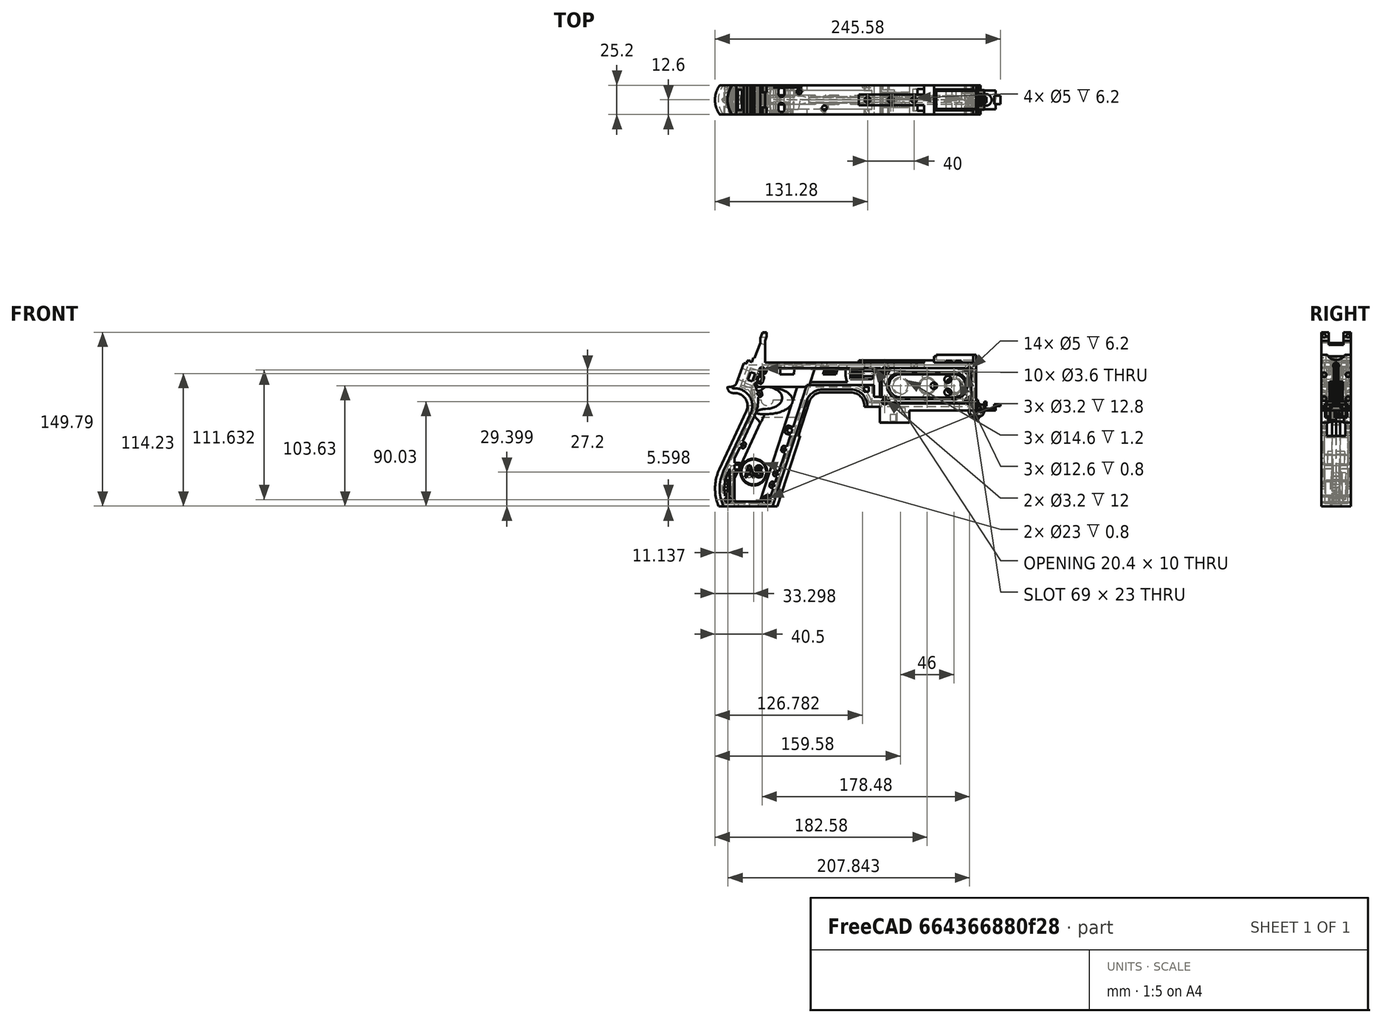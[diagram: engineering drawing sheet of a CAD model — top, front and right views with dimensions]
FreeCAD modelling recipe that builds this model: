
FCSTD DOCUMENT  (FreeCAD 1.0R39319 (Git))
Label: PICON-OF_ver_63
License: All rights reserved
LicenseURL: https://en.wikipedia.org/wiki/All_rights_reserved
objects: Sketcher::SketchObject×132, Part::Extrusion×66, Part::Cut×51, PartDesign::Pad×34, PartDesign::Pocket×21, PartDesign::Chamfer×15, PartDesign::Body×11, PartDesign::Fillet×6, Part::MultiFuse×5, Part::Part2DObjectPython×4, PartDesign::SubtractivePipe×4, PartDesign::SubtractiveLoft×4, PartDesign::Plane×3, PartDesign::SubShapeBinder×2, Part::Sweep×1, PartDesign::ShapeBinder×1, Mesh::Feature×1, PartDesign::Point×1, PartDesign::Groove×1
note: 664 computed .brp shape members not serialized (recipe doc carries the construction recipe); baked Part::Feature solids carry a one-line shape summary decoded from their .brp

FEATURE [Sketcher::SketchObject] Sketch  label="corpo principale"
  ArcFitTolerance = 1e-06
  AttacherType = Attacher::AttachEngine3D
  AttachmentSupport = -> [XZ_Plane]
  FullyConstrained = true
  MakeInternals = false
  MapMode = 5
  Placement = pos=(0,0,0) rot=(1,0,0;1.5708rad)
  sketch-geometry (65):
    g0: LineSegment StartX=0 StartY=0 StartZ=0 EndX=-57.2 EndY=0 EndZ=0
    g1: LineSegment StartX=-57.2 StartY=0 StartZ=0 EndX=-57.2 EndY=-10.4 EndZ=0
    g2: LineSegment StartX=-57.2 StartY=-10.4 StartZ=0 EndX=-82.8 EndY=-10.4 EndZ=0
    g3: LineSegment StartX=-82.8 StartY=-10.4 StartZ=0 EndX=-82.8 EndY=3.2 EndZ=0
    g4: LineSegment StartX=-82.8 StartY=3.2 StartZ=0 EndX=-93.6 EndY=3.2 EndZ=0
    g5: LineSegment StartX=-93.6 StartY=3.2 StartZ=0 EndX=-93.6 EndY=4 EndZ=0
    g6: LineSegment StartX=-107.6 StartY=18 StartZ=0 EndX=-132.428 EndY=18 EndZ=0
    g7: LineSegment StartX=-145.743 StartY=8.32624 StartZ=0 EndX=-175.232 EndY=-82.4316 EndZ=0
    g8: LineSegment StartX=-175.232 StartY=-82.4316 StartZ=0 EndX=-217.232 EndY=-82.4316 EndZ=0
    g9: LineSegment StartX=-217.232 StartY=-52.1862 StartZ=0 EndX=-193.988 EndY=-2.33927 EndZ=0
    g10: LineSegment StartX=-206.196 StartY=23.0857 StartZ=0 EndX=-199.861 EndY=40.4914 EndZ=0
    g11: LineSegment StartX=-199.861 StartY=40.4914 StartZ=0 EndX=-197.061 EndY=40.4914 EndZ=0
    g12: LineSegment StartX=-197.061 StartY=40.4914 StartZ=0 EndX=-197.061 EndY=42.8914 EndZ=0
    g13: LineSegment StartX=-197.061 StartY=42.8914 StartZ=0 EndX=-194.261 EndY=42.8914 EndZ=0
    g14: LineSegment StartX=-194.261 StartY=42.8914 StartZ=0 EndX=-194.535 EndY=42.1397 EndZ=0
    g15: LineSegment StartX=-194.535 StartY=42.1397 StartZ=0 EndX=-193.031 EndY=41.5924 EndZ=0
    g16: LineSegment StartX=-193.031 StartY=41.5924 StartZ=0 EndX=-191.663 EndY=45.3512 EndZ=0
    g17: LineSegment StartX=-191.663 StartY=45.3512 StartZ=0 EndX=-190.536 EndY=44.9408 EndZ=0
    g18: LineSegment StartX=-190.536 StartY=44.9408 StartZ=0 EndX=-185.747 EndY=58.0965 EndZ=0
    g19: LineSegment StartX=-185.747 StartY=58.0965 StartZ=0 EndX=-185.747 EndY=62.0965 EndZ=0
    g20: LineSegment StartX=-185.747 StartY=62.0965 StartZ=0 EndX=-183.832 EndY=67.3588 EndZ=0
    g21: LineSegment StartX=-183.832 StartY=67.3588 StartZ=0 EndX=-180.232 EndY=67.3588 EndZ=0
    g22: LineSegment StartX=-180.232 StartY=67.3588 StartZ=0 EndX=-180.232 EndY=63.7588 EndZ=0
    g23: LineSegment StartX=-180.232 StartY=63.7588 StartZ=0 EndX=-181.6 EndY=60 EndZ=0
    g24: LineSegment StartX=-181.6 StartY=60 StartZ=0 EndX=-181.6 EndY=41.2 EndZ=0
    g25: LineSegment StartX=-181.6 StartY=41.2 StartZ=0 EndX=-100.8 EndY=41.2 EndZ=0
    g26: LineSegment StartX=-36 StartY=43.2 StartZ=0 EndX=-36 EndY=41.2 EndZ=0
    g27: LineSegment StartX=0 StartY=48 StartZ=0 EndX=0 EndY=0 EndZ=0
    g28: LineSegment StartX=-209.901 StartY=19.85 StartZ=0 EndX=-209.901 EndY=20.1 EndZ=0
    g29: LineSegment StartX=-208.001 StartY=22 StartZ=0 EndX=-207.747 EndY=22 EndZ=0
    g30: LineSegment StartX=-207.583 StartY=19 StartZ=0 EndX=-209.051 EndY=19 EndZ=0
    g31: ArcOfCircle CenterX=-208.001 CenterY=20.1 CenterZ=0 NormalX=0 NormalY=0 NormalZ=1 AngleXU=0 Radius=1.9 StartAngle=1.5708 EndAngle=3.14159
    g32: GeomPoint [constr] X=-209.901 Y=22 Z=0
    g33: ArcOfCircle CenterX=-209.051 CenterY=19.85 CenterZ=0 NormalX=0 NormalY=0 NormalZ=1 AngleXU=0 Radius=0.85 StartAngle=3.14159 EndAngle=4.71239
    g34: GeomPoint [constr] X=-209.901 Y=19 Z=0
    g35: ArcOfCircle CenterX=-207.747 CenterY=23.65 CenterZ=0 NormalX=0 NormalY=0 NormalZ=1 AngleXU=0 Radius=1.65 StartAngle=4.71239 EndAngle=5.93412
    g36: GeomPoint [constr] X=-206.591 Y=22 Z=0
    g37: LineSegment StartX=-4 StartY=6 StartZ=0 EndX=-4 EndY=36.4 EndZ=0
    g38: LineSegment StartX=-4 StartY=36.4 StartZ=0 EndX=-185.2 EndY=36.4 EndZ=0
    g39: LineSegment StartX=-185.2 StartY=36.4 StartZ=0 EndX=-190.441 EndY=22 EndZ=0
    g40: LineSegment StartX=-214.575 StartY=-78.4316 StartZ=0 EndX=-178.142 EndY=-78.4316 EndZ=0
    g41: LineSegment StartX=-178.142 StartY=-78.4316 StartZ=0 EndX=-145.51 EndY=22 EndZ=0
    g42: LineSegment StartX=-145.51 StartY=22 StartZ=0 EndX=-87.91 EndY=22 EndZ=0
    g43: LineSegment StartX=-87.91 StartY=22 StartZ=0 EndX=-87.91 EndY=11.6 EndZ=0
    g44: LineSegment StartX=-87.91 StartY=11.6 StartZ=0 EndX=-80.11 EndY=11.6 EndZ=0
    g45: LineSegment StartX=-80.11 StartY=11.6 StartZ=0 EndX=-80.11 EndY=6 EndZ=0
    g46: LineSegment StartX=-80.11 StartY=6 StartZ=0 EndX=-4 EndY=6 EndZ=0
    g47: LineSegment StartX=-190.363 StartY=-4.02975 StartZ=0 EndX=-213.607 EndY=-53.8767 EndZ=0
    g48: ArcOfCircle CenterX=-132.428 CenterY=4 CenterZ=0 NormalX=0 NormalY=0 NormalZ=1 AngleXU=0 Radius=14 StartAngle=1.5708 EndAngle=2.82743
    g49: GeomPoint [constr] X=-142.6 Y=18 Z=0
    g50: ArcOfCircle CenterX=-107.6 CenterY=4 CenterZ=0 NormalX=0 NormalY=0 NormalZ=1 AngleXU=0 Radius=14 StartAngle=0 EndAngle=1.5708
    g51: GeomPoint [constr] X=-93.6 Y=18 Z=0
    g52: ArcOfCircle CenterX=-184.801 CenterY=-67.3089 CenterZ=0 NormalX=0 NormalY=0 NormalZ=1 AngleXU=0 Radius=35.7833 StartAngle=2.70526 EndAngle=3.57792
    g53: ArcOfCircle CenterX=-207.583 CenterY=4 CenterZ=0 NormalX=0 NormalY=0 NormalZ=1 AngleXU=0 Radius=15 StartAngle=5.84685 EndAngle=7.85398
    g54: LineSegment [constr] StartX=-213.607 StartY=-53.8767 StartZ=0 EndX=-217.232 EndY=-52.1862 EndZ=0
    g55: ArcOfCircle CenterX=-184.801 CenterY=-67.3089 CenterZ=0 NormalX=0 NormalY=0 NormalZ=1 AngleXU=0 Radius=31.7833 StartAngle=2.70526 EndAngle=3.49911
    g56: ArcOfCircle CenterX=-218.095 CenterY=8.90192 CenterZ=0 NormalX=0 NormalY=0 NormalZ=1 AngleXU=0 Radius=30.5989 StartAngle=5.84685 EndAngle=6.72553
    g57: LineSegment StartX=-44.6 StartY=43.2 StartZ=0 EndX=-36 EndY=43.2 EndZ=0
    g58: LineSegment StartX=-100.8 StartY=41.2 StartZ=0 EndX=-44.6 EndY=41.2 EndZ=0
    g59: LineSegment StartX=-44.6 StartY=41.2 StartZ=0 EndX=-44.6 EndY=43.2 EndZ=0
    g60: LineSegment StartX=-2.4 StartY=48 StartZ=0 EndX=0 EndY=48 EndZ=0
    g61: LineSegment StartX=-36 StartY=41.2 StartZ=0 EndX=-2.4 EndY=41.2 EndZ=0
    g62: LineSegment StartX=-2.4 StartY=41.2 StartZ=0 EndX=-2.4 EndY=48 EndZ=0
    g63: LineSegment [constr] StartX=-181.6 StartY=36.4 StartZ=0 EndX=-152.209 EndY=36.4 EndZ=0
    g64: LineSegment [constr] StartX=-181.6 StartY=36.4 StartZ=0 EndX=-130.41 EndY=36.4 EndZ=0
  constraints (183):
    c: Coincident(g-1,g0)
    c: PointOnObject(g0,g-1)
    c: Coincident(g0,g1)
    c: Vertical(g1)
    c: Coincident(g1,g2)
    c: Horizontal(g2)
    c: Coincident(g2,g3)
    c: Vertical(g3)
    c: Coincident(g3,g4)
    c: Coincident(g4,g5)
    c: Vertical(g5)
    c: Horizontal(g6)
    c: Coincident(g7,g8)
    c: Horizontal(g8)
    c: Coincident(g10,g11)
    c: Horizontal(g11)
    c: Coincident(g11,g12)
    c: Vertical(g12)
    c: Coincident(g12,g13)
    c: Horizontal(g13)
    c: Coincident(g13,g14)
    c: Coincident(g14,g15)
    c: Coincident(g15,g16)
    c: Coincident(g16,g17)
    c: Coincident(g17,g18)
    c: Coincident(g18,g19)
    c: Vertical(g19)
    c: Coincident(g19,g20)
    c: Coincident(g20,g21)
    c: Horizontal(g21)
    c: Coincident(g21,g22)
    c: Vertical(g22)
    c: Coincident(g22,g23)
    c: Coincident(g23,g24)
    c: Vertical(g24)
    c: Coincident(g24,g25)
    c: Horizontal(g25)
    c: Coincident(g57,g26)
    c: Vertical(g26)
    c: Coincident(g26,g61)
    c: PointOnObject(g60,g-2)
    c: Coincident(g60,g27)
    c: Coincident(g27,g0)
    c: DistanceY(g27,g27) = 48
    c: DistanceY(g1,g1) = 10.4
    c: DistanceX(g0,g0) = 57.2
    c: DistanceX(g2,g2) = 25.6
    c: Horizontal(g4)
    c: DistanceY(g3,g3) = 13.6
    c: DistanceX(g4,g4) = 10.8
    c: DistanceY(g5,g51) = 14.8
    c: DistanceX(g49,g51) = 49
    c: Distance(g7,g49) = 105.6
    c: DistanceX(g61,g60) = 36
    c: DistanceX(g25,g25) = 80.8
    c: DistanceY(g24,g24) = 18.8
    c: DistanceY(g22,g22) = 3.6
    c: Distance(g23) = 4
    c: Angle(g-1,g23) = 1.22173
    c: DistanceX(g21,g21) = 3.6
    c: Distance(g20) = 5.6
    c: Angle(g-1,g20) = 1.22173
    c: DistanceY(g19,g19) = 4
    c: Distance(g18) = 14
    c: Angle(g-1,g18) = 1.22173
    c: Distance(g17) = 1.2
    c: Distance(g16) = 4
    c: Angle(g16) = 1.22173
    c: Perpendicular(g18,g17)
    c: Distance(g15) = 1.6
    c: Perpendicular(g16,g15)
    c: Distance(g14) = 0.8
    c: DistanceX(g13,g13) = 2.8
    c: Perpendicular(g15,g14)
    c: DistanceY(g12,g12) = 2.4
    c: DistanceX(g11,g11) = 2.8
    c: Distance(g9) = 55
    c: Angle(g9,g-1) = 2.00713
    c: Horizontal(g29)
    c: Vertical(g28)
    c: Horizontal(g30)
    c: PointOnObject(g32,g29)
    c: PointOnObject(g32,g28)
    c: Tangent(g29,g31) = 1.5708
    c: Tangent(g28,g31) = 1.5708
    c: PointOnObject(g34,g28)
    c: PointOnObject(g34,g30)
    c: Tangent(g28,g33) = 1.5708
    c: Tangent(g30,g33) = 1.5708
    c: PointOnObject(g36,g29)
    c: PointOnObject(g36,g10)
    c: Tangent(g29,g35) = -1.5708
    c: Tangent(g10,g35) = -1.5708
    c: Angle(g-1,g10) = 1.22173
    c: Radius(g35) = 1.65
    c: Vertical(g37)
    c: Coincident(g37,g38)
    c: Horizontal(g38)
    c: Coincident(g38,g39)
    c: Horizontal(g40)
    c: Coincident(g40,g41)
    c: Coincident(g41,g42)
    c: Horizontal(g42)
    c: Coincident(g42,g43)
    c: Vertical(g43)
    c: Coincident(g43,g44)
    c: Horizontal(g44)
    c: Coincident(g44,g45)
    c: Vertical(g45)
    c: Coincident(g45,g46)
    c: Coincident(g46,g37)
    c: Horizontal(g46)
    c: DistanceY(g0,g37) = 6
    c: DistanceX(g37,g0) = 4
    c: DistanceY(g37,g25) = 4.8
    c: DistanceX(g38,g38) = 181.2
    c: DistanceX(g42,g42) = 57.6
    c: DistanceY(g49,g41) = 4
    c: DistanceX(g41,g49) = 2.91
    c: DistanceY(g43,g43) = 10.4
    c: DistanceX(g44,g44) = 7.8
    c: DistanceY(g7,g40) = 4
    c: Distance(g47) = 55
    c: Angle(g-1,g39) = 1.22173
    c: PointOnObject(g49,g7)
    c: PointOnObject(g49,g6)
    c: Tangent(g7,g48) = -1.5708
    c: Tangent(g6,g48) = -1.5708
    c: PointOnObject(g51,g5)
    c: PointOnObject(g51,g6)
    c: Tangent(g5,g50) = -1.5708
    c: Tangent(g6,g50) = -1.5708
    c: Radius(g50) = 14
    c: Radius(g48) = 14
    c: DistanceX(g8,g8) = 42
    c: Angle(g7,g-1) = 1.88496
    c: Parallel(g41,g7)
    c: Parallel(g47,g9)
    c: Coincident(g52,g8)
    c: Tangent(g52,g9) = 1.5708
    c: DistanceX(g9,g8) = 0
    c: Tangent(g53,g9) = -1.5708
    c: Tangent(g53,g30) = -1.5708
    c: Diameter(g53) = 30
    c: DistanceY(g53,g0) = -4
    c: Coincident(g54,g47)
    c: Distance(g54) = 4
    c: Coincident(g54,g9)
    c: Coincident(g55,g40)
    c: Tangent(g55,g47) = -1.5708
    c: Coincident(g52,g55)
    c: Coincident(g56,g39)
    c: Tangent(g56,g47) = 1.5708
    c: Horizontal(g57)
    c: DistanceX(g57,g57) = 8.6
    c: Coincident(g58,g25)
    c: Horizontal(g58)
    c: Coincident(g59,g58)
    c: Vertical(g59)
    c: DistanceY(g58,g57) = 2
    c: DistanceX(g58,g58) = 56.2
    c: Coincident(g59,g57)
    c: DistanceY(g41,g36) = 0
    c: DistanceY(g36,g39) = 0
    c: DistanceY(g28,g28) = 0.25
    c: DistanceX(g30,g36) = 2.46
    c: DistanceX(g28,g29) = 1.9
    c: Coincident(g62,g60)
    c: Horizontal(g60)
    c: DistanceX(g62,g27) = 2.4
    c: Coincident(g61,g62)
    c: DistanceY(g26,g26) = 2
    c: Vertical(g62)
    c: DistanceY(g61,g60) = 6.8
    c: Horizontal(g61)
    c: Distance(g63) = 29.391
    c: PointOnObject(g63,g38)
    c: PointOnObject(g63,g38)
    c: Distance(g64) = 51.19
    c: PointOnObject(g64,g38)
    c: PointOnObject(g64,g38)
    c: DistanceX(g24,g63) = 0
    c: DistanceX(g24,g64) = 0
FEATURE [Part::Extrusion] Extrude  label="Extrude corpo principale"
  Base = -> Sketch
  Dir = (0,-1,2e-16)
  DirMode = 2
  FaceMakerClass = Part::FaceMakerBullseye
  FaceMakerMode = 3
  LengthFwd = 25.2
  LengthRev = 12.6
  Solid = true
  Symmetric = true
FEATURE [Sketcher::SketchObject] Sketch002  label="scavo grilletto"
  ArcFitTolerance = 1e-06
  AttachmentSupport = -> [XZ_Plane]
  ExternalGeometry = -> [Sketch]
  FullyConstrained = true
  MakeInternals = false
  MapMode = 5
  Placement = pos=(0,0,0) rot=(1,0,0;1.5708rad)
  sketch-geometry (4):
    g0: LineSegment StartX=-89.51 StartY=22 StartZ=0 EndX=-152.71 EndY=22 EndZ=0
    g1: LineSegment StartX=-152.71 StartY=22 StartZ=0 EndX=-167.006 EndY=-22 EndZ=0
    g2: LineSegment StartX=-167.006 StartY=-22 StartZ=0 EndX=-89.51 EndY=-22 EndZ=0
    g3: LineSegment StartX=-89.51 StartY=-22 StartZ=0 EndX=-89.51 EndY=22 EndZ=0
  constraints (12):
    c: Horizontal(g0)
    c: Coincident(g0,g1)
    c: Coincident(g1,g2)
    c: Horizontal(g2)
    c: Coincident(g2,g3)
    c: Coincident(g3,g0)
    c: Vertical(g3)
    c: Angle(g1,g0) = 1.88496
    c: DistanceY(g3,g3) = 44
    c: DistanceX(g0,g0) = 63.2
    c: DistanceX(g0,g-3) = 1.6
    c: DistanceY(g-3,g0) = 0
FEATURE [Sketcher::SketchObject] Sketch004  label="traiettoria arrotondamento impugnatura anteriore"
  ArcFitTolerance = 1e-06
  AttachmentSupport = -> [XZ_Plane]
  ExternalGeometry = -> [Sketch]
  FullyConstrained = true
  MakeInternals = false
  MapMode = 5
  Placement = pos=(0,0,0) rot=(1,0,0;1.5708rad)
  sketch-geometry (13):
    g0: LineSegment StartX=-175.232 StartY=-82.4316 StartZ=0 EndX=-145.743 EndY=8.32624 EndZ=0
    g1: LineSegment StartX=-93.6 StartY=3.2 StartZ=0 EndX=-93.6 EndY=4 EndZ=0
    g2: LineSegment StartX=-132.428 StartY=18 StartZ=0 EndX=-107.6 EndY=18 EndZ=0
    g3: ArcOfCircle CenterX=-132.428 CenterY=4 CenterZ=0 NormalX=0 NormalY=0 NormalZ=1 AngleXU=0 Radius=14 StartAngle=1.5708 EndAngle=2.82743
    g4: ArcOfCircle CenterX=-107.6 CenterY=4 CenterZ=0 NormalX=0 NormalY=0 NormalZ=1 AngleXU=0 Radius=14 StartAngle=0 EndAngle=1.5708
    g5: LineSegment StartX=-175.232 StartY=-82.4316 StartZ=0 EndX=-217.232 EndY=-82.4316 EndZ=0
    g6: LineSegment StartX=-217.232 StartY=-52.1862 StartZ=0 EndX=-193.988 EndY=-2.33927 EndZ=0
    g7: LineSegment StartX=-209.051 StartY=19 StartZ=0 EndX=-207.583 EndY=19 EndZ=0
    g8: LineSegment StartX=-209.901 StartY=20.1 StartZ=0 EndX=-209.901 EndY=19.85 EndZ=0
    g9: ArcOfCircle CenterX=-184.801 CenterY=-67.3089 CenterZ=0 NormalX=0 NormalY=0 NormalZ=1 AngleXU=0 Radius=35.7833 StartAngle=2.70526 EndAngle=3.57792
    g10: ArcOfCircle CenterX=-207.583 CenterY=4 CenterZ=0 NormalX=0 NormalY=0 NormalZ=1 AngleXU=0 Radius=15 StartAngle=5.84685 EndAngle=7.85398
    g11: ArcOfCircle CenterX=-209.051 CenterY=19.85 CenterZ=0 NormalX=0 NormalY=0 NormalZ=1 AngleXU=0 Radius=0.85 StartAngle=3.14159 EndAngle=4.71239
    g12: ArcOfCircle CenterX=-208.001 CenterY=20.1 CenterZ=0 NormalX=0 NormalY=0 NormalZ=1 AngleXU=0 Radius=1.9 StartAngle=1.5708 EndAngle=3.14159
  constraints (26):
    c: Coincident(g0,g-3)
    c: Coincident(g0,g-6)
    c: Coincident(g1,g-8)
    c: Coincident(g1,g-7)
    c: Coincident(g2,g-5)
    c: Coincident(g2,g-4)
    c: Coincident(g3,g2)
    c: Tangent(g3,g0) = 1.5708
    c: Coincident(g4,g1)
    c: Tangent(g4,g2) = 1.5708
    c: Coincident(g5,g0)
    c: Coincident(g5,g-9)
    c: Coincident(g6,g-12)
    c: Coincident(g6,g-11)
    c: Coincident(g7,g-15)
    c: Coincident(g7,g-14)
    c: Coincident(g8,g-16)
    c: Coincident(g8,g-17)
    c: Tangent(g9,g6) = 1.5708
    c: Coincident(g9,g5)
    c: Coincident(g10,g7)
    c: Tangent(g10,g6) = -1.5708
    c: Tangent(g11,g7) = -1.5708
    c: Coincident(g11,g8)
    c: Tangent(g12,g8) = -1.5708
    c: Coincident(g12,g-17)
FEATURE [PartDesign::Plane] DatumPlane  label="Piano per disegno arrotondamento impugnatura"
  AttachmentSupport = -> [Sketch]
  Length = 73.6581
  MapMode = 7
  Placement = pos=(-145.743,1.8e-15,8.32624) rot=(0.154555,0.154555,0.97582;1.59527rad)
  ResizeMode = 0
  Width = 303.511
FEATURE [Sketcher::SketchObject] Sketch005  label="forma arrotondamento impugnatura anteriore"
  ArcFitTolerance = 1e-06
  AttachmentSupport = -> [DatumPlane]
  FullyConstrained = true
  MakeInternals = false
  MapMode = 5
  Placement = pos=(-145.743,1.8e-15,8.32624) rot=(0.154555,0.154555,0.97582;1.59527rad)
  sketch-geometry (5):
    g0: GeomPoint [constr] X=0 Y=-4 Z=0
    g1: GeomPoint [constr] X=-12.6 Y=7.1e-15 Z=0
    g2: GeomPoint [constr] X=12.6 Y=4.97e-14 Z=0
    g3: LineSegment StartX=-12.6 StartY=7.1e-15 StartZ=0 EndX=12.6 EndY=4.97e-14 EndZ=0
    g4: ArcOfCircle CenterX=-3.88e-14 CenterY=17.845 CenterZ=0 NormalX=0 NormalY=0 NormalZ=1 AngleXU=0 Radius=21.845 StartAngle=4.09759 EndAngle=5.32718
  constraints (11):
    c: DistanceY(g0,g-1) = 4
    c: DistanceX(g-1,g0) = 0
    c: DistanceX(g1,g-1) = 12.6
    c: DistanceX(g-1,g2) = 12.6
    c: DistanceY(g-1,g2) = 0
    c: DistanceY(g-1,g1) = 0
    c: Coincident(g3,g1)
    c: Coincident(g3,g2)
    c: Coincident(g4,g1)
    c: Coincident(g4,g2)
    c: PointOnObject(g0,g4)
FEATURE [Part::Sweep] Sweep  label="Sweep impugnatura"
  Frenet = true
  Sections = -> [Sketch005]
  Solid = true
  Spine = -> Sketch [Edge32,Edge33,Edge34,Edge35,Edge36,Edge37,Edge38,Edge39,Edge40,Edge41,Edge42,Edge43,Edge44]
  Transition = 1
FEATURE [Sketcher::SketchObject] Sketch008  label="buchi e pulizie varie"
  ArcFitTolerance = 1e-06
  AttachmentSupport = -> [XZ_Plane]
  ExternalGeometry = -> [Sketch]
  FullyConstrained = true
  MakeInternals = false
  MapMode = 5
  Placement = pos=(0,0,0) rot=(1,0,0;1.5708rad)
  sketch-geometry (26):
    g0: LineSegment StartX=-96.278 StartY=20.155 StartZ=0 EndX=-92.278 EndY=20.155 EndZ=0
    g1: LineSegment StartX=-92.278 StartY=20.155 StartZ=0 EndX=-92.278 EndY=16.155 EndZ=0
    g2: LineSegment StartX=-92.278 StartY=16.155 StartZ=0 EndX=-96.278 EndY=16.155 EndZ=0
    g3: LineSegment StartX=-96.278 StartY=16.155 StartZ=0 EndX=-96.278 EndY=20.155 EndZ=0
    g4: LineSegment StartX=-222.232 StartY=-82.4316 StartZ=0 EndX=-170.232 EndY=-82.4316 EndZ=0
    g5: LineSegment StartX=-170.232 StartY=-82.4316 StartZ=0 EndX=-170.232 EndY=-86.4316 EndZ=0
    g6: LineSegment StartX=-170.232 StartY=-86.4316 StartZ=0 EndX=-222.232 EndY=-86.4316 EndZ=0
    g7: LineSegment StartX=-222.232 StartY=-86.4316 StartZ=0 EndX=-222.232 EndY=-82.4316 EndZ=0
    g8: LineSegment StartX=-213.901 StartY=20.1 StartZ=0 EndX=-213.901 EndY=26 EndZ=0
    g9: LineSegment StartX=-213.901 StartY=26 StartZ=0 EndX=-206.196 EndY=26 EndZ=0
    g10: LineSegment StartX=-17.4 StartY=42.8 StartZ=0 EndX=-12.4 EndY=42.8 EndZ=0
    g11: LineSegment StartX=-12.4 StartY=42.8 StartZ=0 EndX=-12.4 EndY=41.2 EndZ=0
    g12: LineSegment StartX=-12.4 StartY=41.2 StartZ=0 EndX=-17.4 EndY=41.2 EndZ=0
    g13: LineSegment StartX=-17.4 StartY=41.2 StartZ=0 EndX=-17.4 EndY=42.8 EndZ=0
    g14: LineSegment StartX=-25.9 StartY=42.8 StartZ=0 EndX=-20.9 EndY=42.8 EndZ=0
    g15: LineSegment StartX=-20.9 StartY=42.8 StartZ=0 EndX=-20.9 EndY=41.2 EndZ=0
    g16: LineSegment StartX=-20.9 StartY=41.2 StartZ=0 EndX=-25.9 EndY=41.2 EndZ=0
    g17: LineSegment StartX=-25.9 StartY=41.2 StartZ=0 EndX=-25.9 EndY=42.8 EndZ=0
    g18: GeomPoint [constr] X=-206.196 Y=23.0857 Z=0
    g19: GeomPoint [constr] X=-213.901 Y=20.1 Z=0
    g20: BSplineCurve PolesCount=4 KnotsCount=2 Degree=3 IsPeriodic=0
    g21-g24: Circle [constr] x4 (B-spline internal-alignment scaffolding for g20; pole/knot coordinates omitted)
    g25: LineSegment StartX=-206.196 StartY=26 StartZ=0 EndX=-206.196 EndY=23.0857 EndZ=0
  constraints (73):
    c: Horizontal(g0)
    c: Coincident(g1,g0)
    c: Vertical(g1)
    c: Coincident(g2,g1)
    c: Horizontal(g2)
    c: Coincident(g3,g2)
    c: Coincident(g3,g0)
    c: Vertical(g3)
    c: DistanceX(g0,g-4) = 4.368
    c: DistanceY(g0,g-4) = 1.845
    c: DistanceY(g1,g1) = 4
    c: DistanceX(g2,g2) = 4
    c: Horizontal(g4)
    c: Coincident(g5,g4)
    c: Vertical(g5)
    c: Coincident(g6,g5)
    c: Horizontal(g6)
    c: Coincident(g7,g6)
    c: Coincident(g7,g4)
    c: Vertical(g7)
    c: DistanceY(g7,g7) = 4
    c: DistanceX(g4,g-5) = 5
    c: DistanceX(g-5,g4) = 5
    c: DistanceY(g4,g-5) = 0
    c: Coincident(g9,g8)
    c: Parallel(g9,g-6)
    c: DistanceX(g8,g-8) = 4
    c: Horizontal(g10)
    c: Coincident(g11,g10)
    c: Vertical(g11)
    c: Coincident(g12,g11)
    c: Horizontal(g12)
    c: Coincident(g13,g12)
    c: Coincident(g13,g10)
    c: Vertical(g13)
    c: Horizontal(g14)
    c: Coincident(g15,g14)
    c: Vertical(g15)
    c: Coincident(g16,g15)
    c: Horizontal(g16)
    c: Coincident(g17,g16)
    c: Coincident(g17,g14)
    c: Vertical(g17)
    c: DistanceY(g11,g10) = 1.6
    c: DistanceX(g10,g10) = 5
    c: DistanceY(g15,g14) = 1.6
    c: DistanceX(g14,g14) = 5
    c: DistanceX(g15,g12) = 3.5
    c: DistanceX(g11,g-9) = 10
    c: DistanceY(g-9,g11) = 0
    c: DistanceY(g-9,g15) = 0
    c: Perpendicular(g8,g9)
    c: DistanceY(g-7,g9) = 4
    c: DistanceY(g8,g-8) = 0
    c: InternalAlignment(g18,g20)
    c: InternalAlignment(g19,g20)
    c: InternalAlignment(g21,g20)
    c: Weight(g21) = 1
    c: InternalAlignment(g22,g20)
    c: Equal(g22,g21)
    c: InternalAlignment(g23,g20)
    c: Equal(g23,g21)
    c: InternalAlignment(g24,g20)
    c: Equal(g24,g21)
    c: Coincident(g18,g-12)
    c: Coincident(g19,g8)
    c: Coincident(g25,g9)
    c: Coincident(g25,g20)
    c: Vertical(g25)
    c: DistanceY(g20,g23) = 0
    c: DistanceY(g22,g18) = 2.26
    c: DistanceX(g22,g18) = 0.93
    c: DistanceX(g20,g23) = 2.9
FEATURE [Part::Extrusion] Extrude004  label="Extrude Buchi e pulizie varie"
  Base = -> Sketch008
  Dir = (0,-1,2e-16)
  DirMode = 2
  FaceMakerClass = Part::FaceMakerBullseye
  FaceMakerMode = 3
  LengthFwd = 25.2
  LengthRev = 0
  Solid = true
  Symmetric = true
FEATURE [Sketcher::SketchObject] Sketch009  label="rinforzi"
  ArcFitTolerance = 1e-06
  AttachmentSupport = -> [XZ_Plane]
  ExternalGeometry = -> [Sketch]
  FullyConstrained = true
  MakeInternals = false
  MapMode = 5
  Placement = pos=(0,0,0) rot=(1,0,0;1.5708rad)
  sketch-geometry (9):
    g0: LineSegment StartX=-87.91 StartY=22 StartZ=0 EndX=-87.91 EndY=36.4 EndZ=0
    g1: LineSegment StartX=-87.91 StartY=36.4 StartZ=0 EndX=-97.91 EndY=36.4 EndZ=0
    g2: LineSegment StartX=-97.91 StartY=36.4 StartZ=0 EndX=-97.91 EndY=22 EndZ=0
    g3: LineSegment StartX=-97.91 StartY=22 StartZ=0 EndX=-87.91 EndY=22 EndZ=0
    g4: LineSegment StartX=-149.713 StartY=9.06563 StartZ=0 EndX=-154.586 EndY=-5.93437 EndZ=0
    g5: LineSegment StartX=-154.586 StartY=-5.93437 StartZ=0 EndX=-191.863 EndY=-5.93437 EndZ=0
    g6: LineSegment StartX=-191.863 StartY=-5.93437 StartZ=0 EndX=-191.863 EndY=9.06563 EndZ=0
    g7: LineSegment StartX=-191.863 StartY=9.06563 StartZ=0 EndX=-149.713 EndY=9.06563 EndZ=0
    g8: LineSegment [constr] StartX=-145.51 StartY=22 StartZ=0 EndX=-149.713 EndY=9.06563 EndZ=0
  constraints (25):
    c: Vertical(g0)
    c: Coincident(g1,g0)
    c: Horizontal(g1)
    c: Coincident(g2,g1)
    c: Vertical(g2)
    c: Coincident(g3,g2)
    c: Coincident(g3,g0)
    c: Horizontal(g3)
    c: Coincident(g0,g-4)
    c: DistanceX(g3,g3) = 10
    c: DistanceY(g0,g-3) = 0
    c: Coincident(g5,g4)
    c: Horizontal(g5)
    c: Coincident(g6,g5)
    c: Vertical(g6)
    c: Coincident(g7,g6)
    c: Coincident(g7,g4)
    c: Horizontal(g7)
    c: Distance(g8) = 13.6
    c: Parallel(g-6,g8)
    c: Coincident(g-6,g8)
    c: Parallel(g4,g-6)
    c: DistanceY(g4,g4) = 15
    c: Coincident(g4,g8)
    c: DistanceX(g-5,g5) = -1.5
FEATURE [Part::Extrusion] Extrude001  label="Extrude scavo grilletto"
  Base = -> Sketch002
  Dir = (0,-1,2e-16)
  DirMode = 2
  FaceMakerClass = Part::FaceMakerBullseye
  FaceMakerMode = 3
  LengthFwd = 16
  LengthRev = 0
  Solid = true
  Symmetric = true
FEATURE [Part::Extrusion] Extrude005  label="Extrude Rinforzi"
  Base = -> Sketch009
  Dir = (0,-1,2e-16)
  DirMode = 2
  FaceMakerClass = Part::FaceMakerBullseye
  FaceMakerMode = 3
  LengthFwd = 2
  LengthRev = 0
  Placement = pos=(0,12.6,0) rot=(0,0,1;0rad)
  Solid = true
  Symmetric = false
FEATURE [PartDesign::ShapeBinder] CopyCut
  TraceSupport = false
FEATURE [PartDesign::Plane] DatumPlane001
  AttachmentSupport = -> [CopyCut]
  Length = 283.944
  MapMode = 5
  Placement = pos=(0,12.6,0) rot=(0,0.707107,0.707107;3.14159rad)
  ResizeMode = 0
  Width = 188.15
FEATURE [Sketcher::SketchObject] Sketch010  label="buco neopixel"
  ArcFitTolerance = 1e-06
  AttachmentSupport = -> [XZ_Plane]
  ExternalGeometry = -> [Sketch]
  FullyConstrained = true
  MakeInternals = false
  MapMode = 5
  Placement = pos=(0,0,0) rot=(1,0,0;1.5708rad)
  sketch-geometry (5):
    g0: LineSegment [constr] StartX=-199.861 StartY=40.4914 StartZ=0 EndX=-201.368 EndY=36.3521 EndZ=0
    g1: LineSegment StartX=-201.368 StartY=36.3521 StartZ=0 EndX=-204.932 EndY=26.5605 EndZ=0
    g2: LineSegment StartX=-201.368 StartY=36.3521 StartZ=0 EndX=-180.2 EndY=28.6477 EndZ=0
    g3: LineSegment StartX=-180.2 StartY=28.6477 StartZ=0 EndX=-183.764 EndY=18.8561 EndZ=0
    g4: LineSegment StartX=-183.764 StartY=18.8561 StartZ=0 EndX=-204.932 EndY=26.5605 EndZ=0
  constraints (14):
    c: Parallel(g0,g-3)
    c: Distance(g0) = 4.405
    c: Coincident(g0,g-3)
    c: Coincident(g2,g1)
    c: Coincident(g3,g2)
    c: Coincident(g4,g3)
    c: Coincident(g4,g1)
    c: Parallel(g1,g-3)
    c: Distance(g1) = 10.42
    c: Coincident(g1,g0)
    c: Parallel(g2,g4)
    c: Perpendicular(g1,g2)
    c: DistanceX(g-4,g2) = 5
    c: Parallel(g3,g1)
FEATURE [Part::Extrusion] Extrude006  label="Extrude buco neopixel"
  Base = -> Sketch010
  Dir = (0,-1,2e-16)
  DirMode = 2
  FaceMakerClass = Part::FaceMakerBullseye
  FaceMakerMode = 3
  LengthFwd = 17.2
  LengthRev = 0
  Solid = true
  Symmetric = true
FEATURE [Sketcher::SketchObject] Sketch011  label="fermo grilletto"
  ArcFitTolerance = 1e-06
  AttachmentSupport = -> [XZ_Plane]
  ExternalGeometry = -> [Sketch]
  FullyConstrained = true
  MakeInternals = false
  MapMode = 5
  Placement = pos=(0,0,0) rot=(1,0,0;1.5708rad)
  sketch-geometry (18):
    g0: LineSegment [constr] StartX=-145.51 StartY=22 StartZ=0 EndX=-157.347 EndY=-14.4293 EndZ=0
    g1: LineSegment [constr] StartX=-157.347 StartY=-14.4293 StartZ=0 EndX=-157.841 EndY=-15.951 EndZ=0
    g2: LineSegment StartX=-161.151 StartY=-13.1932 StartZ=0 EndX=-155.825 EndY=-14.9237 EndZ=0
    g3: LineSegment StartX=-163.167 StartY=-14.2205 StartZ=0 EndX=-164.403 EndY=-18.0247 EndZ=0
    g4: LineSegment StartX=-163.376 StartY=-20.0408 StartZ=0 EndX=-158.05 EndY=-21.7713 EndZ=0
    g5: LineSegment StartX=-158.05 StartY=-21.7713 StartZ=0 EndX=-155.825 EndY=-14.9237 EndZ=0
    g6: LineSegment StartX=-161.645 StartY=-14.7149 StartZ=0 EndX=-157.841 EndY=-15.951 EndZ=0
    g7: LineSegment StartX=-157.841 StartY=-15.951 StartZ=0 EndX=-159.077 EndY=-19.7552 EndZ=0
    g8: LineSegment StartX=-159.077 StartY=-19.7552 StartZ=0 EndX=-162.881 EndY=-18.5191 EndZ=0
    g9: LineSegment StartX=-162.881 StartY=-18.5191 StartZ=0 EndX=-161.645 EndY=-14.7149 EndZ=0
    g10: LineSegment [constr] StartX=-161.645 StartY=-14.7149 StartZ=0 EndX=-161.151 EndY=-13.1932 EndZ=0
    g11: LineSegment [constr] StartX=-159.077 StartY=-19.7552 StartZ=0 EndX=-157.555 EndY=-20.2496 EndZ=0
    g12: LineSegment [constr] StartX=-159.077 StartY=-19.7552 StartZ=0 EndX=-159.572 EndY=-21.2769 EndZ=0
    g13: LineSegment [constr] StartX=-161.645 StartY=-14.7149 StartZ=0 EndX=-163.167 EndY=-14.2205 EndZ=0
    g14: ArcOfCircle CenterX=-161.645 CenterY=-14.7149 CenterZ=0 NormalX=0 NormalY=0 NormalZ=1 AngleXU=0 Radius=1.6 StartAngle=1.25664 EndAngle=2.82743
    g15: GeomPoint [constr] X=-162.673 Y=-12.6988 Z=0
    g16: ArcOfCircle CenterX=-162.881 CenterY=-18.5191 CenterZ=0 NormalX=0 NormalY=0 NormalZ=1 AngleXU=0 Radius=1.6 StartAngle=2.82743 EndAngle=4.39823
    g17: GeomPoint [constr] X=-164.897 Y=-19.5464 Z=0
  constraints (48):
    c: Parallel(g0,g-3)
    c: Distance(g0) = 38.304
    c: Coincident(g0,g-3)
    c: Parallel(g1,g-3)
    c: Distance(g1) = 1.6
    c: Coincident(g1,g0)
    c: Coincident(g5,g4)
    c: Coincident(g5,g2)
    c: Coincident(g7,g6)
    c: Coincident(g8,g7)
    c: Coincident(g9,g8)
    c: Coincident(g9,g6)
    c: Parallel(g7,g-3)
    c: Parallel(g9,g7)
    c: Perpendicular(g6,g7)
    c: Parallel(g6,g8)
    c: Distance(g6) = 4
    c: Distance(g9) = 4
    c: Parallel(g5,g7)
    c: Parallel(g9,g3)
    c: Parallel(g2,g6)
    c: Parallel(g4,g8)
    c: Parallel(g13,g6)
    c: Parallel(g10,g9)
    c: Parallel(g11,g8)
    c: Parallel(g12,g7)
    c: Distance(g10) = 1.6
    c: Distance(g13) = 1.6
    c: Distance(g12) = 1.6
    c: Distance(g11) = 1.6
    c: Coincident(g10,g6)
    c: Coincident(g13,g6)
    c: Coincident(g12,g7)
    c: Coincident(g11,g7)
    c: Distance(g10,g15) = 1.6
    c: Distance(g15,g13) = 1.6
    c: Distance(g4,g12) = 1.6
    c: Distance(g4,g11) = 1.6
    c: PointOnObject(g15,g2)
    c: Tangent(g3,g14) = -1.5708
    c: Tangent(g2,g14) = 1.5708
    c: PointOnObject(g17,g4)
    c: PointOnObject(g17,g3)
    c: Tangent(g4,g16) = -1.5708
    c: Tangent(g3,g16) = -1.5708
    c: Equal(g16,g14)
    c: Coincident(g16,g8)
    c: Coincident(g6,g1)
FEATURE [Part::Extrusion] Extrude007  label="Extrude fermo grilletto"
  Base = -> Sketch011
  Dir = (0,-1,2e-16)
  DirMode = 2
  FaceMakerClass = Part::FaceMakerBullseye
  FaceMakerMode = 3
  LengthFwd = 25.2
  LengthRev = 0
  Solid = true
  Symmetric = true
FEATURE [Sketcher::SketchObject] Sketch012  label="buco oled"
  ArcFitTolerance = 1e-06
  AttachmentSupport = -> [XZ_Plane]
  ExternalGeometry = -> [Sketch]
  FullyConstrained = true
  MakeInternals = false
  MapMode = 5
  Placement = pos=(0,0,0) rot=(1,0,0;1.5708rad)
  sketch-geometry (4):
    g0: LineSegment StartX=-185.747 StartY=58.0965 StartZ=0 EndX=-180.232 EndY=56.0891 EndZ=0
    g1: LineSegment StartX=-185.747 StartY=58.0965 StartZ=0 EndX=-185.747 EndY=67.3588 EndZ=0
    g2: LineSegment StartX=-185.747 StartY=67.3588 StartZ=0 EndX=-180.232 EndY=67.3588 EndZ=0
    g3: LineSegment StartX=-180.232 StartY=67.3588 StartZ=0 EndX=-180.232 EndY=56.0891 EndZ=0
  constraints (10):
    c: Coincident(g1,g0)
    c: Coincident(g2,g1)
    c: Coincident(g3,g2)
    c: Coincident(g3,g0)
    c: Parallel(g1,g-5)
    c: Perpendicular(g-3,g0)
    c: Parallel(g2,g-6)
    c: Parallel(g3,g-4)
    c: Coincident(g0,g-5)
    c: Coincident(g2,g-6)
FEATURE [Part::Extrusion] Extrude008  label="Extrude buco oled"
  Base = -> Sketch012
  Dir = (0,-1,2e-16)
  DirMode = 2
  FaceMakerClass = Part::FaceMakerBullseye
  FaceMakerMode = 3
  LengthFwd = 12.8
  LengthRev = 0
  Solid = true
  Symmetric = true
FEATURE [Sketcher::SketchObject] Sketch013  label="buco pompa"
  ArcFitTolerance = 1e-06
  AttachmentSupport = -> [XZ_Plane]
  ExternalGeometry = -> [Sketch]
  FullyConstrained = true
  MakeInternals = false
  MapMode = 5
  Placement = pos=(0,0,0) rot=(1,0,0;1.5708rad)
  sketch-geometry (8):
    g0: LineSegment StartX=-82.8 StartY=-10.4 StartZ=0 EndX=-82.8 EndY=-9.6 EndZ=0
    g1: LineSegment StartX=-82.8 StartY=-9.6 StartZ=0 EndX=-67.9 EndY=-9.6 EndZ=0
    g2: LineSegment StartX=-67.9 StartY=-9.6 StartZ=0 EndX=-67.9 EndY=6 EndZ=0
    g3: LineSegment StartX=-67.9 StartY=6 StartZ=0 EndX=-65.9 EndY=6 EndZ=0
    g4: LineSegment StartX=-65.9 StartY=6 StartZ=0 EndX=-65.9 EndY=-1.7 EndZ=0
    g5: LineSegment StartX=-65.9 StartY=-1.7 StartZ=0 EndX=-57.2 EndY=-1.7 EndZ=0
    g6: LineSegment StartX=-57.2 StartY=-1.7 StartZ=0 EndX=-57.2 EndY=-10.4 EndZ=0
    g7: LineSegment StartX=-57.2 StartY=-10.4 StartZ=0 EndX=-82.8 EndY=-10.4 EndZ=0
  constraints (22):
    c: Vertical(g0)
    c: Coincident(g1,g0)
    c: Horizontal(g1)
    c: Coincident(g2,g1)
    c: Vertical(g2)
    c: Coincident(g3,g2)
    c: Horizontal(g3)
    c: Coincident(g4,g3)
    c: Vertical(g4)
    c: Coincident(g5,g4)
    c: Horizontal(g5)
    c: Coincident(g6,g5)
    c: Vertical(g6)
    c: Coincident(g7,g6)
    c: Coincident(g7,g0)
    c: DistanceY(g0,g0) = 0.8
    c: DistanceY(g6,g6) = 8.7
    c: DistanceX(g1,g1) = 14.9
    c: DistanceX(g3,g3) = 2
    c: Coincident(g0,g-4)
    c: DistanceY(g2,g-6) = 0
    c: Coincident(g6,g-5)
FEATURE [Part::Extrusion] Extrude009  label="Extrude buco pompa"
  Base = -> Sketch013
  Dir = (0,-1,2e-16)
  DirMode = 2
  FaceMakerClass = Part::FaceMakerBullseye
  FaceMakerMode = 3
  LengthFwd = 13.2
  LengthRev = 0
  Solid = true
  Symmetric = true
FEATURE [Sketcher::SketchObject] Sketch014  label="buco frontale"
  ArcFitTolerance = 1e-06
  AttachmentSupport = -> [XZ_Plane]
  ExternalGeometry = -> [Sketch]
  FullyConstrained = true
  MakeInternals = false
  MapMode = 5
  Placement = pos=(0,0,0) rot=(1,0,0;1.5708rad)
  sketch-geometry (10):
    g0: LineSegment StartX=0 StartY=0 StartZ=0 EndX=0 EndY=24.671 EndZ=0
    g1: LineSegment StartX=0 StartY=24.671 StartZ=0 EndX=-4 EndY=24.671 EndZ=0
    g2: LineSegment StartX=-4 StartY=24.671 StartZ=0 EndX=-4 EndY=16 EndZ=0
    g3: LineSegment StartX=-4 StartY=16 StartZ=0 EndX=-2.4 EndY=16 EndZ=0
    g4: LineSegment StartX=-2.4 StartY=16 StartZ=0 EndX=-2.4 EndY=10 EndZ=0
    g5: LineSegment StartX=-2.4 StartY=10 StartZ=0 EndX=-12 EndY=10 EndZ=0
    g6: LineSegment StartX=-12 StartY=10 StartZ=0 EndX=-12 EndY=6 EndZ=0
    g7: LineSegment StartX=-12 StartY=6 StartZ=0 EndX=-2.4 EndY=6 EndZ=0
    g8: LineSegment StartX=-2.4 StartY=6 StartZ=0 EndX=-2.4 EndY=0 EndZ=0
    g9: LineSegment StartX=-2.4 StartY=0 StartZ=0 EndX=0 EndY=0 EndZ=0
  constraints (29):
    c: Vertical(g0)
    c: Coincident(g1,g0)
    c: Horizontal(g1)
    c: Coincident(g2,g1)
    c: Vertical(g2)
    c: Coincident(g3,g2)
    c: Horizontal(g3)
    c: Coincident(g4,g3)
    c: Vertical(g4)
    c: Coincident(g5,g4)
    c: Horizontal(g5)
    c: Coincident(g6,g5)
    c: Vertical(g6)
    c: Coincident(g7,g6)
    c: Coincident(g8,g7)
    c: Vertical(g8)
    c: Coincident(g9,g8)
    c: Coincident(g9,g0)
    c: Horizontal(g9)
    c: DistanceY(g0,g0) = 24.671
    c: Horizontal(g7)
    c: DistanceY(g6,g6) = 4
    c: DistanceY(g4,g4) = 6
    c: DistanceX(g9,g9) = 2.4
    c: Coincident(g0,g-1)
    c: DistanceY(g-3,g7) = 0
    c: DistanceX(g8,g4) = 0
    c: DistanceX(g-3,g1) = 0
    c: DistanceX(g6,g-3) = 8
FEATURE [Part::Extrusion] Extrude010  label="Extrude buco frontale"
  Base = -> Sketch014
  Dir = (0,-1,2e-16)
  DirMode = 2
  FaceMakerClass = Part::FaceMakerBullseye
  FaceMakerMode = 3
  LengthFwd = 11.2
  LengthRev = 0
  Solid = true
  Symmetric = true
FEATURE [Sketcher::SketchObject] Sketch015  label="guida rail"
  ArcFitTolerance = 1e-06
  AttachmentSupport = -> [XZ_Plane]
  ExternalGeometry = -> [Sketch]
  FullyConstrained = true
  MakeInternals = false
  MapMode = 5
  Placement = pos=(0,0,0) rot=(1,0,0;1.5708rad)
  sketch-geometry (4):
    g0: LineSegment StartX=-100.8 StartY=43.2 StartZ=0 EndX=-44.6 EndY=43.2 EndZ=0
    g1: LineSegment StartX=-44.6 StartY=43.2 StartZ=0 EndX=-44.6 EndY=41.2 EndZ=0
    g2: LineSegment StartX=-44.6 StartY=41.2 StartZ=0 EndX=-100.8 EndY=41.2 EndZ=0
    g3: LineSegment StartX=-100.8 StartY=41.2 StartZ=0 EndX=-100.8 EndY=43.2 EndZ=0
  constraints (9):
    c: Horizontal(g0)
    c: Coincident(g1,g0)
    c: Coincident(g2,g1)
    c: Coincident(g3,g2)
    c: Coincident(g3,g0)
    c: Vertical(g3)
    c: Coincident(g2,g-3)
    c: Coincident(g1,g-3)
    c: Coincident(g0,g-4)
FEATURE [Part::Extrusion] Extrude011  label="Extrude guida rail"
  Base = -> Sketch015
  Dir = (0,-1,2e-16)
  DirMode = 2
  FaceMakerClass = Part::FaceMakerBullseye
  FaceMakerMode = 3
  LengthFwd = 9
  LengthRev = 0
  Solid = true
  Symmetric = true
FEATURE [Sketcher::SketchObject] Sketch016  label="guide per coperture laterali"
  ArcFitTolerance = 1e-06
  AttachmentSupport = -> [XZ_Plane]
  ExternalGeometry = -> [Sketch]
  FullyConstrained = true
  MakeInternals = false
  MapMode = 5
  Placement = pos=(0,0,0) rot=(1,0,0;1.5708rad)
  sketch-geometry (14):
    g0: Circle CenterX=-5.6 CenterY=7.6 CenterZ=0 NormalX=0 NormalY=0 NormalZ=1 AngleXU=0 Radius=1.6
    g1: Circle CenterX=-5.6 CenterY=7.6 CenterZ=0 NormalX=0 NormalY=0 NormalZ=1 AngleXU=0 Radius=4
    g2: Circle CenterX=-5.6 CenterY=34.8 CenterZ=0 NormalX=0 NormalY=0 NormalZ=1 AngleXU=0 Radius=1.6
    g3: Circle CenterX=-5.6 CenterY=34.8 CenterZ=0 NormalX=0 NormalY=0 NormalZ=1 AngleXU=0 Radius=4
    g4: Circle CenterX=-184.08 CenterY=34.8 CenterZ=0 NormalX=0 NormalY=0 NormalZ=1 AngleXU=0 Radius=1.6
    g5: Circle CenterX=-184.08 CenterY=34.8 CenterZ=0 NormalX=0 NormalY=0 NormalZ=1 AngleXU=0 Radius=4
    g6: Circle CenterX=-179.305 CenterY=-76.8316 CenterZ=0 NormalX=0 NormalY=0 NormalZ=1 AngleXU=0 Radius=1.6
    g7: Circle CenterX=-179.305 CenterY=-76.8316 CenterZ=0 NormalX=0 NormalY=0 NormalZ=1 AngleXU=0 Radius=4
    g8: Circle CenterX=-213.443 CenterY=-76.8316 CenterZ=0 NormalX=0 NormalY=0 NormalZ=1 AngleXU=0 Radius=1.6
    g9: Circle CenterX=-213.443 CenterY=-76.8316 CenterZ=0 NormalX=0 NormalY=0 NormalZ=1 AngleXU=0 Radius=4
    g10: Circle CenterX=-78.51 CenterY=7.6 CenterZ=0 NormalX=0 NormalY=0 NormalZ=1 AngleXU=0 Radius=1.6
    g11: Circle CenterX=-78.51 CenterY=7.6 CenterZ=0 NormalX=0 NormalY=0 NormalZ=1 AngleXU=0 Radius=4
    g12: Circle CenterX=-78.51 CenterY=34.8 CenterZ=0 NormalX=0 NormalY=0 NormalZ=1 AngleXU=0 Radius=1.6
    g13: Circle CenterX=-78.51 CenterY=34.8 CenterZ=0 NormalX=0 NormalY=0 NormalZ=1 AngleXU=0 Radius=4
  constraints (35):
    c: Diameter(g0) = 3.2
    c: Diameter(g1) = 8
    c: Coincident(g0,g1)
    c: Diameter(g2) = 3.2
    c: Diameter(g3) = 8
    c: Coincident(g3,g2)
    c: Tangent(g2,g-7)
    c: Diameter(g4) = 3.2
    c: Diameter(g5) = 8
    c: Coincident(g5,g4)
    c: Tangent(g4,g-7)
    c: Tangent(g4,g-8)
    c: Diameter(g6) = 3.2
    c: Diameter(g7) = 8
    c: Coincident(g7,g6)
    c: Tangent(g6,g-9)
    c: Tangent(g6,g-10)
    c: Diameter(g8) = 3.2
    c: Diameter(g9) = 8
    c: Coincident(g9,g8)
    c: Tangent(g8,g-10)
    c: Tangent(g8,g-11)
    c: Diameter(g10) = 3.2
    c: Diameter(g11) = 8
    c: Diameter(g12) = 3.2
    c: Diameter(g13) = 8
    c: Coincident(g12,g13)
    c: Coincident(g10,g11)
    c: Tangent(g12,g-7)
    c: DistanceX(g12,g10) = 0
    c: Tangent(g2,g-6)
    c: Tangent(g0,g-6)
    c: Tangent(g0,g-3)
    c: Tangent(g10,g-3)
    c: Tangent(g10,g-4)
FEATURE [Part::Extrusion] Extrude012  label="extrude guide per coperture laterali"
  Base = -> Sketch016
  Dir = (0,-1,2e-16)
  DirMode = 2
  FaceMakerClass = Part::FaceMakerBullseye
  FaceMakerMode = 3
  LengthFwd = 25.2
  LengthRev = 0
  Solid = true
  Symmetric = true
FEATURE [Sketcher::SketchObject] Sketch017  label="supporto CAM"
  ArcFitTolerance = 1e-06
  AttachmentSupport = -> [XZ_Plane]
  ExternalGeometry = -> [Sketch]
  FullyConstrained = true
  MakeInternals = false
  MapMode = 5
  Placement = pos=(0,0,0) rot=(1,0,0;1.5708rad)
  sketch-geometry (6):
    g0: LineSegment StartX=-2.4 StartY=48 StartZ=0 EndX=-2.4 EndY=41.2 EndZ=0
    g1: LineSegment StartX=-2.4 StartY=48 StartZ=0 EndX=-34 EndY=48 EndZ=0
    g2: LineSegment StartX=-34 StartY=48 StartZ=0 EndX=-34 EndY=46.72 EndZ=0
    g3: LineSegment StartX=-34 StartY=46.72 StartZ=0 EndX=-36 EndY=46.72 EndZ=0
    g4: LineSegment StartX=-36 StartY=46.72 StartZ=0 EndX=-36 EndY=41.2 EndZ=0
    g5: LineSegment StartX=-36 StartY=41.2 StartZ=0 EndX=-2.4 EndY=41.2 EndZ=0
  constraints (15):
    c: Coincident(g1,g0)
    c: Horizontal(g1)
    c: Coincident(g2,g1)
    c: Vertical(g2)
    c: Coincident(g3,g2)
    c: Horizontal(g3)
    c: Coincident(g4,g3)
    c: Coincident(g5,g4)
    c: DistanceX(g1,g0) = 31.6
    c: Coincident(g5,g0)
    c: Vertical(g4)
    c: DistanceY(g2,g1) = 1.28
    c: Coincident(g0,g-3)
    c: Coincident(g0,g-3)
    c: Coincident(g4,g-4)
FEATURE [Part::Extrusion] Extrude013  label="Extrude supporto CAM"
  Base = -> Sketch017
  Dir = (0,-1,2e-16)
  DirMode = 2
  FaceMakerClass = Part::FaceMakerBullseye
  FaceMakerMode = 3
  LengthFwd = 17.8
  LengthRev = 0
  Solid = true
  Symmetric = true
FEATURE [Sketcher::SketchObject] Sketch018  label="Scavo CAM"
  ArcFitTolerance = 1e-06
  AttachmentSupport = -> [YZ_Plane]
  ExternalGeometry = -> [Sketch]
  FullyConstrained = true
  MakeInternals = false
  MapMode = 5
  Placement = pos=(0,0,0) rot=(0.57735,0.57735,0.57735;2.0944rad)
  sketch-geometry (4):
    g0: LineSegment StartX=-7.73 StartY=48 StartZ=0 EndX=7.73 EndY=48 EndZ=0
    g1: LineSegment [constr] StartX=1.07e-14 StartY=48 StartZ=0 EndX=0 EndY=43.5155 EndZ=0
    g2: ArcOfCircle CenterX=9e-15 CenterY=52.42 CenterZ=0 NormalX=0 NormalY=0 NormalZ=1 AngleXU=0 Radius=8.90445 StartAngle=3.66102 EndAngle=5.76376
    g3: Circle [constr] CenterX=9e-15 CenterY=52.42 CenterZ=0 NormalX=0 NormalY=0 NormalZ=1 AngleXU=0 Radius=8.9
  constraints (13):
    c: Horizontal(g0)
    c: DistanceY(g-3,g0) = 0
    c: DistanceX(g0,g0) = 15.46
    c: DistanceX(g0,g-3) = 7.73
    c: DistanceX(g-3) = 0
    c: Coincident(g1,g-3)
    c: PointOnObject(g1,g-2)
    c: Coincident(g2,g0)
    c: Coincident(g2,g0)
    c: PointOnObject(g1,g2)
    c: Diameter(g3) = 17.8
    c: DistanceY(g1,g3) = 4.42
    c: Coincident(g2,g3)
FEATURE [Part::Extrusion] Extrude014  label="Extrude Scavo CAM"
  Base = -> Sketch018
  Dir = (1,0,0)
  DirMode = 2
  FaceMakerClass = Part::FaceMakerBullseye
  FaceMakerMode = 3
  LengthFwd = -34
  LengthRev = 0
  Solid = true
  Symmetric = false
FEATURE [Sketcher::SketchObject] Sketch019  label="scavo rumble"
  ArcFitTolerance = 1e-06
  AttachmentSupport = -> [XZ_Plane]
  ExternalGeometry = -> [Sketch]
  FullyConstrained = true
  MakeInternals = false
  MapMode = 5
  Placement = pos=(0,0,0) rot=(1,0,0;1.5708rad)
  sketch-geometry (6):
    g0: LineSegment StartX=-168.716 StartY=-37.1227 StartZ=0 EndX=-163.58 EndY=-38.7914 EndZ=0
    g1: LineSegment StartX=-163.58 StartY=-38.7914 StartZ=0 EndX=-170.687 EndY=-60.6657 EndZ=0
    g2: LineSegment StartX=-170.687 StartY=-60.6657 StartZ=0 EndX=-175.823 EndY=-58.997 EndZ=0
    g3: LineSegment StartX=-175.823 StartY=-58.997 StartZ=0 EndX=-168.716 EndY=-37.1227 EndZ=0
    g4: LineSegment [constr] StartX=-145.51 StartY=22 StartZ=0 EndX=-165.102 EndY=-38.297 EndZ=0
    g5: LineSegment [constr] StartX=-163.58 StartY=-38.7914 StartZ=0 EndX=-165.102 EndY=-38.297 EndZ=0
  constraints (17):
    c: Coincident(g1,g0)
    c: Coincident(g2,g1)
    c: Coincident(g3,g2)
    c: Coincident(g3,g0)
    c: Parallel(g3,g-3)
    c: Parallel(g3,g1)
    c: Perpendicular(g3,g0)
    c: Perpendicular(g2,g3)
    c: Distance(g2,g0) = 23
    c: Parallel(g4,g-3)
    c: Distance(g4) = 63.4
    c: Coincident(g4,g-3)
    c: Parallel(g5,g0)
    c: Coincident(g5,g0)
    c: Coincident(g5,g4)
    c: Distance(g4,g0) = 3.8
    c: Distance(g4,g0) = 1.6
FEATURE [Part::Extrusion] Extrude015  label="scavo rumble001"
  Base = -> Sketch019
  Dir = (0,-1,2e-16)
  DirMode = 2
  FaceMakerClass = Part::FaceMakerBullseye
  FaceMakerMode = 3
  LengthFwd = 21
  LengthRev = 0
  Solid = true
  Symmetric = true
FEATURE [Sketcher::SketchObject] Sketch020  label="fermo rumble"
  ArcFitTolerance = 1e-06
  AttachmentSupport = -> [XZ_Plane]
  ExternalGeometry = -> [Sketch019,Sketch]
  FullyConstrained = true
  MakeInternals = false
  MapMode = 5
  Placement = pos=(0,0,0) rot=(1,0,0;1.5708rad)
  sketch-geometry (16):
    g0: LineSegment [constr] StartX=-170.849 StartY=-55.9866 StartZ=0 EndX=-172.209 EndY=-60.1713 EndZ=0
    g1: LineSegment [constr] StartX=-172.209 StartY=-60.1713 StartZ=0 EndX=-170.687 EndY=-60.6657 EndZ=0
    g2: LineSegment StartX=-172.262 StartY=-53.2145 StartZ=0 EndX=-170.17 EndY=-53.8943 EndZ=0
    g3: LineSegment StartX=-170.17 StartY=-53.8943 StartZ=0 EndX=-170.849 EndY=-55.9866 EndZ=0
    g4: LineSegment StartX=-170.849 StartY=-55.9866 StartZ=0 EndX=-172.942 EndY=-55.3068 EndZ=0
    g5: LineSegment StartX=-172.942 StartY=-55.3068 StartZ=0 EndX=-172.262 EndY=-53.2145 EndZ=0
    g6: LineSegment StartX=-171.767 StartY=-51.6928 StartZ=0 EndX=-168.344 EndY=-52.8052 EndZ=0
    g7: LineSegment StartX=-168.344 StartY=-52.8052 StartZ=0 EndX=-169.951 EndY=-57.7507 EndZ=0
    g8: LineSegment StartX=-169.951 StartY=-57.7507 StartZ=0 EndX=-173.374 EndY=-56.6383 EndZ=0
    g9: LineSegment StartX=-174.402 StartY=-54.6222 StartZ=0 EndX=-173.784 EndY=-52.72 EndZ=0
    g10: LineSegment [constr] StartX=-173.784 StartY=-52.72 StartZ=0 EndX=-173.289 EndY=-51.1984 EndZ=0
    g11: LineSegment [constr] StartX=-173.289 StartY=-51.1984 StartZ=0 EndX=-171.767 EndY=-51.6928 EndZ=0
    g12: ArcOfCircle CenterX=-172.88 CenterY=-55.1166 CenterZ=0 NormalX=0 NormalY=0 NormalZ=1 AngleXU=0 Radius=1.6 StartAngle=2.82743 EndAngle=4.39823
    g13: GeomPoint [constr] X=-174.896 Y=-56.1438 Z=0
    g14: ArcOfCircle CenterX=-172.262 CenterY=-53.2145 CenterZ=0 NormalX=0 NormalY=0 NormalZ=1 AngleXU=0 Radius=1.6 StartAngle=1.25664 EndAngle=2.82743
    g15: GeomPoint [constr] X=-173.289 Y=-51.1984 Z=0
  constraints (42):
    c: Parallel(g0,g-4)
    c: Distance(g0) = 4.4
    c: Coincident(g1,g0)
    c: Perpendicular(g0,g1)
    c: Distance(g1) = 1.6
    c: Coincident(g1,g-5)
    c: Coincident(g3,g2)
    c: Coincident(g4,g3)
    c: Coincident(g5,g4)
    c: Coincident(g5,g2)
    c: Parallel(g3,g-4)
    c: Parallel(g3,g5)
    c: Perpendicular(g2,g3)
    c: Parallel(g4,g2)
    c: Distance(g2) = 2.2
    c: Distance(g3) = 2.2
    c: Coincident(g7,g6)
    c: Coincident(g8,g7)
    c: Parallel(g7,g-4)
    c: Parallel(g7,g9)
    c: Perpendicular(g6,g7)
    c: Parallel(g6,g8)
    c: Distance(g6,g15) = 5.2
    c: Distance(g7) = 5.2
    c: Coincident(g11,g10)
    c: Parallel(g10,g9)
    c: Parallel(g11,g6)
    c: Distance(g10) = 1.6
    c: Distance(g11) = 1.6
    c: Coincident(g10,g15)
    c: Distance(g11,g2) = 1.6
    c: Distance(g2,g10) = 1.6
    c: PointOnObject(g13,g8)
    c: PointOnObject(g13,g9)
    c: Tangent(g8,g12) = 1.5708
    c: Tangent(g9,g12) = 1.5708
    c: PointOnObject(g15,g9)
    c: Tangent(g6,g14) = 1.5708
    c: Tangent(g9,g14) = 1.5708
    c: Equal(g12,g14)
    c: Coincident(g6,g11)
    c: Coincident(g3,g0)
FEATURE [Part::Extrusion] Extrude016  label="Extrude fermo rumble"
  Base = -> Sketch020
  Dir = (0,-1,2e-16)
  DirMode = 2
  FaceMakerClass = Part::FaceMakerBullseye
  FaceMakerMode = 3
  LengthFwd = 25.2
  LengthRev = 0
  Solid = true
  Symmetric = true
FEATURE [Sketcher::SketchObject] Sketch021  label="perno fermo rumble001"
  ArcFitTolerance = 1e-06
  AttachmentSupport = -> [XZ_Plane001]
  FullyConstrained = true
  MakeInternals = false
  MapMode = 5
  Placement = pos=(0,0,0) rot=(1,0,0;1.5708rad)
  sketch-geometry (16):
    g0: LineSegment StartX=0 StartY=0.45 StartZ=0 EndX=0 EndY=1.55 EndZ=0
    g1: LineSegment StartX=0.45 StartY=2 StartZ=0 EndX=1.55 EndY=2 EndZ=0
    g2: LineSegment StartX=2 StartY=1.55 StartZ=0 EndX=2 EndY=0.45 EndZ=0
    g3: LineSegment StartX=1.55 StartY=0 StartZ=0 EndX=0.45 EndY=0 EndZ=0
    g4: ArcOfCircle [constr] CenterX=0.45 CenterY=1.55 CenterZ=0 NormalX=0 NormalY=0 NormalZ=1 AngleXU=0 Radius=0.45 StartAngle=1.5708 EndAngle=3.14159
    g5: GeomPoint [constr] X=0 Y=2 Z=0
    g6: LineSegment StartX=0.45 StartY=2 StartZ=0 EndX=0 EndY=1.55 EndZ=0
    g7: ArcOfCircle [constr] CenterX=1.55 CenterY=1.55 CenterZ=0 NormalX=0 NormalY=0 NormalZ=1 AngleXU=0 Radius=0.45 StartAngle=0 EndAngle=1.5708
    g8: GeomPoint [constr] X=2 Y=2 Z=0
    g9: LineSegment StartX=2 StartY=1.55 StartZ=0 EndX=1.55 EndY=2 EndZ=0
    g10: ArcOfCircle [constr] CenterX=1.55 CenterY=0.45 CenterZ=0 NormalX=0 NormalY=0 NormalZ=1 AngleXU=0 Radius=0.45 StartAngle=4.71239 EndAngle=6.28319
    g11: GeomPoint [constr] X=2 Y=0 Z=0
    g12: LineSegment StartX=1.55 StartY=0 StartZ=0 EndX=2 EndY=0.45 EndZ=0
    g13: ArcOfCircle [constr] CenterX=0.45 CenterY=0.45 CenterZ=0 NormalX=0 NormalY=0 NormalZ=1 AngleXU=0 Radius=0.45 StartAngle=3.14159 EndAngle=4.71239
    g14: GeomPoint [constr] X=0 Y=0 Z=0
    g15: LineSegment StartX=0 StartY=0.45 StartZ=0 EndX=0.45 EndY=0 EndZ=0
  constraints (35):
    c: Coincident(g14,g-1)
    c: PointOnObject(g5,g-2)
    c: Horizontal(g1)
    c: Vertical(g2)
    c: Horizontal(g3)
    c: DistanceX(g5,g8) = 2
    c: DistanceY(g11,g8) = 2
    c: PointOnObject(g5,g0)
    c: PointOnObject(g5,g1)
    c: Tangent(g0,g4) = 1.5708
    c: Tangent(g1,g4) = 1.5708
    c: Coincident(g6,g0)
    c: Coincident(g6,g1)
    c: PointOnObject(g8,g2)
    c: PointOnObject(g8,g1)
    c: Tangent(g2,g7) = 1.5708
    c: Tangent(g1,g7) = 1.5708
    c: Coincident(g9,g2)
    c: Coincident(g9,g1)
    c: PointOnObject(g11,g2)
    c: PointOnObject(g11,g3)
    c: Tangent(g2,g10) = 1.5708
    c: Tangent(g3,g10) = 1.5708
    c: Coincident(g12,g2)
    c: Coincident(g12,g3)
    c: PointOnObject(g14,g0)
    c: PointOnObject(g14,g3)
    c: Tangent(g0,g13) = 1.5708
    c: Tangent(g3,g13) = 1.5708
    c: Coincident(g15,g0)
    c: Coincident(g15,g3)
    c: Equal(g6,g9)
    c: Equal(g9,g12)
    c: Equal(g12,g15)
    c: DistanceX(g14,g3) = 0.45
FEATURE [Sketcher::SketchObject] Sketch022  label="fori per M3x5(OD)x6(L)"
  ArcFitTolerance = 1e-06
  AttachmentSupport = -> [XZ_Plane]
  ExternalGeometry = -> [Sketch016]
  FullyConstrained = true
  MakeInternals = false
  MapMode = 5
  Placement = pos=(0,0,0) rot=(1,0,0;1.5708rad)
  sketch-geometry (7):
    g0: Circle CenterX=-5.6 CenterY=34.8 CenterZ=0 NormalX=0 NormalY=0 NormalZ=1 AngleXU=0 Radius=2.5
    g1: Circle CenterX=-5.6 CenterY=7.6 CenterZ=0 NormalX=0 NormalY=0 NormalZ=1 AngleXU=0 Radius=2.5
    g2: Circle CenterX=-78.51 CenterY=34.8 CenterZ=0 NormalX=0 NormalY=0 NormalZ=1 AngleXU=0 Radius=2.5
    g3: Circle CenterX=-78.51 CenterY=7.6 CenterZ=0 NormalX=0 NormalY=0 NormalZ=1 AngleXU=0 Radius=2.5
    g4: Circle CenterX=-184.08 CenterY=34.8 CenterZ=0 NormalX=0 NormalY=0 NormalZ=1 AngleXU=0 Radius=2.5
    g5: Circle CenterX=-179.305 CenterY=-76.8316 CenterZ=0 NormalX=0 NormalY=0 NormalZ=1 AngleXU=0 Radius=2.5
    g6: Circle CenterX=-213.443 CenterY=-76.8316 CenterZ=0 NormalX=0 NormalY=0 NormalZ=1 AngleXU=0 Radius=2.5
  constraints (14):
    c: Diameter(g0) = 5
    c: Diameter(g1) = 5
    c: Diameter(g2) = 5
    c: Diameter(g3) = 5
    c: Diameter(g4) = 5
    c: Diameter(g5) = 5
    c: Diameter(g6) = 5
    c: Coincident(g0,g-8)
    c: Coincident(g1,g-9)
    c: Coincident(g2,g-6)
    c: Coincident(g3,g-7)
    c: Coincident(g4,g-5)
    c: Coincident(g5,g-4)
    c: Coincident(g6,g-3)
FEATURE [Part::Extrusion] Extrude018  label="Extrude fori M3x5x6 - dx"
  Base = -> Sketch022
  Dir = (0,-1,2e-16)
  DirMode = 2
  FaceMakerClass = Part::FaceMakerBullseye
  FaceMakerMode = 3
  LengthFwd = 6.2
  LengthRev = 0
  Placement = pos=(0,-9.5,0) rot=(0,0,1;0rad)
  Solid = true
  Symmetric = true
FEATURE [Part::Extrusion] Extrude019  label="Extrude fori M3x5x6 - sx"
  Base = -> Sketch022
  Dir = (0,-1,2e-16)
  DirMode = 2
  FaceMakerClass = Part::FaceMakerBullseye
  FaceMakerMode = 3
  LengthFwd = 6.2
  LengthRev = 0
  Placement = pos=(0,9.5,0) rot=(0,0,1;0rad)
  Solid = true
  Symmetric = true
FEATURE [Sketcher::SketchObject] Sketch023  label="foro anteriore M3x5x6"
  ArcFitTolerance = 1e-06
  AttachmentSupport = -> [YZ_Plane]
  FullyConstrained = true
  MakeInternals = false
  MapMode = 5
  Placement = pos=(0,0,0) rot=(0.57735,0.57735,0.57735;2.0944rad)
  sketch-geometry (2):
    g0: LineSegment [constr] StartX=0 StartY=0 StartZ=0 EndX=0 EndY=38.6 EndZ=0
    g1: Circle CenterX=0 CenterY=38.6 CenterZ=0 NormalX=0 NormalY=0 NormalZ=1 AngleXU=0 Radius=2.5
  constraints (5):
    c: Coincident(g0,g-1)
    c: PointOnObject(g0,g-2)
    c: DistanceY(g0,g0) = 38.6
    c: Diameter(g1) = 5
    c: Coincident(g1,g0)
FEATURE [Part::Extrusion] Extrude020  label="Extrude foro anteriore M3x5x6"
  Base = -> Sketch023
  Dir = (1,0,0)
  DirMode = 2
  FaceMakerClass = Part::FaceMakerBullseye
  FaceMakerMode = 3
  LengthFwd = -6.2
  LengthRev = 0
  Solid = true
  Symmetric = false
FEATURE [Sketcher::SketchObject] Sketch024  label="fori per viti frontale"
  ArcFitTolerance = 1e-06
  AttachmentSupport = -> [YZ_Plane]
  FullyConstrained = true
  MakeInternals = false
  MapMode = 5
  Placement = pos=(0,0,0) rot=(0.57735,0.57735,0.57735;2.0944rad)
  sketch-geometry (9):
    g0: LineSegment [constr] StartX=-10.3 StartY=30.721 StartZ=0 EndX=10.3 EndY=30.721 EndZ=0
    g1: LineSegment [constr] StartX=10.3 StartY=30.721 StartZ=0 EndX=10.3 EndY=10.121 EndZ=0
    g2: LineSegment [constr] StartX=10.3 StartY=10.121 StartZ=0 EndX=-10.3 EndY=10.121 EndZ=0
    g3: LineSegment [constr] StartX=-10.3 StartY=10.121 StartZ=0 EndX=-10.3 EndY=30.721 EndZ=0
    g4: LineSegment [constr] StartX=0 StartY=0 StartZ=0 EndX=0 EndY=10.121 EndZ=0
    g5: Circle CenterX=-10.3 CenterY=30.721 CenterZ=0 NormalX=0 NormalY=0 NormalZ=1 AngleXU=0 Radius=2
    g6: Circle CenterX=10.3 CenterY=30.721 CenterZ=0 NormalX=0 NormalY=0 NormalZ=1 AngleXU=0 Radius=2
    g7: Circle CenterX=-10.3 CenterY=10.121 CenterZ=0 NormalX=0 NormalY=0 NormalZ=1 AngleXU=0 Radius=2
    g8: Circle CenterX=10.3 CenterY=10.121 CenterZ=0 NormalX=0 NormalY=0 NormalZ=1 AngleXU=0 Radius=2
  constraints (22):
    c: Horizontal(g0)
    c: Coincident(g1,g0)
    c: Vertical(g1)
    c: Coincident(g2,g1)
    c: Horizontal(g2)
    c: Coincident(g3,g2)
    c: Coincident(g3,g0)
    c: Vertical(g3)
    c: DistanceX(g0,g0) = 20.6
    c: DistanceY(g3,g3) = 20.6
    c: Coincident(g4,g-1)
    c: PointOnObject(g4,g-2)
    c: DistanceY(g4,g4) = 10.121
    c: Symmetric(g2,g2,g4)
    c: Diameter(g5) = 4
    c: Diameter(g6) = 4
    c: Diameter(g7) = 4
    c: Diameter(g8) = 4
    c: Coincident(g5,g0)
    c: Coincident(g6,g0)
    c: Coincident(g7,g2)
    c: Coincident(g8,g1)
FEATURE [Part::Extrusion] Extrude021  label="Extrude fori per viti frontale"
  Base = -> Sketch024
  Dir = (1,0,0)
  DirMode = 2
  FaceMakerClass = Part::FaceMakerBullseye
  FaceMakerMode = 3
  LengthFwd = -2.4
  LengthRev = 0
  Solid = true
  Symmetric = false
FEATURE [Sketcher::SketchObject] Sketch025  label="foro per filo CAM"
  ArcFitTolerance = 1e-06
  AttachmentSupport = -> [XZ_Plane]
  ExternalGeometry = -> [Sketch]
  FullyConstrained = true
  MakeInternals = false
  MapMode = 5
  Placement = pos=(0,0,0) rot=(1,0,0;1.5708rad)
  sketch-geometry (4):
    g0: LineSegment StartX=-44.6 StartY=41.2 StartZ=0 EndX=-44.6 EndY=36.4 EndZ=0
    g1: LineSegment StartX=-44.6 StartY=36.4 StartZ=0 EndX=-54.6 EndY=36.4 EndZ=0
    g2: LineSegment StartX=-54.6 StartY=36.4 StartZ=0 EndX=-50.4 EndY=41.2 EndZ=0
    g3: LineSegment StartX=-50.4 StartY=41.2 StartZ=0 EndX=-44.6 EndY=41.2 EndZ=0
  constraints (11):
    c: Vertical(g0)
    c: Coincident(g1,g0)
    c: Horizontal(g1)
    c: Coincident(g2,g1)
    c: Coincident(g3,g2)
    c: Coincident(g3,g0)
    c: Horizontal(g3)
    c: Coincident(g0,g-3)
    c: DistanceY(g0,g-4) = 0
    c: DistanceX(g3,g3) = 5.8
    c: DistanceX(g1,g1) = 10
FEATURE [Part::Extrusion] Extrude022  label="Extrude foro per filo CAM dx"
  Base = -> Sketch025
  Dir = (0,-1,2e-16)
  DirMode = 2
  FaceMakerClass = Part::FaceMakerBullseye
  FaceMakerMode = 3
  LengthFwd = 4.9
  LengthRev = 0
  Placement = pos=(0,6.95,0) rot=(0,0,1;0rad)
  Solid = true
  Symmetric = true
FEATURE [Part::Extrusion] Extrude023  label="Extrude foro per filo CAM sx"
  Base = -> Sketch025
  Dir = (0,-1,2e-16)
  DirMode = 2
  FaceMakerClass = Part::FaceMakerBullseye
  FaceMakerMode = 3
  LengthFwd = 4.9
  LengthRev = 0
  Placement = pos=(0,-6.95,0) rot=(0,0,1;0rad)
  Solid = true
  Symmetric = true
FEATURE [Sketcher::SketchObject] Sketch026  label="foro sotto anteriore M3x5x6"
  ArcFitTolerance = 1e-06
  AttachmentSupport = -> [XY_Plane]
  FullyConstrained = true
  MakeInternals = false
  MapMode = 5
  sketch-geometry (2):
    g0: LineSegment [constr] StartX=0 StartY=0 StartZ=0 EndX=-16.5 EndY=0 EndZ=0
    g1: Circle CenterX=-16.5 CenterY=0 CenterZ=0 NormalX=0 NormalY=0 NormalZ=1 AngleXU=0 Radius=2.5
  constraints (5):
    c: Distance(g0) = 16.5
    c: Coincident(g0,g-1)
    c: PointOnObject(g0,g-1)
    c: Diameter(g1) = 5
    c: Coincident(g0,g1)
FEATURE [Sketcher::SketchObject] Sketch027  label="foro sotto posteriore M3x5x6"
  ArcFitTolerance = 1e-06
  AttachmentSupport = -> [XY_Plane]
  ExternalGeometry = -> [Sketch]
  FullyConstrained = true
  MakeInternals = false
  MapMode = 5
  sketch-geometry (2):
    g0: LineSegment [constr] StartX=-82.8 StartY=2e-16 StartZ=0 EndX=-71.3 EndY=2e-16 EndZ=0
    g1: Circle CenterX=-71.3 CenterY=2e-16 CenterZ=0 NormalX=0 NormalY=0 NormalZ=1 AngleXU=0 Radius=2.5
  constraints (5):
    c: Distance(g0) = 11.5
    c: Coincident(g0,g-3)
    c: PointOnObject(g0,g-3)
    c: Diameter(g1) = 5
    c: Coincident(g1,g0)
FEATURE [Sketcher::SketchObject] Sketch029  label="fori sotto impugnatura"
  ArcFitTolerance = 1e-06
  AttachmentSupport = -> [XY_Plane]
  ExternalGeometry = -> [Sketch]
  FullyConstrained = true
  MakeInternals = false
  MapMode = 5
  sketch-geometry (15):
    g0: LineSegment [constr] StartX=-175.232 StartY=-1.83e-14 StartZ=0 EndX=-191.232 EndY=0 EndZ=0
    g1: Circle CenterX=-191.232 CenterY=0 CenterZ=0 NormalX=0 NormalY=0 NormalZ=1 AngleXU=0 Radius=3.95
    g2: LineSegment [constr] StartX=-175.232 StartY=-1.83e-14 StartZ=0 EndX=-204.275 EndY=0 EndZ=0
    g3: LineSegment StartX=-204.275 StartY=3.525 StartZ=0 EndX=-204.275 EndY=-3.525 EndZ=0
    g4: LineSegment StartX=-205.4 StartY=-4.65 StartZ=0 EndX=-206.65 EndY=-4.65 EndZ=0
    g5: LineSegment StartX=-207.775 StartY=-3.525 StartZ=0 EndX=-207.775 EndY=3.525 EndZ=0
    g6: LineSegment StartX=-206.65 StartY=4.65 StartZ=0 EndX=-205.4 EndY=4.65 EndZ=0
    g7: ArcOfCircle CenterX=-206.65 CenterY=3.525 CenterZ=0 NormalX=0 NormalY=0 NormalZ=1 AngleXU=0 Radius=1.125 StartAngle=1.5708 EndAngle=3.14159
    g8: GeomPoint [constr] X=-207.775 Y=4.65 Z=0
    g9: ArcOfCircle CenterX=-205.4 CenterY=3.525 CenterZ=0 NormalX=0 NormalY=0 NormalZ=1 AngleXU=0 Radius=1.125 StartAngle=0 EndAngle=1.5708
    g10: GeomPoint [constr] X=-204.275 Y=4.65 Z=0
    g11: ArcOfCircle CenterX=-205.4 CenterY=-3.525 CenterZ=0 NormalX=0 NormalY=0 NormalZ=1 AngleXU=0 Radius=1.125 StartAngle=4.71239 EndAngle=6.28319
    g12: GeomPoint [constr] X=-204.275 Y=-4.65 Z=0
    g13: ArcOfCircle CenterX=-206.65 CenterY=-3.525 CenterZ=0 NormalX=0 NormalY=0 NormalZ=1 AngleXU=0 Radius=1.125 StartAngle=3.14159 EndAngle=4.71239
    g14: GeomPoint [constr] X=-207.775 Y=-4.65 Z=0
  constraints (35):
    c: Distance(g0) = 16
    c: Coincident(g0,g-3)
    c: PointOnObject(g0,g-1)
    c: Diameter(g1) = 7.9
    c: Coincident(g1,g0)
    c: Coincident(g2,g0)
    c: PointOnObject(g2,g-1)
    c: Vertical(g3)
    c: Horizontal(g4)
    c: Vertical(g5)
    c: Horizontal(g6)
    c: DistanceY(g12,g10) = 9.3
    c: DistanceX(g8,g10) = 3.5
    c: Symmetric(g10,g12,g2)
    c: PointOnObject(g8,g5)
    c: PointOnObject(g8,g6)
    c: Tangent(g5,g7) = 1.5708
    c: Tangent(g6,g7) = 1.5708
    c: PointOnObject(g10,g3)
    c: PointOnObject(g10,g6)
    c: Tangent(g3,g9) = 1.5708
    c: Tangent(g6,g9) = 1.5708
    c: PointOnObject(g12,g3)
    c: PointOnObject(g12,g4)
    c: Tangent(g3,g11) = 1.5708
    c: Tangent(g4,g11) = 1.5708
    c: PointOnObject(g14,g4)
    c: PointOnObject(g14,g5)
    c: Tangent(g4,g13) = 1.5708
    c: Tangent(g5,g13) = 1.5708
    c: Equal(g7,g9)
    c: Equal(g9,g11)
    c: Equal(g11,g13)
    c: DistanceX(g6,g6) = 1.25
    c: DistanceX(g-5,g5) = 6.8
FEATURE [Sketcher::SketchObject] Sketch030  label="fori superiori per solenoide e oled"
  ArcFitTolerance = 1e-06
  AttachmentSupport = -> [XY_Plane]
  ExternalGeometry = -> [Sketch]
  FullyConstrained = true
  MakeInternals = false
  MapMode = 5
  sketch-geometry (33):
    g0: LineSegment [constr] StartX=-181.6 StartY=1.12e-14 StartZ=0 EndX=-169.91 EndY=0 EndZ=0
    g1: LineSegment [constr] StartX=-169.91 StartY=0 StartZ=0 EndX=-169.91 EndY=-2.6 EndZ=0
    g2: LineSegment [constr] StartX=-169.91 StartY=0 StartZ=0 EndX=-169.91 EndY=2.6 EndZ=0
    g3: LineSegment StartX=-169.91 StartY=4.975 StartZ=0 EndX=-169.91 EndY=8.225 EndZ=0
    g4: LineSegment StartX=-167.535 StartY=10.6 StartZ=0 EndX=-167.285 EndY=10.6 EndZ=0
    g5: LineSegment StartX=-164.91 StartY=8.225 StartZ=0 EndX=-164.91 EndY=4.975 EndZ=0
    g6: LineSegment StartX=-167.285 StartY=2.6 StartZ=0 EndX=-167.535 EndY=2.6 EndZ=0
    g7: LineSegment StartX=-169.91 StartY=-4.975 StartZ=0 EndX=-169.91 EndY=-8.225 EndZ=0
    g8: LineSegment StartX=-167.535 StartY=-10.6 StartZ=0 EndX=-167.285 EndY=-10.6 EndZ=0
    g9: LineSegment StartX=-164.91 StartY=-8.225 StartZ=0 EndX=-164.91 EndY=-4.975 EndZ=0
    g10: LineSegment StartX=-167.285 StartY=-2.6 StartZ=0 EndX=-167.535 EndY=-2.6 EndZ=0
    g11: ArcOfCircle CenterX=-167.535 CenterY=8.225 CenterZ=0 NormalX=0 NormalY=0 NormalZ=1 AngleXU=0 Radius=2.375 StartAngle=1.5708 EndAngle=3.14159
    g12: GeomPoint [constr] X=-169.91 Y=10.6 Z=0
    g13: ArcOfCircle CenterX=-167.285 CenterY=8.225 CenterZ=0 NormalX=0 NormalY=0 NormalZ=1 AngleXU=0 Radius=2.375 StartAngle=0 EndAngle=1.5708
    g14: GeomPoint [constr] X=-164.91 Y=10.6 Z=0
    g15: ArcOfCircle CenterX=-167.285 CenterY=4.975 CenterZ=0 NormalX=0 NormalY=0 NormalZ=1 AngleXU=0 Radius=2.375 StartAngle=4.71239 EndAngle=6.28319
    g16: GeomPoint [constr] X=-164.91 Y=2.6 Z=0
    g17: ArcOfCircle CenterX=-167.535 CenterY=4.975 CenterZ=0 NormalX=0 NormalY=0 NormalZ=1 AngleXU=0 Radius=2.375 StartAngle=3.14159 EndAngle=4.71239
    g18: GeomPoint [constr] X=-169.91 Y=2.6 Z=0
    g19: ArcOfCircle CenterX=-167.535 CenterY=-4.975 CenterZ=0 NormalX=0 NormalY=0 NormalZ=1 AngleXU=0 Radius=2.375 StartAngle=1.5708 EndAngle=3.14159
    g20: GeomPoint [constr] X=-169.91 Y=-2.6 Z=0
    g21: ArcOfCircle CenterX=-167.285 CenterY=-4.975 CenterZ=0 NormalX=0 NormalY=0 NormalZ=1 AngleXU=0 Radius=2.375 StartAngle=0 EndAngle=1.5708
    g22: GeomPoint [constr] X=-164.91 Y=-2.6 Z=0
    g23: ArcOfCircle CenterX=-167.285 CenterY=-8.225 CenterZ=0 NormalX=0 NormalY=0 NormalZ=1 AngleXU=0 Radius=2.375 StartAngle=4.71239 EndAngle=6.28319
    g24: GeomPoint [constr] X=-164.91 Y=-10.6 Z=0
    g25: ArcOfCircle CenterX=-167.535 CenterY=-8.225 CenterZ=0 NormalX=0 NormalY=0 NormalZ=1 AngleXU=0 Radius=2.375 StartAngle=3.14159 EndAngle=4.71239
    g26: GeomPoint [constr] X=-169.91 Y=-10.6 Z=0
    g27: LineSegment [constr] StartX=-181.6 StartY=1.12e-14 StartZ=0 EndX=-152.209 EndY=0 EndZ=0
    g28: LineSegment [constr] StartX=-181.6 StartY=1.12e-14 StartZ=0 EndX=-130.41 EndY=0 EndZ=0
    g29: LineSegment [constr] StartX=-152.209 StartY=0 StartZ=0 EndX=-152.209 EndY=6.95 EndZ=0
    g30: LineSegment [constr] StartX=-130.41 StartY=0 StartZ=0 EndX=-130.41 EndY=-6.95 EndZ=0
    g31: Circle CenterX=-152.209 CenterY=6.95 CenterZ=0 NormalX=0 NormalY=0 NormalZ=1 AngleXU=0 Radius=2.1
    g32: Circle CenterX=-130.41 CenterY=-6.95 CenterZ=0 NormalX=0 NormalY=0 NormalZ=1 AngleXU=0 Radius=2.1
  constraints (79):
    c: Distance(g0) = 11.69
    c: PointOnObject(g0,g-1)
    c: Coincident(g-4,g0)
    c: Distance(g1) = 2.6
    c: Coincident(g1,g0)
    c: Vertical(g1)
    c: Distance(g2) = 2.6
    c: Coincident(g2,g0)
    c: Vertical(g2)
    c: Distance(g18,g12) = 8
    c: Coincident(g18,g2)
    c: Vertical(g3)
    c: Distance(g14,g12) = 5
    c: Horizontal(g4)
    c: Distance(g16,g14) = 8
    c: Vertical(g5)
    c: Distance(g26,g20) = 8
    c: Coincident(g20,g1)
    c: Vertical(g7)
    c: Distance(g26,g24) = 5
    c: Horizontal(g8)
    c: Distance(g24,g22) = 8
    c: Vertical(g9)
    c: PointOnObject(g12,g3)
    c: PointOnObject(g12,g4)
    c: Tangent(g3,g11) = 1.5708
    c: Tangent(g4,g11) = 1.5708
    c: PointOnObject(g14,g5)
    c: PointOnObject(g14,g4)
    c: Tangent(g5,g13) = 1.5708
    c: Tangent(g4,g13) = 1.5708
    c: PointOnObject(g16,g5)
    c: PointOnObject(g16,g6)
    c: Tangent(g5,g15) = 1.5708
    c: Tangent(g6,g15) = 1.5708
    c: PointOnObject(g18,g3)
    c: PointOnObject(g18,g6)
    c: Tangent(g3,g17) = 1.5708
    c: Tangent(g6,g17) = 1.5708
    c: Equal(g11,g13)
    c: Equal(g13,g15)
    c: Equal(g15,g17)
    c: DistanceX(g4,g4) = 0.25
    c: PointOnObject(g20,g7)
    c: PointOnObject(g20,g10)
    c: Tangent(g7,g19) = -1.5708
    c: Tangent(g10,g19) = -1.5708
    c: PointOnObject(g22,g9)
    c: PointOnObject(g22,g10)
    c: Tangent(g9,g21) = -1.5708
    c: Tangent(g10,g21) = -1.5708
    c: PointOnObject(g24,g9)
    c: PointOnObject(g24,g8)
    c: Tangent(g9,g23) = -1.5708
    c: Tangent(g8,g23) = -1.5708
    c: PointOnObject(g26,g8)
    c: PointOnObject(g26,g7)
    c: Tangent(g8,g25) = -1.5708
    c: Tangent(g7,g25) = -1.5708
    c: Equal(g19,g21)
    c: Equal(g21,g23)
    c: Equal(g23,g25)
    c: DistanceX(g10,g10) = 0.25
    c: Distance(g27) = 29.391
    c: Coincident(g27,g0)
    c: PointOnObject(g27,g-1)
    c: Distance(g28) = 51.19
    c: Coincident(g28,g0)
    c: PointOnObject(g28,g-1)
    c: Distance(g29) = 6.95
    c: Coincident(g29,g27)
    c: Vertical(g29)
    c: Distance(g30) = 6.95
    c: Coincident(g30,g28)
    c: Vertical(g30)
    c: Diameter(g31) = 4.2
    c: Diameter(g32) = 4.2
    c: Coincident(g32,g30)
    c: Coincident(g31,g29)
FEATURE [Sketcher::SketchObject] Sketch031  label="fori inferiori switch pompa"
  ArcFitTolerance = 1e-06
  AttachmentSupport = -> [XY_Plane]
  ExternalGeometry = -> [Sketch]
  FullyConstrained = true
  MakeInternals = false
  MapMode = 5
  sketch-geometry (4):
    g0: LineSegment [constr] StartX=-57.2 StartY=1.9e-15 StartZ=0 EndX=-62.45 EndY=1.9e-15 EndZ=0
    g1: LineSegment [constr] StartX=-62.45 StartY=3.25 StartZ=0 EndX=-62.45 EndY=-3.25 EndZ=0
    g2: Circle CenterX=-62.45 CenterY=3.25 CenterZ=0 NormalX=0 NormalY=0 NormalZ=1 AngleXU=0 Radius=1.6
    g3: Circle CenterX=-62.45 CenterY=-3.25 CenterZ=0 NormalX=0 NormalY=0 NormalZ=1 AngleXU=0 Radius=1.6
  constraints (10):
    c: Distance(g0) = 5.25
    c: Coincident(g0,g-3)
    c: PointOnObject(g0,g-3)
    c: Vertical(g1)
    c: DistanceY(g1,g1) = 6.5
    c: Symmetric(g1,g1,g0)
    c: Diameter(g2) = 3.2
    c: Diameter(g3) = 3.2
    c: Coincident(g2,g1)
    c: Coincident(g3,g1)
FEATURE [Sketcher::SketchObject] Sketch032  label="spazio per PILA 18650"
  ArcFitTolerance = 1e-06
  AttachmentSupport = -> [XY_Plane]
  ExternalGeometry = -> [Sketch]
  FullyConstrained = true
  MakeInternals = false
  MapMode = 5
  sketch-geometry (2):
    g0: LineSegment [constr] StartX=-178.142 StartY=-1.74e-14 StartZ=0 EndX=-191.142 EndY=-1.83e-14 EndZ=0
    g1: Circle CenterX=-191.142 CenterY=-1.83e-14 CenterZ=0 NormalX=0 NormalY=0 NormalZ=1 AngleXU=0 Radius=10.5
  constraints (5):
    c: Distance(g0) = 13
    c: Coincident(g0,g-3)
    c: PointOnObject(g0,g-4)
    c: Diameter(g1) = 21
    c: Coincident(g1,g0)
FEATURE [Part::Extrusion] Extrude030  label="Extrude spazio per PILA 18650"
  Base = -> Sketch032
  Dir = (0,0,1)
  DirLink = -> Sketch [Edge45]
  DirMode = 2
  FaceMakerClass = Part::FaceMakerBullseye
  FaceMakerMode = 3
  LengthFwd = 76
  LengthRev = 0
  Placement = pos=(6,0,-72) rot=(0,0,1;0rad)
  Solid = true
  Symmetric = false
FEATURE [Sketcher::SketchObject] Sketch033  label="fermo per scheda micro"
  ArcFitTolerance = 1e-06
  AttachmentSupport = -> [XZ_Plane]
  ExternalGeometry = -> [Sketch]
  FullyConstrained = true
  MakeInternals = false
  MapMode = 5
  Placement = pos=(0,0,0) rot=(1,0,0;1.5708rad)
  sketch-geometry (12):
    g0: LineSegment StartX=-11.6 StartY=6 StartZ=0 EndX=-4 EndY=6 EndZ=0
    g1: LineSegment StartX=-4 StartY=6 StartZ=0 EndX=-4 EndY=36.4 EndZ=0
    g2: LineSegment StartX=-4 StartY=36.4 StartZ=0 EndX=-11.6 EndY=36.4 EndZ=0
    g3: LineSegment StartX=-11.6 StartY=36.4 StartZ=0 EndX=-11.6 EndY=6 EndZ=0
    g4: LineSegment StartX=-80.11 StartY=11.6 StartZ=0 EndX=-70.51 EndY=11.6 EndZ=0
    g5: LineSegment StartX=-70.51 StartY=11.6 StartZ=0 EndX=-70.51 EndY=6 EndZ=0
    g6: LineSegment StartX=-70.51 StartY=6 StartZ=0 EndX=-80.11 EndY=6 EndZ=0
    g7: LineSegment StartX=-80.11 StartY=6 StartZ=0 EndX=-80.11 EndY=11.6 EndZ=0
    g8: LineSegment StartX=-78.51 StartY=36.4 StartZ=0 EndX=-70.51 EndY=36.4 EndZ=0
    g9: LineSegment StartX=-70.51 StartY=36.4 StartZ=0 EndX=-70.51 EndY=30.8 EndZ=0
    g10: LineSegment StartX=-70.51 StartY=30.8 StartZ=0 EndX=-78.51 EndY=30.8 EndZ=0
    g11: LineSegment StartX=-78.51 StartY=30.8 StartZ=0 EndX=-78.51 EndY=36.4 EndZ=0
  constraints (33):
    c: Horizontal(g0)
    c: Coincident(g1,g0)
    c: Coincident(g2,g1)
    c: Horizontal(g2)
    c: Coincident(g3,g2)
    c: Coincident(g3,g0)
    c: Vertical(g3)
    c: DistanceX(g2,g2) = 7.6
    c: Coincident(g1,g-3)
    c: Coincident(g0,g-3)
    c: Horizontal(g4)
    c: Coincident(g5,g4)
    c: Vertical(g5)
    c: Coincident(g6,g5)
    c: Horizontal(g6)
    c: Coincident(g7,g6)
    c: Coincident(g7,g4)
    c: Vertical(g7)
    c: DistanceY(g5,g5) = 5.6
    c: DistanceX(g4,g4) = 9.6
    c: Coincident(g9,g8)
    c: Vertical(g9)
    c: Coincident(g10,g9)
    c: Horizontal(g10)
    c: Coincident(g11,g10)
    c: Coincident(g11,g8)
    c: Vertical(g11)
    c: DistanceY(g9,g9) = 5.6
    c: DistanceX(g10,g10) = 8
    c: Coincident(g4,g-4)
    c: DistanceX(g4,g10) = 1.6
    c: Horizontal(g8)
    c: DistanceY(g8,g1) = 0
FEATURE [Sketcher::SketchObject] Sketch034  label="buchi guida rail"
  ArcFitTolerance = 1e-06
  AttachmentSupport = -> [XY_Plane]
  ExternalGeometry = -> [Sketch]
  FullyConstrained = true
  MakeInternals = false
  MapMode = 5
  sketch-geometry (6):
    g0: LineSegment [constr] StartX=-100.8 StartY=9.1e-15 StartZ=0 EndX=-93.3 EndY=0 EndZ=0
    g1: LineSegment [constr] StartX=-93.3 StartY=0 StartZ=0 EndX=-73.3 EndY=0 EndZ=0
    g2: LineSegment [constr] StartX=-73.3 StartY=0 StartZ=0 EndX=-53.3 EndY=0 EndZ=0
    g3: Circle CenterX=-93.3 CenterY=0 CenterZ=0 NormalX=0 NormalY=0 NormalZ=1 AngleXU=0 Radius=2.5
    g4: Circle CenterX=-73.3 CenterY=0 CenterZ=0 NormalX=0 NormalY=0 NormalZ=1 AngleXU=0 Radius=2.5
    g5: Circle CenterX=-53.3 CenterY=0 CenterZ=0 NormalX=0 NormalY=0 NormalZ=1 AngleXU=0 Radius=2.5
  constraints (15):
    c: Distance(g0) = 7.5
    c: Coincident(g0,g-3)
    c: PointOnObject(g0,g-1)
    c: Distance(g1) = 20
    c: Coincident(g1,g0)
    c: PointOnObject(g1,g-1)
    c: Distance(g2) = 20
    c: Coincident(g2,g1)
    c: PointOnObject(g2,g-1)
    c: Diameter(g3) = 5
    c: Diameter(g4) = 5
    c: Diameter(g5) = 5
    c: Coincident(g3,g0)
    c: Coincident(g4,g1)
    c: Coincident(g5,g2)
FEATURE [Part::Extrusion] Extrude032  label="Extrude buchi guida rail"
  Base = -> Sketch034
  Dir = (0,0,1)
  DirMode = 2
  FaceMakerClass = Part::FaceMakerBullseye
  FaceMakerMode = 3
  LengthFwd = -6.2
  LengthRev = 0
  Placement = pos=(0,0,43.2) rot=(0,0,1;0rad)
  Solid = true
  Symmetric = false
FEATURE [Part::Extrusion] Extrude033  label="Extrude fori superiori per solenoide e oled001"
  Base = -> Sketch030
  Dir = (0,0,1)
  DirMode = 2
  FaceMakerClass = Part::FaceMakerBullseye
  FaceMakerMode = 3
  LengthFwd = -4.8
  LengthRev = 0
  Placement = pos=(0,0,41.2) rot=(0,0,1;0rad)
  Solid = true
  Symmetric = false
FEATURE [Part::Extrusion] Extrude034  label="Extrude fori sotto impugnatura001"
  Base = -> Sketch029
  Dir = (0,0,1)
  DirMode = 2
  FaceMakerClass = Part::FaceMakerBullseye
  FaceMakerMode = 3
  LengthFwd = 5
  LengthRev = 0
  Placement = pos=(0,0,-83) rot=(0,0,1;0rad)
  Solid = true
  Symmetric = false
FEATURE [Part::Extrusion] Extrude035  label="Extrude fori inferiori switch pompa001"
  Base = -> Sketch031
  Dir = (0,0,1)
  DirMode = 2
  FaceMakerClass = Part::FaceMakerBullseye
  FaceMakerMode = 3
  LengthFwd = 4
  LengthRev = 0
  Placement = pos=(0,0,-1.7) rot=(0,0,1;0rad)
  Solid = true
  Symmetric = false
FEATURE [Part::Extrusion] Extrude036  label="Extrude foro sotto posteriore M3x5x007"
  Base = -> Sketch027
  Dir = (0,0,1)
  DirMode = 2
  FaceMakerClass = Part::FaceMakerBullseye
  FaceMakerMode = 3
  LengthFwd = 6.2
  LengthRev = 0
  Placement = pos=(0,0,-9.6) rot=(0,0,1;0rad)
  Solid = true
  Symmetric = false
FEATURE [Part::Extrusion] Extrude037  label="Extrude foro sotto anteriore M3x5x007"
  Base = -> Sketch026
  Dir = (0,0,1)
  DirMode = 2
  FaceMakerClass = Part::FaceMakerBullseye
  FaceMakerMode = 3
  LengthFwd = 6.2
  LengthRev = 0
  Solid = true
  Symmetric = false
FEATURE [Sketcher::SketchObject] Sketch035  label="foro per fissaggio micro"
  ArcFitTolerance = 1e-06
  AttachmentSupport = -> [XZ_Plane]
  ExternalGeometry = -> [Sketch,Sketch033]
  FullyConstrained = true
  MakeInternals = false
  MapMode = 5
  Placement = pos=(0,0,0) rot=(1,0,0;1.5708rad)
  sketch-geometry (3):
    g0: Circle CenterX=-7.8 CenterY=21.2 CenterZ=0 NormalX=0 NormalY=0 NormalZ=1 AngleXU=0 Radius=1.6
    g1: GeomPoint [constr] X=-4 Y=21.2 Z=0
    g2: LineSegment [constr] StartX=-4 StartY=21.2 StartZ=0 EndX=-11.6 EndY=21.2 EndZ=0
  constraints (6):
    c: Diameter(g0) = 3.2
    c: Symmetric(g-3,g-3,g1)
    c: Coincident(g2,g1)
    c: Horizontal(g2)
    c: DistanceX(g-4,g2) = 0
    c: Symmetric(g2,g1,g0)
FEATURE [Part::Extrusion] Extrude038  label="Extrude foro per fissaggio micro"
  Base = -> Sketch035
  Dir = (0,-1,2e-16)
  DirMode = 2
  FaceMakerClass = Part::FaceMakerBullseye
  FaceMakerMode = 3
  LengthFwd = 3
  LengthRev = 0
  Placement = pos=(0,8.6,0) rot=(0,0,1;0rad)
  Solid = true
  Symmetric = false
FEATURE [Sketcher::SketchObject] Sketch036  label="supporto per alimentatore"
  ArcFitTolerance = 1e-06
  AttachmentSupport = -> [XZ_Plane]
  ExternalGeometry = -> [Sketch,Sketch016,Sketch022]
  FullyConstrained = true
  MakeInternals = false
  MapMode = 5
  Placement = pos=(0,0,0) rot=(1,0,0;1.5708rad)
  sketch-geometry (5):
    g0: LineSegment StartX=-211.843 StartY=-50.0944 StartZ=0 EndX=-211.843 EndY=-80.4316 EndZ=0
    g1: LineSegment StartX=-211.843 StartY=-50.0944 StartZ=0 EndX=-207.775 EndY=-41.3701 EndZ=0
    g2: LineSegment [constr] StartX=-209.443 StartY=-50.0944 StartZ=0 EndX=-209.443 EndY=-80.4316 EndZ=0
    g3: LineSegment StartX=-207.775 StartY=-41.3701 StartZ=0 EndX=-207.775 EndY=-80.4316 EndZ=0
    g4: LineSegment StartX=-211.843 StartY=-80.4316 StartZ=0 EndX=-207.775 EndY=-80.4316 EndZ=0
  constraints (15):
    c: Vertical(g0)
    c: Coincident(g1,g0)
    c: Vertical(g2)
    c: Tangent(g2,g-5)
    c: Coincident(g3,g1)
    c: Vertical(g3)
    c: DistanceY(g-3,g3) = -2
    c: Tangent(g1,g-8)
    c: DistanceY(g-3,g0) = -2
    c: Coincident(g4,g0)
    c: Coincident(g4,g3)
    c: Tangent(g0,g-6)
    c: DistanceY(g-3,g2) = -2
    c: DistanceY(g2,g0) = 0
    c: DistanceX(g-3,g3) = 6.8
FEATURE [Part::Extrusion] Extrude039  label="Extrude039 supporto alimentatore"
  Base = -> Sketch036
  Dir = (0,-1,2e-16)
  DirMode = 2
  FaceMakerClass = Part::FaceMakerBullseye
  FaceMakerMode = 3
  LengthFwd = 25.2
  LengthRev = 0
  Solid = true
  Symmetric = true
FEATURE [Sketcher::SketchObject] Sketch037  label="scavo per alimentatore"
  ArcFitTolerance = 1e-06
  AttachmentSupport = -> [XZ_Plane]
  ExternalGeometry = -> [Sketch036]
  FullyConstrained = true
  MakeInternals = false
  MapMode = 5
  Placement = pos=(0,0,0) rot=(1,0,0;1.5708rad)
  sketch-geometry (4):
    g0: LineSegment StartX=-209.575 StartY=-50.4316 StartZ=0 EndX=-209.575 EndY=-80.4316 EndZ=0
    g1: LineSegment StartX=-209.575 StartY=-50.4316 StartZ=0 EndX=-207.775 EndY=-50.4316 EndZ=0
    g2: LineSegment StartX=-207.775 StartY=-50.4316 StartZ=0 EndX=-207.775 EndY=-80.4316 EndZ=0
    g3: LineSegment StartX=-207.775 StartY=-80.4316 StartZ=0 EndX=-209.575 EndY=-80.4316 EndZ=0
  constraints (11):
    c: Vertical(g0)
    c: Coincident(g1,g0)
    c: Horizontal(g1)
    c: Coincident(g2,g1)
    c: Vertical(g2)
    c: Coincident(g3,g2)
    c: Coincident(g3,g0)
    c: Horizontal(g3)
    c: DistanceX(g1,g1) = 1.8
    c: Coincident(g2,g-3)
    c: DistanceY(g2,g2) = 30
FEATURE [Part::Extrusion] Extrude040  label="Extrude040 scavo alimentatore"
  Base = -> Sketch037
  Dir = (0,-1,2e-16)
  DirMode = 2
  FaceMakerClass = Part::FaceMakerBullseye
  FaceMakerMode = 3
  LengthFwd = 19.5
  LengthRev = 0
  Solid = true
  Symmetric = true
FEATURE [Part::Extrusion] Extrude031  label="Extrude fermo per scheda micro"
  Base = -> Sketch033
  Dir = (0,-1,2e-16)
  DirMode = 2
  FaceMakerClass = Part::FaceMakerBullseye
  FaceMakerMode = 3
  LengthFwd = 3
  LengthRev = 0
  Placement = pos=(0,8.6,0) rot=(0,0,1;0rad)
  Solid = true
  Symmetric = false
FEATURE [Sketcher::SketchObject] Sketch038  label="scavo driver solenoide"
  ArcFitTolerance = 1e-06
  AttachmentSupport = -> [XZ_Plane]
  ExternalGeometry = -> [Sketch,Sketch036]
  FullyConstrained = true
  MakeInternals = false
  MapMode = 5
  Placement = pos=(0,0,0) rot=(1,0,0;1.5708rad)
  sketch-geometry (8):
    g0: LineSegment StartX=-192.596 StartY=-10.712 StartZ=0 EndX=-196.04 EndY=-9.10605 EndZ=0
    g1: LineSegment StartX=-196.04 StartY=-9.10605 StartZ=0 EndX=-213.368 EndY=-46.2647 EndZ=0
    g2: LineSegment StartX=-192.596 StartY=-10.712 StartZ=0 EndX=-189.152 EndY=-12.3179 EndZ=0
    g3: LineSegment StartX=-189.152 StartY=-12.3179 StartZ=0 EndX=-205.497 EndY=-47.3701 EndZ=0
    g4: LineSegment [constr] StartX=-213.368 StartY=-46.2647 StartZ=0 EndX=-210.649 EndY=-47.5325 EndZ=0
    g5: LineSegment StartX=-213.368 StartY=-46.2647 StartZ=0 EndX=-210.649 EndY=-47.5325 EndZ=0
    g6: LineSegment StartX=-205.497 StartY=-47.3701 StartZ=0 EndX=-207.775 EndY=-47.3701 EndZ=0
    g7: LineSegment StartX=-207.775 StartY=-47.3701 StartZ=0 EndX=-210.649 EndY=-47.5325 EndZ=0
  constraints (23):
    c: Coincident(g1,g0)
    c: Coincident(g3,g2)
    c: Distance(g2) = 3.8
    c: Distance(g1) = 41
    c: Coincident(g4,g1)
    c: Distance(g4) = 3
    c: Perpendicular(g4,g-3)
    c: Parallel(g1,g-3)
    c: Perpendicular(g1,g0)
    c: Distance(g0) = 3.8
    c: Coincident(g5,g1)
    c: Parallel(g3,g-3)
    c: Perpendicular(g2,g3)
    c: Coincident(g2,g0)
    c: PointOnObject(g4,g-3)
    c: Distance(g-3,g4) = 7
    c: Coincident(g6,g3)
    c: Horizontal(g6)
    c: PointOnObject(g6,g-4)
    c: Coincident(g7,g6)
    c: Coincident(g7,g5)
    c: DistanceY(g6,g-4) = 6
    c: Coincident(g5,g4)
FEATURE [Part::Extrusion] Extrude041  label="Extrude scavo driver solenoide"
  Base = -> Sketch038
  Dir = (0,-1,2e-16)
  DirMode = 2
  FaceMakerClass = Part::FaceMakerBullseye
  FaceMakerMode = 3
  LengthFwd = 20.6
  LengthRev = 0
  Solid = true
  Symmetric = true
FEATURE [Sketcher::SketchObject] Sketch039  label="scavo per cavo usb per micro"
  ArcFitTolerance = 1e-06
  AttachmentSupport = -> [XZ_Plane]
  ExternalGeometry = -> [Sketch,Sketch016]
  FullyConstrained = true
  MakeInternals = false
  MapMode = 5
  Placement = pos=(0,0,0) rot=(1,0,0;1.5708rad)
  sketch-geometry (4):
    g0: LineSegment StartX=-82.51 StartY=36.4 StartZ=0 EndX=-74.51 EndY=36.4 EndZ=0
    g1: LineSegment StartX=-74.51 StartY=36.4 StartZ=0 EndX=-74.51 EndY=30.8 EndZ=0
    g2: LineSegment StartX=-74.51 StartY=30.8 StartZ=0 EndX=-82.51 EndY=30.8 EndZ=0
    g3: LineSegment StartX=-82.51 StartY=30.8 StartZ=0 EndX=-82.51 EndY=36.4 EndZ=0
  constraints (11):
    c: Coincident(g1,g0)
    c: Vertical(g1)
    c: Coincident(g2,g1)
    c: Horizontal(g2)
    c: Coincident(g3,g2)
    c: Coincident(g3,g0)
    c: Vertical(g3)
    c: Tangent(g0,g-3)
    c: Tangent(g2,g-4)
    c: Tangent(g3,g-4)
    c: Tangent(g1,g-4)
FEATURE [Part::Extrusion] Extrude042  label="Extrude scavo per cavo usb per micro"
  Base = -> Sketch039
  Dir = (0,-1,2e-16)
  DirMode = 2
  FaceMakerClass = Part::FaceMakerBullseye
  FaceMakerMode = 3
  LengthFwd = 11.2
  LengthRev = 0
  Solid = true
  Symmetric = true
FEATURE [Sketcher::SketchObject] Sketch040  label="scavo saldature alimentatore connettore 5v"
  ArcFitTolerance = 1e-06
  AttachmentSupport = -> [XZ_Plane]
  ExternalGeometry = -> [Sketch037]
  FullyConstrained = true
  MakeInternals = false
  MapMode = 5
  Placement = pos=(0,0,0) rot=(1,0,0;1.5708rad)
  sketch-geometry (4):
    g0: LineSegment StartX=-211.175 StartY=-52.4316 StartZ=0 EndX=-211.175 EndY=-56.4316 EndZ=0
    g1: LineSegment StartX=-211.175 StartY=-52.4316 StartZ=0 EndX=-209.575 EndY=-52.4316 EndZ=0
    g2: LineSegment StartX=-209.575 StartY=-52.4316 StartZ=0 EndX=-209.575 EndY=-56.4316 EndZ=0
    g3: LineSegment StartX=-209.575 StartY=-56.4316 StartZ=0 EndX=-211.175 EndY=-56.4316 EndZ=0
  constraints (11):
    c: Vertical(g0)
    c: Coincident(g1,g0)
    c: Horizontal(g1)
    c: Coincident(g2,g1)
    c: Coincident(g3,g2)
    c: Coincident(g3,g0)
    c: Horizontal(g3)
    c: DistanceX(g1,g1) = 1.6
    c: DistanceY(g2,g2) = 4
    c: Tangent(g2,g-3)
    c: DistanceY(g1,g-3) = 2
FEATURE [Part::Extrusion] Extrude043  label="Extrude scavo saldature alimentatore connettore 5v"
  Base = -> Sketch040
  Dir = (0,-1,2e-16)
  DirMode = 2
  FaceMakerClass = Part::FaceMakerBullseye
  FaceMakerMode = 3
  LengthFwd = 8
  LengthRev = 0
  Solid = true
  Symmetric = true
FEATURE [Sketcher::SketchObject] Sketch041  label="scavo saldature alimentatore connettore 5v verticali"
  ArcFitTolerance = 1e-06
  AttachmentSupport = -> [XZ_Plane]
  ExternalGeometry = -> [Sketch037]
  FullyConstrained = true
  MakeInternals = false
  MapMode = 5
  Placement = pos=(0,0,0) rot=(1,0,0;1.5708rad)
  sketch-geometry (4):
    g0: LineSegment StartX=-211.175 StartY=-53.6316 StartZ=0 EndX=-209.575 EndY=-53.6316 EndZ=0
    g1: LineSegment StartX=-209.575 StartY=-53.6316 StartZ=0 EndX=-209.575 EndY=-76.6316 EndZ=0
    g2: LineSegment StartX=-209.575 StartY=-76.6316 StartZ=0 EndX=-211.175 EndY=-76.6316 EndZ=0
    g3: LineSegment StartX=-211.175 StartY=-76.6316 StartZ=0 EndX=-211.175 EndY=-53.6316 EndZ=0
  constraints (11):
    c: Horizontal(g0)
    c: Coincident(g1,g0)
    c: Coincident(g2,g1)
    c: Horizontal(g2)
    c: Coincident(g3,g2)
    c: Coincident(g3,g0)
    c: Vertical(g3)
    c: DistanceY(g3,g3) = 23
    c: DistanceX(g0,g0) = 1.6
    c: Tangent(g1,g-3)
    c: DistanceY(g0,g-3) = 3.2
FEATURE [Part::Extrusion] Extrude044  label="Extrude scavo saldature alimentatore connettore 5v verticali"
  Base = -> Sketch041
  Dir = (0,-1,2e-16)
  DirMode = 2
  FaceMakerClass = Part::FaceMakerBullseye
  FaceMakerMode = 3
  LengthFwd = 3.2
  LengthRev = 0
  Placement = pos=(0,8.3,0) rot=(0,0,1;0rad)
  Solid = true
  Symmetric = false
FEATURE [Sketcher::SketchObject] Sketch042  label="fermi per driver solenoide e alimentatore"
  ArcFitTolerance = 1e-06
  AttachmentSupport = -> [XZ_Plane]
  ExternalGeometry = -> [Sketch036,Sketch037,Sketch,Sketch038]
  FullyConstrained = true
  MakeInternals = false
  MapMode = 5
  Placement = pos=(0,0,0) rot=(1,0,0;1.5708rad)
  sketch-geometry (27):
    g0: LineSegment StartX=-201.605 StartY=-28.1375 StartZ=0 EndX=-202.534 EndY=-30.1314 EndZ=0
    g1: LineSegment StartX=-202.534 StartY=-30.1314 StartZ=0 EndX=-200.54 EndY=-31.0612 EndZ=0
    g2: LineSegment StartX=-200.54 StartY=-31.0612 StartZ=0 EndX=-199.611 EndY=-29.0673 EndZ=0
    g3: LineSegment StartX=-199.611 StartY=-29.0673 StartZ=0 EndX=-201.605 EndY=-28.1375 EndZ=0
    g4: LineSegment StartX=-202.379 StartY=-26.0113 StartZ=0 EndX=-204.661 EndY=-30.9053 EndZ=0
    g5: LineSegment StartX=-204.661 StartY=-30.9053 StartZ=0 EndX=-201.217 EndY=-32.5113 EndZ=0
    g6: LineSegment StartX=-199.09 StartY=-31.7374 StartZ=0 EndX=-198.161 EndY=-29.7435 EndZ=0
    g7: LineSegment StartX=-198.935 StartY=-27.6172 StartZ=0 EndX=-202.379 EndY=-26.0113 EndZ=0
    g8: LineSegment [constr] StartX=-199.767 StartY=-33.1875 StartZ=0 EndX=-199.09 EndY=-31.7374 EndZ=0
    g9: LineSegment [constr] StartX=-199.767 StartY=-33.1875 StartZ=0 EndX=-201.217 EndY=-32.5113 EndZ=0
    g10: ArcOfCircle CenterX=-199.611 CenterY=-29.0673 CenterZ=0 NormalX=0 NormalY=0 NormalZ=1 AngleXU=0 Radius=1.6 StartAngle=5.84685 EndAngle=7.41765
    g11: GeomPoint [constr] X=-197.484 Y=-28.2934 Z=0
    g12: ArcOfCircle CenterX=-200.54 CenterY=-31.0612 CenterZ=0 NormalX=0 NormalY=0 NormalZ=1 AngleXU=0 Radius=1.6 StartAngle=4.27606 EndAngle=5.84685
    g13: GeomPoint [constr] X=-199.767 Y=-33.1875 Z=0
    g14: LineSegment StartX=-207.775 StartY=-46.8316 StartZ=0 EndX=-207.775 EndY=-50.8316 EndZ=0
    g15: LineSegment StartX=-207.775 StartY=-46.8316 StartZ=0 EndX=-203.775 EndY=-46.8316 EndZ=0
    g16: LineSegment StartX=-203.775 StartY=-46.8316 StartZ=0 EndX=-203.775 EndY=-50.8316 EndZ=0
    g17: LineSegment StartX=-207.775 StartY=-50.8316 StartZ=0 EndX=-203.775 EndY=-50.8316 EndZ=0
    g18: LineSegment StartX=-209.375 StartY=-52.4316 StartZ=0 EndX=-203.775 EndY=-52.4316 EndZ=0
    g19: LineSegment StartX=-202.175 StartY=-50.8316 StartZ=0 EndX=-202.175 EndY=-46.8316 EndZ=0
    g20: LineSegment StartX=-203.775 StartY=-45.2316 StartZ=0 EndX=-209.375 EndY=-45.2316 EndZ=0
    g21: LineSegment StartX=-209.375 StartY=-45.2316 StartZ=0 EndX=-209.375 EndY=-52.4316 EndZ=0
    g22: ArcOfCircle CenterX=-203.775 CenterY=-46.8316 CenterZ=0 NormalX=0 NormalY=0 NormalZ=1 AngleXU=0 Radius=1.6 StartAngle=1.8e-15 EndAngle=1.5708
    g23: GeomPoint [constr] X=-202.175 Y=-45.2316 Z=0
    g24: ArcOfCircle CenterX=-203.775 CenterY=-50.8316 CenterZ=0 NormalX=0 NormalY=0 NormalZ=1 AngleXU=0 Radius=1.6 StartAngle=4.71239 EndAngle=6.28319
    g25: GeomPoint [constr] X=-202.175 Y=-52.4316 Z=0
    g26: LineSegment [constr] StartX=-207.775 StartY=-50.4316 StartZ=0 EndX=-207.775 EndY=-50.8316 EndZ=0
  constraints (69):
    c: Coincident(g1,g0)
    c: Coincident(g2,g1)
    c: Coincident(g3,g2)
    c: Coincident(g3,g0)
    c: Parallel(g0,g2)
    c: Perpendicular(g3,g0)
    c: Perpendicular(g1,g0)
    c: Coincident(g5,g4)
    c: Coincident(g7,g4)
    c: Distance(g3) = 2.2
    c: Distance(g2) = 2.2
    c: Parallel(g6,g2)
    c: Parallel(g6,g4)
    c: Perpendicular(g5,g6)
    c: Perpendicular(g7,g6)
    c: Distance(g13,g11) = 5.4
    c: Distance(g5,g13) = 5.4
    c: Coincident(g9,g8)
    c: Distance(g8) = 1.6
    c: Distance(g9) = 1.6
    c: Perpendicular(g9,g8)
    c: Parallel(g8,g6)
    c: Coincident(g8,g13)
    c: Distance(g8,g1) = 1.6
    c: Distance(g9,g1) = 1.6
    c: Tangent(g0,g-5)
    c: Distance(g0,g-6) = 19.2
    c: PointOnObject(g11,g7)
    c: PointOnObject(g11,g6)
    c: Tangent(g7,g10) = -1.5708
    c: Tangent(g6,g10) = -1.5708
    c: PointOnObject(g13,g5)
    c: Tangent(g5,g12) = -1.5708
    c: Tangent(g6,g12) = -1.5708
    c: Equal(g10,g12)
    c: Coincident(g10,g2)
    c: Vertical(g14)
    c: Coincident(g15,g14)
    c: Horizontal(g15)
    c: Coincident(g16,g15)
    c: Vertical(g16)
    c: Coincident(g17,g14)
    c: Coincident(g17,g16)
    c: Horizontal(g17)
    c: Distance(g16) = 4
    c: Distance(g15) = 4
    c: Horizontal(g18)
    c: Vertical(g19)
    c: Horizontal(g20)
    c: Coincident(g21,g20)
    c: Coincident(g21,g18)
    c: Vertical(g21)
    c: Distance(g20,g23) = 7.2
    c: Distance(g25,g23) = 7.2
    c: DistanceY(g18,g14) = 1.6
    c: DistanceX(g18,g14) = 1.6
    c: PointOnObject(g23,g20)
    c: PointOnObject(g23,g19)
    c: Tangent(g20,g22) = -1.5708
    c: Tangent(g19,g22) = -1.5708
    c: PointOnObject(g25,g19)
    c: Tangent(g18,g24) = -1.5708
    c: Tangent(g19,g24) = -1.5708
    c: Equal(g22,g24)
    c: Coincident(g22,g15)
    c: Vertical(g26)
    c: Distance(g26) = 0.4
    c: Coincident(g26,g-4)
    c: Coincident(g14,g26)
FEATURE [Part::Extrusion] Extrude045  label="Extrude fermi per driver solenoide e alimentatore"
  Base = -> Sketch042
  Dir = (0,-1,2e-16)
  DirMode = 2
  FaceMakerClass = Part::FaceMakerBullseye
  FaceMakerMode = 3
  LengthFwd = 25.2
  LengthRev = 0
  Solid = true
  Symmetric = true
FEATURE [Sketcher::SketchObject] Sketch043  label="scavo pulizia fermo alimentatore"
  ArcFitTolerance = 1e-06
  AttachmentSupport = -> [XZ_Plane]
  ExternalGeometry = -> [Sketch042,Sketch036,Sketch037]
  FullyConstrained = true
  MakeInternals = false
  MapMode = 5
  Placement = pos=(0,0,0) rot=(1,0,0;1.5708rad)
  sketch-geometry (6):
    g0: LineSegment StartX=-209.375 StartY=-52.4316 StartZ=0 EndX=-209.375 EndY=-50.4316 EndZ=0
    g1: LineSegment StartX=-209.375 StartY=-50.4316 StartZ=0 EndX=-207.775 EndY=-50.4316 EndZ=0
    g2: LineSegment StartX=-207.775 StartY=-50.4316 StartZ=0 EndX=-207.775 EndY=-45.2316 EndZ=0
    g3: LineSegment StartX=-207.775 StartY=-45.2316 StartZ=0 EndX=-202.175 EndY=-45.2316 EndZ=0
    g4: LineSegment StartX=-202.175 StartY=-45.2316 StartZ=0 EndX=-202.175 EndY=-52.4316 EndZ=0
    g5: LineSegment StartX=-202.175 StartY=-52.4316 StartZ=0 EndX=-209.375 EndY=-52.4316 EndZ=0
  constraints (13):
    c: Vertical(g0)
    c: Coincident(g1,g0)
    c: Coincident(g2,g1)
    c: Coincident(g3,g2)
    c: Coincident(g4,g3)
    c: Coincident(g5,g4)
    c: Coincident(g5,g0)
    c: Horizontal(g5)
    c: Coincident(g0,g-6)
    c: Tangent(g1,g-8)
    c: Tangent(g2,g-4)
    c: Tangent(g3,g-7)
    c: Tangent(g4,g-3)
FEATURE [Part::Extrusion] Extrude046  label="Extrude scavo pulizia fermo alimentatore"
  Base = -> Sketch043
  Dir = (0,-1,2e-16)
  DirMode = 2
  FaceMakerClass = Part::FaceMakerBullseye
  FaceMakerMode = 3
  LengthFwd = 19.5
  LengthRev = 0
  Solid = true
  Symmetric = true
FEATURE [Sketcher::SketchObject] Sketch044  label="buchini per fissaggio oled"
  ArcFitTolerance = 1e-06
  AttachmentSupport = -> [YZ_Plane]
  ExternalGeometry = -> [Sketch]
  FullyConstrained = true
  MakeInternals = false
  MapMode = 5
  Placement = pos=(0,0,0) rot=(0.57735,0.57735,0.57735;2.0944rad)
  sketch-geometry (5):
    g0: LineSegment [constr] StartX=1.5e-14 StartY=67.3588 StartZ=0 EndX=0 EndY=64.3588 EndZ=0
    g1: LineSegment [constr] StartX=0 StartY=64.3588 StartZ=0 EndX=10.4 EndY=64.3588 EndZ=0
    g2: LineSegment [constr] StartX=0 StartY=64.3588 StartZ=0 EndX=-10.4 EndY=64.3588 EndZ=0
    g3: Circle CenterX=10.4 CenterY=64.3588 CenterZ=0 NormalX=0 NormalY=0 NormalZ=1 AngleXU=0 Radius=1.5
    g4: Circle CenterX=-10.4 CenterY=64.3588 CenterZ=0 NormalX=0 NormalY=0 NormalZ=1 AngleXU=0 Radius=1.5
  constraints (13):
    c: Distance(g0) = 3
    c: PointOnObject(g0,g-2)
    c: Coincident(g1,g0)
    c: Horizontal(g1)
    c: Coincident(g2,g0)
    c: Horizontal(g2)
    c: DistanceX(g1,g1) = 10.4
    c: Coincident(g3,g1)
    c: Diameter(g4) = 3
    c: Coincident(g4,g2)
    c: Coincident(g0,g-7)
    c: Equal(g1,g2)
    c: Equal(g4,g3)
FEATURE [Part::Extrusion] Extrude047  label="Extrude buchini per fissaggio oled"
  Base = -> Sketch044
  Dir = (1,0,0)
  DirMode = 2
  FaceMakerClass = Part::FaceMakerBullseye
  FaceMakerMode = 3
  LengthFwd = 10
  LengthRev = 0
  Placement = pos=(-186,0,0) rot=(0,0,1;0rad)
  Solid = true
  Symmetric = false
FEATURE [Sketcher::SketchObject] Sketch046  label="scavo 5x5 neopixel"
  ArcFitTolerance = 1e-06
  AttachmentSupport = -> [YZ_Plane002]
  FullyConstrained = true
  MakeInternals = false
  MapMode = 5
  Placement = pos=(0,0,0) rot=(0.57735,0.57735,0.57735;2.0944rad)
  sketch-geometry (4):
    g0: LineSegment StartX=-2.7 StartY=2.7 StartZ=0 EndX=2.7 EndY=2.7 EndZ=0
    g1: LineSegment StartX=2.7 StartY=2.7 StartZ=0 EndX=2.7 EndY=-2.7 EndZ=0
    g2: LineSegment StartX=2.7 StartY=-2.7 StartZ=0 EndX=-2.7 EndY=-2.7 EndZ=0
    g3: LineSegment StartX=-2.7 StartY=-2.7 StartZ=0 EndX=-2.7 EndY=2.7 EndZ=0
  constraints (11):
    c: Horizontal(g0)
    c: Coincident(g1,g0)
    c: Vertical(g1)
    c: Coincident(g2,g1)
    c: Horizontal(g2)
    c: Coincident(g3,g2)
    c: Coincident(g3,g0)
    c: Vertical(g3)
    c: DistanceX(g0,g0) = 5.4
    c: DistanceY(g1,g1) = 5.4
    c: Symmetric(g0,g1,g-1)
FEATURE [Sketcher::SketchObject] Sketch047  label="scavo 10x10 neopixel corpo"
  ArcFitTolerance = 1e-06
  AttachmentOffset = pos=(0,0,1) rot=(0,0,1;0rad)
  AttachmentSupport = -> [YZ_Plane002]
  FullyConstrained = true
  MakeInternals = false
  MapMode = 5
  Placement = pos=(1,0,0) rot=(0.57735,0.57735,0.57735;2.0944rad)
  sketch-geometry (4):
    g0: LineSegment StartX=-5 StartY=5.1 StartZ=0 EndX=5 EndY=5.1 EndZ=0
    g1: LineSegment StartX=5 StartY=5.1 StartZ=0 EndX=5 EndY=-5.1 EndZ=0
    g2: LineSegment StartX=5 StartY=-5.1 StartZ=0 EndX=-5 EndY=-5.1 EndZ=0
    g3: LineSegment StartX=-5 StartY=-5.1 StartZ=0 EndX=-5 EndY=5.1 EndZ=0
  constraints (11):
    c: Horizontal(g0)
    c: Coincident(g1,g0)
    c: Vertical(g1)
    c: Coincident(g2,g1)
    c: Horizontal(g2)
    c: Coincident(g3,g2)
    c: Coincident(g3,g0)
    c: Vertical(g3)
    c: DistanceX(g0,g0) = 10
    c: DistanceY(g1,g1) = 10.2
    c: Symmetric(g0,g2,g-1)
FEATURE [Sketcher::SketchObject] Sketch048  label="buco per perno blocco neopixel"
  ArcFitTolerance = 1e-06
  AttachmentSupport = -> [XZ_Plane002]
  FullyConstrained = true
  MakeInternals = false
  MapMode = 5
  Placement = pos=(0,0,0) rot=(1,0,0;1.5708rad)
  sketch-geometry (4):
    g0: LineSegment StartX=3 StartY=1.2 StartZ=0 EndX=3 EndY=-1.2 EndZ=0
    g1: LineSegment StartX=3 StartY=-1.2 StartZ=0 EndX=5.4 EndY=-1.2 EndZ=0
    g2: LineSegment StartX=5.4 StartY=-1.2 StartZ=0 EndX=5.4 EndY=1.2 EndZ=0
    g3: LineSegment StartX=5.4 StartY=1.2 StartZ=0 EndX=3 EndY=1.2 EndZ=0
  constraints (11):
    c: Coincident(g1,g0)
    c: Horizontal(g1)
    c: Coincident(g2,g1)
    c: Vertical(g2)
    c: Coincident(g3,g2)
    c: Coincident(g3,g0)
    c: Horizontal(g3)
    c: DistanceX(g1,g1) = 2.4
    c: DistanceY(g2,g2) = 2.4
    c: Symmetric(g0,g0,g-1)
    c: DistanceX(g-1,g0) = 3
FEATURE [Sketcher::SketchObject] Sketch045  label="blocco principale per neopixel"
  ArcFitTolerance = 1e-06
  AttachmentSupport = -> [XZ_Plane002]
  ExternalGeometry = -> [Sketch048]
  FullyConstrained = true
  MakeInternals = false
  MapMode = 5
  Placement = pos=(0,0,0) rot=(1,0,0;1.5708rad)
  sketch-geometry (6):
    g0: LineSegment StartX=0 StartY=5.1 StartZ=0 EndX=0 EndY=-5.1 EndZ=0
    g1: LineSegment StartX=0 StartY=-5.1 StartZ=0 EndX=3 EndY=-5.1 EndZ=0
    g2: LineSegment StartX=7 StartY=-1.1 StartZ=0 EndX=7 EndY=5.1 EndZ=0
    g3: LineSegment StartX=7 StartY=5.1 StartZ=0 EndX=0 EndY=5.1 EndZ=0
    g4: ArcOfCircle CenterX=3 CenterY=-1.1 CenterZ=0 NormalX=0 NormalY=0 NormalZ=1 AngleXU=0 Radius=4 StartAngle=4.71239 EndAngle=6.28319
    g5: GeomPoint [constr] X=7 Y=-5.1 Z=0
  constraints (15):
    c: Vertical(g0)
    c: Coincident(g1,g0)
    c: Horizontal(g1)
    c: Vertical(g2)
    c: Coincident(g3,g2)
    c: Coincident(g3,g0)
    c: Horizontal(g3)
    c: DistanceY(g0,g0) = 10.2
    c: Symmetric(g0,g0,g-1)
    c: DistanceX(g3,g3) = 7
    c: PointOnObject(g5,g2)
    c: PointOnObject(g5,g1)
    c: Tangent(g2,g4) = -1.5708
    c: Tangent(g1,g4) = -1.5708
    c: DistanceX(g-3,g1) = 0
FEATURE [Sketcher::SketchObject] Sketch049  label="rinforzi esterni per corpo neopoixel"
  ArcFitTolerance = 1e-06
  AttachmentSupport = -> [XZ_Plane002]
  ExternalGeometry = -> [Sketch045]
  FullyConstrained = true
  MakeInternals = false
  MapMode = 5
  Placement = pos=(0,0,0) rot=(1,0,0;1.5708rad)
  sketch-geometry (8):
    g0: LineSegment StartX=1 StartY=-4.1 StartZ=0 EndX=2 EndY=-4.1 EndZ=0
    g1: LineSegment StartX=2 StartY=-4.1 StartZ=0 EndX=2 EndY=-5.1 EndZ=0
    g2: LineSegment StartX=2 StartY=-5.1 StartZ=0 EndX=1 EndY=-5.1 EndZ=0
    g3: LineSegment StartX=1 StartY=-5.1 StartZ=0 EndX=1 EndY=-4.1 EndZ=0
    g4: LineSegment StartX=1 StartY=5.1 StartZ=0 EndX=2 EndY=5.1 EndZ=0
    g5: LineSegment StartX=2 StartY=5.1 StartZ=0 EndX=2 EndY=4.1 EndZ=0
    g6: LineSegment StartX=2 StartY=4.1 StartZ=0 EndX=1 EndY=4.1 EndZ=0
    g7: LineSegment StartX=1 StartY=4.1 StartZ=0 EndX=1 EndY=5.1 EndZ=0
  constraints (24):
    c: Horizontal(g0)
    c: Coincident(g1,g0)
    c: Vertical(g1)
    c: Coincident(g2,g1)
    c: Horizontal(g2)
    c: Coincident(g3,g2)
    c: Coincident(g3,g0)
    c: Vertical(g3)
    c: Horizontal(g4)
    c: Coincident(g5,g4)
    c: Vertical(g5)
    c: Coincident(g6,g5)
    c: Horizontal(g6)
    c: Coincident(g7,g6)
    c: Coincident(g7,g4)
    c: Vertical(g7)
    c: DistanceX(g4,g4) = 1
    c: DistanceY(g5,g5) = 1
    c: DistanceX(g0,g0) = 1
    c: DistanceY(g1,g1) = 1
    c: DistanceX(g-3,g4) = 1
    c: DistanceY(g-3,g4) = 0
    c: DistanceX(g-4,g2) = 1
    c: DistanceY(g2,g-4) = 0
FEATURE [Sketcher::SketchObject] Sketch052  label="scavo saldature driver solenoide"
  ArcFitTolerance = 1e-06
  AttachmentSupport = -> [XZ_Plane]
  ExternalGeometry = -> [Sketch038]
  FullyConstrained = true
  MakeInternals = false
  MapMode = 5
  Placement = pos=(0,0,0) rot=(1,0,0;1.5708rad)
  sketch-geometry (4):
    g0: LineSegment StartX=-196.403 StartY=-8.937 StartZ=0 EndX=-198.093 EndY=-12.5622 EndZ=0
    g1: LineSegment StartX=-198.093 StartY=-12.5622 StartZ=0 EndX=-197.731 EndY=-12.7313 EndZ=0
    g2: LineSegment StartX=-197.731 StartY=-12.7313 StartZ=0 EndX=-196.04 EndY=-9.10605 EndZ=0
    g3: LineSegment StartX=-196.04 StartY=-9.10605 StartZ=0 EndX=-196.403 EndY=-8.937 EndZ=0
  constraints (11):
    c: Coincident(g1,g0)
    c: Coincident(g2,g1)
    c: Coincident(g3,g2)
    c: Coincident(g3,g0)
    c: Parallel(g2,g0)
    c: Perpendicular(g2,g3)
    c: Perpendicular(g1,g2,g1) = 1.5708
    c: Parallel(g2,g-3)
    c: Distance(g2) = 4
    c: Distance(g3) = 0.4
    c: Coincident(g2,g-3)
FEATURE [Part::Extrusion] Extrude055  label="Extrude scavo saldature driver solenoide"
  Base = -> Sketch052
  Dir = (0,-1,2e-16)
  DirMode = 2
  FaceMakerClass = Part::FaceMakerBullseye
  FaceMakerMode = 3
  LengthFwd = 6
  LengthRev = 0
  Solid = true
  Symmetric = true
FEATURE [Sketcher::SketchObject] Sketch053  label="scavo saldature rumble"
  ArcFitTolerance = 1e-06
  AttachmentSupport = -> [XZ_Plane]
  ExternalGeometry = -> [Sketch019]
  FullyConstrained = true
  MakeInternals = false
  MapMode = 5
  Placement = pos=(0,0,0) rot=(1,0,0;1.5708rad)
  sketch-geometry (4):
    g0: LineSegment StartX=-169.451 StartY=-56.8615 StartZ=0 EndX=-170.687 EndY=-60.6657 EndZ=0
    g1: LineSegment StartX=-170.687 StartY=-60.6657 StartZ=0 EndX=-169.546 EndY=-61.0365 EndZ=0
    g2: LineSegment StartX=-169.546 StartY=-61.0365 StartZ=0 EndX=-168.31 EndY=-57.2323 EndZ=0
    g3: LineSegment StartX=-168.31 StartY=-57.2323 StartZ=0 EndX=-169.451 EndY=-56.8615 EndZ=0
  constraints (11):
    c: Coincident(g1,g0)
    c: Coincident(g2,g1)
    c: Coincident(g3,g2)
    c: Coincident(g3,g0)
    c: Parallel(g0,g2)
    c: Perpendicular(g3,g0)
    c: Perpendicular(g1,g0)
    c: Parallel(g0,g-3)
    c: Distance(g0) = 4
    c: Coincident(g0,g-3)
    c: Distance(g1) = 1.2
FEATURE [Part::Extrusion] Extrude056  label="Extrude scavo saldature rumble"
  Base = -> Sketch053
  Dir = (0,-1,2e-16)
  DirMode = 2
  FaceMakerClass = Part::FaceMakerBullseye
  FaceMakerMode = 3
  LengthFwd = 8.4
  LengthRev = 0
  Solid = true
  Symmetric = true
FEATURE [Sketcher::SketchObject] Sketch054  label="scavo saldature alimentatore connettore USB"
  ArcFitTolerance = 1e-06
  AttachmentSupport = -> [XZ_Plane]
  ExternalGeometry = -> [Sketch037]
  FullyConstrained = true
  MakeInternals = false
  MapMode = 5
  Placement = pos=(0,0,0) rot=(1,0,0;1.5708rad)
  sketch-geometry (4):
    g0: LineSegment StartX=-209.575 StartY=-80.4316 StartZ=0 EndX=-210.375 EndY=-80.4316 EndZ=0
    g1: LineSegment StartX=-210.375 StartY=-80.4316 StartZ=0 EndX=-210.375 EndY=-72.4316 EndZ=0
    g2: LineSegment StartX=-210.375 StartY=-72.4316 StartZ=0 EndX=-209.575 EndY=-72.4316 EndZ=0
    g3: LineSegment StartX=-209.575 StartY=-72.4316 StartZ=0 EndX=-209.575 EndY=-80.4316 EndZ=0
  constraints (11):
    c: Horizontal(g0)
    c: Coincident(g1,g0)
    c: Vertical(g1)
    c: Coincident(g2,g1)
    c: Horizontal(g2)
    c: Coincident(g3,g2)
    c: Coincident(g3,g0)
    c: Vertical(g3)
    c: DistanceX(g0,g0) = 0.8
    c: DistanceY(g3,g3) = 8
    c: Coincident(g0,g-4)
FEATURE [Part::Extrusion] Extrude057  label="Extrude scavo saldature alimentatore connettore USB"
  Base = -> Sketch054
  Dir = (0,-1,2e-16)
  DirMode = 2
  FaceMakerClass = Part::FaceMakerBullseye
  FaceMakerMode = 3
  LengthFwd = 11
  LengthRev = 0
  Solid = true
  Symmetric = true
FEATURE [Sketcher::SketchObject] Sketch055  label="buco interno per micro switch"
  ArcFitTolerance = 1e-06
  AttachmentSupport = -> [XZ_Plane]
  ExternalGeometry = -> [Sketch]
  FullyConstrained = true
  MakeInternals = false
  MapMode = 5
  Placement = pos=(0,0,0) rot=(1,0,0;1.5708rad)
  sketch-geometry (11):
    g0: LineSegment [constr] StartX=-194.483 StartY=34.2854 StartZ=0 EndX=-196.022 EndY=30.0568 EndZ=0
    g1: LineSegment [constr] StartX=-196.022 StartY=30.0568 StartZ=0 EndX=-197.561 EndY=25.8282 EndZ=0
    g2: LineSegment [constr] StartX=-196.022 StartY=30.0568 StartZ=0 EndX=-194.143 EndY=29.3727 EndZ=0
    g3: LineSegment [constr] StartX=-196.022 StartY=30.0568 StartZ=0 EndX=-197.902 EndY=30.7408 EndZ=0
    g4: LineSegment StartX=-196.362 StartY=34.9694 StartZ=0 EndX=-192.604 EndY=33.6014 EndZ=0
    g5: LineSegment StartX=-199.441 StartY=26.5122 StartZ=0 EndX=-195.682 EndY=25.1441 EndZ=0
    g6: LineSegment StartX=-192.604 StartY=33.6014 StartZ=0 EndX=-195.682 EndY=25.1441 EndZ=0
    g7: LineSegment StartX=-196.362 StartY=34.9694 StartZ=0 EndX=-199.441 EndY=26.5122 EndZ=0
    g8: GeomPoint [constr] X=-187.821 Y=29.2 Z=0
    g9: LineSegment [constr] StartX=-188.505 StartY=27.3206 StartZ=0 EndX=-196.022 EndY=30.0568 EndZ=0
    g10: LineSegment [constr] StartX=-187.821 StartY=29.2 StartZ=0 EndX=-188.505 EndY=27.3206 EndZ=0
  constraints (27):
    c: Coincident(g2,g0)
    c: Parallel(g0,g-3)
    c: Tangent(g1,g0) = -1.5708
    c: Perpendicular(g0,g2)
    c: Tangent(g2,g3)
    c: Distance(g0,g1) = 9
    c: Equal(g0,g1)
    c: Distance(g3,g2) = 4
    c: Equal(g2,g3)
    c: Parallel(g3,g4)
    c: Symmetric(g4,g4,g0)
    c: Parallel(g6,g1)
    c: Parallel(g7,g1)
    c: Symmetric(g6,g6,g2)
    c: Symmetric(g5,g5,g1)
    c: Symmetric(g7,g7,g3)
    c: Coincident(g7,g4)
    c: Coincident(g6,g4)
    c: Coincident(g5,g6)
    c: Symmetric(g-3,g-3,g8)
    c: Perpendicular(g-3,g9)
    c: Distance(g9) = 8
    c: Coincident(g3,g9)
    c: Coincident(g10,g8)
    c: Parallel(g10,g-3)
    c: Distance(g10) = 2
    c: Coincident(g10,g9)
FEATURE [Sketcher::SketchObject] Sketch056  label="buco esterno per micro switch"
  ArcFitTolerance = 1e-06
  AttachmentSupport = -> [XZ_Plane]
  ExternalGeometry = -> [Sketch055]
  FullyConstrained = true
  MakeInternals = false
  MapMode = 5
  Placement = pos=(0,0,0) rot=(1,0,0;1.5708rad)
  sketch-geometry (17):
    g0: GeomPoint [constr] X=-194.143 Y=29.3727 Z=0
    g1: GeomPoint [constr] X=-194.483 Y=34.2854 Z=0
    g2: GeomPoint [constr] X=-197.902 Y=30.7408 Z=0
    g3: GeomPoint [constr] X=-197.561 Y=25.8282 Z=0
    g4: GeomPoint [constr] X=-196.022 Y=30.0568 Z=0
    g5: LineSegment [constr] StartX=-194.483 StartY=34.2854 StartZ=0 EndX=-196.022 EndY=30.0568 EndZ=0
    g6: LineSegment [constr] StartX=-196.022 StartY=30.0568 StartZ=0 EndX=-197.561 EndY=25.8282 EndZ=0
    g7: LineSegment [constr] StartX=-197.902 StartY=30.7408 StartZ=0 EndX=-196.022 EndY=30.0568 EndZ=0
    g8: LineSegment [constr] StartX=-196.022 StartY=30.0568 StartZ=0 EndX=-194.143 EndY=29.3727 EndZ=0
    g9: LineSegment [constr] StartX=-195.338 StartY=31.9362 StartZ=0 EndX=-196.022 EndY=30.0568 EndZ=0
    g10: LineSegment [constr] StartX=-196.022 StartY=30.0568 StartZ=0 EndX=-196.706 EndY=28.1774 EndZ=0
    g11: LineSegment [constr] StartX=-196.022 StartY=30.0568 StartZ=0 EndX=-196.821 EndY=30.3475 EndZ=0
    g12: LineSegment [constr] StartX=-196.022 StartY=30.0568 StartZ=0 EndX=-195.223 EndY=29.7661 EndZ=0
    g13: LineSegment StartX=-194.539 StartY=31.6454 StartZ=0 EndX=-195.907 EndY=27.8867 EndZ=0
    g14: LineSegment StartX=-196.137 StartY=32.2269 StartZ=0 EndX=-197.505 EndY=28.4681 EndZ=0
    g15: LineSegment StartX=-196.137 StartY=32.2269 StartZ=0 EndX=-194.539 EndY=31.6454 EndZ=0
    g16: LineSegment StartX=-197.505 StartY=28.4681 StartZ=0 EndX=-195.907 EndY=27.8867 EndZ=0
  constraints (34):
    c: Symmetric(g-5,g-5,g1)
    c: Symmetric(g-5,g-6,g0)
    c: Symmetric(g-6,g-6,g3)
    c: Symmetric(g-5,g-6,g2)
    c: Coincident(g5,g1)
    c: Coincident(g5,g4)
    c: Coincident(g6,g4)
    c: Coincident(g6,g3)
    c: Equal(g5,g6)
    c: Coincident(g7,g2)
    c: Coincident(g7,g4)
    c: Coincident(g8,g4)
    c: Coincident(g8,g0)
    c: Equal(g7,g8)
    c: Coincident(g11,g9)
    c: Coincident(g12,g9)
    c: Tangent(g10,g9) = -1.5708
    c: Perpendicular(g11,g9)
    c: Parallel(g9,g-4)
    c: Equal(g9,g10)
    c: Parallel(g12,g11)
    c: Equal(g11,g12)
    c: Distance(g11,g12) = 1.7
    c: Distance(g9,g10) = 4
    c: Symmetric(g13,g13,g12)
    c: Parallel(g13,g9)
    c: Symmetric(g14,g14,g11)
    c: Symmetric(g15,g15,g9)
    c: Parallel(g15,g11)
    c: Symmetric(g16,g16,g10)
    c: Coincident(g16,g14)
    c: Coincident(g15,g14)
    c: Coincident(g13,g15)
    c: Coincident(g9,g4)
FEATURE [Sketcher::SketchObject] Sketch057  label="buco interno per SWITCH"
  ArcFitTolerance = 1e-06
  AttachmentSupport = -> [XZ_Plane]
  ExternalGeometry = -> [Sketch]
  FullyConstrained = true
  MakeInternals = false
  MapMode = 5
  Placement = pos=(0,0,0) rot=(1,0,0;1.5708rad)
  sketch-geometry (10):
    g0: GeomPoint [constr] X=-187.821 Y=29.2 Z=0
    g1: LineSegment [constr] StartX=-188.505 StartY=27.3206 StartZ=0 EndX=-193.203 EndY=29.0307 EndZ=0
    g2: LineSegment [constr] StartX=-190.809 StartY=35.6086 StartZ=0 EndX=-195.597 EndY=22.4529 EndZ=0
    g3: GeomPoint [constr] X=-193.203 Y=29.0307 Z=0
    g4: LineSegment [constr] StartX=-196.492 StartY=30.2278 StartZ=0 EndX=-189.914 EndY=27.8336 EndZ=0
    g5: LineSegment StartX=-194.098 StartY=36.8056 StartZ=0 EndX=-187.52 EndY=34.4115 EndZ=0
    g6: LineSegment StartX=-194.098 StartY=36.8056 StartZ=0 EndX=-198.886 EndY=23.6499 EndZ=0
    g7: LineSegment StartX=-187.52 StartY=34.4115 StartZ=0 EndX=-192.308 EndY=21.2558 EndZ=0
    g8: LineSegment StartX=-198.886 StartY=23.6499 StartZ=0 EndX=-192.308 EndY=21.2558 EndZ=0
    g9: LineSegment [constr] StartX=-187.821 StartY=29.2 StartZ=0 EndX=-188.505 EndY=27.3206 EndZ=0
  constraints (23):
    c: Symmetric(g-3,g-3,g0)
    c: Perpendicular(g1,g-3)
    c: Parallel(g2,g-3)
    c: Symmetric(g2,g2,g3)
    c: Perpendicular(g2,g4)
    c: Symmetric(g4,g4,g3)
    c: Distance(g2) = 14
    c: Distance(g4) = 7
    c: Distance(g1) = 5
    c: Parallel(g5,g4)
    c: Parallel(g7,g2)
    c: Symmetric(g5,g5,g2)
    c: Symmetric(g6,g6,g4)
    c: Symmetric(g7,g7,g4)
    c: Symmetric(g8,g8,g2)
    c: Coincident(g6,g5)
    c: Coincident(g7,g5)
    c: Coincident(g8,g7)
    c: Coincident(g3,g1)
    c: Coincident(g9,g0)
    c: Parallel(g9,g-3)
    c: Distance(g9) = 2
    c: Coincident(g1,g9)
FEATURE [Sketcher::SketchObject] Sketch058  label="buco esterno per SWITCH"
  ArcFitTolerance = 1e-06
  AttachmentSupport = -> [XZ_Plane]
  ExternalGeometry = -> [Sketch057]
  FullyConstrained = true
  MakeInternals = false
  MapMode = 5
  Placement = pos=(0,0,0) rot=(1,0,0;1.5708rad)
  sketch-geometry (12):
    g0: GeomPoint [constr] X=-190.809 Y=35.6086 Z=0
    g1: GeomPoint [constr] X=-196.492 Y=30.2278 Z=0
    g2: GeomPoint [constr] X=-189.914 Y=27.8336 Z=0
    g3: GeomPoint [constr] X=-195.597 Y=22.4529 Z=0
    g4: GeomPoint [constr] X=-193.203 Y=29.0307 Z=0
    g5: LineSegment [constr] StartX=-192.006 StartY=32.3196 StartZ=0 EndX=-194.4 EndY=25.7418 EndZ=0
    g6: GeomPoint [constr] X=-193.203 Y=29.0307 Z=0
    g7: LineSegment [constr] StartX=-195.082 StartY=29.7148 StartZ=0 EndX=-191.324 EndY=28.3467 EndZ=0
    g8: LineSegment StartX=-193.885 StartY=33.0037 StartZ=0 EndX=-190.127 EndY=31.6356 EndZ=0
    g9: LineSegment StartX=-190.127 StartY=31.6356 StartZ=0 EndX=-192.521 EndY=25.0578 EndZ=0
    g10: LineSegment StartX=-196.28 StartY=26.4258 StartZ=0 EndX=-192.521 EndY=25.0578 EndZ=0
    g11: LineSegment StartX=-193.885 StartY=33.0037 StartZ=0 EndX=-196.28 EndY=26.4258 EndZ=0
  constraints (21):
    c: Symmetric(g-6,g-6,g3)
    c: Symmetric(g-4,g-6,g2)
    c: Symmetric(g-5,g-4,g0)
    c: Symmetric(g-5,g-6,g1)
    c: Symmetric(g1,g2,g4)
    c: Parallel(g5,g-4)
    c: Symmetric(g5,g5,g6)
    c: Perpendicular(g7,g5)
    c: Symmetric(g7,g7,g6)
    c: Distance(g5) = 7
    c: Distance(g7) = 4
    c: Parallel(g8,g7)
    c: Parallel(g11,g5)
    c: Symmetric(g8,g8,g5)
    c: Symmetric(g9,g9,g7)
    c: Symmetric(g10,g10,g5)
    c: Symmetric(g11,g11,g7)
    c: Coincident(g11,g8)
    c: Coincident(g9,g8)
    c: Coincident(g9,g10)
    c: Coincident(g6,g4)
FEATURE [Part::Extrusion] Extrude060  label="Extrude buco interno per SWITCH destro"
  Base = -> Sketch057
  Dir = (0,-1,2e-16)
  DirMode = 2
  FaceMakerClass = Part::FaceMakerBullseye
  FaceMakerMode = 3
  LengthFwd = 13.2
  LengthRev = 0
  Placement = pos=(0,2.6,0) rot=(0,0,1;0rad)
  Solid = true
  Symmetric = false
FEATURE [Part::Extrusion] Extrude061  label="Extrude buco esterno per SWITCH destro"
  Base = -> Sketch058
  Dir = (0,-1,2e-16)
  DirMode = 2
  FaceMakerClass = Part::FaceMakerBullseye
  FaceMakerMode = 3
  LengthFwd = 2
  LengthRev = 0
  Placement = pos=(0,-10.6,0) rot=(0,0,1;0rad)
  Solid = true
  Symmetric = false
FEATURE [Sketcher::SketchObject] Sketch059  label="buco per spazio introduzione SWITCH"
  ArcFitTolerance = 1e-06
  AttachmentSupport = -> [XZ_Plane]
  ExternalGeometry = -> [Sketch057,Sketch010]
  FullyConstrained = true
  MakeInternals = false
  MapMode = 5
  Placement = pos=(0,0,0) rot=(1,0,0;1.5708rad)
  sketch-geometry (8):
    g0: LineSegment [constr] StartX=-201.368 StartY=36.3521 StartZ=0 EndX=-195.094 EndY=34.0687 EndZ=0
    g1: LineSegment [constr] StartX=-194.098 StartY=36.8056 StartZ=0 EndX=-195.094 EndY=34.0687 EndZ=0
    g2: LineSegment StartX=-198.658 StartY=24.2771 StartZ=0 EndX=-199.654 EndY=21.5401 EndZ=0
    g3: LineSegment StartX=-199.654 StartY=21.5401 StartZ=0 EndX=-181.196 EndY=14.822 EndZ=0
    g4: LineSegment StartX=-181.196 StartY=14.822 StartZ=0 EndX=-180.2 EndY=17.559 EndZ=0
    g5: LineSegment StartX=-180.2 StartY=17.559 StartZ=0 EndX=-198.658 EndY=24.2771 EndZ=0
    g6: LineSegment [constr] StartX=-204.932 StartY=26.5605 StartZ=0 EndX=-198.658 EndY=24.2771 EndZ=0
    g7: LineSegment [constr] StartX=-198.658 StartY=24.2771 StartZ=0 EndX=-199.654 EndY=21.5401 EndZ=0
  constraints (20):
    c: Parallel(g1,g-3)
    c: Parallel(g0,g-4)
    c: Coincident(g0,g-4)
    c: Coincident(g1,g-3)
    c: Coincident(g0,g1)
    c: Coincident(g3,g2)
    c: Coincident(g4,g3)
    c: Coincident(g5,g4)
    c: Coincident(g5,g2)
    c: Parallel(g5,g-5)
    c: Parallel(g3,g-5)
    c: Parallel(g4,g-6)
    c: DistanceX(g-6,g4) = 0
    c: Coincident(g6,g-5)
    c: Equal(g6,g0)
    c: Coincident(g7,g6)
    c: Equal(g7,g1)
    c: Tangent(g7,g-3)
    c: Coincident(g2,g6)
    c: Coincident(g2,g7)
FEATURE [Part::Extrusion] Extrude062  label="Extrude buco per spazio introduzione SWITCH"
  Base = -> Sketch059
  Dir = (0,-1,2e-16)
  DirMode = 2
  FaceMakerClass = Part::FaceMakerBullseye
  FaceMakerMode = 3
  LengthFwd = 13.2
  LengthRev = 0
  Solid = true
  Symmetric = true
FEATURE [Part::Extrusion] Extrude063  label="Extrude buco interno per SWITCH sinistro"
  Base = -> Sketch057
  Dir = (0,-1,2e-16)
  DirMode = 2
  FaceMakerClass = Part::FaceMakerBullseye
  FaceMakerMode = 3
  LengthFwd = 13.2
  LengthRev = 0
  Placement = pos=(0,10.6,0) rot=(0,0,1;0rad)
  Solid = true
  Symmetric = false
FEATURE [Part::Extrusion] Extrude064  label="Extrude buco esterno per SWITCH sinistro"
  Base = -> Sketch058
  Dir = (0,-1,2e-16)
  DirMode = 2
  FaceMakerClass = Part::FaceMakerBullseye
  FaceMakerMode = 3
  LengthFwd = 2
  LengthRev = 0
  Placement = pos=(0,12.6,0) rot=(0,0,1;0rad)
  Solid = true
  Symmetric = false
FEATURE [Sketcher::SketchObject] Sketch061  label="struttura esterna blocco switch"
  ArcFitTolerance = 1e-06
  AttachmentSupport = -> [XZ_Plane003]
  FullyConstrained = true
  MakeInternals = false
  MapMode = 5
  Placement = pos=(0,0,0) rot=(1,0,0;1.5708rad)
  sketch-geometry (5):
    g0: LineSegment StartX=-1 StartY=-5.1 StartZ=0 EndX=1 EndY=-5.1 EndZ=0
    g1: LineSegment StartX=1 StartY=-5.1 StartZ=0 EndX=1 EndY=5.1 EndZ=0
    g2: LineSegment StartX=1 StartY=5.1 StartZ=0 EndX=-1 EndY=5.1 EndZ=0
    g3: LineSegment StartX=-1 StartY=5.1 StartZ=0 EndX=-1 EndY=-5.1 EndZ=0
    g4: GeomPoint [constr] X=0 Y=0 Z=0
  constraints (12):
    c: Coincident(g0,g1)
    c: Coincident(g1,g2)
    c: Coincident(g2,g3)
    c: Coincident(g3,g0)
    c: Horizontal(g0)
    c: Horizontal(g2)
    c: Vertical(g1)
    c: Vertical(g3)
    c: Symmetric(g2,g0,g4)
    c: Distance(g1,g3) = 2
    c: Distance(g0,g2) = 10.2
    c: Coincident(g4,g-1)
FEATURE [Sketcher::SketchObject] Sketch062  label="struttura interna blocco switch"
  ArcFitTolerance = 1e-06
  AttachmentSupport = -> [XZ_Plane003]
  ExternalGeometry = -> [Sketch061]
  FullyConstrained = true
  MakeInternals = false
  MapMode = 5
  Placement = pos=(0,0,0) rot=(1,0,0;1.5708rad)
  sketch-geometry (5):
    g0: LineSegment StartX=-1 StartY=3.1 StartZ=0 EndX=-1 EndY=-3.1 EndZ=0
    g1: LineSegment StartX=-1 StartY=-3.1 StartZ=0 EndX=1 EndY=-3.1 EndZ=0
    g2: LineSegment StartX=1 StartY=-3.1 StartZ=0 EndX=1 EndY=3.1 EndZ=0
    g3: LineSegment StartX=1 StartY=3.1 StartZ=0 EndX=-1 EndY=3.1 EndZ=0
    g4: GeomPoint [constr] X=0 Y=0 Z=0
  constraints (12):
    c: Coincident(g0,g1)
    c: Coincident(g1,g2)
    c: Coincident(g2,g3)
    c: Coincident(g3,g0)
    c: Vertical(g0)
    c: Vertical(g2)
    c: Horizontal(g1)
    c: Horizontal(g3)
    c: Symmetric(g2,g0,g4)
    c: Coincident(g4,g-1)
    c: Distance(g0) = 6.2
    c: Equal(g3,g-3)
FEATURE [Sketcher::SketchObject] Sketch063  label="blocchi tra switch"
  ArcFitTolerance = 1e-06
  AttachmentSupport = -> [XZ_Plane003]
  ExternalGeometry = -> [Sketch061,Sketch062]
  FullyConstrained = true
  MakeInternals = false
  MapMode = 5
  Placement = pos=(0,0,0) rot=(1,0,0;1.5708rad)
  sketch-geometry (8):
    g0: LineSegment StartX=-3 StartY=5.1 StartZ=0 EndX=-1 EndY=5.1 EndZ=0
    g1: LineSegment StartX=-1 StartY=5.1 StartZ=0 EndX=-1 EndY=3.1 EndZ=0
    g2: LineSegment StartX=-1 StartY=3.1 StartZ=0 EndX=-3 EndY=3.1 EndZ=0
    g3: LineSegment StartX=-3 StartY=3.1 StartZ=0 EndX=-3 EndY=5.1 EndZ=0
    g4: LineSegment StartX=-3 StartY=-3.1 StartZ=0 EndX=-1 EndY=-3.1 EndZ=0
    g5: LineSegment StartX=-1 StartY=-3.1 StartZ=0 EndX=-1 EndY=-5.1 EndZ=0
    g6: LineSegment StartX=-1 StartY=-5.1 StartZ=0 EndX=-3 EndY=-5.1 EndZ=0
    g7: LineSegment StartX=-3 StartY=-5.1 StartZ=0 EndX=-3 EndY=-3.1 EndZ=0
  constraints (20):
    c: Horizontal(g0)
    c: Coincident(g1,g0)
    c: Coincident(g2,g1)
    c: Horizontal(g2)
    c: Coincident(g3,g2)
    c: Coincident(g3,g0)
    c: Vertical(g3)
    c: Horizontal(g4)
    c: Coincident(g5,g4)
    c: Coincident(g6,g5)
    c: Horizontal(g6)
    c: Coincident(g7,g6)
    c: Coincident(g7,g4)
    c: Vertical(g7)
    c: Coincident(g0,g-4)
    c: Coincident(g1,g-5)
    c: Coincident(g4,g-6)
    c: Coincident(g5,g-7)
    c: Distance(g0) = 2
    c: Distance(g4) = 2
FEATURE [Sketcher::SketchObject] Sketch066  label="piano per rampino"
  ArcFitTolerance = 1e-06
  AttachmentSupport = -> [XZ_Plane002]
  ExternalGeometry = -> [Sketch045]
  FullyConstrained = true
  MakeInternals = false
  MapMode = 5
  Placement = pos=(0,0,0) rot=(1,0,0;1.5708rad)
  sketch-geometry (4):
    g0: LineSegment StartX=5.4 StartY=5.1 StartZ=0 EndX=5.4 EndY=3.9 EndZ=0
    g1: LineSegment StartX=5.4 StartY=3.9 StartZ=0 EndX=7 EndY=3.9 EndZ=0
    g2: LineSegment StartX=7 StartY=3.9 StartZ=0 EndX=7 EndY=5.1 EndZ=0
    g3: LineSegment StartX=7 StartY=5.1 StartZ=0 EndX=5.4 EndY=5.1 EndZ=0
  constraints (11):
    c: Coincident(g0,g1)
    c: Coincident(g1,g2)
    c: Coincident(g2,g3)
    c: Coincident(g3,g0)
    c: Vertical(g0)
    c: Vertical(g2)
    c: Horizontal(g1)
    c: Horizontal(g3)
    c: Distance(g0,g2) = 1.6
    c: Distance(g1,g3) = 1.2
    c: Coincident(g2,g-3)
FEATURE [Sketcher::SketchObject] Sketch064  label="rampini_per_serraggio_struttura"
  ArcFitTolerance = 1e-06
  AttachmentSupport = -> [XZ_Plane002]
  ExternalGeometry = -> [Sketch066,Sketch045]
  FullyConstrained = true
  MakeInternals = false
  MapMode = 5
  Placement = pos=(0,0,0) rot=(1,0,0;1.5708rad)
  sketch-geometry (7):
    g0: LineSegment StartX=7 StartY=5.1 StartZ=0 EndX=7 EndY=3.9 EndZ=0
    g1: LineSegment StartX=7 StartY=3.9 StartZ=0 EndX=9 EndY=3.9 EndZ=0
    g2: LineSegment StartX=7 StartY=5.1 StartZ=0 EndX=7 EndY=5.1 EndZ=0
    g3: LineSegment StartX=7 StartY=5.1 StartZ=0 EndX=7 EndY=7.5 EndZ=0
    g4: LineSegment StartX=9 StartY=5.1 StartZ=0 EndX=9 EndY=3.9 EndZ=0
    g5: LineSegment StartX=7 StartY=7.5 StartZ=0 EndX=9 EndY=7.5 EndZ=0
    g6: LineSegment StartX=9 StartY=7.5 StartZ=0 EndX=9 EndY=5.1 EndZ=0
  constraints (20):
    c: Vertical(g0)
    c: Coincident(g1,g0)
    c: Horizontal(g1)
    c: Coincident(g2,g0)
    c: Horizontal(g2)
    c: Coincident(g3,g2)
    c: Vertical(g3)
    c: Coincident(g5,g3)
    c: Coincident(g4,g6)
    c: Coincident(g4,g1)
    c: Vertical(g4)
    c: Coincident(g0,g-3)
    c: DistanceY(g-4,g3) = 2.4
    c: DistanceX(g1,g1) = 2
    c: DistanceY(g2,g6) = 0
    c: DistanceX(g2,g2) = 0
    c: DistanceY(g0,g0) = 1.2
    c: Coincident(g5,g6)
    c: Horizontal(g5)
    c: Vertical(g6)
FEATURE [Sketcher::SketchObject] Sketch067  label="perno per blocco switch"
  ArcFitTolerance = 1e-06
  AttachmentSupport = -> [XZ_Plane]
  ExternalGeometry = -> [Sketch,Sketch010]
  FullyConstrained = true
  MakeInternals = false
  MapMode = 5
  Placement = pos=(0,0,0) rot=(1,0,0;1.5708rad)
  sketch-geometry (14):
    g0: LineSegment StartX=-191.073 StartY=24.9429 StartZ=0 EndX=-185.81 EndY=23.0276 EndZ=0
    g1: LineSegment StartX=-183.76 StartY=23.9839 StartZ=0 EndX=-182.392 EndY=27.7427 EndZ=0
    g2: LineSegment StartX=-183.348 StartY=29.7934 StartZ=0 EndX=-188.61 EndY=31.7087 EndZ=0
    g3: LineSegment StartX=-188.61 StartY=31.7087 StartZ=0 EndX=-191.073 EndY=24.9429 EndZ=0
    g4: GeomPoint [constr] X=-186.459 Y=27.0946 Z=0
    g5: LineSegment StartX=-189.022 StartY=25.8992 StartZ=0 EndX=-185.263 EndY=24.5311 EndZ=0
    g6: LineSegment StartX=-185.263 StartY=24.5311 StartZ=0 EndX=-183.895 EndY=28.2899 EndZ=0
    g7: LineSegment StartX=-183.895 StartY=28.2899 StartZ=0 EndX=-187.654 EndY=29.658 EndZ=0
    g8: LineSegment StartX=-187.654 StartY=29.658 StartZ=0 EndX=-189.022 EndY=25.8992 EndZ=0
    g9: GeomPoint [constr] X=-186.459 Y=27.0946 Z=0
    g10: ArcOfCircle CenterX=-185.263 CenterY=24.5311 CenterZ=0 NormalX=0 NormalY=0 NormalZ=1 AngleXU=0 Radius=1.6 StartAngle=4.36332 EndAngle=5.93412
    g11: GeomPoint [constr] X=-184.307 Y=22.4804 Z=0
    g12: ArcOfCircle CenterX=-183.895 CenterY=28.2899 CenterZ=0 NormalX=0 NormalY=0 NormalZ=1 AngleXU=0 Radius=1.6 StartAngle=5.93412 EndAngle=7.50492
    g13: GeomPoint [constr] X=-181.844 Y=29.2462 Z=0
  constraints (30):
    c: Coincident(g2,g3)
    c: Coincident(g3,g0)
    c: Symmetric(g13,g0,g4)
    c: Distance(g11,g3) = 7.2
    c: Distance(g0,g2) = 7.2
    c: Parallel(g3,g1)
    c: Parallel(g2,g0)
    c: Perpendicular(g2,g3)
    c: Coincident(g5,g6)
    c: Coincident(g6,g7)
    c: Coincident(g7,g8)
    c: Coincident(g8,g5)
    c: Symmetric(g7,g5,g9)
    c: Distance(g6,g8) = 4
    c: Distance(g5,g7) = 4
    c: Coincident(g9,g4)
    c: Parallel(g8,g6)
    c: Parallel(g7,g5)
    c: Perpendicular(g7,g8)
    c: Tangent(g8,g-3)
    c: Tangent(g2,g-4)
    c: PointOnObject(g11,g1)
    c: PointOnObject(g11,g0)
    c: Tangent(g1,g10) = -1.5708
    c: Tangent(g0,g10) = -1.5708
    c: PointOnObject(g13,g1)
    c: Tangent(g1,g12) = -1.5708
    c: Tangent(g2,g12) = -1.5708
    c: Equal(g10,g12)
    c: Coincident(g10,g5)
FEATURE [Part::Extrusion] Extrude072  label="Extrude perno per blocco switch"
  Base = -> Sketch067
  Dir = (0,-1,2e-16)
  DirMode = 2
  FaceMakerClass = Part::FaceMakerBullseye
  FaceMakerMode = 3
  LengthFwd = 25.2
  LengthRev = 0
  Solid = true
  Symmetric = true
FEATURE [Part::MultiFuse] Fusion
  Refine = true
  Shapes = -> [Extrude,Sweep,Extrude007,Extrude011,Extrude005,Extrude012,Extrude013,Extrude016,Extrude031,Extrude039,Extrude045,Extrude072]
FEATURE [Part::Cut] Cut
  Base = -> Fusion
  Refine = true
  Tool = -> Extrude001
FEATURE [Part::Cut] Cut001
  Base = -> Cut
  Refine = true
  Tool = -> Extrude004
FEATURE [Part::Cut] Cut002
  Base = -> Cut001
  Refine = true
  Tool = -> Extrude006
FEATURE [Part::Cut] Cut003
  Base = -> Cut002
  Refine = true
  Tool = -> Extrude008
FEATURE [Part::Cut] Cut004
  Base = -> Cut003
  Refine = true
  Tool = -> Extrude009
FEATURE [Part::Cut] Cut005
  Base = -> Cut004
  Refine = true
  Tool = -> Extrude010
FEATURE [Part::Cut] Cut006
  Base = -> Cut005
  Refine = true
  Tool = -> Extrude014
FEATURE [Part::Cut] Cut007
  Base = -> Cut006
  Refine = true
  Tool = -> Extrude015
FEATURE [Part::Cut] Cut008
  Base = -> Cut007
  Refine = true
  Tool = -> Extrude018
FEATURE [Part::Cut] Cut009
  Base = -> Cut008
  Refine = true
  Tool = -> Extrude019
FEATURE [Part::Cut] Cut010
  Base = -> Cut009
  Refine = true
  Tool = -> Extrude020
FEATURE [Part::Cut] Cut011
  Base = -> Cut010
  Refine = true
  Tool = -> Extrude021
FEATURE [Part::Cut] Cut012
  Base = -> Cut011
  Refine = true
  Tool = -> Extrude022
FEATURE [Part::Cut] Cut013
  Base = -> Cut012
  Refine = true
  Tool = -> Extrude023
FEATURE [Part::Cut] Cut014
  Base = -> Cut013
  Refine = true
  Tool = -> Extrude032
FEATURE [Part::Cut] Cut015
  Base = -> Cut014
  Refine = true
  Tool = -> Extrude033
FEATURE [Part::Cut] Cut016
  Base = -> Cut015
  Refine = true
  Tool = -> Extrude034
FEATURE [Part::Cut] Cut017
  Base = -> Cut016
  Refine = true
  Tool = -> Extrude035
FEATURE [Part::Cut] Cut018
  Base = -> Cut017
  Refine = true
  Tool = -> Extrude036
FEATURE [Part::Cut] Cut019
  Base = -> Cut018
  Refine = true
  Tool = -> Extrude037
FEATURE [Part::Cut] Cut020
  Base = -> Cut019
  Refine = true
  Tool = -> Extrude030
FEATURE [Part::Cut] Cut022
  Base = -> Cut020
  Refine = true
  Tool = -> Extrude038
FEATURE [Part::Cut] Cut023
  Base = -> Cut022
  Refine = true
  Tool = -> Extrude041
FEATURE [Part::Cut] Cut024
  Base = -> Cut023
  Refine = true
  Tool = -> Extrude040
FEATURE [Part::Cut] Cut025
  Base = -> Cut024
  Refine = true
  Tool = -> Extrude042
FEATURE [Part::Cut] Cut026
  Base = -> Cut025
  Refine = true
  Tool = -> Extrude043
FEATURE [Part::Cut] Cut027
  Base = -> Cut026
  Refine = true
  Tool = -> Extrude044
FEATURE [Part::Cut] Cut028
  Base = -> Cut027
  Refine = true
  Tool = -> Extrude046
FEATURE [Part::Cut] Cut029
  Base = -> Cut028
  Refine = true
  Tool = -> Extrude047
FEATURE [Part::Cut] Cut033
  Base = -> Cut029
  Refine = true
  Tool = -> Extrude055
FEATURE [Part::Cut] Cut034
  Base = -> Cut033
  Refine = true
  Tool = -> Extrude056
FEATURE [Part::Cut] Cut035
  Base = -> Cut034
  Refine = true
  Tool = -> Extrude057
FEATURE [Part::Cut] Cut037
  Base = -> Cut035
  Refine = true
  Tool = -> Extrude060
FEATURE [Part::Cut] Cut038
  Base = -> Cut037
  Refine = true
  Tool = -> Extrude061
FEATURE [Part::Cut] Cut039
  Base = -> Cut038
  Refine = true
  Tool = -> Extrude063
FEATURE [Part::Cut] Cut040
  Base = -> Cut039
  Refine = true
  Tool = -> Extrude064
FEATURE [Part::Cut] Cut041
  Base = -> Cut040
  Refine = true
  Tool = -> Extrude062
FEATURE [Sketcher::SketchObject] Sketch068  label="base con smusso sopra neopixel"
  ArcFitTolerance = 1e-06
  AttachmentSupport = -> [YZ_Plane002]
  FullyConstrained = true
  MakeInternals = false
  MapMode = 5
  Placement = pos=(0,0,0) rot=(0.57735,0.57735,0.57735;2.0944rad)
  sketch-geometry (5):
    g0: LineSegment StartX=-9.5 StartY=-6.1 StartZ=0 EndX=9.5 EndY=-6.1 EndZ=0
    g1: LineSegment StartX=9.5 StartY=-6.1 StartZ=0 EndX=9.5 EndY=6.1 EndZ=0
    g2: LineSegment StartX=9.5 StartY=6.1 StartZ=0 EndX=-9.5 EndY=6.1 EndZ=0
    g3: LineSegment StartX=-9.5 StartY=6.1 StartZ=0 EndX=-9.5 EndY=-6.1 EndZ=0
    g4: GeomPoint [constr] X=0 Y=0 Z=0
  constraints (12):
    c: Coincident(g0,g1)
    c: Coincident(g1,g2)
    c: Coincident(g2,g3)
    c: Coincident(g3,g0)
    c: Horizontal(g0)
    c: Horizontal(g2)
    c: Vertical(g1)
    c: Vertical(g3)
    c: Symmetric(g2,g0,g4)
    c: Distance(g1,g3) = 19
    c: Distance(g0,g2) = 12.2
    c: Coincident(g4,g-1)
FEATURE [Sketcher::SketchObject] Sketch069  label="cilindro minore"
  ArcFitTolerance = 1e-06
  AttachmentSupport = -> [XZ_Plane004]
  FullyConstrained = true
  MakeInternals = false
  MapMode = 5
  Placement = pos=(0,0,0) rot=(1,0,0;1.5708rad)
  sketch-geometry (1):
    g0: Circle CenterX=0 CenterY=0 CenterZ=0 NormalX=0 NormalY=0 NormalZ=1 AngleXU=0 Radius=5.8
  constraints (2):
    c: Diameter(g0) = 11.6
    c: Coincident(g0,g-1)
FEATURE [Sketcher::SketchObject] Sketch070  label="cilindro maggiore"
  ArcFitTolerance = 1e-06
  AttachmentSupport = -> [XZ_Plane004]
  ExternalGeometry = -> [Sketch069]
  FullyConstrained = true
  MakeInternals = false
  MapMode = 5
  Placement = pos=(0,0,0) rot=(1,0,0;1.5708rad)
  sketch-geometry (1):
    g0: Circle CenterX=0 CenterY=0 CenterZ=0 NormalX=0 NormalY=0 NormalZ=1 AngleXU=0 Radius=6.5
  constraints (2):
    c: Coincident(g0,g-1)
    c: Diameter(g0) = 13
FEATURE [Sketcher::SketchObject] Sketch071  label="buco interno"
  ArcFitTolerance = 1e-06
  AttachmentSupport = -> [XZ_Plane004]
  ExternalGeometry = -> [Sketch069]
  FullyConstrained = true
  MakeInternals = false
  MapMode = 5
  Placement = pos=(0,0,0) rot=(1,0,0;1.5708rad)
  sketch-geometry (1):
    g0: Circle CenterX=0 CenterY=0 CenterZ=0 NormalX=0 NormalY=0 NormalZ=1 AngleXU=0 Radius=5
  constraints (2):
    c: Coincident(g0,g-1)
    c: Diameter(g0) = 10
FEATURE [PartDesign::Pad] Pad
  Direction = (0,-1,2e-16)
  Length = 1.2
  Length2 = 10
  Placement = pos=(0,0,0) rot=(1,0,0;1.5708rad)
  Profile = -> Sketch070
  ReferenceAxis = -> Sketch070 [N_Axis]
  Refine = true
  Suppressed = false
  Type = 0
FEATURE [PartDesign::Pad] Pad001
  BaseFeature = -> Pad
  Direction = (0,-1,2e-16)
  Length = 5.6
  Length2 = 10
  Placement = pos=(0,0,0) rot=(1,0,0;1.5708rad)
  Profile = -> Sketch069
  ReferenceAxis = -> Sketch069 [N_Axis]
  Refine = true
  Suppressed = false
  Type = 0
FEATURE [PartDesign::Pocket] Pocket
  BaseFeature = -> Pad001
  Direction = (0,1,-2e-16)
  Length = 7
  Length2 = 5
  Midplane = true
  Placement = pos=(0,0,0) rot=(1,0,0;1.5708rad)
  Profile = -> Sketch071
  ReferenceAxis = -> Sketch071 [N_Axis]
  Refine = true
  Suppressed = false
  Type = 0
FEATURE [PartDesign::Fillet] Fillet
  Base = -> Pocket [Face7]
  BaseFeature = -> Pocket
  Placement = pos=(0,0,0) rot=(1,0,0;1.5708rad)
  Radius = 1
  Refine = true
  SupportTransform = false
  Suppressed = false
  UseAllEdges = false
FEATURE [PartDesign::Body] Body004  label="pulsanti lato sinistro"
  AllowCompound = false
  Group = -> [Sketch069,Sketch070,Sketch071,Pad,Pad001,Pocket,Fillet]
  Origin = -> Origin004
  Tip = -> Fillet
FEATURE [Sketcher::SketchObject] Sketch072  label="buco per saldature e diodo driver solenoide"
  ArcFitTolerance = 1e-06
  AttachmentSupport = -> [XZ_Plane]
  ExternalGeometry = -> [Sketch038]
  FullyConstrained = true
  MakeInternals = false
  MapMode = 5
  Placement = pos=(0,0,0) rot=(1,0,0;1.5708rad)
  sketch-geometry (4):
    g0: LineSegment StartX=-213.368 StartY=-46.2647 StartZ=0 EndX=-208.296 EndY=-35.389 EndZ=0
    g1: LineSegment StartX=-208.296 StartY=-35.389 StartZ=0 EndX=-208.659 EndY=-35.2199 EndZ=0
    g2: LineSegment StartX=-208.659 StartY=-35.2199 StartZ=0 EndX=-213.73 EndY=-46.0956 EndZ=0
    g3: LineSegment StartX=-213.73 StartY=-46.0956 StartZ=0 EndX=-213.368 EndY=-46.2647 EndZ=0
  constraints (11):
    c: Coincident(g1,g0)
    c: Coincident(g2,g1)
    c: Coincident(g3,g2)
    c: Coincident(g3,g0)
    c: Parallel(g-3,g0)
    c: Parallel(g0,g2)
    c: Perpendicular(g0,g3)
    c: Perpendicular(g1,g0)
    c: Distance(g3) = 0.4
    c: Distance(g2) = 12
    c: Coincident(g0,g-3)
FEATURE [Part::Extrusion] Extrude074  label="Extrude buco per saldature e diodo driver solenoide"
  Base = -> Sketch072
  Dir = (0,-1,2e-16)
  DirMode = 2
  FaceMakerClass = Part::FaceMakerBullseye
  FaceMakerMode = 3
  LengthFwd = 14.6
  LengthRev = 0
  Solid = true
  Symmetric = true
FEATURE [Part::Cut] Cut042
  Base = -> Cut041
  Refine = true
  Tool = -> Extrude074
FEATURE [Sketcher::SketchObject] Sketch073  label="fori slargati blocco solenoide"
  ArcFitTolerance = 1e-06
  AttachmentSupport = -> [XY_Plane]
  ExternalGeometry = -> [Sketch030]
  FullyConstrained = true
  MakeInternals = false
  MapMode = 5
  sketch-geometry (2):
    g0: Circle CenterX=-152.209 CenterY=6.95 CenterZ=0 NormalX=0 NormalY=0 NormalZ=1 AngleXU=0 Radius=3.7
    g1: Circle CenterX=-130.41 CenterY=-6.95 CenterZ=0 NormalX=0 NormalY=0 NormalZ=1 AngleXU=0 Radius=3.7
  constraints (4):
    c: Diameter(g0) = 7.4
    c: Coincident(g0,g-3)
    c: Diameter(g1) = 7.4
    c: Coincident(g1,g-4)
FEATURE [Part::Extrusion] Extrude075  label="Extrude fori slargati blocco solenoide"
  Base = -> Sketch073
  Dir = (0,0,1)
  DirMode = 2
  FaceMakerClass = Part::FaceMakerBullseye
  FaceMakerMode = 3
  LengthFwd = 1.5
  LengthRev = 0
  Placement = pos=(0,0,36.4) rot=(0,0,1;0rad)
  Solid = true
  Symmetric = false
FEATURE [Part::Cut] Cut043
  Base = -> Cut042
  Refine = true
  Tool = -> Extrude075
FEATURE [Sketcher::SketchObject] Sketch074  label="lato sx pistola"
  ArcFitTolerance = 1e-06
  AttachmentSupport = -> [XZ_Plane]
  ExternalGeometry = -> [Sketch016,Sketch,Sketch058]
  FullyConstrained = true
  MakeInternals = false
  MapMode = 5
  Placement = pos=(0,0,0) rot=(1,0,0;1.5708rad)
  sketch-geometry (37):
    g0: LineSegment StartX=-82.8 StartY=3.2 StartZ=0 EndX=0 EndY=3.2 EndZ=0
    g1: LineSegment StartX=-82.8 StartY=3.2 StartZ=0 EndX=-82.8 EndY=6.2 EndZ=0
    g2: LineSegment [constr] StartX=-107.6 StartY=18 StartZ=0 EndX=-107.6 EndY=20 EndZ=0
    g3: LineSegment [constr] StartX=-132.428 StartY=18 StartZ=0 EndX=-132.428 EndY=20 EndZ=0
    g4: LineSegment StartX=-132.428 StartY=20 StartZ=0 EndX=-107.6 EndY=20 EndZ=0
    g5: ArcOfCircle CenterX=-107.6 CenterY=4 CenterZ=0 NormalX=0 NormalY=0 NormalZ=1 AngleXU=0 Radius=16 StartAngle=0.137937 EndAngle=1.5708
    g6: LineSegment StartX=-82.8 StartY=6.2 StartZ=0 EndX=-91.752 EndY=6.2 EndZ=0
    g7: LineSegment [constr] StartX=-145.743 StartY=8.32624 StartZ=0 EndX=-147.645 EndY=8.94427 EndZ=0
    g8: ArcOfCircle CenterX=-132.428 CenterY=4 CenterZ=0 NormalX=0 NormalY=0 NormalZ=1 AngleXU=0 Radius=16 StartAngle=1.5708 EndAngle=2.82743
    g9: LineSegment StartX=-215.932 StartY=-80.4316 StartZ=0 EndX=-176.685 EndY=-80.4316 EndZ=0
    g10: LineSegment StartX=-147.645 StartY=8.94427 StartZ=0 EndX=-176.685 EndY=-80.4316 EndZ=0
    g11: LineSegment [constr] StartX=-193.988 StartY=-2.33927 StartZ=0 EndX=-192.176 EndY=-3.18451 EndZ=0
    g12: LineSegment [constr] StartX=-217.232 StartY=-52.1862 StartZ=0 EndX=-215.42 EndY=-53.0314 EndZ=0
    g13: LineSegment StartX=-192.176 StartY=-3.18451 StartZ=0 EndX=-215.42 EndY=-53.0314 EndZ=0
    g14: ArcOfCircle CenterX=-184.801 CenterY=-67.3089 CenterZ=0 NormalX=0 NormalY=0 NormalZ=1 AngleXU=0 Radius=33.7833 StartAngle=2.70526 EndAngle=3.54053
    g15: ArcOfCircle CenterX=-207.583 CenterY=4 CenterZ=0 NormalX=0 NormalY=0 NormalZ=1 AngleXU=0 Radius=17 StartAngle=5.84685 EndAngle=7.56663
    g16: LineSegment StartX=-202.765 StartY=20.303 StartZ=0 EndX=-195.887 EndY=39.2 EndZ=0
    g17: LineSegment [constr] StartX=-193.885 StartY=33.0037 StartZ=0 EndX=-197.644 EndY=34.3718 EndZ=0
    g18: LineSegment StartX=-195.887 StartY=39.2 StartZ=0 EndX=0 EndY=39.2 EndZ=0
    g19: LineSegment StartX=0 StartY=3.2 StartZ=0 EndX=0 EndY=39.2 EndZ=0
    g20: LineSegment StartX=-189.939 StartY=31.5672 StartZ=0 EndX=-192.333 EndY=24.9893 EndZ=0
    g21: LineSegment StartX=-196.467 StartY=26.4942 StartZ=0 EndX=-194.073 EndY=33.0721 EndZ=0
    g22: Circle CenterX=-213.443 CenterY=-76.8316 CenterZ=0 NormalX=0 NormalY=0 NormalZ=1 AngleXU=0 Radius=1.8
    g23: Circle CenterX=-179.305 CenterY=-76.8316 CenterZ=0 NormalX=0 NormalY=0 NormalZ=1 AngleXU=0 Radius=1.8
    g24: Circle CenterX=-184.08 CenterY=34.8 CenterZ=0 NormalX=0 NormalY=0 NormalZ=1 AngleXU=0 Radius=1.8
    g25: Circle CenterX=-78.51 CenterY=34.8 CenterZ=0 NormalX=0 NormalY=0 NormalZ=1 AngleXU=0 Radius=1.8
    g26: Circle CenterX=-78.51 CenterY=7.6 CenterZ=0 NormalX=0 NormalY=0 NormalZ=1 AngleXU=0 Radius=1.8
    g27: Circle CenterX=-5.6 CenterY=34.8 CenterZ=0 NormalX=0 NormalY=0 NormalZ=1 AngleXU=0 Radius=1.8
    g28: Circle CenterX=-5.6 CenterY=7.6 CenterZ=0 NormalX=0 NormalY=0 NormalZ=1 AngleXU=0 Radius=1.8
    g29: LineSegment StartX=-190.127 StartY=31.6356 StartZ=0 EndX=-189.939 EndY=31.5672 EndZ=0
    g30: LineSegment StartX=-194.073 StartY=33.0721 StartZ=0 EndX=-193.885 EndY=33.0037 EndZ=0
    g31: LineSegment StartX=-193.885 StartY=33.0037 StartZ=0 EndX=-190.127 EndY=31.6356 EndZ=0
    g32: LineSegment StartX=-196.467 StartY=26.4942 StartZ=0 EndX=-192.333 EndY=24.9893 EndZ=0
    g33: Circle CenterX=-19 CenterY=21.2 CenterZ=0 NormalX=0 NormalY=0 NormalZ=1 AngleXU=0 Radius=6.3
    g34: Circle CenterX=-42 CenterY=21.2 CenterZ=0 NormalX=0 NormalY=0 NormalZ=1 AngleXU=0 Radius=6.3
    g35: Circle CenterX=-65 CenterY=21.2 CenterZ=0 NormalX=0 NormalY=0 NormalZ=1 AngleXU=0 Radius=6.3
    g36: LineSegment [constr] StartX=-4 StartY=21.2 StartZ=0 EndX=-65 EndY=21.2 EndZ=0
  constraints (96):
    c: Coincident(g0,g-41)
    c: Horizontal(g0)
    c: PointOnObject(g0,g-39)
    c: Coincident(g1,g0)
    c: Vertical(g1)
    c: DistanceY(g1,g1) = 3
    c: Coincident(g2,g-17)
    c: Vertical(g2)
    c: Coincident(g3,g-16)
    c: Vertical(g3)
    c: DistanceY(g2,g2) = 2
    c: DistanceY(g3,g3) = 2
    c: Coincident(g4,g3)
    c: Coincident(g4,g2)
    c: Coincident(g5,g-17)
    c: Coincident(g5,g2)
    c: Coincident(g6,g1)
    c: Horizontal(g6)
    c: Coincident(g6,g5)
    c: Coincident(g7,g-15)
    c: Coincident(g8,g7)
    c: Coincident(g8,g3)
    c: Coincident(g8,g-15)
    c: Horizontal(g9)
    c: DistanceY(g-13,g9) = 2
    c: Coincident(g10,g7)
    c: Parallel(g10,g-14)
    c: Coincident(g9,g10)
    c: Distance(g11) = 2
    c: Coincident(g11,g-11)
    c: Perpendicular(g-11,g11)
    c: Distance(g12) = 2
    c: Coincident(g12,g-12)
    c: Perpendicular(g-11,g12)
    c: Coincident(g13,g11)
    c: Coincident(g13,g12)
    c: Coincident(g14,g-32)
    c: Coincident(g14,g12)
    c: Coincident(g14,g9)
    c: Coincident(g15,g-10)
    c: Coincident(g15,g11)
    c: Parallel(g16,g-22)
    c: Distance(g17) = 4
    c: PointOnObject(g17,g16)
    c: Coincident(g15,g16)
    c: Horizontal(g18)
    c: Coincident(g18,g16)
    c: Coincident(g19,g0)
    c: PointOnObject(g19,g-39)
    c: DistanceY(g19,g-36) = 2
    c: Coincident(g18,g19)
    c: Diameter(g22) = 3.6
    c: Coincident(g22,g-9)
    c: Diameter(g23) = 3.6
    c: Coincident(g23,g-8)
    c: Diameter(g24) = 3.6
    c: Diameter(g25) = 3.6
    c: Diameter(g26) = 3.6
    c: Diameter(g27) = 3.6
    c: Diameter(g28) = 3.6
    c: Coincident(g27,g-4)
    c: Coincident(g28,g-3)
    c: Coincident(g25,g-6)
    c: Coincident(g26,g-5)
    c: Coincident(g24,g-7)
    c: Parallel(g20,g-21)
    c: Equal(g20,g-21)
    c: Parallel(g21,g-19)
    c: Equal(g21,g-19)
    c: Distance(g29) = 0.2
    c: Distance(g30) = 0.2
    c: Parallel(g29,g-20)
    c: Parallel(g31,g-20)
    c: Equal(g31,g-20)
    c: Coincident(g30,g31)
    c: Coincident(g31,g29)
    c: Coincident(g29,g-21)
    c: Parallel(g30,g31)
    c: Coincident(g17,g30)
    c: Coincident(g20,g29)
    c: Coincident(g21,g30)
    c: Perpendicular(g16,g17)
    c: Coincident(g32,g21)
    c: Coincident(g32,g20)
    c: Perpendicular(g10,g7)
    c: Diameter(g33) = 12.6
    c: Diameter(g34) = 12.6
    c: Diameter(g35) = 12.6
    c: Horizontal(g36)
    c: PointOnObject(g33,g36)
    c: PointOnObject(g34,g36)
    c: DistanceX(g34,g33) = 23
    c: DistanceX(g35,g34) = 23
    c: DistanceX(g33,g36) = 15
    c: Symmetric(g-24,g-24,g36)
    c: Coincident(g36,g35)
FEATURE [Sketcher::SketchObject] Sketch075  label="lato dx pistola"
  ArcFitTolerance = 1e-06
  AttachmentSupport = -> [XZ_Plane]
  ExternalGeometry = -> [Sketch016,Sketch,Sketch058,Sketch074]
  FullyConstrained = true
  MakeInternals = false
  MapMode = 5
  Placement = pos=(0,0,0) rot=(1,0,0;1.5708rad)
  sketch-geometry (61):
    g0: LineSegment StartX=-82.8 StartY=3.2 StartZ=0 EndX=0 EndY=3.2 EndZ=0
    g1: LineSegment StartX=-82.8 StartY=3.2 StartZ=0 EndX=-82.8 EndY=6.2 EndZ=0
    g2: LineSegment [constr] StartX=-107.6 StartY=18 StartZ=0 EndX=-107.6 EndY=20 EndZ=0
    g3: LineSegment [constr] StartX=-132.428 StartY=18 StartZ=0 EndX=-132.428 EndY=20 EndZ=0
    g4: LineSegment StartX=-132.428 StartY=20 StartZ=0 EndX=-107.6 EndY=20 EndZ=0
    g5: ArcOfCircle CenterX=-107.6 CenterY=4 CenterZ=0 NormalX=0 NormalY=0 NormalZ=1 AngleXU=0 Radius=16 StartAngle=0.137937 EndAngle=1.5708
    g6: LineSegment StartX=-82.8 StartY=6.2 StartZ=0 EndX=-91.752 EndY=6.2 EndZ=0
    g7: LineSegment [constr] StartX=-145.743 StartY=8.32624 StartZ=0 EndX=-147.645 EndY=8.94427 EndZ=0
    g8: ArcOfCircle CenterX=-132.428 CenterY=4 CenterZ=0 NormalX=0 NormalY=0 NormalZ=1 AngleXU=0 Radius=16 StartAngle=1.5708 EndAngle=2.82743
    g9: LineSegment StartX=-215.932 StartY=-80.4316 StartZ=0 EndX=-176.685 EndY=-80.4316 EndZ=0
    g10: LineSegment StartX=-147.645 StartY=8.94427 StartZ=0 EndX=-176.685 EndY=-80.4316 EndZ=0
    g11: LineSegment [constr] StartX=-193.988 StartY=-2.33927 StartZ=0 EndX=-192.176 EndY=-3.18451 EndZ=0
    g12: LineSegment [constr] StartX=-217.232 StartY=-52.1862 StartZ=0 EndX=-215.42 EndY=-53.0314 EndZ=0
    g13: LineSegment StartX=-192.176 StartY=-3.18451 StartZ=0 EndX=-215.42 EndY=-53.0314 EndZ=0
    g14: ArcOfCircle CenterX=-184.801 CenterY=-67.3089 CenterZ=0 NormalX=0 NormalY=0 NormalZ=1 AngleXU=0 Radius=33.7833 StartAngle=2.70526 EndAngle=3.54053
    g15: ArcOfCircle CenterX=-207.583 CenterY=4 CenterZ=0 NormalX=0 NormalY=0 NormalZ=1 AngleXU=0 Radius=17 StartAngle=5.84685 EndAngle=7.56663
    g16: LineSegment StartX=-202.765 StartY=20.303 StartZ=0 EndX=-195.887 EndY=39.2 EndZ=0
    g17: LineSegment [constr] StartX=-193.885 StartY=33.0037 StartZ=0 EndX=-197.644 EndY=34.3718 EndZ=0
    g18: LineSegment StartX=-195.887 StartY=39.2 StartZ=0 EndX=0 EndY=39.2 EndZ=0
    g19: LineSegment StartX=0 StartY=3.2 StartZ=0 EndX=0 EndY=39.2 EndZ=0
    g20: LineSegment StartX=-189.939 StartY=31.5672 StartZ=0 EndX=-192.333 EndY=24.9893 EndZ=0
    g21: LineSegment StartX=-196.467 StartY=26.4942 StartZ=0 EndX=-194.073 EndY=33.0721 EndZ=0
    g22: Circle CenterX=-213.443 CenterY=-76.8316 CenterZ=0 NormalX=0 NormalY=0 NormalZ=1 AngleXU=0 Radius=1.8
    g23: Circle CenterX=-179.305 CenterY=-76.8316 CenterZ=0 NormalX=0 NormalY=0 NormalZ=1 AngleXU=0 Radius=1.8
    g24: Circle CenterX=-184.08 CenterY=34.8 CenterZ=0 NormalX=0 NormalY=0 NormalZ=1 AngleXU=0 Radius=1.8
    g25: Circle CenterX=-78.51 CenterY=34.8 CenterZ=0 NormalX=0 NormalY=0 NormalZ=1 AngleXU=0 Radius=1.8
    g26: Circle CenterX=-78.51 CenterY=7.6 CenterZ=0 NormalX=0 NormalY=0 NormalZ=1 AngleXU=0 Radius=1.8
    g27: Circle CenterX=-5.6 CenterY=34.8 CenterZ=0 NormalX=0 NormalY=0 NormalZ=1 AngleXU=0 Radius=1.8
    g28: Circle CenterX=-5.6 CenterY=7.6 CenterZ=0 NormalX=0 NormalY=0 NormalZ=1 AngleXU=0 Radius=1.8
    g29: LineSegment StartX=-190.127 StartY=31.6356 StartZ=0 EndX=-189.939 EndY=31.5672 EndZ=0
    g30: LineSegment StartX=-194.073 StartY=33.0721 StartZ=0 EndX=-193.885 EndY=33.0037 EndZ=0
    g31: LineSegment StartX=-193.885 StartY=33.0037 StartZ=0 EndX=-190.127 EndY=31.6356 EndZ=0
    g32: LineSegment StartX=-196.467 StartY=26.4942 StartZ=0 EndX=-192.333 EndY=24.9893 EndZ=0
    g33: LineSegment [constr] StartX=-4 StartY=21.2 StartZ=0 EndX=-87.91 EndY=21.2 EndZ=0
    g34: GeomPoint [constr] X=-4 Y=21.2 Z=0
    g35: LineSegment [constr] StartX=-15.2 StartY=33.7 StartZ=0 EndX=-15.2 EndY=8.7 EndZ=0
    g36: LineSegment [constr] StartX=-15.2 StartY=33.7 StartZ=0 EndX=-56.2 EndY=33.7 EndZ=0
    g37: LineSegment [constr] StartX=-15.2 StartY=8.7 StartZ=0 EndX=-56.2 EndY=8.7 EndZ=0
    g38: LineSegment [constr] StartX=-56.2 StartY=33.7 StartZ=0 EndX=-56.2 EndY=8.7 EndZ=0
    g39: Circle CenterX=-18.6 CenterY=30.3 CenterZ=0 NormalX=0 NormalY=0 NormalZ=1 AngleXU=0 Radius=3.4
    g40: Circle CenterX=-18.6 CenterY=12.1 CenterZ=0 NormalX=0 NormalY=0 NormalZ=1 AngleXU=0 Radius=3.4
    g41: Circle CenterX=-43.2 CenterY=30.3 CenterZ=0 NormalX=0 NormalY=0 NormalZ=1 AngleXU=0 Radius=3.4
    g42: Circle CenterX=-43.2 CenterY=12.1 CenterZ=0 NormalX=0 NormalY=0 NormalZ=1 AngleXU=0 Radius=3.4
    g43: LineSegment [constr] StartX=-4 StartY=21.2 StartZ=0 EndX=-15.2 EndY=21.2 EndZ=0
    g44: LineSegment [constr] StartX=-15.2 StartY=21.2 StartZ=0 EndX=-36.2 EndY=21.2 EndZ=0
    g45: LineSegment [constr] StartX=-41.5 StartY=16.2 StartZ=0 EndX=-30.9 EndY=16.2 EndZ=0
    g46: LineSegment [constr] StartX=-30.9 StartY=16.2 StartZ=0 EndX=-30.9 EndY=26.2 EndZ=0
    g47: LineSegment [constr] StartX=-30.9 StartY=26.2 StartZ=0 EndX=-41.5 EndY=26.2 EndZ=0
    g48: LineSegment [constr] StartX=-41.5 StartY=26.2 StartZ=0 EndX=-41.5 EndY=16.2 EndZ=0
    g49: GeomPoint [constr] X=-36.2 Y=21.2 Z=0
    g50: Circle CenterX=-36.2 CenterY=21.2 CenterZ=0 NormalX=0 NormalY=0 NormalZ=1 AngleXU=0 Radius=2.8
    g51: LineSegment [constr] StartX=-24.2 StartY=26.7 StartZ=0 EndX=-24.2 EndY=15.7 EndZ=0
    g52: Circle CenterX=-24.2 CenterY=26.7 CenterZ=0 NormalX=0 NormalY=0 NormalZ=1 AngleXU=0 Radius=3
    g53: Circle CenterX=-24.2 CenterY=15.7 CenterZ=0 NormalX=0 NormalY=0 NormalZ=1 AngleXU=0 Radius=3
    g54: GeomPoint X=-18.6 Y=30.3 Z=0
    g55: GeomPoint X=-18.6 Y=12.1 Z=0
    g56: GeomPoint X=-43.2 Y=12.1 Z=0
    g57: GeomPoint X=-43.2 Y=30.3 Z=0
    g58: Circle CenterX=-65 CenterY=21.2 CenterZ=0 NormalX=0 NormalY=0 NormalZ=1 AngleXU=0 Radius=1.5
    g59: Circle CenterX=-42 CenterY=21.2 CenterZ=0 NormalX=0 NormalY=0 NormalZ=1 AngleXU=0 Radius=1.5
    g60: Circle CenterX=-19 CenterY=21.2 CenterZ=0 NormalX=0 NormalY=0 NormalZ=1 AngleXU=0 Radius=1.5
  constraints (149):
    c: Coincident(g0,g-41)
    c: Horizontal(g0)
    c: PointOnObject(g0,g-39)
    c: Coincident(g1,g0)
    c: Vertical(g1)
    c: DistanceY(g1,g1) = 3
    c: Coincident(g2,g-17)
    c: Vertical(g2)
    c: Coincident(g3,g-16)
    c: Vertical(g3)
    c: DistanceY(g2,g2) = 2
    c: DistanceY(g3,g3) = 2
    c: Coincident(g4,g3)
    c: Coincident(g4,g2)
    c: Coincident(g5,g-17)
    c: Coincident(g5,g2)
    c: Coincident(g6,g1)
    c: Horizontal(g6)
    c: Coincident(g6,g5)
    c: Coincident(g7,g-15)
    c: Coincident(g8,g7)
    c: Coincident(g8,g3)
    c: Coincident(g8,g-15)
    c: Horizontal(g9)
    c: DistanceY(g-13,g9) = 2
    c: Coincident(g10,g7)
    c: Parallel(g10,g-14)
    c: Coincident(g9,g10)
    c: Distance(g11) = 2
    c: Coincident(g11,g-11)
    c: Perpendicular(g-11,g11)
    c: Distance(g12) = 2
    c: Coincident(g12,g-12)
    c: Perpendicular(g-11,g12)
    c: Coincident(g13,g11)
    c: Coincident(g13,g12)
    c: Coincident(g14,g-32)
    c: Coincident(g14,g12)
    c: Coincident(g14,g9)
    c: Coincident(g15,g-10)
    c: Coincident(g15,g11)
    c: Parallel(g16,g-22)
    c: Distance(g17) = 4
    c: PointOnObject(g17,g16)
    c: Coincident(g15,g16)
    c: Horizontal(g18)
    c: Coincident(g18,g16)
    c: Coincident(g19,g0)
    c: PointOnObject(g19,g-39)
    c: DistanceY(g19,g-36) = 2
    c: Coincident(g18,g19)
    c: Diameter(g22) = 3.6
    c: Coincident(g22,g-9)
    c: Diameter(g23) = 3.6
    c: Coincident(g23,g-8)
    c: Diameter(g24) = 3.6
    c: Diameter(g25) = 3.6
    c: Diameter(g26) = 3.6
    c: Diameter(g27) = 3.6
    c: Diameter(g28) = 3.6
    c: Coincident(g27,g-4)
    c: Coincident(g28,g-3)
    c: Coincident(g25,g-6)
    c: Coincident(g26,g-5)
    c: Coincident(g24,g-7)
    c: Parallel(g20,g-21)
    c: Equal(g20,g-21)
    c: Parallel(g21,g-19)
    c: Equal(g21,g-19)
    c: Distance(g29) = 0.2
    c: Distance(g30) = 0.2
    c: Parallel(g29,g-20)
    c: Parallel(g31,g-20)
    c: Equal(g31,g-20)
    c: Coincident(g30,g31)
    c: Coincident(g31,g29)
    c: Coincident(g29,g-21)
    c: Parallel(g30,g31)
    c: Coincident(g17,g30)
    c: Coincident(g20,g29)
    c: Coincident(g21,g30)
    c: Perpendicular(g16,g17)
    c: Coincident(g32,g21)
    c: Coincident(g32,g20)
    c: Perpendicular(g10,g7)
    c: Horizontal(g33)
    c: Symmetric(g-24,g-24,g33)
    c: PointOnObject(g33,g-28)
    c: Symmetric(g-24,g-24,g34)
    c: DistanceY(g35,g35) = 25
    c: Symmetric(g35,g35,g33)
    c: Distance(g36) = 41
    c: Coincident(g36,g35)
    c: Horizontal(g36)
    c: Coincident(g37,g35)
    c: Horizontal(g37)
    c: Coincident(g38,g36)
    c: Vertical(g38)
    c: Coincident(g37,g38)
    c: Diameter(g39) = 6.8
    c: Diameter(g40) = 6.8
    c: Tangent(g39,g36)
    c: Tangent(g40,g37)
    c: Tangent(g39,g35)
    c: Tangent(g40,g35)
    c: Diameter(g41) = 6.8
    c: Diameter(g42) = 6.8
    c: Tangent(g41,g36)
    c: Tangent(g42,g37)
    c: DistanceX(g41,g39) = 24.6
    c: DistanceX(g42,g40) = 24.6
    c: Distance(g43) = 11.2
    c: Coincident(g43,g33)
    c: PointOnObject(g43,g33)
    c: PointOnObject(g43,g35)
    c: Distance(g44) = 21
    c: Coincident(g44,g43)
    c: PointOnObject(g44,g33)
    c: Coincident(g45,g46)
    c: Coincident(g46,g47)
    c: Coincident(g47,g48)
    c: Coincident(g48,g45)
    c: Horizontal(g45)
    c: Horizontal(g47)
    c: Vertical(g46)
    c: Vertical(g48)
    c: Symmetric(g47,g45,g49)
    c: Distance(g46,g48) = 10.6
    c: Distance(g45,g47) = 10
    c: Coincident(g49,g44)
    c: Diameter(g50) = 5.6
    c: Coincident(g50,g44)
    c: Distance(g51) = 11
    c: Symmetric(g51,g51,g33)
    c: DistanceX(g51,g43) = 9
    c: Diameter(g52) = 6
    c: Coincident(g52,g51)
    c: Diameter(g53) = 6
    c: Coincident(g53,g51)
    c: Coincident(g40,g55)
    c: Coincident(g39,g54)
    c: Coincident(g41,g57)
    c: Coincident(g42,g56)
    c: Diameter(g58) = 3
    c: Diameter(g59) = 3
    c: Diameter(g60) = 3
    c: Coincident(g58,g-44)
    c: Coincident(g59,g-46)
    c: Coincident(g60,g-45)
FEATURE [Sketcher::SketchObject] Sketch078
  ArcFitTolerance = 1e-06
  AttachmentSupport = -> [XZ_Plane005]
  FullyConstrained = true
  MakeInternals = false
  MapMode = 5
  Placement = pos=(0,0,0) rot=(1,0,0;1.5708rad)
  sketch-geometry (5):
    g0: LineSegment [constr] StartX=0 StartY=5.5 StartZ=0 EndX=0 EndY=-5.5 EndZ=0
    g1: ArcOfCircle CenterX=0 CenterY=5.5 CenterZ=0 NormalX=0 NormalY=0 NormalZ=1 AngleXU=0 Radius=2.7 StartAngle=0 EndAngle=3.14159
    g2: ArcOfCircle CenterX=0 CenterY=-5.5 CenterZ=0 NormalX=0 NormalY=0 NormalZ=1 AngleXU=0 Radius=2.7 StartAngle=3.1416 EndAngle=6.28318
    g3: LineSegment StartX=-2.7 StartY=5.5 StartZ=0 EndX=-2.7 EndY=-5.50001 EndZ=0
    g4: LineSegment StartX=2.7 StartY=5.5 StartZ=0 EndX=2.7 EndY=-5.50001 EndZ=0
  constraints (13):
    c: Distance(g0) = 11
    c: Vertical(g0)
    c: Symmetric(g0,g0,g-1)
    c: Radius(g1) = 2.7
    c: Coincident(g1,g0)
    c: Radius(g2) = 2.7
    c: Coincident(g2,g0)
    c: Vertical(g3)
    c: Vertical(g4)
    c: Coincident(g2,g4)
    c: Coincident(g2,g3)
    c: Tangent(g3,g1) = -1.5708
    c: Tangent(g4,g1) = 1.5708
FEATURE [PartDesign::Pad] Pad002
  Direction = (0,-1,2e-16)
  Length = 0.8
  Length2 = 10
  Placement = pos=(0,0,0) rot=(1,0,0;1.5708rad)
  Profile = -> Sketch078
  ReferenceAxis = -> Sketch078 [N_Axis]
  Refine = true
  Suppressed = false
  Type = 0
FEATURE [Sketcher::SketchObject] Sketch079
  ArcFitTolerance = 1e-06
  AttachmentSupport = -> [XZ_Plane005]
  ExternalGeometry = -> [Sketch078]
  FullyConstrained = true
  MakeInternals = false
  MapMode = 5
  Placement = pos=(0,0,0) rot=(1,0,0;1.5708rad)
  sketch-geometry (2):
    g0: Circle CenterX=-1e-16 CenterY=5.5 CenterZ=0 NormalX=0 NormalY=0 NormalZ=1 AngleXU=0 Radius=2.7
    g1: Circle CenterX=0 CenterY=-5.5 CenterZ=0 NormalX=0 NormalY=0 NormalZ=1 AngleXU=0 Radius=2.7
  constraints (4):
    c: Coincident(g0,g-3)
    c: PointOnObject(g-3,g0)
    c: Coincident(g1,g-4)
    c: Equal(g1,g-4)
FEATURE [PartDesign::Pad] Pad003
  BaseFeature = -> Pad002
  Direction = (0,-1,2e-16)
  Length = 5
  Length2 = 10
  Placement = pos=(0,0,0) rot=(1,0,0;1.5708rad)
  Profile = -> Sketch079
  ReferenceAxis = -> Sketch079 [N_Axis]
  Refine = true
  Suppressed = false
  Type = 0
FEATURE [PartDesign::Fillet] Fillet001
  Base = -> Pad003 [Edge16,Edge14]
  BaseFeature = -> Pad003
  Placement = pos=(0,0,0) rot=(1,0,0;1.5708rad)
  Radius = 0.4
  Refine = true
  SupportTransform = false
  Suppressed = false
  UseAllEdges = false
FEATURE [PartDesign::Body] Body005  label="pulsanti lato destro"
  AllowCompound = false
  Group = -> [Sketch078,Pad002,Sketch079,Pad003,Fillet001]
  Origin = -> Origin005
  Tip = -> Fillet001
FEATURE [PartDesign::SubShapeBinder] Binder
  BindCopyOnChange = 0
  BindMode = 0
  ClaimChildren = false
  Context = -> Body006 [Binder.]
  Fuse = false
  MakeFace = true
  OffsetFill = false
  OffsetIntersection = false
  OffsetJoinType = 0
  OffsetOpenResult = false
  PartialLoad = false
  Refine = true
  Relative = true
  Support = -> [Body[Sketch074.]]
  _Version = 2
FEATURE [PartDesign::SubShapeBinder] Binder001
  BindCopyOnChange = 0
  BindMode = 0
  ClaimChildren = false
  Context = -> Body007 [Binder001.]
  Fuse = false
  MakeFace = true
  OffsetFill = false
  OffsetIntersection = false
  OffsetJoinType = 0
  OffsetOpenResult = false
  PartialLoad = false
  Refine = true
  Relative = true
  Support = -> [Body[Sketch075.]]
  _Version = 2
FEATURE [Mesh::Feature] logo_per_PCB_definitivo_positivo
  Placement = pos=(-191,17,-66) rot=(0,1,1;0rad)
FEATURE [Sketcher::SketchObject] Sketch114  label="Sketch114 - base lato DX"
  ArcFitTolerance = 1e-06
  AttachmentSupport = -> [Binder001]
  ExternalGeometry = -> [Binder001]
  FullyConstrained = true
  MakeInternals = false
  MapMode = 5
  Placement = pos=(0,1e-15,0) rot=(0,0.707107,0.707107;3.14159rad)
  sketch-geometry (30):
    g0: Circle CenterX=5.6 CenterY=34.8 CenterZ=0 NormalX=0 NormalY=0 NormalZ=1 AngleXU=0 Radius=1.8
    g1: Circle CenterX=5.6 CenterY=7.6 CenterZ=0 NormalX=0 NormalY=0 NormalZ=1 AngleXU=0 Radius=1.8
    g2: Circle CenterX=24.2 CenterY=26.7 CenterZ=0 NormalX=0 NormalY=0 NormalZ=1 AngleXU=0 Radius=3
    g3: Circle CenterX=24.2 CenterY=15.7 CenterZ=0 NormalX=0 NormalY=0 NormalZ=1 AngleXU=0 Radius=3
    g4: Circle CenterX=36.2 CenterY=21.2 CenterZ=0 NormalX=0 NormalY=0 NormalZ=1 AngleXU=0 Radius=2.8
    g5: Circle CenterX=78.51 CenterY=34.8 CenterZ=0 NormalX=0 NormalY=0 NormalZ=1 AngleXU=0 Radius=1.8
    g6: Circle CenterX=78.51 CenterY=7.6 CenterZ=0 NormalX=0 NormalY=0 NormalZ=1 AngleXU=0 Radius=1.8
    g7: Circle CenterX=184.08 CenterY=34.8 CenterZ=0 NormalX=0 NormalY=0 NormalZ=1 AngleXU=0 Radius=1.8
    g8: Circle CenterX=213.443 CenterY=-76.8316 CenterZ=0 NormalX=0 NormalY=0 NormalZ=1 AngleXU=0 Radius=1.8
    g9: Circle CenterX=179.305 CenterY=-76.8316 CenterZ=0 NormalX=0 NormalY=0 NormalZ=1 AngleXU=0 Radius=1.8
    g10: ArcOfCircle [constr] CenterX=132.428 CenterY=4 CenterZ=0 NormalX=0 NormalY=0 NormalZ=1 AngleXU=0 Radius=16 StartAngle=0.314159 EndAngle=1.5708
    g11: ArcOfCircle CenterX=107.6 CenterY=4 CenterZ=0 NormalX=0 NormalY=0 NormalZ=1 AngleXU=0 Radius=16 StartAngle=1.5708 EndAngle=3.00366
    g12: ArcOfCircle CenterX=207.583 CenterY=4 CenterZ=0 NormalX=0 NormalY=0 NormalZ=1 AngleXU=0 Radius=17 StartAngle=1.85815 EndAngle=3.57792
    g13: ArcOfCircle CenterX=184.801 CenterY=-67.3089 CenterZ=0 NormalX=0 NormalY=0 NormalZ=1 AngleXU=0 Radius=33.7833 StartAngle=5.88425 EndAngle=6.71952
    g14: LineSegment StartX=0 StartY=39.2 StartZ=0 EndX=0 EndY=3.2 EndZ=0
    g15: LineSegment StartX=0 StartY=3.2 StartZ=0 EndX=82.8 EndY=3.2 EndZ=0
    g16: LineSegment StartX=82.8 StartY=3.2 StartZ=0 EndX=82.8 EndY=6.2 EndZ=0
    g17: LineSegment StartX=82.8 StartY=6.2 StartZ=0 EndX=91.752 EndY=6.2 EndZ=0
    g18: LineSegment StartX=107.6 StartY=20 StartZ=0 EndX=132.428 EndY=20 EndZ=0
    g19: LineSegment StartX=147.645 StartY=8.94427 StartZ=0 EndX=176.685 EndY=-80.4316 EndZ=0
    g20: LineSegment StartX=176.685 StartY=-80.4316 StartZ=0 EndX=215.932 EndY=-80.4316 EndZ=0
    g21: LineSegment StartX=215.42 StartY=-53.0314 StartZ=0 EndX=192.176 EndY=-3.18451 EndZ=0
    g22: LineSegment StartX=202.765 StartY=20.303 StartZ=0 EndX=195.887 EndY=39.2 EndZ=0
    g23: LineSegment StartX=195.887 StartY=39.2 StartZ=0 EndX=0 EndY=39.2 EndZ=0
    g24: LineSegment StartX=196.467 StartY=26.4942 StartZ=0 EndX=194.073 EndY=33.0721 EndZ=0
    g25: LineSegment StartX=194.073 StartY=33.0721 StartZ=0 EndX=189.939 EndY=31.5672 EndZ=0
    g26: LineSegment StartX=189.939 StartY=31.5672 StartZ=0 EndX=192.333 EndY=24.9893 EndZ=0
    g27: LineSegment StartX=192.333 StartY=24.9893 StartZ=0 EndX=196.467 EndY=26.4942 EndZ=0
    g28: LineSegment StartX=132.428 StartY=20 StartZ=0 EndX=144.053 EndY=20 EndZ=0
    g29: LineSegment StartX=144.053 StartY=20 StartZ=0 EndX=147.645 EndY=8.94427 EndZ=0
  constraints (65):
    c: Equal(g0,g-25)
    c: Equal(g2,g-29)
    c: Equal(g3,g-30)
    c: Equal(g4,g-28)
    c: Equal(g1,g-26)
    c: Coincident(g0,g-25)
    c: Coincident(g1,g-26)
    c: Coincident(g2,g-29)
    c: Coincident(g3,g-30)
    c: Coincident(g4,g-28)
    c: Equal(g5,g-23)
    c: Equal(g6,g-24)
    c: Coincident(g5,g-23)
    c: Coincident(g6,g-24)
    c: Equal(g7,g-20)
    c: Coincident(g7,g-20)
    c: Equal(g9,g-22)
    c: Coincident(g9,g-22)
    c: Equal(g8,g-21)
    c: Coincident(g8,g-21)
    c: Equal(g13,g-12)
    c: Equal(g12,g-14)
    c: Equal(g10,g-9)
    c: Equal(g11,g-7)
    c: Coincident(g14,g-27)
    c: Coincident(g14,g-27)
    c: Coincident(g15,g14)
    c: Coincident(g15,g-5)
    c: Coincident(g16,g15)
    c: Coincident(g16,g-6)
    c: Coincident(g17,g16)
    c: Coincident(g17,g-7)
    c: Coincident(g11,g17)
    c: Coincident(g11,g-8)
    c: Coincident(g18,g11)
    c: Coincident(g18,g-9)
    c: Coincident(g10,g18)
    c: Coincident(g10,g-10)
    c: Coincident(g19,g10)
    c: Coincident(g19,g-11)
    c: Coincident(g20,g19)
    c: Coincident(g20,g-12)
    c: Coincident(g13,g20)
    c: Coincident(g13,g-13)
    c: Coincident(g21,g13)
    c: Coincident(g21,g-14)
    c: Coincident(g12,g21)
    c: Coincident(g12,g-15)
    c: Coincident(g22,g12)
    c: Coincident(g22,g-15)
    c: Coincident(g23,g22)
    c: Coincident(g23,g14)
    c: Coincident(g24,g-18)
    c: Coincident(g24,g-16)
    c: Coincident(g25,g24)
    c: Coincident(g25,g-19)
    c: Coincident(g26,g25)
    c: Coincident(g26,g-19)
    c: Coincident(g27,g26)
    c: Coincident(g27,g24)
    c: Coincident(g29,g10)
    c: Coincident(g28,g10)
    c: Coincident(g29,g28)
    c: Parallel(g28,g18)
    c: Parallel(g29,g19)
FEATURE [PartDesign::Pad] Pad011
  Direction = (0,1,-2e-16)
  Length = 2
  Length2 = 10
  Profile = -> Sketch114
  ReferenceAxis = -> Sketch114 [N_Axis]
  Refine = true
  Reversed = true
  Suppressed = false
  Type = 0
FEATURE [Sketcher::SketchObject] Sketch115
  ArcFitTolerance = 1e-06
  AttachmentSupport = -> [Pad011]
  ExternalGeometry = -> [Binder001]
  FullyConstrained = true
  MakeInternals = false
  MapMode = 5
  Placement = pos=(0,1.7e-15,0) rot=(0,0.707107,0.707107;3.14159rad)
  sketch-geometry (4):
    g0: ArcOfCircle CenterX=24.2 CenterY=26.7 CenterZ=0 NormalX=0 NormalY=0 NormalZ=1 AngleXU=0 Radius=3 StartAngle=4.48384e-08 EndAngle=3.14159
    g1: ArcOfCircle CenterX=24.2 CenterY=15.7 CenterZ=0 NormalX=0 NormalY=0 NormalZ=1 AngleXU=0 Radius=3 StartAngle=3.14159 EndAngle=6.28318
    g2: LineSegment StartX=21.2 StartY=26.7 StartZ=0 EndX=21.2 EndY=15.7 EndZ=0
    g3: LineSegment StartX=27.2 StartY=26.7 StartZ=0 EndX=27.2 EndY=15.7 EndZ=0
  constraints (12):
    c: Equal(g1,g-4)
    c: Equal(g0,g-3)
    c: Coincident(g0,g-3)
    c: Coincident(g1,g-4)
    c: Vertical(g2)
    c: Vertical(g3)
    c: Tangent(g3,g-3)
    c: Tangent(g2,g-3)
    c: Coincident(g0,g2)
    c: Coincident(g0,g3)
    c: Coincident(g1,g2)
    c: Coincident(g3,g1)
FEATURE [Sketcher::SketchObject] Sketch117  label="Sketch117 - fori per inserto M3 x 3 x 4.5"
  ArcFitTolerance = 1e-06
  AttachmentSupport = -> [Pad011]
  ExternalGeometry = -> [Binder001]
  FullyConstrained = true
  MakeInternals = false
  MapMode = 5
  Placement = pos=(0,1.7e-15,0) rot=(0,0.707107,0.707107;3.14159rad)
  sketch-geometry (4):
    g0: Circle CenterX=43.2 CenterY=30.3 CenterZ=0 NormalX=0 NormalY=0 NormalZ=1 AngleXU=0 Radius=2.25
    g1: Circle CenterX=43.2 CenterY=12.1 CenterZ=0 NormalX=0 NormalY=0 NormalZ=1 AngleXU=0 Radius=2.25
    g2: Circle CenterX=18.6 CenterY=30.3 CenterZ=0 NormalX=0 NormalY=0 NormalZ=1 AngleXU=0 Radius=2.25
    g3: Circle CenterX=18.6 CenterY=12.1 CenterZ=0 NormalX=0 NormalY=0 NormalZ=1 AngleXU=0 Radius=2.25
  constraints (8):
    c: Diameter(g0) = 4.5
    c: Diameter(g1) = 4.5
    c: Diameter(g2) = 4.5
    c: Diameter(g3) = 4.5
    c: Coincident(g2,g-3)
    c: Coincident(g3,g-6)
    c: Coincident(g0,g-4)
    c: Coincident(g1,g-5)
FEATURE [Sketcher::SketchObject] Sketch118
  ArcFitTolerance = 1e-06
  AttachmentSupport = -> [Pad011]
  ExternalGeometry = -> [Binder001]
  FullyConstrained = true
  MakeInternals = false
  MapMode = 5
  Placement = pos=(0,-2,0) rot=(1,0,0;1.5708rad)
  sketch-geometry (12):
    g0: Circle CenterX=-78.51 CenterY=34.8 CenterZ=0 NormalX=0 NormalY=0 NormalZ=1 AngleXU=0 Radius=1.8
    g1: Circle CenterX=-78.51 CenterY=7.6 CenterZ=0 NormalX=0 NormalY=0 NormalZ=1 AngleXU=0 Radius=1.8
    g2: Circle CenterX=-5.6 CenterY=34.8 CenterZ=0 NormalX=0 NormalY=0 NormalZ=1 AngleXU=0 Radius=1.8
    g3: Circle CenterX=-5.6 CenterY=7.6 CenterZ=0 NormalX=0 NormalY=0 NormalZ=1 AngleXU=0 Radius=1.8
    g4: LineSegment StartX=0 StartY=39.2 StartZ=0 EndX=0 EndY=3.2 EndZ=0
    g5: LineSegment StartX=0 StartY=3.2 StartZ=0 EndX=-82.8 EndY=3.2 EndZ=0
    g6: LineSegment StartX=-82.8 StartY=3.2 StartZ=0 EndX=-82.8 EndY=39.2 EndZ=0
    g7: LineSegment StartX=-82.8 StartY=39.2 StartZ=0 EndX=0 EndY=39.2 EndZ=0
    g8: ArcOfCircle CenterX=-65 CenterY=21.2 CenterZ=0 NormalX=0 NormalY=0 NormalZ=1 AngleXU=0 Radius=10 StartAngle=1.5708 EndAngle=4.71239
    g9: ArcOfCircle CenterX=-19 CenterY=21.2 CenterZ=0 NormalX=0 NormalY=0 NormalZ=1 AngleXU=0 Radius=10 StartAngle=4.71239 EndAngle=7.85398
    g10: LineSegment StartX=-65 StartY=31.2 StartZ=0 EndX=-19 EndY=31.2 EndZ=0
    g11: LineSegment StartX=-65 StartY=11.2 StartZ=0 EndX=-19 EndY=11.2 EndZ=0
  constraints (25):
    c: Equal(g2,g-5)
    c: Equal(g3,g-7)
    c: Equal(g1,g-6)
    c: Equal(g0,g-4)
    c: Coincident(g0,g-4)
    c: Coincident(g1,g-6)
    c: Coincident(g3,g-7)
    c: Coincident(g2,g-5)
    c: Coincident(g4,g-8)
    c: Coincident(g4,g-9)
    c: Coincident(g5,g4)
    c: Coincident(g5,g-10)
    c: Coincident(g6,g5)
    c: PointOnObject(g6,g-3)
    c: Vertical(g6)
    c: Coincident(g7,g6)
    c: Coincident(g7,g4)
    c: Tangent(g8,g10) = 1.5708
    c: Tangent(g8,g11) = -1.5708
    c: Tangent(g9,g10) = 1.5708
    c: Tangent(g9,g11) = -1.5708
    c: Equal(g8,g9)
    c: Radius(g8) = 10
    c: Coincident(g8,g-11)
    c: Coincident(g9,g-12)
FEATURE [Sketcher::SketchObject] Sketch120
  ArcFitTolerance = 1e-06
  AttachmentSupport = -> [Pad011]
  ExternalGeometry = -> [Binder001]
  FullyConstrained = true
  MakeInternals = false
  MapMode = 5
  Placement = pos=(0,-2,0) rot=(1,0,0;1.5708rad)
  sketch-geometry (4):
    g0: LineSegment StartX=-137.815 StartY=39.2 StartZ=0 EndX=-142.655 EndY=24.303 EndZ=0
    g1: LineSegment StartX=-137.815 StartY=39.2 StartZ=0 EndX=-110.815 EndY=39.2 EndZ=0
    g2: LineSegment StartX=-142.655 StartY=24.303 StartZ=0 EndX=-110.815 EndY=24.303 EndZ=0
    g3: ArcOfCircle CenterX=-92.2534 CenterY=31.7515 CenterZ=0 NormalX=0 NormalY=0 NormalZ=1 AngleXU=0 Radius=20 StartAngle=2.75997 EndAngle=3.52321
  constraints (12):
    c: PointOnObject(g0,g-3)
    c: Coincident(g1,g0)
    c: PointOnObject(g1,g-3)
    c: Coincident(g2,g0)
    c: Horizontal(g2)
    c: Tangent(g0,g-4)
    c: Vertical(g2,g1)
    c: DistanceX(g1,g1) = 27
    c: DistanceY(g-6,g0) = 4
    c: Radius(g3) = 20
    c: Coincident(g3,g1)
    c: Coincident(g3,g2)
FEATURE [Sketcher::SketchObject] Sketch121
  ArcFitTolerance = 1e-06
  AttachmentSupport = -> [Pad011]
  ExternalGeometry = -> [Binder001]
  FullyConstrained = true
  MakeInternals = false
  MapMode = 5
  Placement = pos=(0,-2,0) rot=(1,0,0;1.5708rad)
  sketch-geometry (15):
    g0: LineSegment StartX=-137.815 StartY=39.2 StartZ=0 EndX=-143.955 EndY=20.303 EndZ=0
    g1: LineSegment StartX=-143.955 StartY=20.303 StartZ=0 EndX=-190.141 EndY=20.303 EndZ=0
    g2: LineSegment StartX=-190.141 StartY=20.303 StartZ=0 EndX=-186.139 EndY=31.3 EndZ=0
    g3: LineSegment StartX=-178.754 StartY=39.2 StartZ=0 EndX=-180.791 EndY=33.6029 EndZ=0
    g4: ArcOfCircle CenterX=-184.08 CenterY=34.8 CenterZ=0 NormalX=0 NormalY=0 NormalZ=1 AngleXU=0 Radius=3.5 StartAngle=4.71239 EndAngle=5.93412
    g5: LineSegment StartX=-184.08 StartY=31.3 StartZ=0 EndX=-186.139 EndY=31.3 EndZ=0
    g6: LineSegment StartX=-137.815 StartY=39.2 StartZ=0 EndX=-156.815 EndY=39.2 EndZ=0
    g7: LineSegment StartX=-168.815 StartY=39.2 StartZ=0 EndX=-178.754 EndY=39.2 EndZ=0
    g8: LineSegment StartX=-157.815 StartY=39.2 StartZ=0 EndX=-167.815 EndY=39.2 EndZ=0
    g9: LineSegment StartX=-168.815 StartY=31.2 StartZ=0 EndX=-156.815 EndY=31.2 EndZ=0
    g10: LineSegment StartX=-167.436 StartY=36.2 StartZ=0 EndX=-157.436 EndY=36.2 EndZ=0
    g11: ArcOfCircle CenterX=-176.411 CenterY=35.2 CenterZ=0 NormalX=0 NormalY=0 NormalZ=1 AngleXU=0 Radius=20 StartAngle=6.08183 EndAngle=6.48454
    g12: ArcOfCircle CenterX=-188.411 CenterY=35.2 CenterZ=0 NormalX=0 NormalY=0 NormalZ=1 AngleXU=0 Radius=20 StartAngle=6.08183 EndAngle=6.48454
    g13: ArcOfCircle CenterX=-177.411 CenterY=35.2 CenterZ=0 NormalX=0 NormalY=0 NormalZ=1 AngleXU=0 Radius=20 StartAngle=0.0500209 EndAngle=0.201358
    g14: ArcOfCircle CenterX=-187.411 CenterY=35.2 CenterZ=0 NormalX=0 NormalY=0 NormalZ=1 AngleXU=0 Radius=20 StartAngle=0.0500209 EndAngle=0.201358
  constraints (46):
    c: PointOnObject(g0,g-3)
    c: Tangent(g0,g-5)
    c: Coincident(g1,g0)
    c: Horizontal(g1)
    c: Coincident(g2,g1)
    c: PointOnObject(g3,g-3)
    c: Parallel(g3,g-6)
    c: Parallel(g2,g-6)
    c: Radius(g4) = 3.5
    c: Coincident(g4,g-7)
    c: Tangent(g3,g4) = 1.5708
    c: Horizontal(g5)
    c: Tangent(g5,g4) = 1.5708
    c: DistanceX(g-8,g5) = 3.8
    c: Coincident(g2,g5)
    c: Coincident(g6,g0)
    c: PointOnObject(g6,g-3)
    c: DistanceX(g6,g6) = 19
    c: PointOnObject(g7,g-3)
    c: DistanceX(g7,g6) = 12
    c: Coincident(g7,g3)
    c: PointOnObject(g8,g-3)
    c: PointOnObject(g8,g-3)
    c: DistanceX(g8,g8) = 10
    c: DistanceX(g8,g6) = 1
    c: Horizontal(g9)
    c: Vertical(g7,g9)
    c: Vertical(g6,g9)
    c: DistanceY(g9,g7) = 8
    c: Horizontal(g10)
    c: Equal(g8,g10)
    c: DistanceY(g10,g8) = 3
    c: Radius(g11) = 20
    c: Coincident(g11,g6)
    c: Coincident(g11,g9)
    c: Radius(g12) = 20
    c: Coincident(g12,g7)
    c: Coincident(g12,g9)
    c: Equal(g13,g11)
    c: Coincident(g13,g8)
    c: Coincident(g13,g10)
    c: Horizontal(g13,g11)
    c: Equal(g14,g12)
    c: Coincident(g14,g8)
    c: Coincident(g14,g10)
    c: Horizontal(g1,g-6)
FEATURE [Sketcher::SketchObject] Sketch122
  ArcFitTolerance = 1e-06
  AttachmentSupport = -> [Pad011]
  ExternalGeometry = -> [Binder001]
  FullyConstrained = true
  MakeInternals = false
  MapMode = 5
  Placement = pos=(0,-2,0) rot=(1,0,0;1.5708rad)
  sketch-geometry (8):
    g0: ArcOfCircle CenterX=-184.801 CenterY=-67.3089 CenterZ=0 NormalX=0 NormalY=0 NormalZ=1 AngleXU=0 Radius=33.7833 StartAngle=2.70526 EndAngle=3.54053
    g1: LineSegment StartX=-176.685 StartY=-80.4316 StartZ=0 EndX=-215.932 EndY=-80.4316 EndZ=0
    g2: LineSegment StartX=-215.42 StartY=-53.0314 StartZ=0 EndX=-192.176 EndY=-3.18454 EndZ=0
    g3: ArcOfCircle CenterX=-207.583 CenterY=4 CenterZ=0 NormalX=0 NormalY=0 NormalZ=1 AngleXU=0 Radius=17 StartAngle=5.84685 EndAngle=7.56663
    g4: Circle CenterX=-213.443 CenterY=-76.8316 CenterZ=0 NormalX=0 NormalY=0 NormalZ=1 AngleXU=0 Radius=3
    g5: Circle CenterX=-179.305 CenterY=-76.8316 CenterZ=0 NormalX=0 NormalY=0 NormalZ=1 AngleXU=0 Radius=3
    g6: LineSegment StartX=-143.955 StartY=20.303 StartZ=0 EndX=-176.685 EndY=-80.4316 EndZ=0
    g7: LineSegment StartX=-202.765 StartY=20.303 StartZ=0 EndX=-143.955 EndY=20.303 EndZ=0
  constraints (18):
    c: Coincident(g0,g-7)
    c: Coincident(g0,g-8)
    c: Coincident(g1,g0)
    c: Tangent(g2,g-5)
    c: Coincident(g3,g-6)
    c: Coincident(g2,g3)
    c: Coincident(g0,g2)
    c: Diameter(g4) = 6
    c: Diameter(g5) = 6
    c: Coincident(g4,g-9)
    c: Coincident(g5,g-10)
    c: Horizontal(g1)
    c: Coincident(g6,g1)
    c: Tangent(g6,g-4)
    c: Coincident(g3,g-6)
    c: Coincident(g7,g3)
    c: Horizontal(g7)
    c: Coincident(g7,g6)
FEATURE [Sketcher::SketchObject] Sketch123
  ArcFitTolerance = 1e-06
  AttachmentSupport = -> [Pad011]
  ExternalGeometry = -> [Binder001]
  FullyConstrained = true
  MakeInternals = false
  MapMode = 5
  Placement = pos=(0,-2,0) rot=(1,0,0;1.5708rad)
  sketch-geometry (4):
    g0: LineSegment StartX=-108 StartY=36.8 StartZ=0 EndX=-90 EndY=36.8 EndZ=0
    g1: LineSegment StartX=-108 StartY=36.8 StartZ=0 EndX=-108 EndY=26.8 EndZ=0
    g2: LineSegment StartX=-108 StartY=26.8 StartZ=0 EndX=-90 EndY=26.8 EndZ=0
    g3: ArcOfCircle CenterX=-94 CenterY=31.8 CenterZ=0 NormalX=0 NormalY=0 NormalZ=1 AngleXU=0 Radius=6.40312 StartAngle=5.38713 EndAngle=7.17924
  constraints (13):
    c: Horizontal(g0)
    c: Coincident(g1,g0)
    c: Vertical(g1)
    c: Coincident(g2,g1)
    c: Horizontal(g2)
    c: DistanceX(g0,g0) = 18
    c: DistanceY(g1,g1) = 10
    c: Equal(g0,g2)
    c: DistanceX(g0,g-3) = 90
    c: DistanceY(g0,g-3) = 2.4
    c: Coincident(g3,g0)
    c: Coincident(g3,g2)
    c: DistanceX(g3,g0) = 4
FEATURE [PartDesign::Chamfer] Chamfer014
  Angle = 45
  Base = -> Pad011 [Edge80,Edge4,Edge7]
  BaseFeature = -> Pad011
  ChamferType = 0
  FlipDirection = false
  Refine = true
  Size = 1.9
  Size2 = 1
  SupportTransform = false
  Suppressed = false
  UseAllEdges = false
FEATURE [PartDesign::Pocket] Pocket006
  BaseFeature = -> Chamfer014
  Direction = (0,-1,2e-16)
  Length = 1.2
  Length2 = 5
  Profile = -> Sketch115
  ReferenceAxis = -> Sketch115 [N_Axis]
  Refine = true
  Suppressed = false
  Type = 0
FEATURE [Sketcher::SketchObject] Sketch116  label="Sketch116 - pieno per inserto M3 x 3 x 4,5"
  ArcFitTolerance = 1e-06
  AttachmentSupport = -> [Pocket006]
  ExternalGeometry = -> [Binder001]
  FullyConstrained = true
  MakeInternals = false
  MapMode = 5
  Placement = pos=(0,1.7e-15,0) rot=(0,0.707107,0.707107;3.14159rad)
  sketch-geometry (4):
    g0: Circle CenterX=43.2 CenterY=30.3 CenterZ=0 NormalX=0 NormalY=0 NormalZ=1 AngleXU=0 Radius=3.4
    g1: Circle CenterX=43.2 CenterY=12.1 CenterZ=0 NormalX=0 NormalY=0 NormalZ=1 AngleXU=0 Radius=3.4
    g2: Circle CenterX=18.6 CenterY=30.3 CenterZ=0 NormalX=0 NormalY=0 NormalZ=1 AngleXU=0 Radius=3.4
    g3: Circle CenterX=18.6 CenterY=12.1 CenterZ=0 NormalX=0 NormalY=0 NormalZ=1 AngleXU=0 Radius=3.4
  constraints (8):
    c: Diameter(g0) = 6.8
    c: Diameter(g1) = 6.8
    c: Diameter(g2) = 6.8
    c: Diameter(g3) = 6.8
    c: Coincident(g2,g-3)
    c: Coincident(g0,g-4)
    c: Coincident(g3,g-6)
    c: Coincident(g1,g-5)
FEATURE [PartDesign::Pad] Pad012
  BaseFeature = -> Pocket006
  Direction = (0,1,-2e-16)
  Length = 2.4
  Length2 = 10
  Profile = -> Sketch116
  ReferenceAxis = -> Sketch116 [N_Axis]
  Refine = true
  Suppressed = false
  Type = 0
FEATURE [PartDesign::Pocket] Pocket007
  BaseFeature = -> Pad012
  Direction = (0,-1,2e-16)
  Length = 0.6
  Length2 = 2.4
  Profile = -> Sketch117
  ReferenceAxis = -> Sketch117 [N_Axis]
  Refine = true
  Suppressed = false
  Type = 4
FEATURE [PartDesign::Pad] Pad013
  BaseFeature = -> Pocket007
  Direction = (0,-1,2e-16)
  Length = 1.6
  Length2 = 10
  Profile = -> Sketch118
  ReferenceAxis = -> Sketch118 [N_Axis]
  Refine = true
  Suppressed = false
  Type = 0
FEATURE [Sketcher::SketchObject] Sketch119
  ArcFitTolerance = 1e-06
  AttachmentSupport = -> [Pad013]
  ExternalGeometry = -> [Binder001]
  FullyConstrained = true
  MakeInternals = false
  MapMode = 5
  Placement = pos=(0,-3.6,0) rot=(1,0,0;1.5708rad)
  sketch-geometry (21):
    g0: LineSegment [constr] StartX=-82.8 StartY=3.2 StartZ=0 EndX=-82.8 EndY=39.2 EndZ=0
    g1: ArcOfCircle CenterX=-78.51 CenterY=34.8 CenterZ=0 NormalX=0 NormalY=0 NormalZ=1 AngleXU=0 Radius=3.5 StartAngle=4.71239 EndAngle=6.28319
    g2: ArcOfCircle CenterX=-78.51 CenterY=7.6 CenterZ=0 NormalX=0 NormalY=0 NormalZ=1 AngleXU=0 Radius=3.5 StartAngle=0 EndAngle=1.5708
    g3: ArcOfCircle CenterX=-5.6 CenterY=34.8 CenterZ=0 NormalX=0 NormalY=0 NormalZ=1 AngleXU=0 Radius=3.5 StartAngle=3.14159 EndAngle=4.71239
    g4: ArcOfCircle CenterX=-5.6 CenterY=7.6 CenterZ=0 NormalX=0 NormalY=0 NormalZ=1 AngleXU=0 Radius=3.5 StartAngle=1.5708 EndAngle=3.14159
    g5: LineSegment StartX=0 StartY=39.2 StartZ=0 EndX=0 EndY=31.3 EndZ=0
    g6: LineSegment StartX=0 StartY=39.2 StartZ=0 EndX=-9.1 EndY=39.2 EndZ=0
    g7: LineSegment StartX=0 StartY=3.2 StartZ=0 EndX=0 EndY=11.1 EndZ=0
    g8: LineSegment StartX=0 StartY=3.2 StartZ=0 EndX=-9.1 EndY=3.2 EndZ=0
    g9: LineSegment StartX=-82.8 StartY=3.2 StartZ=0 EndX=-75.01 EndY=3.2 EndZ=0
    g10: LineSegment StartX=-82.8 StartY=3.2 StartZ=0 EndX=-82.8 EndY=11.1 EndZ=0
    g11: LineSegment StartX=-82.8 StartY=39.2 StartZ=0 EndX=-82.8 EndY=31.3 EndZ=0
    g12: LineSegment StartX=-82.8 StartY=39.2 StartZ=0 EndX=-75.01 EndY=39.2 EndZ=0
    g13: LineSegment StartX=-82.8 StartY=31.3 StartZ=0 EndX=-78.51 EndY=31.3 EndZ=0
    g14: LineSegment StartX=-75.01 StartY=39.2 StartZ=0 EndX=-75.01 EndY=34.8 EndZ=0
    g15: LineSegment StartX=-82.8 StartY=11.1 StartZ=0 EndX=-78.51 EndY=11.1 EndZ=0
    g16: LineSegment StartX=-75.01 StartY=3.2 StartZ=0 EndX=-75.01 EndY=7.6 EndZ=0
    g17: LineSegment StartX=-9.1 StartY=39.2 StartZ=0 EndX=-9.1 EndY=34.8 EndZ=0
    g18: LineSegment StartX=0 StartY=31.3 StartZ=0 EndX=-5.6 EndY=31.3 EndZ=0
    g19: LineSegment StartX=0 StartY=11.1 StartZ=0 EndX=-5.6 EndY=11.1 EndZ=0
    g20: LineSegment StartX=-9.1 StartY=3.2 StartZ=0 EndX=-9.1 EndY=7.6 EndZ=0
  constraints (51):
    c: Coincident(g0,g-10)
    c: PointOnObject(g0,g-8)
    c: Vertical(g0)
    c: Coincident(g1,g-3)
    c: Coincident(g2,g-4)
    c: Coincident(g3,g-5)
    c: Coincident(g4,g-6)
    c: Radius(g4) = 3.5
    c: Radius(g3) = 3.5
    c: Radius(g1) = 3.5
    c: Radius(g2) = 3.5
    c: Coincident(g5,g-9)
    c: PointOnObject(g5,g-9)
    c: Coincident(g6,g5)
    c: PointOnObject(g6,g-8)
    c: Coincident(g7,g-9)
    c: PointOnObject(g7,g-9)
    c: Coincident(g8,g7)
    c: PointOnObject(g8,g-7)
    c: Coincident(g9,g0)
    c: PointOnObject(g9,g-7)
    c: Coincident(g10,g0)
    c: PointOnObject(g10,g0)
    c: Coincident(g11,g0)
    c: PointOnObject(g11,g0)
    c: Coincident(g12,g0)
    c: PointOnObject(g12,g-8)
    c: Coincident(g13,g11)
    c: Horizontal(g13)
    c: Coincident(g14,g12)
    c: Vertical(g14)
    c: Coincident(g15,g10)
    c: Horizontal(g15)
    c: Coincident(g16,g9)
    c: Vertical(g16)
    c: Coincident(g17,g6)
    c: Vertical(g17)
    c: Coincident(g18,g5)
    c: Horizontal(g18)
    c: Coincident(g19,g7)
    c: Horizontal(g19)
    c: Coincident(g20,g8)
    c: Vertical(g20)
    c: Tangent(g20,g4) = 1.5708
    c: Tangent(g4,g19) = -1.5708
    c: Tangent(g18,g3) = 1.5708
    c: Tangent(g3,g17) = -1.5708
    c: Tangent(g13,g1) = -1.5708
    c: Tangent(g1,g14) = 1.5708
    c: Tangent(g16,g2) = -1.5708
    c: Tangent(g2,g15) = 1.5708
FEATURE [PartDesign::Pocket] Pocket008
  BaseFeature = -> Pad013
  Direction = (0,1,-2e-16)
  Length = 1.6
  Length2 = 5
  Profile = -> Sketch119
  ReferenceAxis = -> Sketch119 [N_Axis]
  Refine = true
  Suppressed = false
  Type = 0
FEATURE [PartDesign::Pad] Pad017
  BaseFeature = -> Pocket008
  Direction = (0,-1,2e-16)
  Length = 1.6
  Length2 = 10
  Profile = -> Sketch123
  ReferenceAxis = -> Sketch123 [N_Axis]
  Refine = true
  Suppressed = false
  Type = 0
FEATURE [Sketcher::SketchObject] Sketch125
  ArcFitTolerance = 1e-06
  AttachmentSupport = -> [Pad017]
  ExternalGeometry = -> [Pad017]
  FullyConstrained = true
  MakeInternals = false
  MapMode = 5
  Placement = pos=(0,-3.6,8e-16) rot=(1,0,0;1.5708rad)
  sketch-geometry (20):
    g0: LineSegment StartX=-108 StartY=35.8 StartZ=0 EndX=-108 EndY=35 EndZ=0
    g1: LineSegment StartX=-108 StartY=35 StartZ=0 EndX=-97 EndY=35 EndZ=0
    g2: LineSegment StartX=-97 StartY=35 StartZ=0 EndX=-97 EndY=35.8 EndZ=0
    g3: LineSegment StartX=-97 StartY=35.8 StartZ=0 EndX=-108 EndY=35.8 EndZ=0
    g4: LineSegment StartX=-108 StartY=28.6 StartZ=0 EndX=-108 EndY=27.8 EndZ=0
    g5: LineSegment StartX=-108 StartY=27.8 StartZ=0 EndX=-97 EndY=27.8 EndZ=0
    g6: LineSegment StartX=-97 StartY=27.8 StartZ=0 EndX=-97 EndY=28.6 EndZ=0
    g7: LineSegment StartX=-97 StartY=28.6 StartZ=0 EndX=-108 EndY=28.6 EndZ=0
    g8: LineSegment StartX=-108 StartY=30.4 StartZ=0 EndX=-108 EndY=29.6 EndZ=0
    g9: LineSegment StartX=-108 StartY=29.6 StartZ=0 EndX=-97 EndY=29.6 EndZ=0
    g10: LineSegment StartX=-97 StartY=29.6 StartZ=0 EndX=-97 EndY=30.4 EndZ=0
    g11: LineSegment StartX=-97 StartY=30.4 StartZ=0 EndX=-108 EndY=30.4 EndZ=0
    g12: LineSegment StartX=-108 StartY=32.2 StartZ=0 EndX=-108 EndY=31.4 EndZ=0
    g13: LineSegment StartX=-108 StartY=31.4 StartZ=0 EndX=-97 EndY=31.4 EndZ=0
    g14: LineSegment StartX=-97 StartY=31.4 StartZ=0 EndX=-97 EndY=32.2 EndZ=0
    g15: LineSegment StartX=-97 StartY=32.2 StartZ=0 EndX=-108 EndY=32.2 EndZ=0
    g16: LineSegment StartX=-108 StartY=34 StartZ=0 EndX=-108 EndY=33.2 EndZ=0
    g17: LineSegment StartX=-108 StartY=33.2 StartZ=0 EndX=-97 EndY=33.2 EndZ=0
    g18: LineSegment StartX=-97 StartY=33.2 StartZ=0 EndX=-97 EndY=34 EndZ=0
    g19: LineSegment StartX=-97 StartY=34 StartZ=0 EndX=-108 EndY=34 EndZ=0
  constraints (55):
    c: Coincident(g1,g0)
    c: Horizontal(g1)
    c: Coincident(g2,g1)
    c: Vertical(g2)
    c: Coincident(g3,g2)
    c: Horizontal(g3)
    c: Coincident(g3,g0)
    c: DistanceX(g1,g1) = 11
    c: DistanceY(g2,g2) = 0.8
    c: Coincident(g5,g4)
    c: Horizontal(g5)
    c: Coincident(g6,g5)
    c: Vertical(g6)
    c: Coincident(g7,g6)
    c: Horizontal(g7)
    c: Coincident(g7,g4)
    c: Coincident(g9,g8)
    c: Horizontal(g9)
    c: Coincident(g10,g9)
    c: Vertical(g10)
    c: Coincident(g11,g10)
    c: Horizontal(g11)
    c: Coincident(g11,g8)
    c: Coincident(g13,g12)
    c: Horizontal(g13)
    c: Coincident(g14,g13)
    c: Vertical(g14)
    c: Coincident(g15,g14)
    c: Horizontal(g15)
    c: Coincident(g15,g12)
    c: Coincident(g17,g16)
    c: Horizontal(g17)
    c: Coincident(g18,g17)
    c: Vertical(g18)
    c: Coincident(g19,g18)
    c: Horizontal(g19)
    c: Coincident(g19,g16)
    c: Equal(g3,g19)
    c: Equal(g3,g15)
    c: Equal(g3,g11)
    c: Equal(g3,g7)
    c: Equal(g2,g18)
    c: Equal(g2,g14)
    c: Equal(g2,g10)
    c: Equal(g2,g6)
    c: DistanceY(g-4,g4) = 1
    c: DistanceY(g4,g8) = 1
    c: DistanceY(g8,g12) = 1
    c: DistanceY(g12,g16) = 1
    c: DistanceY(g16,g0) = 1
    c: Tangent(g0,g-5)
    c: Tangent(g16,g-5)
    c: Tangent(g12,g-5)
    c: Tangent(g8,g-5)
    c: Tangent(g4,g-5)
FEATURE [PartDesign::Chamfer] Chamfer009
  Angle = 45
  Base = -> Pad017 [Edge151,Edge154]
  BaseFeature = -> Pad017
  ChamferType = 1
  FlipDirection = false
  Refine = true
  Size = 1.5
  Size2 = 2.8
  SupportTransform = false
  Suppressed = false
  UseAllEdges = false
FEATURE [PartDesign::Pocket] Pocket009
  BaseFeature = -> Chamfer009
  Direction = (0,1,-2e-16)
  Length = 1
  Length2 = 5
  Profile = -> Sketch125
  ReferenceAxis = -> Sketch125 [N_Axis]
  Refine = true
  Suppressed = false
  Type = 0
FEATURE [PartDesign::Pad] Pad014
  BaseFeature = -> Pocket009
  Direction = (0,-1,2e-16)
  Length = 0.8
  Length2 = 10
  Profile = -> Sketch120
  ReferenceAxis = -> Sketch120 [N_Axis]
  Refine = true
  Suppressed = false
  Type = 0
FEATURE [Sketcher::SketchObject] Sketch124
  ArcFitTolerance = 1e-06
  AttachmentSupport = -> [Pad014]
  ExternalGeometry = -> [Binder001]
  FullyConstrained = true
  MakeInternals = false
  MapMode = 5
  Placement = pos=(0,-2.8,6e-16) rot=(1,0,0;1.5708rad)
  sketch-geometry (4):
    g0: LineSegment StartX=-129 StartY=39.2 StartZ=0 EndX=-131.599 EndY=31.2 EndZ=0
    g1: LineSegment StartX=-118 StartY=39.2 StartZ=0 EndX=-120.599 EndY=31.2 EndZ=0
    g2: LineSegment StartX=-129 StartY=39.2 StartZ=0 EndX=-118 EndY=39.2 EndZ=0
    g3: LineSegment StartX=-120.599 StartY=31.2 StartZ=0 EndX=-131.599 EndY=31.2 EndZ=0
  constraints (12):
    c: PointOnObject(g0,g-3)
    c: PointOnObject(g1,g-3)
    c: Parallel(g-4,g0)
    c: Parallel(g-4,g1)
    c: Coincident(g2,g0)
    c: Coincident(g2,g1)
    c: DistanceX(g2,g2) = 11
    c: DistanceY(g1,g1) = 8
    c: Coincident(g3,g1)
    c: Horizontal(g3)
    c: Coincident(g3,g0)
    c: DistanceX(g1,g-3) = 118
FEATURE [PartDesign::Pad] Pad018
  BaseFeature = -> Pad014
  Direction = (0,-1,2e-16)
  Length = 1.2
  Length2 = 10
  Profile = -> Sketch124
  ReferenceAxis = -> Sketch124 [N_Axis]
  Refine = true
  Suppressed = false
  Type = 0
FEATURE [Sketcher::SketchObject] Sketch126
  ArcFitTolerance = 1e-06
  AttachmentSupport = -> [Pad018]
  ExternalGeometry = -> [Pad018]
  FullyConstrained = true
  MakeInternals = false
  MapMode = 5
  Placement = pos=(0,-4,0) rot=(1,0,0;1.5708rad)
  sketch-geometry (8):
    g0: LineSegment StartX=-129.877 StartY=36.5 StartZ=0 EndX=-130.137 EndY=35.7 EndZ=0
    g1: LineSegment StartX=-130.69 StartY=34 StartZ=0 EndX=-130.95 EndY=33.2 EndZ=0
    g2: LineSegment StartX=-129.877 StartY=36.5 StartZ=0 EndX=-118.877 EndY=36.5 EndZ=0
    g3: LineSegment StartX=-130.137 StartY=35.7 StartZ=0 EndX=-119.137 EndY=35.7 EndZ=0
    g4: LineSegment StartX=-130.69 StartY=34 StartZ=0 EndX=-119.69 EndY=34 EndZ=0
    g5: LineSegment StartX=-130.95 StartY=33.2 StartZ=0 EndX=-119.95 EndY=33.2 EndZ=0
    g6: LineSegment StartX=-118.877 StartY=36.5 StartZ=0 EndX=-119.137 EndY=35.7 EndZ=0
    g7: LineSegment StartX=-119.69 StartY=34 StartZ=0 EndX=-119.95 EndY=33.2 EndZ=0
  constraints (20):
    c: Coincident(g2,g0)
    c: Horizontal(g2)
    c: Coincident(g3,g0)
    c: Horizontal(g3)
    c: Coincident(g4,g1)
    c: Horizontal(g4)
    c: Coincident(g5,g1)
    c: Horizontal(g5)
    c: Coincident(g6,g2)
    c: Coincident(g6,g3)
    c: Coincident(g7,g4)
    c: Coincident(g7,g5)
    c: Tangent(g0,g-4)
    c: Tangent(g6,g-5)
    c: Tangent(g1,g-4)
    c: Tangent(g7,g-5)
    c: DistanceY(g3,g2) = 0.8
    c: DistanceY(g5,g4) = 0.8
    c: DistanceY(g-6,g1) = 2
    c: DistanceY(g-6,g0) = 4.5
FEATURE [PartDesign::Chamfer] Chamfer008
  Angle = 45
  Base = -> Pad018 [Edge257]
  BaseFeature = -> Pad018
  ChamferType = 1
  FlipDirection = false
  Refine = true
  Size = 1
  Size2 = 6
  SupportTransform = false
  Suppressed = false
  UseAllEdges = false
FEATURE [PartDesign::Pocket] Pocket010
  BaseFeature = -> Chamfer008
  Direction = (0,1,-2e-16)
  Length = 1
  Length2 = 5
  Profile = -> Sketch126
  ReferenceAxis = -> Sketch126 [N_Axis]
  Refine = true
  Suppressed = false
  Type = 0
FEATURE [PartDesign::Pad] Pad015
  BaseFeature = -> Pocket010
  Direction = (0,-1,2e-16)
  Length = 2
  Length2 = 10
  Profile = -> Sketch121
  ReferenceAxis = -> Sketch121 [N_Axis]
  Refine = true
  Suppressed = false
  Type = 0
FEATURE [PartDesign::Pad] Pad016
  BaseFeature = -> Pad015
  Direction = (0,-1,2e-16)
  Length = 1.6
  Length2 = 10
  Profile = -> Sketch122
  ReferenceAxis = -> Sketch122 [N_Axis]
  Refine = true
  Suppressed = false
  Type = 0
FEATURE [Sketcher::SketchObject] Sketch129
  ArcFitTolerance = 1e-06
  AttachmentSupport = -> [Pad016]
  ExternalGeometry = -> [Binder001]
  FullyConstrained = true
  MakeInternals = false
  MapMode = 5
  Placement = pos=(0,-3.6,0) rot=(1,0,0;1.5708rad)
  sketch-geometry (12):
    g0: LineSegment [constr] StartX=-192.176 StartY=-3.18451 StartZ=0 EndX=-181.223 EndY=20.303 EndZ=0
    g1: LineSegment [constr] StartX=-202.765 StartY=20.303 StartZ=0 EndX=-181.223 EndY=20.303 EndZ=0
    g2: LineSegment StartX=-202.765 StartY=20.303 StartZ=0 EndX=-181.223 EndY=20.303 EndZ=0
    g3: LineSegment StartX=-192.176 StartY=-3.18451 StartZ=0 EndX=-196.804 EndY=-13.1107 EndZ=0
    g4: ArcOfCircle CenterX=-207.583 CenterY=4 CenterZ=0 NormalX=0 NormalY=0 NormalZ=1 AngleXU=0 Radius=17 StartAngle=5.84685 EndAngle=7.56663
    g5: ArcOfEllipse CenterX=-181.223 CenterY=8.55923 CenterZ=0 NormalX=0 NormalY=0 NormalZ=1 MajorRadius=23.4779 MinorRadius=11.7437 AngleXU=2e-16 StartAngle=4.71239 EndAngle=7.85398
    g6: LineSegment [constr] StartX=-157.745 StartY=8.55923 StartZ=0 EndX=-204.701 EndY=8.55923 EndZ=0
    g7: LineSegment [constr] StartX=-181.223 StartY=20.303 StartZ=0 EndX=-181.223 EndY=-3.18451 EndZ=0
    g8: GeomPoint [constr] X=-160.894 Y=8.55923 Z=0
    g9: GeomPoint [constr] X=-201.553 Y=8.55923 Z=0
    g10: ArcOfCircle CenterX=-181.223 CenterY=-20.3763 CenterZ=0 NormalX=0 NormalY=0 NormalZ=1 AngleXU=0 Radius=17.1918 StartAngle=1.57079 EndAngle=2.70526
    g11: GeomPoint [constr] X=-181.223 Y=-3.18451 Z=0
  constraints (23):
    c: Coincident(g0,g-5)
    c: Coincident(g1,g-6)
    c: Horizontal(g1)
    c: Coincident(g1,g0)
    c: Parallel(g0,g-4)
    c: Coincident(g2,g1)
    c: Coincident(g2,g0)
    c: Coincident(g3,g0)
    c: Equal(g4,g-5)
    c: Coincident(g4,g1)
    c: Coincident(g4,g0)
    c: InternalAlignment(g6-g9 -> g5) x4
    c: Vertical(g5,g0)
    c: Horizontal(g6)
    c: Coincident(g5,g0)
    c: DistanceX(g6,g-3) = 10.1
    c: Tangent(g10,g3) = -1.5708
    c: PointOnObject(g11,g10)
    c: Tangent(g5,g10,g11) = 1.5708
    c: Coincident(g10,g5)
    c: Coincident(g11,g7)
    c: Parallel(g3,g-4)
    c: Horizontal(g5,g0)
FEATURE [Sketcher::SketchObject] Sketch130
  ArcFitTolerance = 1e-06
  AttachmentOffset = pos=(0,0,-1.6) rot=(0,0,1;0rad)
  AttachmentSupport = -> [Pad016]
  ExternalGeometry = -> [Binder001]
  FullyConstrained = true
  MakeInternals = false
  MapMode = 5
  Placement = pos=(0,-2,-4e-16) rot=(1,0,0;1.5708rad)
  sketch-geometry (12):
    g0: LineSegment [constr] StartX=-192.176 StartY=-3.18451 StartZ=0 EndX=-181.223 EndY=20.303 EndZ=0
    g1: LineSegment [constr] StartX=-202.765 StartY=20.303 StartZ=0 EndX=-181.223 EndY=20.303 EndZ=0
    g2: LineSegment StartX=-202.765 StartY=20.303 StartZ=0 EndX=-181.223 EndY=20.303 EndZ=0
    g3: LineSegment StartX=-192.176 StartY=-3.18451 StartZ=0 EndX=-193.827 EndY=-6.72678 EndZ=0
    g4: ArcOfCircle CenterX=-207.583 CenterY=4 CenterZ=0 NormalX=0 NormalY=0 NormalZ=1 AngleXU=0 Radius=17 StartAngle=5.84685 EndAngle=7.56663
    g5: ArcOfEllipse CenterX=-181.223 CenterY=10.803 CenterZ=0 NormalX=0 NormalY=0 NormalZ=1 MajorRadius=14.4779 MinorRadius=9.5 AngleXU=0 StartAngle=4.71239 EndAngle=7.85398
    g6: LineSegment [constr] StartX=-166.745 StartY=10.803 StartZ=0 EndX=-195.701 EndY=10.803 EndZ=0
    g7: LineSegment [constr] StartX=-181.223 StartY=20.303 StartZ=0 EndX=-181.223 EndY=1.30297 EndZ=0
    g8: GeomPoint [constr] X=-170.298 Y=10.803 Z=0
    g9: GeomPoint [constr] X=-192.148 Y=10.803 Z=0
    g10: ArcOfCircle CenterX=-181.223 CenterY=-12.6042 CenterZ=0 NormalX=0 NormalY=0 NormalZ=1 AngleXU=0 Radius=13.9072 StartAngle=1.5708 EndAngle=2.70526
    g11: GeomPoint [constr] X=-181.223 Y=1.30297 Z=0
  constraints (23):
    c: Coincident(g0,g-5)
    c: Coincident(g1,g-6)
    c: Horizontal(g1)
    c: Coincident(g1,g0)
    c: Parallel(g0,g-4)
    c: Coincident(g2,g1)
    c: Coincident(g2,g0)
    c: Coincident(g3,g0)
    c: Equal(g4,g-5)
    c: Coincident(g4,g1)
    c: Coincident(g4,g0)
    c: InternalAlignment(g6-g9 -> g5) x4
    c: Vertical(g5,g0)
    c: Horizontal(g6)
    c: Coincident(g5,g0)
    c: DistanceX(g6,g-3) = 19.1
    c: Tangent(g10,g3) = -1.5708
    c: PointOnObject(g11,g10)
    c: Tangent(g5,g10,g11) = 1.5708
    c: Coincident(g10,g5)
    c: Coincident(g11,g7)
    c: Parallel(g3,g-4)
    c: DistanceY(g5,g0) = 19
FEATURE [Part::Part2DObjectPython] Clone2D001  label="Sketch130 (2D)"  # Draft 2D object (typed FeaturePython)
  Fuse = false
  Objects = -> [Sketch130]
  Placement = pos=(0,-2,-4e-16) rot=(1,0,0;1.5708rad)
  Scale = (1,1,1)
FEATURE [Sketcher::SketchObject] Sketch131
  ArcFitTolerance = 1e-06
  AttachmentOffset = pos=(0,0,-3.5) rot=(0,0,1;0rad)
  AttachmentSupport = -> [Pad016]
  ExternalGeometry = -> [Binder001]
  FullyConstrained = true
  MakeInternals = false
  MapMode = 5
  Placement = pos=(0,-0.1,-8e-16) rot=(1,0,0;1.5708rad)
  sketch-geometry (1):
    g0: GeomPoint X=-197.47 Y=8.55923 Z=0
  constraints (1):
    c: Symmetric(g-6,g-4,g0)
FEATURE [Sketcher::SketchObject] Sketch132
  ArcFitTolerance = 1e-06
  AttachmentSupport = -> [Pad016]
  ExternalGeometry = -> [Binder001]
  FullyConstrained = true
  MakeInternals = false
  MapMode = 5
  Placement = pos=(0,-3.6,0) rot=(1,0,0;1.5708rad)
  sketch-geometry (3):
    g0: LineSegment [constr] StartX=-215.42 StartY=-53.0314 StartZ=0 EndX=-167.782 EndY=-53.0314 EndZ=0
    g1: Circle CenterX=-191.282 CenterY=-53.0314 CenterZ=0 NormalX=0 NormalY=0 NormalZ=1 AngleXU=0 Radius=11.5
    g2: Circle CenterX=-191.282 CenterY=-53.0314 CenterZ=0 NormalX=0 NormalY=0 NormalZ=1 AngleXU=0 Radius=10.7
  constraints (8):
    c: Coincident(g0,g-3)
    c: PointOnObject(g0,g-4)
    c: Horizontal(g0)
    c: Diameter(g1) = 23
    c: PointOnObject(g1,g0)
    c: DistanceX(g1,g0) = 23.5
    c: Diameter(g2) = 21.4
    c: Coincident(g2,g1)
FEATURE [Part::Part2DObjectPython] ShapeString  # Draft 2D object (typed FeaturePython)
  FontFile = <path>
  Fuse = false
  Justification = 6
  JustificationReference = 0
  KeepLeftMargin = false
  MakeFace = true
  ObliqueAngle = 0
  Placement = pos=(-199,-3.6,-57.5) rot=(1,0,0;1.5708rad)
  ScaleToSize = true
  Size = 10
  String = AS
  Tracking = 0
FEATURE [Sketcher::SketchObject] Sketch133
  ArcFitTolerance = 1e-06
  AttachmentSupport = -> [Binder]
  ExternalGeometry = -> [Binder]
  FullyConstrained = true
  MakeInternals = false
  MapMode = 5
  Placement = pos=(0,9e-16,0) rot=(0,0.707107,0.707107;3.14159rad)
  sketch-geometry (30):
    g0: LineSegment StartX=0 StartY=39.2 StartZ=0 EndX=0 EndY=3.2 EndZ=0
    g1: LineSegment StartX=0 StartY=3.2 StartZ=0 EndX=82.8 EndY=3.2 EndZ=0
    g2: LineSegment StartX=82.8 StartY=3.2 StartZ=0 EndX=82.8 EndY=6.2 EndZ=0
    g3: LineSegment StartX=82.8 StartY=6.2 StartZ=0 EndX=91.752 EndY=6.2 EndZ=0
    g4: LineSegment StartX=0 StartY=39.2 StartZ=0 EndX=195.887 EndY=39.2 EndZ=0
    g5: LineSegment StartX=195.887 StartY=39.2 StartZ=0 EndX=202.765 EndY=20.303 EndZ=0
    g6: LineSegment StartX=192.333 StartY=24.9893 StartZ=0 EndX=196.467 EndY=26.4942 EndZ=0
    g7: LineSegment StartX=196.467 StartY=26.4942 StartZ=0 EndX=194.073 EndY=33.0721 EndZ=0
    g8: LineSegment StartX=194.073 StartY=33.0721 StartZ=0 EndX=189.939 EndY=31.5672 EndZ=0
    g9: LineSegment StartX=189.939 StartY=31.5672 StartZ=0 EndX=192.333 EndY=24.9893 EndZ=0
    g10: ArcOfCircle CenterX=107.6 CenterY=4 CenterZ=0 NormalX=0 NormalY=0 NormalZ=1 AngleXU=0 Radius=16 StartAngle=1.5708 EndAngle=3.00366
    g11: LineSegment StartX=107.6 StartY=20 StartZ=0 EndX=132.428 EndY=20 EndZ=0
    g12: ArcOfCircle [constr] CenterX=132.428 CenterY=4 CenterZ=0 NormalX=0 NormalY=0 NormalZ=1 AngleXU=0 Radius=16 StartAngle=0.314159 EndAngle=1.5708
    g13: LineSegment StartX=147.645 StartY=8.94427 StartZ=0 EndX=176.685 EndY=-80.4316 EndZ=0
    g14: LineSegment StartX=176.685 StartY=-80.4316 StartZ=0 EndX=215.932 EndY=-80.4316 EndZ=0
    g15: ArcOfCircle CenterX=207.583 CenterY=4 CenterZ=0 NormalX=0 NormalY=0 NormalZ=1 AngleXU=0 Radius=17 StartAngle=1.85815 EndAngle=3.57792
    g16: ArcOfCircle CenterX=184.801 CenterY=-67.3089 CenterZ=0 NormalX=0 NormalY=0 NormalZ=1 AngleXU=0 Radius=33.7833 StartAngle=5.88425 EndAngle=6.71952
    g17: LineSegment StartX=192.176 StartY=-3.18451 StartZ=0 EndX=215.42 EndY=-53.0314 EndZ=0
    g18: Circle CenterX=5.6 CenterY=34.8 CenterZ=0 NormalX=0 NormalY=0 NormalZ=1 AngleXU=0 Radius=1.8
    g19: Circle CenterX=5.6 CenterY=7.6 CenterZ=0 NormalX=0 NormalY=0 NormalZ=1 AngleXU=0 Radius=1.8
    g20: Circle CenterX=78.51 CenterY=34.8 CenterZ=0 NormalX=0 NormalY=0 NormalZ=1 AngleXU=0 Radius=1.8
    g21: Circle CenterX=78.51 CenterY=7.6 CenterZ=0 NormalX=0 NormalY=0 NormalZ=1 AngleXU=0 Radius=1.8
    g22: Circle CenterX=184.08 CenterY=34.8 CenterZ=0 NormalX=0 NormalY=0 NormalZ=1 AngleXU=0 Radius=1.8
    g23: Circle CenterX=179.305 CenterY=-76.8316 CenterZ=0 NormalX=0 NormalY=0 NormalZ=1 AngleXU=0 Radius=1.8
    g24: Circle CenterX=213.443 CenterY=-76.8316 CenterZ=0 NormalX=0 NormalY=0 NormalZ=1 AngleXU=0 Radius=1.8
    g25: Circle CenterX=19 CenterY=21.2 CenterZ=0 NormalX=0 NormalY=0 NormalZ=1 AngleXU=0 Radius=6.3
    g26: Circle CenterX=42 CenterY=21.2 CenterZ=0 NormalX=0 NormalY=0 NormalZ=1 AngleXU=0 Radius=6.3
    g27: Circle CenterX=65 CenterY=21.2 CenterZ=0 NormalX=0 NormalY=0 NormalZ=1 AngleXU=0 Radius=6.3
    g28: LineSegment StartX=132.428 StartY=20 StartZ=0 EndX=144.053 EndY=20 EndZ=0
    g29: LineSegment StartX=147.645 StartY=8.94427 StartZ=0 EndX=144.053 EndY=20 EndZ=0
  constraints (65):
    c: Coincident(g0,g-4)
    c: Coincident(g0,g-5)
    c: Coincident(g1,g0)
    c: Coincident(g1,g-6)
    c: Coincident(g2,g1)
    c: Coincident(g2,g-7)
    c: Coincident(g3,g2)
    c: Coincident(g3,g-8)
    c: Coincident(g4,g0)
    c: Coincident(g4,g-16)
    c: Coincident(g5,g4)
    c: Coincident(g5,g-16)
    c: Coincident(g6,g-20)
    c: Coincident(g6,g-21)
    c: Coincident(g7,g6)
    c: Coincident(g7,g-23)
    c: Coincident(g8,g7)
    c: Coincident(g8,g-22)
    c: Coincident(g9,g8)
    c: Coincident(g9,g6)
    c: Equal(g10,g-8)
    c: Coincident(g10,g3)
    c: Coincident(g10,g-9)
    c: Coincident(g11,g10)
    c: Coincident(g11,g-10)
    c: Equal(g12,g-10)
    c: Coincident(g12,g11)
    c: Coincident(g12,g-11)
    c: Coincident(g13,g12)
    c: Coincident(g13,g-12)
    c: Coincident(g14,g13)
    c: Coincident(g14,g-13)
    c: Equal(g15,g-15)
    c: Coincident(g15,g5)
    c: Coincident(g15,g-15)
    c: Equal(g16,g-13)
    c: Coincident(g16,g14)
    c: Coincident(g16,g-14)
    c: Coincident(g17,g15)
    c: Coincident(g17,g16)
    c: Equal(g18,g-28)
    c: Equal(g19,g-29)
    c: Equal(g20,g-26)
    c: Equal(g21,g-27)
    c: Equal(g22,g-17)
    c: Equal(g24,g-25)
    c: Equal(g23,g-24)
    c: Coincident(g23,g-24)
    c: Coincident(g24,g-25)
    c: Coincident(g22,g-17)
    c: Coincident(g20,g-26)
    c: Coincident(g21,g-27)
    c: Coincident(g18,g-28)
    c: Coincident(g19,g-29)
    c: Equal(g25,g-30)
    c: Equal(g26,g-31)
    c: Equal(g27,g-32)
    c: Coincident(g25,g-30)
    c: Coincident(g26,g-31)
    c: Coincident(g27,g-32)
    c: Parallel(g28,g11)
    c: Parallel(g29,g13)
    c: Coincident(g28,g11)
    c: Coincident(g29,g12)
    c: Coincident(g29,g28)
FEATURE [PartDesign::Pad] Pad019
  Direction = (0,1,-2e-16)
  Length = 2
  Length2 = 10
  Profile = -> Sketch133
  ReferenceAxis = -> Sketch133 [N_Axis]
  Refine = true
  Suppressed = false
  Type = 0
FEATURE [Sketcher::SketchObject] Sketch091  label="Sketch091 - forma anteriore"
  ArcFitTolerance = 1e-06
  AttachmentSupport = -> [Pad019]
  ExternalGeometry = -> [Binder]
  FullyConstrained = true
  MakeInternals = false
  MapMode = 5
  Placement = pos=(0,2,0) rot=(0,0.707107,0.707107;3.14159rad)
  sketch-geometry (12):
    g0: Circle CenterX=5.6 CenterY=34.8 CenterZ=0 NormalX=0 NormalY=0 NormalZ=1 AngleXU=0 Radius=1.8
    g1: Circle CenterX=5.6 CenterY=7.6 CenterZ=0 NormalX=0 NormalY=0 NormalZ=1 AngleXU=0 Radius=1.8
    g2: Circle CenterX=78.51 CenterY=34.8 CenterZ=0 NormalX=0 NormalY=0 NormalZ=1 AngleXU=0 Radius=1.8
    g3: Circle CenterX=78.51 CenterY=7.6 CenterZ=0 NormalX=0 NormalY=0 NormalZ=1 AngleXU=0 Radius=1.8
    g4: LineSegment StartX=0 StartY=39.2 StartZ=0 EndX=0 EndY=3.2 EndZ=0
    g5: LineSegment StartX=0 StartY=3.2 StartZ=0 EndX=82.8 EndY=3.2 EndZ=0
    g6: LineSegment StartX=82.8 StartY=3.2 StartZ=0 EndX=82.8 EndY=39.2 EndZ=0
    g7: LineSegment StartX=82.8 StartY=39.2 StartZ=0 EndX=0 EndY=39.2 EndZ=0
    g8: ArcOfCircle CenterX=19 CenterY=21.2 CenterZ=0 NormalX=0 NormalY=0 NormalZ=1 AngleXU=0 Radius=10 StartAngle=1.5708 EndAngle=4.71239
    g9: ArcOfCircle CenterX=65 CenterY=21.2 CenterZ=0 NormalX=0 NormalY=0 NormalZ=1 AngleXU=0 Radius=10 StartAngle=4.71239 EndAngle=7.85398
    g10: LineSegment StartX=19 StartY=31.2 StartZ=0 EndX=65 EndY=31.2 EndZ=0
    g11: LineSegment StartX=19 StartY=11.2 StartZ=0 EndX=65 EndY=11.2 EndZ=0
  constraints (25):
    c: Equal(g2,g-7)
    c: Equal(g3,g-8)
    c: Equal(g1,g-13)
    c: Equal(g0,g-12)
    c: Coincident(g0,g-12)
    c: Coincident(g1,g-13)
    c: Coincident(g3,g-8)
    c: Coincident(g2,g-7)
    c: Coincident(g4,g-4)
    c: Coincident(g4,g-5)
    c: Coincident(g5,g4)
    c: Coincident(g5,g-6)
    c: Coincident(g6,g5)
    c: PointOnObject(g6,g-3)
    c: Vertical(g6)
    c: Coincident(g7,g6)
    c: Coincident(g7,g4)
    c: Tangent(g8,g10) = 1.5708
    c: Tangent(g8,g11) = -1.5708
    c: Tangent(g9,g10) = 1.5708
    c: Tangent(g9,g11) = -1.5708
    c: Equal(g8,g9)
    c: Radius(g8) = 10
    c: Coincident(g8,g-11)
    c: Coincident(g9,g-9)
FEATURE [Sketcher::SketchObject] Sketch093  label="Sketch093 - scavi interni pulsanti"
  ArcFitTolerance = 1e-06
  AttachmentSupport = -> [Pad019]
  ExternalGeometry = -> [Binder]
  FullyConstrained = true
  MakeInternals = false
  MapMode = 5
  Placement = pos=(0,1.8e-15,0) rot=(1,0,0;1.5708rad)
  sketch-geometry (3):
    g0: Circle CenterX=-65 CenterY=21.2 CenterZ=0 NormalX=0 NormalY=0 NormalZ=1 AngleXU=0 Radius=7.3
    g1: Circle CenterX=-42 CenterY=21.2 CenterZ=0 NormalX=0 NormalY=0 NormalZ=1 AngleXU=0 Radius=7.3
    g2: Circle CenterX=-19 CenterY=21.2 CenterZ=0 NormalX=0 NormalY=0 NormalZ=1 AngleXU=0 Radius=7.3
  constraints (6):
    c: Coincident(g0,g-3)
    c: Coincident(g1,g-4)
    c: Coincident(g2,g-5)
    c: Diameter(g0) = 14.6
    c: Diameter(g1) = 14.6
    c: Diameter(g2) = 14.6
FEATURE [Sketcher::SketchObject] Sketch094  label="Sketch094 - forma centrale"
  ArcFitTolerance = 1e-06
  AttachmentSupport = -> [Pad019]
  ExternalGeometry = -> [Binder]
  FullyConstrained = true
  MakeInternals = false
  MapMode = 5
  Placement = pos=(0,2,0) rot=(0,0.707107,0.707107;3.14159rad)
  sketch-geometry (4):
    g0: LineSegment StartX=137.815 StartY=39.2 StartZ=0 EndX=142.655 EndY=24.303 EndZ=0
    g1: LineSegment StartX=110.815 StartY=24.303 StartZ=0 EndX=142.655 EndY=24.303 EndZ=0
    g2: LineSegment StartX=137.815 StartY=39.2 StartZ=0 EndX=110.815 EndY=39.2 EndZ=0
    g3: ArcOfCircle CenterX=92.2534 CenterY=31.7515 CenterZ=0 NormalX=0 NormalY=0 NormalZ=1 AngleXU=0 Radius=20 StartAngle=5.90156 EndAngle=6.66481
  constraints (12):
    c: PointOnObject(g0,g-3)
    c: Tangent(g0,g-5)
    c: Horizontal(g1)
    c: Coincident(g1,g0)
    c: Coincident(g2,g0)
    c: PointOnObject(g2,g-3)
    c: DistanceX(g2,g2) = 27
    c: Vertical(g1,g2)
    c: Coincident(g3,g2)
    c: Radius(g3) = 20
    c: Coincident(g3,g1)
    c: DistanceY(g-6,g0) = 4
FEATURE [Sketcher::SketchObject] Sketch095  label="Sketch095 - forma posteriore"
  ArcFitTolerance = 1e-06
  AttachmentSupport = -> [Pad019]
  ExternalGeometry = -> [Binder]
  FullyConstrained = true
  MakeInternals = false
  MapMode = 5
  Placement = pos=(0,2,0) rot=(0,0.707107,0.707107;3.14159rad)
  sketch-geometry (15):
    g0: LineSegment StartX=137.815 StartY=39.2 StartZ=0 EndX=143.955 EndY=20.303 EndZ=0
    g1: LineSegment StartX=143.955 StartY=20.303 StartZ=0 EndX=190.141 EndY=20.303 EndZ=0
    g2: ArcOfCircle CenterX=184.08 CenterY=34.8 CenterZ=0 NormalX=0 NormalY=0 NormalZ=1 AngleXU=0 Radius=3.5 StartAngle=3.49066 EndAngle=4.71239
    g3: LineSegment StartX=180.791 StartY=33.6029 StartZ=0 EndX=178.754 EndY=39.2 EndZ=0
    g4: LineSegment StartX=184.08 StartY=31.3 StartZ=0 EndX=186.139 EndY=31.3 EndZ=0
    g5: LineSegment StartX=190.141 StartY=20.303 StartZ=0 EndX=186.139 EndY=31.3 EndZ=0
    g6: LineSegment StartX=137.815 StartY=39.2 StartZ=0 EndX=156.815 EndY=39.2 EndZ=0
    g7: LineSegment StartX=178.754 StartY=39.2 StartZ=0 EndX=168.815 EndY=39.2 EndZ=0
    g8: LineSegment StartX=156.815 StartY=31.2 StartZ=0 EndX=168.815 EndY=31.2 EndZ=0
    g9: ArcOfCircle CenterX=176.411 CenterY=35.2 CenterZ=0 NormalX=0 NormalY=0 NormalZ=1 AngleXU=0 Radius=20 StartAngle=2.94023 EndAngle=3.34295
    g10: ArcOfCircle CenterX=188.411 CenterY=35.2 CenterZ=0 NormalX=0 NormalY=0 NormalZ=1 AngleXU=0 Radius=20 StartAngle=2.94023 EndAngle=3.34295
    g11: LineSegment StartX=157.815 StartY=39.2 StartZ=0 EndX=167.815 EndY=39.2 EndZ=0
    g12: LineSegment StartX=157.436 StartY=36.2 StartZ=0 EndX=167.436 EndY=36.2 EndZ=0
    g13: ArcOfCircle CenterX=177.411 CenterY=35.2 CenterZ=0 NormalX=0 NormalY=0 NormalZ=1 AngleXU=0 Radius=20 StartAngle=2.94023 EndAngle=3.09157
    g14: ArcOfCircle CenterX=187.411 CenterY=35.2 CenterZ=0 NormalX=0 NormalY=0 NormalZ=1 AngleXU=0 Radius=20 StartAngle=2.94023 EndAngle=3.09157
  constraints (46):
    c: PointOnObject(g0,g-3)
    c: Tangent(g0,g-6)
    c: Coincident(g1,g0)
    c: Horizontal(g1)
    c: Radius(g2) = 3.5
    c: Coincident(g2,g-5)
    c: PointOnObject(g3,g-3)
    c: Parallel(g3,g-4)
    c: Tangent(g3,g2) = 1.5708
    c: Horizontal(g4)
    c: Tangent(g4,g2) = -1.5708
    c: Coincident(g5,g1)
    c: Parallel(g5,g-4)
    c: Coincident(g5,g4)
    c: DistanceX(g4,g-8) = 3.8
    c: Coincident(g6,g0)
    c: PointOnObject(g6,g-3)
    c: Coincident(g7,g3)
    c: PointOnObject(g7,g-3)
    c: Horizontal(g8)
    c: DistanceX(g6,g7) = 12
    c: Vertical(g8,g6)
    c: Vertical(g7,g8)
    c: DistanceY(g8,g6) = 8
    c: Coincident(g9,g8)
    c: Coincident(g9,g6)
    c: Coincident(g10,g7)
    c: Coincident(g10,g8)
    c: Radius(g9) = 20
    c: Radius(g10) = 20
    c: PointOnObject(g11,g-3)
    c: PointOnObject(g11,g-3)
    c: DistanceX(g11,g11) = 10
    c: DistanceX(g6,g11) = 1
    c: Horizontal(g12)
    c: Equal(g12,g11)
    c: DistanceY(g12,g11) = 3
    c: Coincident(g13,g11)
    c: Coincident(g13,g12)
    c: Radius(g13) = 20
    c: Coincident(g14,g11)
    c: Coincident(g14,g12)
    c: Radius(g14) = 20
    c: DistanceX(g0,g6) = 19
    c: Horizontal(g9,g13)
    c: Horizontal(g0,g-4)
FEATURE [Sketcher::SketchObject] Sketch096  label="Sketch096 - forma impugnatura"
  ArcFitTolerance = 1e-06
  AttachmentSupport = -> [Pad019]
  ExternalGeometry = -> [Binder]
  FullyConstrained = true
  MakeInternals = false
  MapMode = 5
  Placement = pos=(0,2,0) rot=(0,0.707107,0.707107;3.14159rad)
  sketch-geometry (8):
    g0: LineSegment StartX=176.685 StartY=-80.4316 StartZ=0 EndX=143.955 EndY=20.303 EndZ=0
    g1: LineSegment StartX=176.685 StartY=-80.4316 StartZ=0 EndX=215.932 EndY=-80.4316 EndZ=0
    g2: Circle CenterX=179.305 CenterY=-76.8316 CenterZ=0 NormalX=0 NormalY=0 NormalZ=1 AngleXU=0 Radius=3
    g3: Circle CenterX=213.443 CenterY=-76.8316 CenterZ=0 NormalX=0 NormalY=0 NormalZ=1 AngleXU=0 Radius=3
    g4: LineSegment StartX=143.955 StartY=20.303 StartZ=0 EndX=202.765 EndY=20.303 EndZ=0
    g5: LineSegment StartX=215.42 StartY=-53.0314 StartZ=0 EndX=192.176 EndY=-3.18451 EndZ=0
    g6: ArcOfCircle CenterX=184.801 CenterY=-67.3089 CenterZ=0 NormalX=0 NormalY=0 NormalZ=1 AngleXU=0 Radius=33.7833 StartAngle=5.88425 EndAngle=6.71952
    g7: ArcOfCircle CenterX=207.583 CenterY=4 CenterZ=0 NormalX=0 NormalY=0 NormalZ=1 AngleXU=0 Radius=17 StartAngle=1.85815 EndAngle=3.57792
  constraints (19):
    c: Coincident(g0,g-4)
    c: PointOnObject(g0,g-3)
    c: Horizontal(g0,g-7)
    c: Coincident(g1,g0)
    c: Coincident(g1,g-5)
    c: Diameter(g2) = 6
    c: Diameter(g3) = 6
    c: Coincident(g2,g-9)
    c: Coincident(g3,g-10)
    c: Coincident(g4,g0)
    c: Coincident(g5,g-6)
    c: Coincident(g6,g1)
    c: Coincident(g6,g5)
    c: Equal(g-5,g6)
    c: Coincident(g5,g-7)
    c: Coincident(g4,g-7)
    c: Tangent(g7,g-7)
    c: Coincident(g7,g4)
    c: Coincident(g7,g5)
FEATURE [Sketcher::SketchObject] Sketch097
  ArcFitTolerance = 1e-06
  AttachmentSupport = -> [Pad019]
  ExternalGeometry = -> [Binder]
  FullyConstrained = true
  MakeInternals = false
  MapMode = 5
  Placement = pos=(0,2,0) rot=(0,0.707107,0.707107;3.14159rad)
  sketch-geometry (4):
    g0: LineSegment StartX=90 StartY=36.8 StartZ=0 EndX=108 EndY=36.8 EndZ=0
    g1: LineSegment StartX=108 StartY=36.8 StartZ=0 EndX=108 EndY=26.8 EndZ=0
    g2: LineSegment StartX=108 StartY=26.8 StartZ=0 EndX=90 EndY=26.8 EndZ=0
    g3: ArcOfCircle CenterX=94 CenterY=31.8 CenterZ=0 NormalX=0 NormalY=0 NormalZ=1 AngleXU=0 Radius=6.40312 StartAngle=2.24554 EndAngle=4.03765
  constraints (13):
    c: Horizontal(g0)
    c: Coincident(g1,g0)
    c: Vertical(g1)
    c: DistanceX(g0,g0) = 18
    c: DistanceY(g1,g1) = 10
    c: Coincident(g2,g1)
    c: Horizontal(g2)
    c: Equal(g2,g0)
    c: DistanceY(g0,g-3) = 2.4
    c: Coincident(g3,g0)
    c: Coincident(g3,g2)
    c: DistanceX(g2,g3) = 4
    c: DistanceX(g-3,g0) = 90
FEATURE [PartDesign::Chamfer] Chamfer015
  Angle = 45
  Base = -> Pad019 [Edge19,Edge22,Edge79]
  BaseFeature = -> Pad019
  ChamferType = 0
  FlipDirection = false
  Refine = true
  Size = 1.9
  Size2 = 1
  SupportTransform = false
  Suppressed = false
  UseAllEdges = false
FEATURE [PartDesign::Pocket] Pocket002
  BaseFeature = -> Chamfer015
  Direction = (0,1,-2e-16)
  Length = 1.2
  Length2 = 5
  Profile = -> Sketch093
  ReferenceAxis = -> Sketch093 [N_Axis]
  Refine = true
  Suppressed = false
  Type = 0
FEATURE [PartDesign::Pad] Pad005
  BaseFeature = -> Pocket002
  Direction = (0,1,-2e-16)
  Length = 1.6
  Length2 = 10
  Profile = -> Sketch091
  ReferenceAxis = -> Sketch091 [N_Axis]
  Refine = true
  Suppressed = false
  Type = 0
FEATURE [Sketcher::SketchObject] Sketch092  label="Sketch092 - scavi per viti anteriori"
  ArcFitTolerance = 1e-06
  AttachmentSupport = -> [Pad005]
  ExternalGeometry = -> [Binder]
  FullyConstrained = true
  MakeInternals = false
  MapMode = 5
  Placement = pos=(0,3.6,0) rot=(0,0.707107,0.707107;3.14159rad)
  sketch-geometry (20):
    g0: ArcOfCircle CenterX=5.6 CenterY=7.6 CenterZ=0 NormalX=0 NormalY=0 NormalZ=1 AngleXU=0 Radius=3.5 StartAngle=0 EndAngle=1.5708
    g1: ArcOfCircle CenterX=5.6 CenterY=34.8 CenterZ=0 NormalX=0 NormalY=0 NormalZ=1 AngleXU=0 Radius=3.5 StartAngle=4.71239 EndAngle=6.28319
    g2: ArcOfCircle CenterX=78.51 CenterY=34.8 CenterZ=0 NormalX=0 NormalY=0 NormalZ=1 AngleXU=0 Radius=3.5 StartAngle=3.14159 EndAngle=4.71239
    g3: ArcOfCircle CenterX=78.51 CenterY=7.6 CenterZ=0 NormalX=0 NormalY=0 NormalZ=1 AngleXU=0 Radius=3.5 StartAngle=1.5708 EndAngle=3.14159
    g4: LineSegment StartX=0 StartY=3.2 StartZ=0 EndX=0 EndY=11.1 EndZ=0
    g5: LineSegment StartX=0 StartY=11.1 StartZ=0 EndX=5.6 EndY=11.1 EndZ=0
    g6: LineSegment StartX=0 StartY=3.2 StartZ=0 EndX=9.1 EndY=3.2 EndZ=0
    g7: LineSegment StartX=9.1 StartY=3.2 StartZ=0 EndX=9.1 EndY=7.6 EndZ=0
    g8: LineSegment StartX=0 StartY=39.2 StartZ=0 EndX=0 EndY=31.3 EndZ=0
    g9: LineSegment StartX=0 StartY=31.3 StartZ=0 EndX=5.6 EndY=31.3 EndZ=0
    g10: LineSegment StartX=0 StartY=39.2 StartZ=0 EndX=9.1 EndY=39.2 EndZ=0
    g11: LineSegment StartX=9.1 StartY=39.2 StartZ=0 EndX=9.1 EndY=34.8 EndZ=0
    g12: LineSegment StartX=82.8 StartY=39.2 StartZ=0 EndX=75.01 EndY=39.2 EndZ=0
    g13: LineSegment StartX=82.8 StartY=39.2 StartZ=0 EndX=82.8 EndY=31.3 EndZ=0
    g14: LineSegment StartX=82.8 StartY=31.3 StartZ=0 EndX=78.51 EndY=31.3 EndZ=0
    g15: LineSegment StartX=82.8 StartY=3.2 StartZ=0 EndX=75.01 EndY=3.2 EndZ=0
    g16: LineSegment StartX=75.01 StartY=3.2 StartZ=0 EndX=75.01 EndY=7.6 EndZ=0
    g17: LineSegment StartX=82.8 StartY=3.2 StartZ=0 EndX=82.8 EndY=11.1 EndZ=0
    g18: LineSegment StartX=82.8 StartY=11.1 StartZ=0 EndX=78.51 EndY=11.1 EndZ=0
    g19: LineSegment StartX=75.01 StartY=39.2 StartZ=0 EndX=75.01 EndY=34.8 EndZ=0
  constraints (48):
    c: Radius(g0) = 3.5
    c: Coincident(g0,g-10)
    c: Radius(g1) = 3.5
    c: Coincident(g1,g-9)
    c: Radius(g2) = 3.5
    c: Coincident(g2,g-8)
    c: Radius(g3) = 3.5
    c: Coincident(g3,g-7)
    c: Coincident(g4,g-5)
    c: PointOnObject(g4,g-4)
    c: Coincident(g5,g4)
    c: Horizontal(g5)
    c: Coincident(g6,g4)
    c: PointOnObject(g6,g-5)
    c: Coincident(g7,g6)
    c: Vertical(g7)
    c: Coincident(g8,g-4)
    c: PointOnObject(g8,g-4)
    c: Coincident(g9,g8)
    c: Horizontal(g9)
    c: Coincident(g10,g8)
    c: PointOnObject(g10,g-3)
    c: Coincident(g11,g10)
    c: Vertical(g11)
    c: PointOnObject(g12,g-3)
    c: PointOnObject(g12,g-3)
    c: Coincident(g13,g12)
    c: Vertical(g13)
    c: Coincident(g14,g13)
    c: Horizontal(g14)
    c: Coincident(g15,g-6)
    c: PointOnObject(g15,g-5)
    c: Coincident(g16,g15)
    c: Vertical(g16)
    c: Coincident(g17,g15)
    c: Coincident(g18,g17)
    c: Horizontal(g18)
    c: Tangent(g3,g18) = -1.5708
    c: Tangent(g16,g3) = 1.5708
    c: Coincident(g19,g12)
    c: Vertical(g19)
    c: Tangent(g2,g19) = -1.5708
    c: Tangent(g2,g14) = 1.5708
    c: Tangent(g0,g7) = -1.5708
    c: Tangent(g0,g5) = 1.5708
    c: Tangent(g9,g1) = -1.5708
    c: Tangent(g1,g11) = 1.5708
    c: Tangent(g17,g13)
FEATURE [PartDesign::Pocket] Pocket001
  BaseFeature = -> Pad005
  Direction = (0,-1,2e-16)
  Length = 1.6
  Length2 = 5
  Profile = -> Sketch092
  ReferenceAxis = -> Sketch092 [N_Axis]
  Refine = true
  Suppressed = false
  Type = 0
FEATURE [PartDesign::Pad] Pad006
  BaseFeature = -> Pocket001
  Direction = (0,1,-2e-16)
  Length = 0.8
  Length2 = 10
  Profile = -> Sketch094
  ReferenceAxis = -> Sketch094 [N_Axis]
  Refine = true
  Suppressed = false
  Type = 0
FEATURE [PartDesign::Pad] Pad007
  BaseFeature = -> Pad006
  Direction = (0,1,-2e-16)
  Length = 2
  Length2 = 10
  Profile = -> Sketch095
  ReferenceAxis = -> Sketch095 [N_Axis]
  Refine = true
  Suppressed = false
  Type = 0
FEATURE [PartDesign::Pad] Pad008  label="Pad008 - forma impugnatura"
  BaseFeature = -> Pad007
  Direction = (0,1,-2e-16)
  Length = 1.6
  Length2 = 10
  Profile = -> Sketch096
  ReferenceAxis = -> Sketch096 [N_Axis]
  Refine = true
  Suppressed = false
  Type = 0
FEATURE [PartDesign::Pad] Pad009
  BaseFeature = -> Pad008
  Direction = (0,1,-2e-16)
  Length = 1.6
  Length2 = 10
  Profile = -> Sketch097
  ReferenceAxis = -> Sketch097 [N_Axis]
  Refine = true
  Suppressed = false
  Type = 0
FEATURE [Sketcher::SketchObject] Sketch098
  ArcFitTolerance = 1e-06
  AttachmentSupport = -> [Pad006]
  ExternalGeometry = -> [Binder]
  FullyConstrained = true
  MakeInternals = false
  MapMode = 5
  Placement = pos=(0,2.8,-7e-16) rot=(0,0.707107,0.707107;3.14159rad)
  sketch-geometry (4):
    g0: LineSegment StartX=118 StartY=39.2 StartZ=0 EndX=129 EndY=39.2 EndZ=0
    g1: LineSegment StartX=120.599 StartY=31.2 StartZ=0 EndX=131.599 EndY=31.2 EndZ=0
    g2: LineSegment StartX=129 StartY=39.2 StartZ=0 EndX=131.599 EndY=31.2 EndZ=0
    g3: LineSegment StartX=118 StartY=39.2 StartZ=0 EndX=120.599 EndY=31.2 EndZ=0
  constraints (12):
    c: PointOnObject(g0,g-3)
    c: PointOnObject(g0,g-3)
    c: DistanceX(g0,g0) = 11
    c: Horizontal(g1)
    c: Equal(g1,g0)
    c: Coincident(g2,g0)
    c: Coincident(g3,g0)
    c: Parallel(g-4,g2)
    c: Coincident(g1,g2)
    c: Coincident(g1,g3)
    c: DistanceY(g1,g0) = 8
    c: DistanceX(g-3,g0) = 118
FEATURE [Sketcher::SketchObject] Sketch099
  ArcFitTolerance = 1e-06
  AttachmentSupport = -> [Pad008]
  ExternalGeometry = -> [Binder]
  FullyConstrained = true
  MakeInternals = false
  MapMode = 5
  Placement = pos=(0,3.6,0) rot=(0,0.707107,0.707107;3.14159rad)
  sketch-geometry (13):
    g0: LineSegment StartX=192.176 StartY=-3.18451 StartZ=0 EndX=196.804 EndY=-13.1108 EndZ=0
    g1: LineSegment [constr] StartX=202.765 StartY=20.303 StartZ=0 EndX=181.223 EndY=20.303 EndZ=0
    g2: LineSegment [constr] StartX=181.223 StartY=20.303 StartZ=0 EndX=181.223 EndY=-3.18451 EndZ=0
    g3: ArcOfCircle CenterX=181.223 CenterY=-20.3764 CenterZ=0 NormalX=0 NormalY=0 NormalZ=1 AngleXU=0 Radius=17.1918 StartAngle=0.436332 EndAngle=1.57079
    g4: ArcOfEllipse CenterX=181.223 CenterY=8.55923 CenterZ=0 NormalX=0 NormalY=0 NormalZ=1 MajorRadius=23.4779 MinorRadius=11.7437 AngleXU=0 StartAngle=1.5708 EndAngle=4.71239
    g5: LineSegment [constr] StartX=204.701 StartY=8.55923 StartZ=0 EndX=157.745 EndY=8.55923 EndZ=0
    g6: LineSegment [constr] StartX=181.223 StartY=20.303 StartZ=0 EndX=181.223 EndY=-3.18451 EndZ=0
    g7: GeomPoint [constr] X=201.553 Y=8.55923 Z=0
    g8: GeomPoint [constr] X=160.894 Y=8.55923 Z=0
    g9: GeomPoint [constr] X=181.223 Y=-3.18451 Z=0
    g10: LineSegment StartX=181.223 StartY=20.303 StartZ=0 EndX=202.765 EndY=20.303 EndZ=0
    g11: ArcOfCircle CenterX=207.583 CenterY=4 CenterZ=0 NormalX=0 NormalY=0 NormalZ=1 AngleXU=0 Radius=17 StartAngle=1.85815 EndAngle=3.57792
    g12: LineSegment [constr] StartX=172.411 StartY=39.2 StartZ=0 EndX=192.176 EndY=-3.18451 EndZ=0
  constraints (27):
    c: Coincident(g1,g-7)
    c: Horizontal(g1)
    c: Coincident(g2,g1)
    c: Vertical(g2)
    c: Horizontal(g2,g0)
    c: Coincident(g3,g0)
    c: Coincident(g3,g2)
    c: InternalAlignment(g5-g8 -> g4) x4
    c: Horizontal(g5)
    c: PointOnObject(g4,g2)
    c: Coincident(g4,g1)
    c: DistanceX(g-3,g5) = 10.1
    c: Coincident(g4,g2)
    c: Tangent(g3,g-5)
    c: PointOnObject(g9,g4)
    c: PointOnObject(g9,g3)
    c: Tangent(g4,g3,g9) = 1.5708
    c: Coincident(g10,g1)
    c: Coincident(g10,g1)
    c: Equal(g11,g-4)
    c: Coincident(g11,g1)
    c: Coincident(g11,g0)
    c: PointOnObject(g12,g-6)
    c: PointOnObject(g1,g12)
    c: Tangent(g12,g-5) = -1.5708
    c: Tangent(g0,g-5) = -1.5708
    c: Horizontal(g9,g12)
FEATURE [Sketcher::SketchObject] Sketch106  label="Sketch106 - smusso impuniatura interno"
  ArcFitTolerance = 1e-06
  AttachmentSupport = -> [Pad008]
  ExternalGeometry = -> [Pad008]
  FullyConstrained = true
  MakeInternals = false
  MapMode = 5
  Placement = pos=(0,-1.586e-13,-80.4316) rot=(1,0,0;3.14159rad)
  sketch-geometry (9):
    g0: LineSegment StartX=-176.685 StartY=-3.6 StartZ=0 EndX=-176.685 EndY=-1.04263e-11 EndZ=0
    g1: LineSegment [constr] StartX=-176.685 StartY=-1.416e-13 StartZ=0 EndX=-176.685 EndY=-1.04263e-11 EndZ=0
    g2: LineSegment [constr] StartX=-186.685 StartY=-3.6 StartZ=0 EndX=-186.685 EndY=-1.04263e-11 EndZ=0
    g3: ArcOfEllipse CenterX=-186.685 CenterY=-1.04263e-11 CenterZ=0 NormalX=0 NormalY=0 NormalZ=1 MajorRadius=10 MinorRadius=3.6 AngleXU=3.14159 StartAngle=1.5708 EndAngle=3.14159
    g4: LineSegment [constr] StartX=-196.685 StartY=-1.416e-13 StartZ=0 EndX=-176.685 EndY=-1.416e-13 EndZ=0
    g5: LineSegment [constr] StartX=-186.685 StartY=-3.6 StartZ=0 EndX=-186.685 EndY=3.6 EndZ=0
    g6: GeomPoint [constr] X=-196.015 Y=-1.398e-13 Z=0
    g7: GeomPoint [constr] X=-177.356 Y=-1.416e-13 Z=0
    g8: LineSegment StartX=-176.685 StartY=-3.6 StartZ=0 EndX=-186.685 EndY=-3.6 EndZ=0
  constraints (15):
    c: PointOnObject(g2,g-3)
    c: Coincident(g1,g-5)
    c: DistanceY(g1,g1) = 0
    c: Coincident(g0,g1)
    c: DistanceX(g2,g-5) = 10
    c: Vertical(g2)
    c: Horizontal(g2,g0)
    c: InternalAlignment(g4-g7 -> g3) x4
    c: Coincident(g3,g2)
    c: Horizontal(g4)
    c: Coincident(g3,g0)
    c: Tangent(g0,g-5) = 1.5708
    c: Coincident(g3,g2)
    c: Coincident(g8,g0)
    c: Coincident(g8,g2)
FEATURE [Sketcher::SketchObject] Sketch107  label="Sketch107 - smusso impugnatura esterno"
  ArcFitTolerance = 1e-06
  AttachmentSupport = -> [Pad008]
  ExternalGeometry = -> [Pad008]
  FullyConstrained = true
  MakeInternals = false
  MapMode = 5
  Placement = pos=(0,-1.586e-13,-80.4316) rot=(1,0,0;3.14159rad)
  sketch-geometry (9):
    g0: LineSegment [constr] StartX=-215.932 StartY=-1.416e-13 StartZ=0 EndX=-215.932 EndY=-6.48e-14 EndZ=0
    g1: LineSegment StartX=-215.932 StartY=-3.6 StartZ=0 EndX=-215.932 EndY=-6.48e-14 EndZ=0
    g2: LineSegment StartX=-215.932 StartY=-3.6 StartZ=0 EndX=-205.932 EndY=-3.6 EndZ=0
    g3: LineSegment [constr] StartX=-205.932 StartY=-3.6 StartZ=0 EndX=-205.932 EndY=-6.48e-14 EndZ=0
    g4: ArcOfEllipse CenterX=-205.932 CenterY=-6.48e-14 CenterZ=0 NormalX=0 NormalY=0 NormalZ=1 MajorRadius=10 MinorRadius=3.6 AngleXU=-3.14159 StartAngle=-2.66e-14 EndAngle=1.5708
    g5: LineSegment [constr] StartX=-215.932 StartY=-1.416e-13 StartZ=0 EndX=-195.932 EndY=-1.416e-13 EndZ=0
    g6: LineSegment [constr] StartX=-205.932 StartY=-3.6 StartZ=0 EndX=-205.932 EndY=3.6 EndZ=0
    g7: GeomPoint [constr] X=-215.262 Y=-1.54e-13 Z=0
    g8: GeomPoint [constr] X=-196.602 Y=-1.551e-13 Z=0
  constraints (16):
    c: Coincident(g0,g-6)
    c: PointOnObject(g0,g-6)
    c: DistanceY(g0,g0) = 0
    c: Coincident(g1,g-6)
    c: Coincident(g1,g0)
    c: Tangent(g2,g-3)
    c: DistanceX(g2,g2) = 10
    c: Coincident(g3,g2)
    c: Vertical(g3)
    c: Horizontal(g3,g0)
    c: InternalAlignment(g5-g8 -> g4) x4
    c: Coincident(g4,g3)
    c: Horizontal(g5)
    c: Coincident(g4,g0)
    c: Coincident(g4,g2)
    c: PointOnObject(g2,g1)
FEATURE [Sketcher::SketchObject] Sketch108
  ArcFitTolerance = 1e-06
  AttachmentOffset = pos=(0,0,-1.6) rot=(0,0,1;0rad)
  AttachmentSupport = -> [Pad008]
  ExternalGeometry = -> [Binder]
  FullyConstrained = true
  MakeInternals = false
  MapMode = 5
  Placement = pos=(0,2,4e-16) rot=(0,0.707107,0.707107;3.14159rad)
  sketch-geometry (14):
    g0: LineSegment StartX=192.176 StartY=-3.18451 StartZ=0 EndX=193.827 EndY=-6.72678 EndZ=0
    g1: LineSegment [constr] StartX=202.765 StartY=20.303 StartZ=0 EndX=181.223 EndY=20.303 EndZ=0
    g2: LineSegment [constr] StartX=181.223 StartY=20.303 StartZ=0 EndX=181.223 EndY=1.30297 EndZ=0
    g3: ArcOfCircle CenterX=181.223 CenterY=-12.6042 CenterZ=0 NormalX=0 NormalY=0 NormalZ=1 AngleXU=0 Radius=13.9072 StartAngle=0.436332 EndAngle=1.5708
    g4: ArcOfEllipse CenterX=181.223 CenterY=10.803 CenterZ=0 NormalX=0 NormalY=0 NormalZ=1 MajorRadius=14.4779 MinorRadius=9.5 AngleXU=0 StartAngle=1.5708 EndAngle=4.71239
    g5: LineSegment [constr] StartX=195.701 StartY=10.803 StartZ=0 EndX=166.745 EndY=10.803 EndZ=0
    g6: LineSegment [constr] StartX=181.223 StartY=20.303 StartZ=0 EndX=181.223 EndY=1.30297 EndZ=0
    g7: GeomPoint [constr] X=192.148 Y=10.803 Z=0
    g8: GeomPoint [constr] X=170.298 Y=10.803 Z=0
    g9: LineSegment StartX=181.223 StartY=20.303 StartZ=0 EndX=202.765 EndY=20.303 EndZ=0
    g10: ArcOfCircle CenterX=207.583 CenterY=4 CenterZ=0 NormalX=0 NormalY=0 NormalZ=1 AngleXU=0 Radius=17 StartAngle=1.85815 EndAngle=3.57792
    g11: LineSegment [constr] StartX=172.411 StartY=39.2 StartZ=0 EndX=192.176 EndY=-3.18451 EndZ=0
    g12: GeomPoint [constr] X=181.223 Y=1.30297 Z=0
    g13: GeomPoint [constr] X=181.223 Y=1.30297 Z=0
  constraints (28):
    c: Coincident(g1,g-7)
    c: Horizontal(g1)
    c: Coincident(g2,g1)
    c: Vertical(g2)
    c: Coincident(g3,g2)
    c: InternalAlignment(g5-g8 -> g4) x4
    c: Horizontal(g5)
    c: PointOnObject(g4,g2)
    c: Coincident(g4,g1)
    c: DistanceX(g-3,g5) = 19.1
    c: Coincident(g4,g2)
    c: Coincident(g9,g1)
    c: Coincident(g9,g1)
    c: Coincident(g10,g1)
    c: Coincident(g10,g0)
    c: PointOnObject(g11,g-6)
    c: PointOnObject(g1,g11)
    c: DistanceY(g2,g1) = 19
    c: Coincident(g10,g-4)
    c: PointOnObject(g12,g4)
    c: PointOnObject(g12,g3)
    c: Tangent(g11,g-5) = -1.5708
    c: Tangent(g0,g-5) = -1.5708
    c: Tangent(g3,g0) = 1.5708
    c: PointOnObject(g13,g4)
    c: PointOnObject(g13,g3)
    c: Tangent(g4,g3,g13) = 1.5708
    c: Horizontal(g11,g0)
FEATURE [Part::Part2DObjectPython] Clone2D  label="Sketch108 (2D)"  # Draft 2D object (typed FeaturePython)
  Fuse = false
  Objects = -> [Sketch108]
  Placement = pos=(0,2,4e-16) rot=(0,0.707107,0.707107;3.14159rad)
  Scale = (1,1,1)
FEATURE [Sketcher::SketchObject] Sketch109
  ArcFitTolerance = 1e-06
  AttachmentOffset = pos=(0,0,-3.5) rot=(0,0,1;0rad)
  AttachmentSupport = -> [Pad008]
  ExternalGeometry = -> [Binder]
  FullyConstrained = true
  MakeInternals = false
  MapMode = 5
  Placement = pos=(0,0.1,8e-16) rot=(0,0.707107,0.707107;3.14159rad)
  sketch-geometry (1):
    g0: GeomPoint X=197.47 Y=8.55923 Z=0
  constraints (1):
    c: Symmetric(g-7,g-5,g0)
FEATURE [PartDesign::Chamfer] Chamfer005
  Angle = 45
  Base = -> Pad009 [Edge215,Edge212]
  BaseFeature = -> Pad009
  ChamferType = 1
  FlipDirection = false
  Refine = true
  Size = 1.5
  Size2 = 2.8
  SupportTransform = false
  Suppressed = false
  UseAllEdges = false
FEATURE [Sketcher::SketchObject] Sketch111
  ArcFitTolerance = 1e-06
  AttachmentSupport = -> [Pad009]
  ExternalGeometry = -> [Pad009]
  FullyConstrained = true
  MakeInternals = false
  MapMode = 5
  Placement = pos=(0,3.6,-8e-16) rot=(0,0.707107,0.707107;3.14159rad)
  sketch-geometry (21):
    g0: LineSegment [constr] StartX=97 StartY=36.8 StartZ=0 EndX=97 EndY=26.8 EndZ=0
    g1: LineSegment StartX=97 StartY=28.6 StartZ=0 EndX=97 EndY=27.8 EndZ=0
    g2: LineSegment StartX=97 StartY=27.8 StartZ=0 EndX=108 EndY=27.8 EndZ=0
    g3: LineSegment StartX=108 StartY=27.8 StartZ=0 EndX=108 EndY=28.6 EndZ=0
    g4: LineSegment StartX=108 StartY=28.6 StartZ=0 EndX=97 EndY=28.6 EndZ=0
    g5: LineSegment StartX=97 StartY=35.8 StartZ=0 EndX=97 EndY=35 EndZ=0
    g6: LineSegment StartX=97 StartY=35 StartZ=0 EndX=108 EndY=35 EndZ=0
    g7: LineSegment StartX=108 StartY=35 StartZ=0 EndX=108 EndY=35.8 EndZ=0
    g8: LineSegment StartX=108 StartY=35.8 StartZ=0 EndX=97 EndY=35.8 EndZ=0
    g9: LineSegment StartX=97 StartY=30.4 StartZ=0 EndX=97 EndY=29.6 EndZ=0
    g10: LineSegment StartX=97 StartY=29.6 StartZ=0 EndX=108 EndY=29.6 EndZ=0
    g11: LineSegment StartX=108 StartY=29.6 StartZ=0 EndX=108 EndY=30.4 EndZ=0
    g12: LineSegment StartX=108 StartY=30.4 StartZ=0 EndX=97 EndY=30.4 EndZ=0
    g13: LineSegment StartX=97 StartY=34 StartZ=0 EndX=97 EndY=33.2 EndZ=0
    g14: LineSegment StartX=97 StartY=33.2 StartZ=0 EndX=108 EndY=33.2 EndZ=0
    g15: LineSegment StartX=108 StartY=33.2 StartZ=0 EndX=108 EndY=34 EndZ=0
    g16: LineSegment StartX=108 StartY=34 StartZ=0 EndX=97 EndY=34 EndZ=0
    g17: LineSegment StartX=97 StartY=32.2 StartZ=0 EndX=97 EndY=31.4 EndZ=0
    g18: LineSegment StartX=97 StartY=31.4 StartZ=0 EndX=108 EndY=31.4 EndZ=0
    g19: LineSegment StartX=108 StartY=31.4 StartZ=0 EndX=108 EndY=32.2 EndZ=0
    g20: LineSegment StartX=108 StartY=32.2 StartZ=0 EndX=97 EndY=32.2 EndZ=0
  constraints (54):
    c: Vertical(g0)
    c: PointOnObject(g0,g-3)
    c: PointOnObject(g0,g-4)
    c: DistanceX(g0,g-5) = 11
    c: Coincident(g1,g2)
    c: Coincident(g2,g3)
    c: Coincident(g3,g4)
    c: Coincident(g4,g1)
    c: Horizontal(g2)
    c: Horizontal(g4)
    c: Tangent(g1,g0)
    c: Tangent(g3,g-5)
    c: DistanceY(g2,g3) = 0.8
    c: Coincident(g5,g6)
    c: Coincident(g6,g7)
    c: Coincident(g7,g8)
    c: Coincident(g8,g5)
    c: Horizontal(g6)
    c: Horizontal(g8)
    c: DistanceY(g6,g7) = 0.8
    c: Coincident(g9,g10)
    c: Coincident(g10,g11)
    c: Coincident(g11,g12)
    c: Coincident(g12,g9)
    c: Horizontal(g10)
    c: Horizontal(g12)
    c: DistanceY(g10,g11) = 0.8
    c: Tangent(g5,g0)
    c: Tangent(g7,g-5)
    c: Tangent(g9,g0)
    c: Tangent(g11,g-5)
    c: Coincident(g13,g14)
    c: Coincident(g14,g15)
    c: Coincident(g15,g16)
    c: Coincident(g16,g13)
    c: Horizontal(g14)
    c: Horizontal(g16)
    c: DistanceY(g14,g15) = 0.8
    c: Tangent(g13,g0)
    c: Tangent(g15,g-5)
    c: Coincident(g17,g18)
    c: Coincident(g18,g19)
    c: Coincident(g19,g20)
    c: Coincident(g20,g17)
    c: Horizontal(g18)
    c: Horizontal(g20)
    c: DistanceY(g18,g19) = 0.8
    c: Tangent(g17,g0)
    c: Tangent(g19,g-5)
    c: DistanceY(g1,g9) = 1
    c: DistanceY(g9,g17) = 1
    c: DistanceY(g17,g13) = 1
    c: DistanceY(g13,g5) = 1
    c: DistanceY(g0,g1) = 1
FEATURE [PartDesign::Pocket] Pocket004
  BaseFeature = -> Chamfer005
  Direction = (0,-1,2e-16)
  Length = 1
  Length2 = 5
  Profile = -> Sketch111
  ReferenceAxis = -> Sketch111 [N_Axis]
  Refine = true
  Suppressed = false
  Type = 0
FEATURE [PartDesign::Pad] Pad010
  BaseFeature = -> Pocket004
  Direction = (0,1,-2e-16)
  Length = 1.2
  Length2 = 10
  Profile = -> Sketch098
  ReferenceAxis = -> Sketch098 [N_Axis]
  Refine = true
  Suppressed = false
  Type = 0
FEATURE [PartDesign::Chamfer] Chamfer006
  Angle = 45
  Base = -> Pad010 [Edge291]
  BaseFeature = -> Pad010
  ChamferType = 1
  FlipDirection = false
  Refine = true
  Size = 1
  Size2 = 6
  SupportTransform = false
  Suppressed = false
  UseAllEdges = false
FEATURE [Sketcher::SketchObject] Sketch110
  ArcFitTolerance = 1e-06
  AttachmentSupport = -> [Pad010]
  ExternalGeometry = -> [Sketch098]
  FullyConstrained = true
  MakeInternals = false
  MapMode = 5
  Placement = pos=(0,4,-9e-16) rot=(0,0.707107,0.707107;3.14159rad)
  sketch-geometry (8):
    g0: LineSegment StartX=119.69 StartY=34 StartZ=0 EndX=130.69 EndY=34 EndZ=0
    g1: LineSegment StartX=119.95 StartY=33.2 StartZ=0 EndX=130.95 EndY=33.2 EndZ=0
    g2: LineSegment StartX=119.137 StartY=35.7 StartZ=0 EndX=130.137 EndY=35.7 EndZ=0
    g3: LineSegment StartX=118.877 StartY=36.5 StartZ=0 EndX=129.877 EndY=36.5 EndZ=0
    g4: LineSegment StartX=118.877 StartY=36.5 StartZ=0 EndX=119.137 EndY=35.7 EndZ=0
    g5: LineSegment StartX=129.877 StartY=36.5 StartZ=0 EndX=130.137 EndY=35.7 EndZ=0
    g6: LineSegment StartX=119.69 StartY=34 StartZ=0 EndX=119.95 EndY=33.2 EndZ=0
    g7: LineSegment StartX=130.69 StartY=34 StartZ=0 EndX=130.95 EndY=33.2 EndZ=0
  constraints (24):
    c: Horizontal(g0)
    c: Horizontal(g1)
    c: Horizontal(g2)
    c: Horizontal(g3)
    c: Equal(g1,g-5)
    c: Equal(g0,g-5)
    c: Equal(g2,g-5)
    c: Equal(g3,g-5)
    c: PointOnObject(g0,g-3)
    c: PointOnObject(g1,g-3)
    c: PointOnObject(g2,g-3)
    c: PointOnObject(g3,g-3)
    c: Coincident(g4,g3)
    c: Coincident(g4,g2)
    c: Coincident(g5,g3)
    c: Coincident(g5,g2)
    c: Coincident(g6,g0)
    c: Coincident(g6,g1)
    c: Coincident(g7,g0)
    c: Coincident(g7,g1)
    c: DistanceY(g1,g0) = 0.8
    c: DistanceY(g2,g3) = 0.8
    c: DistanceY(g-5,g1) = 2
    c: DistanceY(g-5,g2) = 4.5
FEATURE [PartDesign::Pocket] Pocket003
  BaseFeature = -> Chamfer006
  Direction = (0,-1,2e-16)
  Length = 1
  Length2 = 5
  Profile = -> Sketch110
  ReferenceAxis = -> Sketch110 [N_Axis]
  Refine = true
  Suppressed = false
  Type = 0
FEATURE [PartDesign::SubtractivePipe] SubtractivePipe
  AuxilleryCurvelinear = true
  AuxillerySpineTangent = false
  BaseFeature = -> Pocket003
  Binormal = (0,0,0)
  Mode = 0
  Profile = -> Sketch106
  Refine = true
  Spine = -> Pad008 [Edge215]
  SpineTangent = false
  Suppressed = false
  Transformation = 0
  Transition = 0
FEATURE [PartDesign::SubtractivePipe] SubtractivePipe001
  AuxilleryCurvelinear = true
  AuxillerySpineTangent = false
  BaseFeature = -> SubtractivePipe
  Binormal = (0,0,0)
  Mode = 0
  Profile = -> Sketch107
  Refine = true
  Spine = -> Pad008 [Edge213,Edge216,Edge210]
  SpineTangent = false
  Suppressed = false
  Transformation = 0
  Transition = 0
FEATURE [PartDesign::SubtractiveLoft] SubtractiveLoft
  BaseFeature = -> SubtractivePipe001
  Closed = false
  Profile = -> Sketch099
  Refine = true
  Ruled = false
  Sections = -> [Sketch108]
  Suppressed = false
FEATURE [PartDesign::SubtractiveLoft] SubtractiveLoft001
  BaseFeature = -> SubtractiveLoft
  Closed = false
  Profile = -> Clone2D
  Refine = true
  Ruled = false
  Sections = -> [Sketch109]
  Suppressed = false
FEATURE [Sketcher::SketchObject] Sketch112
  ArcFitTolerance = 1e-06
  AttachmentSupport = -> [Pad008]
  ExternalGeometry = -> [Binder]
  FullyConstrained = true
  MakeInternals = false
  MapMode = 5
  Placement = pos=(0,3.6,0) rot=(0,0.707107,0.707107;3.14159rad)
  sketch-geometry (4):
    g0: LineSegment [constr] StartX=167.782 StartY=-53.0314 StartZ=0 EndX=215.42 EndY=-53.0314 EndZ=0
    g1: GeomPoint [constr] X=191.282 Y=-53.0314 Z=0
    g2: Circle CenterX=191.282 CenterY=-53.0314 CenterZ=0 NormalX=0 NormalY=0 NormalZ=1 AngleXU=0 Radius=11.5
    g3: Circle CenterX=191.282 CenterY=-53.0314 CenterZ=0 NormalX=0 NormalY=0 NormalZ=1 AngleXU=0 Radius=10.7
  constraints (9):
    c: Horizontal(g0)
    c: PointOnObject(g0,g-3)
    c: Diameter(g2) = 23
    c: Coincident(g2,g1)
    c: Diameter(g3) = 21.4
    c: Coincident(g3,g1)
    c: DistanceX(g0,g1) = 23.5
    c: PointOnObject(g1,g0)
    c: Coincident(g0,g-4)
FEATURE [PartDesign::Chamfer] Chamfer016
  Angle = 45
  Base = -> SubtractiveLoft001 [Edge118,Edge117,Edge119,Edge120,Edge109]
  BaseFeature = -> SubtractiveLoft001
  ChamferType = 0
  FlipDirection = false
  Refine = true
  Size = 1.5
  Size2 = 1
  SupportTransform = false
  Suppressed = false
  UseAllEdges = false
FEATURE [PartDesign::Chamfer] Chamfer017
  Angle = 45
  Base = -> Chamfer016 [Edge15]
  BaseFeature = -> Chamfer016
  ChamferType = 0
  FlipDirection = false
  Refine = true
  Size = 1.6
  Size2 = 1
  SupportTransform = false
  Suppressed = false
  UseAllEdges = false
FEATURE [PartDesign::Chamfer] Chamfer018
  Angle = 45
  Base = -> Chamfer017 [Edge10]
  BaseFeature = -> Chamfer017
  ChamferType = 0
  FlipDirection = false
  Refine = true
  Size = 3.5
  Size2 = 1
  SupportTransform = false
  Suppressed = false
  UseAllEdges = false
FEATURE [PartDesign::Chamfer] Chamfer019
  Angle = 45
  Base = -> Chamfer018 [Edge94]
  BaseFeature = -> Chamfer018
  ChamferType = 0
  FlipDirection = false
  Refine = true
  Size = 1.9
  Size2 = 1
  SupportTransform = false
  Suppressed = false
  UseAllEdges = false
FEATURE [PartDesign::Fillet] Fillet009
  Base = -> Chamfer019 [Edge83]
  BaseFeature = -> Chamfer019
  Radius = 1.1
  Refine = true
  SupportTransform = false
  Suppressed = false
  UseAllEdges = false
FEATURE [PartDesign::Fillet] Fillet010
  Base = -> Fillet009 [Edge77]
  BaseFeature = -> Fillet009
  Radius = 1.9
  Refine = true
  SupportTransform = false
  Suppressed = false
  UseAllEdges = false
FEATURE [PartDesign::Pocket] Pocket005
  BaseFeature = -> Fillet010
  Direction = (0,-1,2e-16)
  Length = 0.8
  Length2 = 5
  Profile = -> Sketch112
  ReferenceAxis = -> Sketch112 [N_Axis]
  Refine = true
  Suppressed = false
  Type = 0
FEATURE [Part::Part2DObjectPython] ShapeString001  # Draft 2D object (typed FeaturePython)
  FontFile = <path>
  Fuse = false
  Justification = 6
  JustificationReference = 0
  KeepLeftMargin = false
  MakeFace = true
  ObliqueAngle = 0
  Placement = pos=(-183.5,3.6,-57.5) rot=(0,0.707107,0.707107;3.14159rad)
  ScaleToSize = true
  Size = 10
  String = AS
  Tracking = 0
FEATURE [PartDesign::Pocket] Pocket013
  BaseFeature = -> Pocket005
  Direction = (-1e-16,-1,2e-16)
  Length = 1
  Length2 = 5
  Profile = -> ShapeString001
  ReferenceAxis = -> ShapeString001 [N_Axis]
  Refine = true
  Suppressed = false
  Type = 0
FEATURE [PartDesign::Pad] Pad020
  Direction = (0,-1,2e-16)
  Length = 25.2
  Length2 = 10
  Midplane = true
  Placement = pos=(0,0,0) rot=(1,0,0;1.5708rad)
  Profile = -> Sketch021
  ReferenceAxis = -> Sketch021 [N_Axis]
  Refine = true
  Suppressed = false
  Type = 0
FEATURE [PartDesign::Body] Body001  label="perno fermo rumble e driver solenoide"
  AllowCompound = false
  Group = -> [Sketch021,Pad020]
  Origin = -> Origin001
  Tip = -> Pad020
FEATURE [PartDesign::Pad] Pad021
  Direction = (0,-1,2e-16)
  Length = 16.8
  Length2 = 10
  Midplane = true
  Placement = pos=(0,0,0) rot=(1,0,0;1.5708rad)
  Profile = -> Sketch061
  ReferenceAxis = -> Sketch061 [N_Axis]
  Refine = true
  Suppressed = false
  Type = 0
FEATURE [PartDesign::Pocket] Pocket014
  BaseFeature = -> Pad021
  Direction = (0,1,-2e-16)
  Length = 12.8
  Length2 = 5
  Midplane = true
  Placement = pos=(0,0,0) rot=(1,0,0;1.5708rad)
  Profile = -> Sketch062
  ReferenceAxis = -> Sketch062 [N_Axis]
  Refine = true
  Suppressed = false
  Type = 0
FEATURE [PartDesign::Pad] Pad022
  BaseFeature = -> Pocket014
  Direction = (0,-1,2e-16)
  Length = 7.6
  Length2 = 10
  Midplane = true
  Placement = pos=(0,0,0) rot=(1,0,0;1.5708rad)
  Profile = -> Sketch063
  ReferenceAxis = -> Sketch063 [N_Axis]
  Refine = true
  Suppressed = false
  Type = 0
FEATURE [PartDesign::Body] Body003  label="blocco switch"
  AllowCompound = false
  Group = -> [Sketch061,Sketch062,Sketch063,Pad021,Pocket014,Pad022]
  Origin = -> Origin003
  Tip = -> Pad022
FEATURE [PartDesign::Pad] Pad024
  Direction = (0,-1,2e-16)
  Length = 17
  Length2 = 10
  Midplane = true
  Placement = pos=(0,0,0) rot=(1,0,0;1.5708rad)
  Profile = -> Sketch045
  ReferenceAxis = -> Sketch045 [N_Axis]
  Refine = true
  Suppressed = false
  Type = 0
FEATURE [PartDesign::Pocket] Pocket015
  BaseFeature = -> Pad024
  Direction = (-1,0,0)
  Length = 8
  Length2 = 5
  Placement = pos=(0,0,0) rot=(1,0,0;1.5708rad)
  Profile = -> Sketch047
  ReferenceAxis = -> Sketch047 [N_Axis]
  Refine = true
  Reversed = true
  Suppressed = false
  Type = 0
FEATURE [PartDesign::Pocket] Pocket016
  BaseFeature = -> Pocket015
  Direction = (-1,0,0)
  Length = 1
  Length2 = 5
  Placement = pos=(0,0,0) rot=(1,0,0;1.5708rad)
  Profile = -> Sketch046
  ReferenceAxis = -> Sketch046 [N_Axis]
  Refine = true
  Reversed = true
  Suppressed = false
  Type = 0
FEATURE [PartDesign::Pocket] Pocket017
  BaseFeature = -> Pocket016
  Direction = (0,1,-2e-16)
  Length = 17
  Length2 = 5
  Midplane = true
  Placement = pos=(0,0,0) rot=(1,0,0;1.5708rad)
  Profile = -> Sketch048
  ReferenceAxis = -> Sketch048 [N_Axis]
  Refine = true
  Suppressed = false
  Type = 0
FEATURE [PartDesign::Pad] Pad025
  BaseFeature = -> Pocket017
  Direction = (0,-1,2e-16)
  Length = 17
  Length2 = 10
  Midplane = true
  Placement = pos=(0,0,0) rot=(1,0,0;1.5708rad)
  Profile = -> Sketch049
  ReferenceAxis = -> Sketch049 [N_Axis]
  Refine = true
  Suppressed = false
  Type = 0
FEATURE [PartDesign::Pad] Pad026
  BaseFeature = -> Pad025
  Direction = (0,-1,2e-16)
  Length = 17
  Length2 = 10
  Midplane = true
  Placement = pos=(0,0,0) rot=(1,0,0;1.5708rad)
  Profile = -> Sketch066
  ReferenceAxis = -> Sketch066 [N_Axis]
  Refine = true
  Suppressed = false
  Type = 0
FEATURE [PartDesign::Pad] Pad027
  BaseFeature = -> Pad026
  Direction = (0,-1,2e-16)
  Length = 5
  Length2 = 10
  Midplane = true
  Placement = pos=(0,0,0) rot=(1,0,0;1.5708rad)
  Profile = -> Sketch064
  ReferenceAxis = -> Sketch064 [N_Axis]
  Refine = true
  Suppressed = false
  Type = 0
FEATURE [PartDesign::Pad] Pad028
  BaseFeature = -> Pad027
  Direction = (1,0,0)
  Length = 1
  Length2 = 10
  Placement = pos=(0,0,0) rot=(1,0,0;1.5708rad)
  Profile = -> Sketch068
  ReferenceAxis = -> Sketch068 [N_Axis]
  Refine = true
  Reversed = true
  Suppressed = false
  Type = 0
FEATURE [PartDesign::Chamfer] Chamfer020
  Angle = 45
  Base = -> Pad028 [Edge73,Edge75,Edge78,Edge77]
  BaseFeature = -> Pad028
  ChamferType = 0
  FlipDirection = false
  Placement = pos=(0,0,0) rot=(1,0,0;1.5708rad)
  Refine = true
  Size = 0.5
  Size2 = 1
  SupportTransform = false
  Suppressed = false
  UseAllEdges = false
FEATURE [PartDesign::Body] Body002  label="supporto per neopixel"
  AllowCompound = false
  Group = -> [Sketch045,Sketch047,Sketch046,Sketch048,Sketch049,Sketch066,Sketch064,Sketch068,Pad024,Pocket015,Pocket016,Pocket017,Pad025,Pad026,Pad027,Pad028,Chamfer020]
  Origin = -> Origin002
  Tip = -> Chamfer020
FEATURE [Sketcher::SketchObject] Sketch134  label="perno fermo rumble002"
  ArcFitTolerance = 1e-06
  AttachmentSupport = -> [XZ_Plane008]
  FullyConstrained = true
  MakeInternals = false
  MapMode = 5
  Placement = pos=(0,0,0) rot=(1,0,0;1.5708rad)
  sketch-geometry (16):
    g0: LineSegment StartX=0 StartY=0.45 StartZ=0 EndX=0 EndY=1.55 EndZ=0
    g1: LineSegment StartX=0.45 StartY=2 StartZ=0 EndX=1.55 EndY=2 EndZ=0
    g2: LineSegment StartX=2 StartY=1.55 StartZ=0 EndX=2 EndY=0.45 EndZ=0
    g3: LineSegment StartX=1.55 StartY=0 StartZ=0 EndX=0.45 EndY=0 EndZ=0
    g4: ArcOfCircle [constr] CenterX=0.45 CenterY=1.55 CenterZ=0 NormalX=0 NormalY=0 NormalZ=1 AngleXU=0 Radius=0.45 StartAngle=1.5708 EndAngle=3.14159
    g5: GeomPoint [constr] X=0 Y=2 Z=0
    g6: LineSegment StartX=0.45 StartY=2 StartZ=0 EndX=0 EndY=1.55 EndZ=0
    g7: ArcOfCircle [constr] CenterX=1.55 CenterY=1.55 CenterZ=0 NormalX=0 NormalY=0 NormalZ=1 AngleXU=0 Radius=0.45 StartAngle=0 EndAngle=1.5708
    g8: GeomPoint [constr] X=2 Y=2 Z=0
    g9: LineSegment StartX=2 StartY=1.55 StartZ=0 EndX=1.55 EndY=2 EndZ=0
    g10: ArcOfCircle [constr] CenterX=1.55 CenterY=0.45 CenterZ=0 NormalX=0 NormalY=0 NormalZ=1 AngleXU=0 Radius=0.45 StartAngle=4.71239 EndAngle=6.28319
    g11: GeomPoint [constr] X=2 Y=0 Z=0
    g12: LineSegment StartX=1.55 StartY=0 StartZ=0 EndX=2 EndY=0.45 EndZ=0
    g13: ArcOfCircle [constr] CenterX=0.45 CenterY=0.45 CenterZ=0 NormalX=0 NormalY=0 NormalZ=1 AngleXU=0 Radius=0.45 StartAngle=3.14159 EndAngle=4.71239
    g14: GeomPoint [constr] X=0 Y=0 Z=0
    g15: LineSegment StartX=0 StartY=0.45 StartZ=0 EndX=0.45 EndY=0 EndZ=0
  constraints (35):
    c: Coincident(g14,g-1)
    c: PointOnObject(g5,g-2)
    c: Horizontal(g1)
    c: Vertical(g2)
    c: Horizontal(g3)
    c: DistanceX(g5,g8) = 2
    c: DistanceY(g11,g8) = 2
    c: PointOnObject(g5,g0)
    c: PointOnObject(g5,g1)
    c: Tangent(g0,g4) = 1.5708
    c: Tangent(g1,g4) = 1.5708
    c: Coincident(g6,g0)
    c: Coincident(g6,g1)
    c: PointOnObject(g8,g2)
    c: PointOnObject(g8,g1)
    c: Tangent(g2,g7) = 1.5708
    c: Tangent(g1,g7) = 1.5708
    c: Coincident(g9,g2)
    c: Coincident(g9,g1)
    c: PointOnObject(g11,g2)
    c: PointOnObject(g11,g3)
    c: Tangent(g2,g10) = 1.5708
    c: Tangent(g3,g10) = 1.5708
    c: Coincident(g12,g2)
    c: Coincident(g12,g3)
    c: PointOnObject(g14,g0)
    c: PointOnObject(g14,g3)
    c: Tangent(g0,g13) = 1.5708
    c: Tangent(g3,g13) = 1.5708
    c: Coincident(g15,g0)
    c: Coincident(g15,g3)
    c: Equal(g6,g9)
    c: Equal(g9,g12)
    c: Equal(g12,g15)
    c: DistanceX(g14,g3) = 0.45
FEATURE [PartDesign::Pad] Pad029
  Direction = (0,-1,2e-16)
  Length = 17
  Length2 = 10
  Midplane = true
  Placement = pos=(0,0,0) rot=(1,0,0;1.5708rad)
  Profile = -> Sketch134
  ReferenceAxis = -> Sketch134 [N_Axis]
  Refine = true
  Suppressed = false
  Type = 0
FEATURE [PartDesign::Body] Body008  label="perno fermo neopixel"
  AllowCompound = false
  Group = -> [Sketch134,Pad029]
  Origin = -> Origin008
  Tip = -> Pad029
FEATURE [Sketcher::SketchObject] Sketch135  label="perno fermo rumble003"
  ArcFitTolerance = 1e-06
  AttachmentSupport = -> [XZ_Plane009]
  FullyConstrained = true
  MakeInternals = false
  MapMode = 5
  Placement = pos=(0,0,0) rot=(1,0,0;1.5708rad)
  sketch-geometry (16):
    g0: LineSegment StartX=4.69e-14 StartY=0.8 StartZ=0 EndX=-3.04e-14 EndY=3.1 EndZ=0
    g1: LineSegment StartX=0.8 StartY=3.9 StartZ=0 EndX=3.1 EndY=3.9 EndZ=0
    g2: LineSegment StartX=3.9 StartY=3.1 StartZ=0 EndX=3.9 EndY=0.8 EndZ=0
    g3: LineSegment StartX=3.1 StartY=0 StartZ=0 EndX=0.8 EndY=0 EndZ=0
    g4: ArcOfCircle [constr] CenterX=0.8 CenterY=3.1 CenterZ=0 NormalX=0 NormalY=0 NormalZ=1 AngleXU=0 Radius=0.8 StartAngle=1.5708 EndAngle=3.14159
    g5: GeomPoint [constr] X=0 Y=3.9 Z=0
    g6: LineSegment StartX=0.8 StartY=3.9 StartZ=0 EndX=-3.04e-14 EndY=3.1 EndZ=0
    g7: ArcOfCircle [constr] CenterX=3.1 CenterY=3.1 CenterZ=0 NormalX=0 NormalY=0 NormalZ=1 AngleXU=0 Radius=0.8 StartAngle=-2.4e-14 EndAngle=1.5708
    g8: GeomPoint [constr] X=3.9 Y=3.9 Z=0
    g9: LineSegment StartX=3.9 StartY=3.1 StartZ=0 EndX=3.1 EndY=3.9 EndZ=0
    g10: ArcOfCircle [constr] CenterX=3.1 CenterY=0.8 CenterZ=0 NormalX=0 NormalY=0 NormalZ=1 AngleXU=0 Radius=0.8 StartAngle=4.71239 EndAngle=6.28319
    g11: GeomPoint [constr] X=3.9 Y=0 Z=0
    g12: LineSegment StartX=3.1 StartY=0 StartZ=0 EndX=3.9 EndY=0.8 EndZ=0
    g13: ArcOfCircle [constr] CenterX=0.8 CenterY=0.8 CenterZ=0 NormalX=0 NormalY=0 NormalZ=1 AngleXU=0 Radius=0.8 StartAngle=3.14159 EndAngle=4.71239
    g14: GeomPoint [constr] X=0 Y=0 Z=0
    g15: LineSegment StartX=4.69e-14 StartY=0.8 StartZ=0 EndX=0.8 EndY=0 EndZ=0
  constraints (35):
    c: Coincident(g14,g-1)
    c: PointOnObject(g5,g-2)
    c: Horizontal(g1)
    c: Vertical(g2)
    c: Horizontal(g3)
    c: DistanceX(g5,g8) = 3.9
    c: DistanceY(g11,g8) = 3.9
    c: PointOnObject(g5,g0)
    c: PointOnObject(g5,g1)
    c: Tangent(g0,g4) = 1.5708
    c: Tangent(g1,g4) = 1.5708
    c: Coincident(g6,g0)
    c: Coincident(g6,g1)
    c: PointOnObject(g8,g2)
    c: PointOnObject(g8,g1)
    c: Tangent(g2,g7) = 1.5708
    c: Tangent(g1,g7) = 1.5708
    c: Coincident(g9,g2)
    c: Coincident(g9,g1)
    c: PointOnObject(g11,g2)
    c: PointOnObject(g11,g3)
    c: Tangent(g2,g10) = 1.5708
    c: Tangent(g3,g10) = 1.5708
    c: Coincident(g12,g2)
    c: Coincident(g12,g3)
    c: PointOnObject(g14,g0)
    c: PointOnObject(g14,g3)
    c: Tangent(g0,g13) = 1.5708
    c: Tangent(g3,g13) = 1.5708
    c: Coincident(g15,g0)
    c: Coincident(g15,g3)
    c: Equal(g6,g9)
    c: Equal(g9,g12)
    c: Equal(g12,g15)
    c: DistanceX(g14,g3) = 0.8
FEATURE [PartDesign::Pad] Pad030
  Direction = (0,-1,2e-16)
  Length = 25.2
  Length2 = 10
  Midplane = true
  Placement = pos=(0,0,0) rot=(1,0,0;1.5708rad)
  Profile = -> Sketch135
  ReferenceAxis = -> Sketch135 [N_Axis]
  Refine = true
  Suppressed = false
  Type = 0
FEATURE [PartDesign::Body] Body009  label="perno fermo switch - caricabatterie - grilletto"
  AllowCompound = false
  Group = -> [Sketch135,Pad030]
  Origin = -> Origin009
  Tip = -> Pad030
FEATURE [Sketcher::SketchObject] Sketch136  label="scavo_rele"
  ArcFitTolerance = 1e-06
  AttachmentSupport = -> [XZ_Plane]
  ExternalGeometry = -> [Sketch]
  FullyConstrained = true
  MakeInternals = false
  MapMode = 5
  Placement = pos=(0,0,0) rot=(1,0,0;1.5708rad)
  sketch-geometry (7):
    g0: LineSegment [constr] StartX=-172.456 StartY=-60.9321 StartZ=0 EndX=-176.597 EndY=-73.6763 EndZ=0
    g1: LineSegment [constr] StartX=-172.456 StartY=-60.9321 StartZ=0 EndX=-170.364 EndY=-61.612 EndZ=0
    g2: LineSegment [constr] StartX=-172.456 StartY=-60.9321 StartZ=0 EndX=-176.07 EndY=-59.7579 EndZ=0
    g3: LineSegment StartX=-176.07 StartY=-59.7579 StartZ=0 EndX=-170.364 EndY=-61.612 EndZ=0
    g4: LineSegment StartX=-176.07 StartY=-59.7579 StartZ=0 EndX=-180.211 EndY=-72.502 EndZ=0
    g5: LineSegment StartX=-170.364 StartY=-61.612 StartZ=0 EndX=-174.505 EndY=-74.3561 EndZ=0
    g6: LineSegment StartX=-180.211 StartY=-72.502 StartZ=0 EndX=-174.505 EndY=-74.3561 EndZ=0
  constraints (19):
    c: Tangent(g0,g-3)
    c: Distance(g0,g-3) = 87.2
    c: Distance(g0,g0) = 13.4
    c: Coincident(g1,g0)
    c: Coincident(g2,g0)
    c: Distance(g2) = 3.8
    c: Distance(g1) = 2.2
    c: Perpendicular(g0,g1)
    c: Perpendicular(g0,g2)
    c: Coincident(g3,g2)
    c: Coincident(g3,g1)
    c: Equal(g4,g0)
    c: Equal(g5,g0)
    c: Parallel(g4,g0)
    c: Parallel(g5,g0)
    c: Coincident(g4,g2)
    c: Coincident(g5,g1)
    c: Coincident(g6,g4)
    c: Coincident(g6,g5)
FEATURE [Part::Extrusion] Extrude076  label="Extrude076 - scavo_rele"
  Base = -> Sketch136
  Dir = (0,-1,2e-16)
  DirMode = 2
  FaceMakerClass = Part::FaceMakerBullseye
  FaceMakerMode = 3
  LengthFwd = 18.2
  LengthRev = 0
  Solid = true
  Symmetric = true
FEATURE [Sketcher::SketchObject] Sketch137  label="scavo_nuovo_driver"
  ArcFitTolerance = 1e-06
  AttachmentSupport = -> [XZ_Plane]
  ExternalGeometry = -> [Sketch]
  FullyConstrained = true
  MakeInternals = false
  MapMode = 5
  Placement = pos=(0,0,0) rot=(1,0,0;1.5708rad)
  sketch-geometry (7):
    g0: LineSegment [constr] StartX=-160.034 StartY=-22.6997 StartZ=0 EndX=-164.854 EndY=-37.5361 EndZ=0
    g1: LineSegment [constr] StartX=-160.034 StartY=-22.6997 StartZ=0 EndX=-156.99 EndY=-23.6885 EndZ=0
    g2: LineSegment [constr] StartX=-160.034 StartY=-22.6997 StartZ=0 EndX=-163.648 EndY=-21.5254 EndZ=0
    g3: LineSegment StartX=-163.648 StartY=-21.5254 StartZ=0 EndX=-156.99 EndY=-23.6885 EndZ=0
    g4: LineSegment StartX=-163.648 StartY=-21.5254 StartZ=0 EndX=-168.468 EndY=-36.3619 EndZ=0
    g5: LineSegment StartX=-156.99 StartY=-23.6885 StartZ=0 EndX=-161.811 EndY=-38.525 EndZ=0
    g6: LineSegment StartX=-168.468 StartY=-36.3619 StartZ=0 EndX=-161.811 EndY=-38.525 EndZ=0
  constraints (19):
    c: Distance(g0,g-3) = 47
    c: Distance(g0) = 15.6
    c: Tangent(g0,g-3)
    c: Coincident(g1,g0)
    c: Coincident(g2,g0)
    c: Distance(g1) = 3.2
    c: Distance(g2) = 3.8
    c: Perpendicular(g0,g1)
    c: Perpendicular(g0,g2)
    c: Coincident(g3,g2)
    c: Coincident(g3,g1)
    c: Equal(g4,g0)
    c: Equal(g5,g0)
    c: Parallel(g4,g0)
    c: Parallel(g5,g0)
    c: Coincident(g4,g2)
    c: Coincident(g5,g1)
    c: Coincident(g6,g4)
    c: Coincident(g6,g5)
FEATURE [Part::Extrusion] Extrude077  label="Extrude077 - scavo_nuovo_driver"
  Base = -> Sketch137
  Dir = (0,-1,2e-16)
  DirMode = 2
  FaceMakerClass = Part::FaceMakerBullseye
  FaceMakerMode = 3
  LengthFwd = 20.8
  LengthRev = 0
  Solid = true
  Symmetric = true
FEATURE [Sketcher::SketchObject] Sketch138  label="scavo_nuovo_driver_alto"
  ArcFitTolerance = 1e-06
  AttachmentSupport = -> [XZ_Plane]
  ExternalGeometry = -> [Sketch]
  FullyConstrained = true
  MakeInternals = false
  MapMode = 5
  Placement = pos=(0,0,0) rot=(1,0,0;1.5708rad)
  sketch-geometry (7):
    g0: LineSegment [constr] StartX=-188.917 StartY=18.1185 StartZ=0 EndX=-187.75 EndY=4.97025 EndZ=0
    g1: LineSegment StartX=-187.75 StartY=4.97025 StartZ=0 EndX=-189.742 EndY=4.79337 EndZ=0
    g2: LineSegment StartX=-187.75 StartY=4.97025 StartZ=0 EndX=-182.769 EndY=5.41245 EndZ=0
    g3: LineSegment StartX=-190.909 StartY=17.9416 StartZ=0 EndX=-189.742 EndY=4.79337 EndZ=0
    g4: LineSegment StartX=-183.937 StartY=18.5607 StartZ=0 EndX=-182.769 EndY=5.41245 EndZ=0
    g5: LineSegment StartX=-190.909 StartY=17.9416 StartZ=0 EndX=-188.917 EndY=18.1185 EndZ=0
    g6: LineSegment StartX=-188.917 StartY=18.1185 StartZ=0 EndX=-183.937 EndY=18.5607 EndZ=0
  constraints (20):
    c: Distance(g0) = 13.2
    c: DistanceY(g-3,g0) = 9
    c: PointOnObject(g0,g-4)
    c: PointOnObject(g0,g-4)
    c: Coincident(g1,g0)
    c: Coincident(g2,g0)
    c: Distance(g1) = 2
    c: Distance(g2) = 5
    c: Perpendicular(g0,g1)
    c: Perpendicular(g0,g2)
    c: Equal(g3,g0)
    c: Parallel(g3,g0)
    c: Coincident(g3,g1)
    c: Equal(g4,g0)
    c: Parallel(g4,g0)
    c: Coincident(g4,g2)
    c: Coincident(g5,g3)
    c: Coincident(g5,g0)
    c: Coincident(g6,g0)
    c: Coincident(g6,g4)
FEATURE [Part::Extrusion] Extrude078  label="Extrude078 - scavo_nuovo_driver_alto"
  Base = -> Sketch138
  Dir = (0,-1,2e-16)
  DirMode = 2
  FaceMakerClass = Part::FaceMakerBullseye
  FaceMakerMode = 3
  LengthFwd = 17.2
  LengthRev = 0
  Solid = true
  Symmetric = true
FEATURE [Sketcher::SketchObject] Sketch139  label="fermi_nuovo_driver_alto"
  ArcFitTolerance = 1e-06
  AttachmentSupport = -> [XZ_Plane]
  ExternalGeometry = -> [Sketch138,Sketch]
  FullyConstrained = true
  MakeInternals = false
  MapMode = 5
  Placement = pos=(0,0,0) rot=(1,0,0;1.5708rad)
  sketch-geometry (17):
    g0: LineSegment [constr] StartX=-188.41 StartY=16.8018 StartZ=0 EndX=-187.948 EndY=14.1416 EndZ=0
    g1: LineSegment [constr] StartX=-187.948 StartY=14.1416 StartZ=0 EndX=-187.486 EndY=11.4815 EndZ=0
    g2: LineSegment StartX=-187.948 StartY=14.1416 StartZ=0 EndX=-187.76 EndY=13.0579 EndZ=0
    g3: LineSegment StartX=-187.948 StartY=14.1416 StartZ=0 EndX=-188.136 EndY=15.2254 EndZ=0
    g4: LineSegment StartX=-187.76 StartY=13.0579 StartZ=0 EndX=-185.592 EndY=13.4346 EndZ=0
    g5: LineSegment StartX=-188.136 StartY=15.2254 StartZ=0 EndX=-185.969 EndY=15.6021 EndZ=0
    g6: LineSegment StartX=-185.969 StartY=15.6021 StartZ=0 EndX=-185.592 EndY=13.4346 EndZ=0
    g7: LineSegment StartX=-187.486 StartY=11.4815 StartZ=0 EndX=-189.062 EndY=11.2075 EndZ=0
    g8: LineSegment StartX=-188.41 StartY=16.8018 StartZ=0 EndX=-189.987 EndY=16.5278 EndZ=0
    g9: LineSegment StartX=-189.987 StartY=16.5278 StartZ=0 EndX=-189.062 EndY=11.2075 EndZ=0
    g10: LineSegment StartX=-187.486 StartY=11.4815 StartZ=0 EndX=-185.318 EndY=11.8582 EndZ=0
    g11: LineSegment StartX=-188.41 StartY=16.8018 StartZ=0 EndX=-186.243 EndY=17.1785 EndZ=0
    g12: LineSegment StartX=-184.393 StartY=15.8761 StartZ=0 EndX=-184.016 EndY=13.7086 EndZ=0
    g13: ArcOfCircle CenterX=-185.969 CenterY=15.6021 CenterZ=0 NormalX=0 NormalY=0 NormalZ=1 AngleXU=0 Radius=1.6 StartAngle=0.172085 EndAngle=1.74288
    g14: GeomPoint [constr] X=-184.667 Y=17.4525 Z=0
    g15: ArcOfCircle CenterX=-185.592 CenterY=13.4346 CenterZ=0 NormalX=0 NormalY=0 NormalZ=1 AngleXU=0 Radius=1.6 StartAngle=4.88447 EndAngle=6.45527
    g16: GeomPoint [constr] X=-183.742 Y=12.1322 Z=0
  constraints (43):
    c: Tangent(g1,g0) = -1.5708
    c: Distance(g0) = 2.7
    c: Equal(g1,g0)
    c: Tangent(g1,g-5)
    c: Coincident(g2,g0)
    c: Coincident(g3,g0)
    c: Distance(g2) = 1.1
    c: Equal(g3,g2)
    c: PointOnObject(g3,g2)
    c: Coincident(g4,g2)
    c: Coincident(g5,g3)
    c: Distance(g4) = 2.2
    c: Equal(g4,g5)
    c: Perpendicular(g1,g4)
    c: Perpendicular(g0,g5)
    c: Coincident(g6,g5)
    c: Coincident(g6,g4)
    c: Coincident(g7,g1)
    c: Coincident(g8,g0)
    c: Distance(g7) = 1.6
    c: Equal(g7,g8)
    c: Perpendicular(g1,g7)
    c: Perpendicular(g8,g0)
    c: Coincident(g9,g8)
    c: Coincident(g9,g7)
    c: Coincident(g10,g1)
    c: Coincident(g11,g0)
    c: Distance(g10,g16) = 3.8
    c: Perpendicular(g1,g10)
    c: Perpendicular(g1,g11)
    c: DistanceY(g0,g-4) = 3.8
    c: PointOnObject(g14,g12)
    c: PointOnObject(g14,g11)
    c: Tangent(g12,g13) = 1.5708
    c: Tangent(g11,g13) = 1.5708
    c: PointOnObject(g16,g12)
    c: PointOnObject(g16,g10)
    c: Tangent(g12,g15) = 1.5708
    c: Tangent(g10,g15) = -1.5708
    c: Equal(g13,g15)
    c: Coincident(g13,g5)
    c: Parallel(g2,g0)
    c: PointOnObject(g0,g-5)
FEATURE [Part::Extrusion] Extrude079  label="Extrude079 - fermi_nuovo_driver_alto"
  Base = -> Sketch139
  Dir = (0,-1,2e-16)
  DirMode = 2
  FaceMakerClass = Part::FaceMakerBullseye
  FaceMakerMode = 3
  LengthFwd = 25.2
  LengthRev = 0
  Solid = true
  Symmetric = true
FEATURE [Sketcher::SketchObject] Sketch140  label="scavo_diodo_nuovo_driver_alto"
  ArcFitTolerance = 1e-06
  AttachmentSupport = -> [XZ_Plane]
  ExternalGeometry = -> [Sketch138]
  FullyConstrained = true
  MakeInternals = false
  MapMode = 5
  Placement = pos=(0,0,0) rot=(1,0,0;1.5708rad)
  sketch-geometry (4):
    g0: LineSegment StartX=-190.909 StartY=17.9416 StartZ=0 EndX=-189.742 EndY=4.79337 EndZ=0
    g1: LineSegment StartX=-193.898 StartY=17.6763 StartZ=0 EndX=-192.73 EndY=4.52805 EndZ=0
    g2: LineSegment StartX=-190.909 StartY=17.9416 StartZ=0 EndX=-193.898 EndY=17.6763 EndZ=0
    g3: LineSegment StartX=-192.73 StartY=4.52805 StartZ=0 EndX=-189.742 EndY=4.79337 EndZ=0
  constraints (11):
    c: Equal(g0,g-3)
    c: Parallel(g0,g-3)
    c: Equal(g1,g-3)
    c: Parallel(g1,g-3)
    c: Coincident(g2,g0)
    c: Distance(g2) = 3
    c: Perpendicular(g0,g2)
    c: Coincident(g1,g2)
    c: Coincident(g3,g1)
    c: Coincident(g3,g0)
    c: Coincident(g0,g-3)
FEATURE [Part::Extrusion] Extrude080  label="Extrude080 - scavo_diodo_nuovo_driver_alto"
  Base = -> Sketch140
  Dir = (0,-1,2e-16)
  DirMode = 2
  FaceMakerClass = Part::FaceMakerBullseye
  FaceMakerMode = 3
  LengthFwd = 4
  LengthRev = 0
  Placement = pos=(0,7.8,0) rot=(0,0,1;0rad)
  Solid = true
  Symmetric = false
FEATURE [Part::MultiFuse] Fusion001
  Refine = true
  Shapes = -> [Cut043,Extrude079]
FEATURE [Part::Cut] Cut044
  Base = -> Fusion001
  Refine = true
  Tool = -> Extrude078
FEATURE [Part::Cut] Cut045
  Base = -> Cut044
  Refine = true
  Tool = -> Extrude080
FEATURE [Sketcher::SketchObject] Sketch141  label="fermi_nuovo_driver"
  ArcFitTolerance = 1e-06
  AttachmentSupport = -> [XZ_Plane]
  ExternalGeometry = -> [Sketch,Sketch137]
  FullyConstrained = true
  MakeInternals = false
  MapMode = 5
  Placement = pos=(0,0,0) rot=(1,0,0;1.5708rad)
  sketch-geometry (17):
    g0: LineSegment [constr] StartX=-156.99 StartY=-23.6885 StartZ=0 EndX=-160.034 EndY=-22.6997 EndZ=0
    g1: LineSegment [constr] StartX=-160.034 StartY=-22.6997 StartZ=0 EndX=-162.815 EndY=-31.2592 EndZ=0
    g2: LineSegment [constr] StartX=-162.815 StartY=-31.2592 StartZ=0 EndX=-164.484 EndY=-36.3949 EndZ=0
    g3: LineSegment StartX=-164.484 StartY=-36.3949 StartZ=0 EndX=-166.576 EndY=-35.715 EndZ=0
    g4: LineSegment StartX=-167.603 StartY=-33.6989 StartZ=0 EndX=-166.923 EndY=-31.6066 EndZ=0
    g5: LineSegment StartX=-164.907 StartY=-30.5793 StartZ=0 EndX=-161.293 EndY=-31.7536 EndZ=0
    g6: LineSegment StartX=-161.293 StartY=-31.7536 StartZ=0 EndX=-162.962 EndY=-36.8893 EndZ=0
    g7: LineSegment StartX=-164.484 StartY=-36.3949 StartZ=0 EndX=-162.962 EndY=-36.8893 EndZ=0
    g8: LineSegment StartX=-165.402 StartY=-32.101 StartZ=0 EndX=-166.082 EndY=-34.1933 EndZ=0
    g9: LineSegment StartX=-166.082 StartY=-34.1933 StartZ=0 EndX=-163.989 EndY=-34.8732 EndZ=0
    g10: LineSegment StartX=-163.989 StartY=-34.8732 StartZ=0 EndX=-163.309 EndY=-32.7809 EndZ=0
    g11: LineSegment StartX=-163.309 StartY=-32.7809 StartZ=0 EndX=-165.402 EndY=-32.101 EndZ=0
    g12: ArcOfCircle CenterX=-165.402 CenterY=-32.101 CenterZ=0 NormalX=0 NormalY=0 NormalZ=1 AngleXU=0 Radius=1.6 StartAngle=1.25664 EndAngle=2.82743
    g13: GeomPoint [constr] X=-166.429 Y=-30.0849 Z=0
    g14: ArcOfCircle CenterX=-166.082 CenterY=-34.1933 CenterZ=0 NormalX=0 NormalY=0 NormalZ=1 AngleXU=0 Radius=1.6 StartAngle=2.82743 EndAngle=4.39823
    g15: GeomPoint [constr] X=-168.098 Y=-35.2206 Z=0
    g16: LineSegment [constr] StartX=-160.034 StartY=-22.6997 StartZ=0 EndX=-164.854 EndY=-37.5361 EndZ=0
  constraints (44):
    c: Coincident(g0,g-4)
    c: PointOnObject(g0,g-3)
    c: Parallel(g0,g-4)
    c: Coincident(g1,g0)
    c: Parallel(g1,g-3)
    c: Coincident(g2,g1)
    c: Distance(g2) = 5.4
    c: Coincident(g3,g2)
    c: Parallel(g2,g-3)
    c: Distance(g15,g13) = 5.4
    c: Perpendicular(g3,g2)
    c: Parallel(g4,g2)
    c: Distance(g5,g13) = 5.4
    c: Distance(g3,g15) = 3.8
    c: Perpendicular(g4,g5)
    c: Coincident(g6,g5)
    c: Distance(g6) = 5.4
    c: Parallel(g6,g4)
    c: Coincident(g7,g2)
    c: Coincident(g7,g6)
    c: Coincident(g8,g9)
    c: Coincident(g9,g10)
    c: Coincident(g10,g11)
    c: Coincident(g11,g8)
    c: Distance(g8,g10) = 2.2
    c: Distance(g9,g11) = 2.2
    c: Perpendicular(g11,g8)
    c: Equal(g8,g10)
    c: Equal(g11,g9)
    c: Tangent(g10,g2)
    c: Distance(g10,g1) = 1.6
    c: PointOnObject(g13,g4)
    c: PointOnObject(g13,g5)
    c: Tangent(g4,g12) = 1.5708
    c: Tangent(g5,g12) = 1.5708
    c: PointOnObject(g15,g4)
    c: Tangent(g4,g14) = 1.5708
    c: Tangent(g3,g14) = 1.5708
    c: Equal(g14,g12)
    c: Coincident(g12,g8)
    c: Coincident(g16,g0)
    c: PointOnObject(g16,g-5)
    c: Parallel(g16,g-3)
    c: Distance(g16,g2) = 1.2
FEATURE [Part::Extrusion] Extrude081  label="Extrude081 - fermi_nuovo_driver"
  Base = -> Sketch141
  Dir = (0,-1,2e-16)
  DirMode = 2
  FaceMakerClass = Part::FaceMakerBullseye
  FaceMakerMode = 3
  LengthFwd = 25.2
  LengthRev = 0
  Solid = true
  Symmetric = true
FEATURE [Part::MultiFuse] Fusion002
  Refine = true
  Shapes = -> [Cut045,Extrude081]
FEATURE [Part::Cut] Cut046
  Base = -> Fusion002
  Refine = true
  Tool = -> Extrude077
FEATURE [Sketcher::SketchObject] Sketch142  label="fermi_rele"
  ArcFitTolerance = 1e-06
  AttachmentSupport = -> [XZ_Plane]
  ExternalGeometry = -> [Sketch,Sketch136]
  FullyConstrained = true
  MakeInternals = false
  MapMode = 5
  Placement = pos=(0,0,0) rot=(1,0,0;1.5708rad)
  sketch-geometry (15):
    g0: LineSegment StartX=-176.936 StartY=-62.4208 StartZ=0 EndX=-177.615 EndY=-64.5131 EndZ=0
    g1: LineSegment StartX=-174.919 StartY=-61.3936 StartZ=0 EndX=-171.305 EndY=-62.5678 EndZ=0
    g2: LineSegment StartX=-171.305 StartY=-62.5678 StartZ=0 EndX=-172.974 EndY=-67.7035 EndZ=0
    g3: LineSegment StartX=-176.588 StartY=-66.5293 StartZ=0 EndX=-172.974 EndY=-67.7035 EndZ=0
    g4: LineSegment StartX=-175.414 StartY=-62.9152 StartZ=0 EndX=-173.322 EndY=-63.5951 EndZ=0
    g5: LineSegment StartX=-175.414 StartY=-62.9152 StartZ=0 EndX=-176.094 EndY=-65.0076 EndZ=0
    g6: LineSegment StartX=-173.322 StartY=-63.5951 StartZ=0 EndX=-174.001 EndY=-65.6874 EndZ=0
    g7: LineSegment StartX=-176.094 StartY=-65.0076 StartZ=0 EndX=-174.001 EndY=-65.6874 EndZ=0
    g8: LineSegment [constr] StartX=-173.322 StartY=-63.5951 StartZ=0 EndX=-172.827 EndY=-62.0734 EndZ=0
    g9: LineSegment [constr] StartX=-173.322 StartY=-63.5951 StartZ=0 EndX=-171.8 EndY=-64.0895 EndZ=0
    g10: LineSegment [constr] StartX=-170.364 StartY=-61.612 StartZ=0 EndX=-172.456 EndY=-60.9321 EndZ=0
    g11: ArcOfCircle CenterX=-175.414 CenterY=-62.9152 CenterZ=0 NormalX=0 NormalY=0 NormalZ=1 AngleXU=0 Radius=1.6 StartAngle=1.25664 EndAngle=2.82743
    g12: GeomPoint [constr] X=-176.441 Y=-60.8991 Z=0
    g13: ArcOfCircle CenterX=-176.094 CenterY=-65.0076 CenterZ=0 NormalX=0 NormalY=0 NormalZ=1 AngleXU=0 Radius=1.6 StartAngle=2.82743 EndAngle=4.39823
    g14: GeomPoint [constr] X=-178.11 Y=-66.0348 Z=0
  constraints (39):
    c: Distance(g14,g12) = 5.4
    c: Distance(g1,g12) = 5.4
    c: Perpendicular(g1,g0)
    c: Coincident(g2,g1)
    c: Parallel(g2,g0)
    c: Coincident(g3,g2)
    c: Parallel(g2,g-3)
    c: Coincident(g5,g4)
    c: Distance(g5) = 2.2
    c: Distance(g4) = 2.2
    c: Perpendicular(g4,g5)
    c: Coincident(g6,g4)
    c: Equal(g6,g5)
    c: Parallel(g6,g5)
    c: Coincident(g7,g5)
    c: Coincident(g7,g6)
    c: Coincident(g8,g4)
    c: Coincident(g9,g4)
    c: Distance(g8) = 1.6
    c: Distance(g9) = 1.6
    c: Parallel(g8,g6)
    c: Parallel(g9,g4)
    c: PointOnObject(g8,g1)
    c: PointOnObject(g9,g2)
    c: Coincident(g10,g-4)
    c: Parallel(g10,g-4)
    c: PointOnObject(g10,g-3)
    c: Tangent(g6,g-3) = 1.5708
    c: Distance(g4,g10) = 2.8
    c: PointOnObject(g12,g1)
    c: Tangent(g1,g11) = 1.5708
    c: Tangent(g0,g11) = -1.5708
    c: PointOnObject(g14,g3)
    c: PointOnObject(g14,g0)
    c: Tangent(g3,g13) = -1.5708
    c: Tangent(g0,g13) = -1.5708
    c: Equal(g11,g13)
    c: Coincident(g11,g4)
    c: Parallel(g3,g1)
FEATURE [Part::Extrusion] Extrude082  label="Extrude082 - fermi_rele"
  Base = -> Sketch142
  Dir = (0,-1,2e-16)
  DirMode = 2
  FaceMakerClass = Part::FaceMakerBullseye
  FaceMakerMode = 3
  LengthFwd = 25.2
  LengthRev = 0
  Solid = true
  Symmetric = true
FEATURE [Part::MultiFuse] Fusion003
  Refine = true
  Shapes = -> [Cut046,Extrude082]
FEATURE [Part::Cut] Cut047
  Base = -> Fusion003
  Refine = true
  Tool = -> Extrude076
FEATURE [Sketcher::SketchObject] Sketch143  label="foro_passaggio_cavi_led_batteria"
  ArcFitTolerance = 1e-06
  AttachmentSupport = -> [XZ_Plane]
  ExternalGeometry = -> [Sketch,Sketch042,Sketch036]
  FullyConstrained = true
  MakeInternals = false
  MapMode = 5
  Placement = pos=(0,0,0) rot=(1,0,0;1.5708rad)
  sketch-geometry (4):
    g0: LineSegment StartX=-207.775 StartY=-41.3701 StartZ=0 EndX=-213.607 EndY=-53.8767 EndZ=0
    g1: LineSegment StartX=-213.607 StartY=-53.8767 StartZ=0 EndX=-211.843 EndY=-59.5559 EndZ=0
    g2: LineSegment StartX=-207.775 StartY=-41.3701 StartZ=0 EndX=-207.775 EndY=-50.8316 EndZ=0
    g3: LineSegment StartX=-207.775 StartY=-50.8316 StartZ=0 EndX=-211.843 EndY=-59.5559 EndZ=0
  constraints (9):
    c: Coincident(g0,g-3)
    c: PointOnObject(g1,g-6)
    c: Coincident(g1,g0)
    c: Coincident(g2,g0)
    c: Coincident(g2,g-7)
    c: Coincident(g3,g2)
    c: Parallel(g3,g0)
    c: Coincident(g3,g1)
    c: Coincident(g0,g-5)
FEATURE [Part::Extrusion] Extrude083  label="Extrude083 - foro_passaggio_cavi_led_batteria"
  Base = -> Sketch143
  Dir = (0,-1,2e-16)
  DirMode = 2
  FaceMakerClass = Part::FaceMakerBullseye
  FaceMakerMode = 3
  LengthFwd = 6
  LengthRev = 0
  Solid = true
  Symmetric = true
FEATURE [Part::Cut] Cut048
  Base = -> Cut047
  Refine = true
  Tool = -> Extrude083
FEATURE [Sketcher::SketchObject] Sketch144  label="foro_areazione_alimentatore"
  ArcFitTolerance = 1e-06
  AttachmentSupport = -> [XZ_Plane]
  ExternalGeometry = -> [Sketch036]
  FullyConstrained = true
  MakeInternals = false
  MapMode = 5
  Placement = pos=(0,0,0) rot=(1,0,0;1.5708rad)
  sketch-geometry (4):
    g0: LineSegment StartX=-211.843 StartY=-60.3701 StartZ=0 EndX=-207.775 EndY=-60.3701 EndZ=0
    g1: LineSegment StartX=-207.775 StartY=-60.3701 StartZ=0 EndX=-207.775 EndY=-70.3701 EndZ=0
    g2: LineSegment StartX=-211.843 StartY=-60.3701 StartZ=0 EndX=-211.843 EndY=-70.3701 EndZ=0
    g3: LineSegment StartX=-207.775 StartY=-70.3701 StartZ=0 EndX=-211.843 EndY=-70.3701 EndZ=0
  constraints (11):
    c: Horizontal(g0)
    c: Distance(g1) = 10
    c: Coincident(g1,g0)
    c: Tangent(g1,g-3)
    c: PointOnObject(g0,g-4)
    c: Coincident(g2,g0)
    c: PointOnObject(g2,g-4)
    c: Coincident(g3,g1)
    c: Horizontal(g3)
    c: Coincident(g3,g2)
    c: DistanceY(g0,g-3) = 19
FEATURE [Part::Extrusion] Extrude084  label="Extrude084 - foro_areazione_alimentatore"
  Base = -> Sketch144
  Dir = (0,-1,2e-16)
  DirMode = 2
  FaceMakerClass = Part::FaceMakerBullseye
  FaceMakerMode = 3
  LengthFwd = 10
  LengthRev = 0
  Solid = true
  Symmetric = true
FEATURE [Part::Cut] Cut049
  Base = -> Cut048
  Refine = true
  Tool = -> Extrude084
FEATURE [Sketcher::SketchObject] Sketch145  label="foro_per_condesatore"
  ArcFitTolerance = 1e-06
  AttachmentSupport = -> [XZ_Plane]
  ExternalGeometry = -> [Sketch138]
  FullyConstrained = true
  MakeInternals = false
  MapMode = 5
  Placement = pos=(0,0,0) rot=(1,0,0;1.5708rad)
  sketch-geometry (1):
    g0: Circle CenterX=-179.742 CenterY=9.59337 CenterZ=0 NormalX=0 NormalY=0 NormalZ=1 AngleXU=0 Radius=5.4
  constraints (3):
    c: Diameter(g0) = 10.8
    c: DistanceX(g-3,g0) = 10
    c: DistanceY(g-3,g0) = 4.8
FEATURE [Part::Extrusion] Extrude085  label="Extrude085 - foro_per_condesatore"
  Base = -> Sketch145
  Dir = (0,-1,2e-16)
  DirMode = 2
  FaceMakerClass = Part::FaceMakerBullseye
  FaceMakerMode = 3
  LengthFwd = 25.2
  LengthRev = 0
  Solid = true
  Symmetric = true
FEATURE [Part::Cut] Cut050
  Base = -> Cut049
  Refine = true
  Tool = -> Extrude085
FEATURE [Sketcher::SketchObject] Sketch146  label="scavo_pulsante_6x6_per_led_batteria"
  ArcFitTolerance = 1e-06
  AttachmentSupport = -> [XZ_Plane]
  ExternalGeometry = -> [Sketch016]
  FullyConstrained = true
  MakeInternals = false
  MapMode = 5
  Placement = pos=(0,0,0) rot=(1,0,0;1.5708rad)
  sketch-geometry (5):
    g0: LineSegment StartX=-216.643 StartY=-65.8316 StartZ=0 EndX=-216.643 EndY=-72.8316 EndZ=0
    g1: LineSegment StartX=-216.643 StartY=-72.8316 StartZ=0 EndX=-210.243 EndY=-72.8316 EndZ=0
    g2: LineSegment StartX=-210.243 StartY=-72.8316 StartZ=0 EndX=-210.243 EndY=-65.8316 EndZ=0
    g3: LineSegment StartX=-210.243 StartY=-65.8316 StartZ=0 EndX=-216.643 EndY=-65.8316 EndZ=0
    g4: GeomPoint [constr] X=-213.443 Y=-69.3316 Z=0
  constraints (13):
    c: Coincident(g0,g1)
    c: Coincident(g1,g2)
    c: Coincident(g2,g3)
    c: Coincident(g3,g0)
    c: Vertical(g0)
    c: Vertical(g2)
    c: Horizontal(g1)
    c: Horizontal(g3)
    c: Distance(g0,g2) = 6.4
    c: Distance(g1,g3) = 7
    c: Tangent(g1,g-3)
    c: Symmetric(g0,g2,g4)
    c: Vertical(g-3,g4)
FEATURE [Part::Extrusion] Extrude086  label="Extrude086 - scavo_pulsante_6x6_per_led_batteria"
  Base = -> Sketch146
  Dir = (0,-1,2e-16)
  DirMode = 2
  FaceMakerClass = Part::FaceMakerBullseye
  FaceMakerMode = 3
  LengthFwd = 4
  LengthRev = 0
  Placement = pos=(0,12.6,0) rot=(0,0,1;0rad)
  Solid = true
  Symmetric = false
FEATURE [Sketcher::SketchObject] Sketch147  label="scavo_led_stato_batteria"
  ArcFitTolerance = 1e-06
  AttachmentSupport = -> [XZ_Plane]
  ExternalGeometry = -> [Sketch016]
  FullyConstrained = true
  MakeInternals = false
  MapMode = 5
  Placement = pos=(0,0,0) rot=(1,0,0;1.5708rad)
  sketch-geometry (5):
    g0: LineSegment StartX=-215.843 StartY=-56.2316 StartZ=0 EndX=-215.843 EndY=-65.4316 EndZ=0
    g1: LineSegment StartX=-215.843 StartY=-65.4316 StartZ=0 EndX=-211.043 EndY=-65.4316 EndZ=0
    g2: LineSegment StartX=-211.043 StartY=-65.4316 StartZ=0 EndX=-211.043 EndY=-56.2316 EndZ=0
    g3: LineSegment StartX=-211.043 StartY=-56.2316 StartZ=0 EndX=-215.843 EndY=-56.2316 EndZ=0
    g4: GeomPoint [constr] X=-213.443 Y=-60.8316 Z=0
  constraints (13):
    c: Coincident(g0,g1)
    c: Coincident(g1,g2)
    c: Coincident(g2,g3)
    c: Coincident(g3,g0)
    c: Distance(g0,g2) = 4.8
    c: Distance(g1,g3) = 9.2
    c: Equal(g0,g2)
    c: Equal(g1,g3)
    c: Perpendicular(g3,g0)
    c: DistanceY(g-3,g0) = 11.4
    c: Vertical(g2)
    c: Symmetric(g0,g2,g4)
    c: Vertical(g4,g-3)
FEATURE [Part::Extrusion] Extrude087  label="Extrude087 - scavo_led_stato_batteria"
  Base = -> Sketch147
  Dir = (0,-1,2e-16)
  DirMode = 2
  FaceMakerClass = Part::FaceMakerBullseye
  FaceMakerMode = 3
  LengthFwd = 2.2
  LengthRev = 0
  Placement = pos=(0,12.6,0) rot=(0,0,1;0rad)
  Solid = true
  Symmetric = false
FEATURE [Sketcher::SketchObject] Sketch148
  ArcFitTolerance = 1e-06
  AttachmentSupport = -> [Pad016]
  ExternalGeometry = -> [Pad016]
  FullyConstrained = true
  MakeInternals = false
  MapMode = 5
  Placement = pos=(0,0,-80.4316) rot=(1,0,0;3.14159rad)
  sketch-geometry (8):
    g0: LineSegment StartX=-176.685 StartY=3.6 StartZ=0 EndX=-186.685 EndY=3.6 EndZ=0
    g1: LineSegment StartX=-176.685 StartY=3.6 StartZ=0 EndX=-176.685 EndY=-9e-16 EndZ=0
    g2: LineSegment [constr] StartX=-186.685 StartY=3.6 StartZ=0 EndX=-186.685 EndY=-9e-16 EndZ=0
    g3: ArcOfEllipse CenterX=-186.685 CenterY=-9e-16 CenterZ=0 NormalX=0 NormalY=0 NormalZ=1 MajorRadius=10 MinorRadius=3.6 AngleXU=0 StartAngle=0 EndAngle=1.5708
    g4: LineSegment [constr] StartX=-176.685 StartY=-1e-15 StartZ=0 EndX=-196.685 EndY=-1e-15 EndZ=0
    g5: LineSegment [constr] StartX=-186.685 StartY=3.6 StartZ=0 EndX=-186.685 EndY=-3.6 EndZ=0
    g6: GeomPoint [constr] X=-177.356 Y=-1e-15 Z=0
    g7: GeomPoint [constr] X=-196.015 Y=-1e-15 Z=0
  constraints (13):
    c: Distance(g0) = 10
    c: Coincident(g0,g-5)
    c: PointOnObject(g0,g-3)
    c: Coincident(g1,g0)
    c: Coincident(g1,g-5)
    c: Coincident(g2,g0)
    c: Vertical(g2)
    c: PointOnObject(g2,g-4)
    c: InternalAlignment(g4-g7 -> g3) x4
    c: Coincident(g3,g2)
    c: Coincident(g3,g0)
    c: Coincident(g3,g1)
    c: Horizontal(g4)
FEATURE [PartDesign::SubtractivePipe] SubtractivePipe004
  AuxilleryCurvelinear = true
  AuxillerySpineTangent = false
  BaseFeature = -> Pad016
  Binormal = (0,0,0)
  Mode = 0
  Profile = -> Sketch148
  Refine = true
  Spine = -> Pad016 [Edge253]
  SpineTangent = false
  Suppressed = false
  Transformation = 0
  Transition = 0
FEATURE [Sketcher::SketchObject] Sketch149
  ArcFitTolerance = 1e-06
  AttachmentSupport = -> [Pad016]
  ExternalGeometry = -> [Pad016]
  FullyConstrained = true
  MakeInternals = false
  MapMode = 5
  Placement = pos=(0,0,-80.4316) rot=(1,0,0;3.14159rad)
  sketch-geometry (8):
    g0: LineSegment StartX=-215.932 StartY=3.6 StartZ=0 EndX=-205.932 EndY=3.6 EndZ=0
    g1: LineSegment StartX=-215.932 StartY=3.6 StartZ=0 EndX=-215.932 EndY=-4e-16 EndZ=0
    g2: LineSegment [constr] StartX=-205.932 StartY=3.6 StartZ=0 EndX=-205.932 EndY=-9e-16 EndZ=0
    g3: ArcOfEllipse CenterX=-205.932 CenterY=-1e-15 CenterZ=0 NormalX=0 NormalY=0 NormalZ=1 MajorRadius=10 MinorRadius=3.6 AngleXU=-3.14159 StartAngle=4.71239 EndAngle=6.28319
    g4: LineSegment [constr] StartX=-215.932 StartY=-1e-15 StartZ=0 EndX=-195.932 EndY=-1e-15 EndZ=0
    g5: LineSegment [constr] StartX=-205.932 StartY=-3.6 StartZ=0 EndX=-205.932 EndY=3.6 EndZ=0
    g6: GeomPoint [constr] X=-215.262 Y=-2.1e-15 Z=0
    g7: GeomPoint [constr] X=-196.602 Y=-9e-16 Z=0
  constraints (13):
    c: Distance(g0) = 10
    c: Coincident(g0,g-5)
    c: PointOnObject(g0,g-5)
    c: Coincident(g1,g0)
    c: Coincident(g1,g-4)
    c: Coincident(g2,g0)
    c: Vertical(g2)
    c: PointOnObject(g2,g-3)
    c: InternalAlignment(g4-g7 -> g3) x4
    c: Coincident(g3,g2)
    c: Coincident(g3,g0)
    c: Coincident(g3,g1)
    c: Horizontal(g4)
FEATURE [PartDesign::SubtractivePipe] SubtractivePipe005
  AuxilleryCurvelinear = true
  AuxillerySpineTangent = false
  BaseFeature = -> SubtractivePipe004
  Binormal = (0,0,0)
  Mode = 0
  Profile = -> Sketch149
  Refine = true
  Spine = -> Pad016 [Edge251,Edge256,Edge255]
  SpineTangent = false
  Suppressed = false
  Transformation = 0
  Transition = 0
FEATURE [PartDesign::SubtractiveLoft] SubtractiveLoft002
  BaseFeature = -> SubtractivePipe005
  Closed = false
  Profile = -> Sketch129
  Refine = true
  Ruled = false
  Sections = -> [Sketch130]
  Suppressed = false
FEATURE [PartDesign::SubtractiveLoft] SubtractiveLoft003
  BaseFeature = -> SubtractiveLoft002
  Closed = false
  Profile = -> Clone2D001
  Refine = true
  Ruled = false
  Sections = -> [Sketch131]
  Suppressed = false
FEATURE [PartDesign::Chamfer] Chamfer010
  Angle = 45
  Base = -> SubtractiveLoft003 [Edge203,Edge204,Edge202,Edge201,Edge195]
  BaseFeature = -> SubtractiveLoft003
  ChamferType = 0
  FlipDirection = false
  Refine = true
  Size = 1.5
  Size2 = 1
  SupportTransform = false
  Suppressed = false
  UseAllEdges = false
FEATURE [PartDesign::Chamfer] Chamfer011
  Angle = 45
  Base = -> Chamfer010 [Edge15]
  BaseFeature = -> Chamfer010
  ChamferType = 0
  FlipDirection = false
  Refine = true
  Size = 1.6
  Size2 = 1
  SupportTransform = false
  Suppressed = false
  UseAllEdges = false
FEATURE [PartDesign::Chamfer] Chamfer012
  Angle = 45
  Base = -> Chamfer011 [Edge10]
  BaseFeature = -> Chamfer011
  ChamferType = 0
  FlipDirection = false
  Refine = true
  Size = 3.5
  Size2 = 1
  SupportTransform = false
  Suppressed = false
  UseAllEdges = false
FEATURE [PartDesign::Chamfer] Chamfer013
  Angle = 45
  Base = -> Chamfer012 [Edge94]
  BaseFeature = -> Chamfer012
  ChamferType = 0
  FlipDirection = false
  Refine = true
  Size = 1.9
  Size2 = 1
  SupportTransform = false
  Suppressed = false
  UseAllEdges = false
FEATURE [PartDesign::Fillet] Fillet007
  Base = -> Chamfer013 [Edge83]
  BaseFeature = -> Chamfer013
  Radius = 1.1
  Refine = true
  SupportTransform = false
  Suppressed = false
  UseAllEdges = false
FEATURE [PartDesign::Fillet] Fillet008
  Base = -> Fillet007 [Edge75]
  BaseFeature = -> Fillet007
  Radius = 1.9
  Refine = true
  SupportTransform = false
  Suppressed = false
  UseAllEdges = false
FEATURE [PartDesign::Pocket] Pocket011
  BaseFeature = -> Fillet008
  Direction = (0,1,-2e-16)
  Length = 0.8
  Length2 = 5
  Profile = -> Sketch132
  ReferenceAxis = -> Sketch132 [N_Axis]
  Refine = true
  Suppressed = false
  Type = 0
FEATURE [PartDesign::Pocket] Pocket012
  BaseFeature = -> Pocket011
  Direction = (0,1,0)
  Length = 1
  Length2 = 5
  Profile = -> ShapeString
  ReferenceAxis = -> ShapeString [N_Axis]
  Refine = true
  Suppressed = false
  Type = 0
FEATURE [Sketcher::SketchObject] Sketch150
  ArcFitTolerance = 1e-06
  AttachmentSupport = -> [Pad008]
  ExternalGeometry = -> [Pad008]
  FullyConstrained = true
  MakeInternals = false
  MapMode = 5
  Placement = pos=(0,3.6,0) rot=(0,0.707107,0.707107;3.14159rad)
  sketch-geometry (7):
    g0: LineSegment [constr] StartX=210.343 StartY=-66.0316 StartZ=0 EndX=210.343 EndY=-72.8316 EndZ=0
    g1: LineSegment [constr] StartX=210.343 StartY=-72.8316 StartZ=0 EndX=216.543 EndY=-72.8316 EndZ=0
    g2: LineSegment [constr] StartX=216.543 StartY=-72.8316 StartZ=0 EndX=216.543 EndY=-66.0316 EndZ=0
    g3: LineSegment [constr] StartX=216.543 StartY=-66.0316 StartZ=0 EndX=210.343 EndY=-66.0316 EndZ=0
    g4: LineSegment [constr] StartX=210.343 StartY=-72.8316 StartZ=0 EndX=216.543 EndY=-66.0316 EndZ=0
    g5: LineSegment [constr] StartX=210.343 StartY=-66.0316 StartZ=0 EndX=213.443 EndY=-69.4316 EndZ=0
    g6: Circle CenterX=213.443 CenterY=-69.4316 CenterZ=0 NormalX=0 NormalY=0 NormalZ=1 AngleXU=0 Radius=2
  constraints (18):
    c: Coincident(g0,g1)
    c: Coincident(g1,g2)
    c: Coincident(g2,g3)
    c: Coincident(g3,g0)
    c: Vertical(g0)
    c: Vertical(g2)
    c: Horizontal(g1)
    c: Horizontal(g3)
    c: Distance(g0,g2) = 6.2
    c: Distance(g1,g3) = 6.8
    c: DistanceY(g-3,g1) = 4
    c: Coincident(g4,g0)
    c: Coincident(g4,g2)
    c: Coincident(g5,g0)
    c: Symmetric(g0,g2,g5)
    c: Diameter(g6) = 4
    c: Coincident(g6,g5)
    c: Vertical(g5,g-3)
FEATURE [Sketcher::SketchObject] Sketch151
  ArcFitTolerance = 1e-06
  AttachmentSupport = -> [Pad008]
  ExternalGeometry = -> [Pad008]
  FullyConstrained = true
  MakeInternals = false
  MapMode = 5
  Placement = pos=(0,3.6,0) rot=(0,0.707107,0.707107;3.14159rad)
  sketch-geometry (10):
    g0: LineSegment [constr] StartX=211.143 StartY=-56.2316 StartZ=0 EndX=211.143 EndY=-65.4316 EndZ=0
    g1: LineSegment [constr] StartX=211.143 StartY=-65.4316 StartZ=0 EndX=215.743 EndY=-65.4316 EndZ=0
    g2: LineSegment [constr] StartX=215.743 StartY=-65.4316 StartZ=0 EndX=215.743 EndY=-56.2316 EndZ=0
    g3: LineSegment [constr] StartX=215.743 StartY=-56.2316 StartZ=0 EndX=211.143 EndY=-56.2316 EndZ=0
    g4: LineSegment StartX=212.243 StartY=-63.8316 StartZ=0 EndX=214.643 EndY=-63.8316 EndZ=0
    g5: LineSegment StartX=214.643 StartY=-63.8316 StartZ=0 EndX=214.643 EndY=-57.0316 EndZ=0
    g6: LineSegment StartX=214.643 StartY=-57.0316 StartZ=0 EndX=212.243 EndY=-57.0316 EndZ=0
    g7: LineSegment StartX=212.243 StartY=-57.0316 StartZ=0 EndX=212.243 EndY=-63.8316 EndZ=0
    g8: GeomPoint [constr] X=213.443 Y=-60.4316 Z=0
    g9: GeomPoint [constr] X=213.443 Y=-60.8316 Z=0
  constraints (26):
    c: Coincident(g0,g1)
    c: Coincident(g1,g2)
    c: Coincident(g2,g3)
    c: Coincident(g3,g0)
    c: Vertical(g0)
    c: Vertical(g2)
    c: Horizontal(g1)
    c: Horizontal(g3)
    c: Distance(g0,g2) = 4.6
    c: Distance(g1,g3) = 9.2
    c: DistanceY(g-3,g1) = 11.4
    c: Coincident(g4,g5)
    c: Coincident(g5,g6)
    c: Coincident(g6,g7)
    c: Coincident(g7,g4)
    c: Horizontal(g4)
    c: Horizontal(g6)
    c: Vertical(g5)
    c: Vertical(g7)
    c: Symmetric(g6,g4,g8)
    c: Distance(g5,g7) = 2.4
    c: Distance(g4,g6) = 6.8
    c: Symmetric(g2,g0,g9)
    c: Vertical(g8,g9)
    c: DistanceY(g1,g4) = 1.6
    c: Vertical(g9,g-3)
FEATURE [PartDesign::Pocket] Pocket019
  BaseFeature = -> Pocket013
  Direction = (0,-1,2e-16)
  Length = 3.6
  Length2 = 5
  Profile = -> Sketch151
  ReferenceAxis = -> Sketch151 [N_Axis]
  Refine = true
  Suppressed = false
  Type = 0
FEATURE [PartDesign::Pocket] Pocket018
  BaseFeature = -> Pocket019
  Direction = (0,-1,2e-16)
  Length = 3.6
  Length2 = 5
  Profile = -> Sketch150
  ReferenceAxis = -> Sketch150 [N_Axis]
  Refine = true
  Suppressed = false
  Type = 0
FEATURE [PartDesign::Point] DatumPoint
  AttacherType = Attacher::AttachEnginePoint
  AttachmentSupport = -> [Sketch150]
  MapMode = 36
  Placement = pos=(-213.443,3.6,-69.4316) rot=(0,1,0;3.14159rad)
FEATURE [PartDesign::Plane] DatumPlane002
  AttachmentSupport = -> [DatumPoint]
  Length = 260.281
  MapMode = 1
  Placement = pos=(-213.443,3.6,-69.4316) rot=(0,0,1;0rad)
  ResizeMode = 0
  Width = 71.8377
FEATURE [Sketcher::SketchObject] Sketch152
  ArcFitTolerance = 1e-06
  AttachmentSupport = -> [DatumPlane002]
  ExternalGeometry = -> [Sketch150]
  FullyConstrained = true
  MakeInternals = false
  MapMode = 5
  Placement = pos=(-213.443,3.6,-69.4316) rot=(0,0,1;0rad)
  sketch-geometry (7):
    g0: LineSegment StartX=0 StartY=0 StartZ=0 EndX=-4 EndY=5.1e-15 EndZ=0
    g1: ArcOfEllipse CenterX=0 CenterY=0 CenterZ=0 NormalX=0 NormalY=0 NormalZ=1 MajorRadius=4 MinorRadius=3.6 AngleXU=3.14159 StartAngle=2e-16 EndAngle=1.5708
    g2: LineSegment [constr] StartX=-4 StartY=9e-16 StartZ=0 EndX=4 EndY=-9e-16 EndZ=0
    g3: LineSegment [constr] StartX=0 StartY=-3.6 StartZ=0 EndX=0 EndY=3.6 EndZ=0
    g4: GeomPoint [constr] X=-1.74356 Y=2.5e-15 Z=0
    g5: GeomPoint [constr] X=1.74356 Y=-2e-15 Z=0
    g6: LineSegment StartX=0 StartY=0 StartZ=0 EndX=-5.5e-15 EndY=-3.6 EndZ=0
  constraints (11):
    c: PointOnObject(g1,g-2)
    c: Distance(g0) = 4
    c: PointOnObject(g0,g-1)
    c: InternalAlignment(g2-g5 -> g1) x4
    c: Coincident(g1,g0)
    c: Vertical(g3)
    c: Coincident(g1,g-1)
    c: Distance(g6) = 3.6
    c: Coincident(g6,g1)
    c: Coincident(g1,g6)
    c: Coincident(g0,g1)
FEATURE [PartDesign::Groove] Groove
  Angle = 360
  Angle2 = 60
  Axis = (0,1,0)
  Base = (-213.443,3.6,-69.4316)
  BaseFeature = -> Pocket018
  Profile = -> Sketch152
  ReferenceAxis = -> Sketch152 [V_Axis]
  Refine = true
  Reversed = true
  Suppressed = false
  Type = 0
FEATURE [PartDesign::Body] Body006  label="lato SX"
  AllowCompound = false
  Group = -> [Binder,Pad019,Chamfer015,Pocket002,Sketch133,Sketch091,Pad005,Sketch092,Pocket001,Sketch093,Sketch094,Pad006,Sketch095,Pad007,Sketch096,Pad008,Sketch097,Pad009,Chamfer005,Pocket004,Sketch098,Pad010,Chamfer006,Pocket003,SubtractivePipe,SubtractivePipe001,Sketch099,Sketch106,Sketch107,Sketch108,Clone2D,Sketch109,SubtractiveLoft,SubtractiveLoft001,Sketch110,Sketch111,Sketch112,Chamfer016,Chamfer017,+15 more]
  Origin = -> Origin006
  Tip = -> Groove
FEATURE [Sketcher::SketchObject] Sketch153  label="ripieno_per_sostegno_led_batteria"
  ArcFitTolerance = 1e-06
  AttachmentSupport = -> [XZ_Plane]
  ExternalGeometry = -> [Sketch036]
  FullyConstrained = true
  MakeInternals = false
  MapMode = 5
  Placement = pos=(0,0,0) rot=(1,0,0;1.5708rad)
  sketch-geometry (4):
    g0: LineSegment StartX=-217.343 StartY=-54.5944 StartZ=0 EndX=-217.343 EndY=-63.1944 EndZ=0
    g1: LineSegment StartX=-217.343 StartY=-63.1944 StartZ=0 EndX=-211.843 EndY=-63.1944 EndZ=0
    g2: LineSegment StartX=-211.843 StartY=-63.1944 StartZ=0 EndX=-211.843 EndY=-54.5944 EndZ=0
    g3: LineSegment StartX=-211.843 StartY=-54.5944 StartZ=0 EndX=-217.343 EndY=-54.5944 EndZ=0
  constraints (11):
    c: Coincident(g0,g1)
    c: Coincident(g1,g2)
    c: Coincident(g2,g3)
    c: Coincident(g3,g0)
    c: Vertical(g0)
    c: Horizontal(g1)
    c: Horizontal(g3)
    c: Tangent(g2,g-3)
    c: DistanceY(g2,g-3) = 4.5
    c: DistanceX(g3,g3) = 5.5
    c: DistanceY(g0,g0) = 8.6
FEATURE [Part::Extrusion] Extrude088  label="Extrude088 - ripieno_per_sostegno_led_batteria"
  Base = -> Sketch153
  Dir = (0,-1,2e-16)
  DirMode = 2
  FaceMakerClass = Part::FaceMakerBullseye
  FaceMakerMode = 3
  LengthFwd = 4
  LengthRev = 0
  Placement = pos=(0,12.6,0) rot=(0,0,1;0rad)
  Solid = true
  Symmetric = false
FEATURE [Part::MultiFuse] Fusion004
  Refine = true
  Shapes = -> [Cut050,Extrude088]
FEATURE [Part::Cut] Cut051
  Base = -> Fusion004
  Refine = true
  Tool = -> Extrude087
FEATURE [Part::Cut] Cut052
  Base = -> Cut051
  Refine = true
  Tool = -> Extrude086
FEATURE [Sketcher::SketchObject] Sketch154
  ArcFitTolerance = 1e-06
  AttachmentSupport = -> [Pad016]
  ExternalGeometry = -> [Binder001]
  FullyConstrained = true
  MakeInternals = false
  MapMode = 5
  Placement = pos=(0,-3.6,0) rot=(1,0,0;1.5708rad)
  sketch-geometry (25):
    g0: LineSegment StartX=-214.643 StartY=-72.4316 StartZ=0 EndX=-212.243 EndY=-72.4316 EndZ=0
    g1: LineSegment StartX=-212.243 StartY=-72.4316 StartZ=0 EndX=-212.243 EndY=-71.2316 EndZ=0
    g2: LineSegment StartX=-212.243 StartY=-71.2316 StartZ=0 EndX=-214.643 EndY=-71.2316 EndZ=0
    g3: LineSegment StartX=-214.643 StartY=-71.2316 StartZ=0 EndX=-214.643 EndY=-72.4316 EndZ=0
    g4: GeomPoint [constr] X=-213.443 Y=-71.8316 Z=0
    g5: LineSegment StartX=-214.643 StartY=-69.6316 StartZ=0 EndX=-212.243 EndY=-69.6316 EndZ=0
    g6: LineSegment StartX=-212.243 StartY=-69.6316 StartZ=0 EndX=-212.243 EndY=-68.4316 EndZ=0
    g7: LineSegment StartX=-212.243 StartY=-68.4316 StartZ=0 EndX=-214.643 EndY=-68.4316 EndZ=0
    g8: LineSegment StartX=-214.643 StartY=-68.4316 StartZ=0 EndX=-214.643 EndY=-69.6316 EndZ=0
    g9: GeomPoint [constr] X=-213.443 Y=-69.0316 Z=0
    g10: LineSegment StartX=-214.643 StartY=-66.8316 StartZ=0 EndX=-212.243 EndY=-66.8316 EndZ=0
    g11: LineSegment StartX=-212.243 StartY=-66.8316 StartZ=0 EndX=-212.243 EndY=-65.6316 EndZ=0
    g12: LineSegment StartX=-212.243 StartY=-65.6316 StartZ=0 EndX=-214.643 EndY=-65.6316 EndZ=0
    g13: LineSegment StartX=-214.643 StartY=-65.6316 StartZ=0 EndX=-214.643 EndY=-66.8316 EndZ=0
    g14: GeomPoint [constr] X=-213.443 Y=-66.2316 Z=0
    g15: LineSegment StartX=-214.643 StartY=-64.0316 StartZ=0 EndX=-212.243 EndY=-64.0316 EndZ=0
    g16: LineSegment StartX=-212.243 StartY=-64.0316 StartZ=0 EndX=-212.243 EndY=-62.8316 EndZ=0
    g17: LineSegment StartX=-212.243 StartY=-62.8316 StartZ=0 EndX=-214.643 EndY=-62.8316 EndZ=0
    g18: LineSegment StartX=-214.643 StartY=-62.8316 StartZ=0 EndX=-214.643 EndY=-64.0316 EndZ=0
    g19: GeomPoint [constr] X=-213.443 Y=-63.4316 Z=0
    g20: LineSegment StartX=-214.643 StartY=-61.2316 StartZ=0 EndX=-212.243 EndY=-61.2316 EndZ=0
    g21: LineSegment StartX=-212.243 StartY=-61.2316 StartZ=0 EndX=-212.243 EndY=-60.0316 EndZ=0
    g22: LineSegment StartX=-212.243 StartY=-60.0316 StartZ=0 EndX=-214.643 EndY=-60.0316 EndZ=0
    g23: LineSegment StartX=-214.643 StartY=-60.0316 StartZ=0 EndX=-214.643 EndY=-61.2316 EndZ=0
    g24: GeomPoint [constr] X=-213.443 Y=-60.6316 Z=0
  constraints (65):
    c: Coincident(g0,g1)
    c: Coincident(g1,g2)
    c: Coincident(g2,g3)
    c: Coincident(g3,g0)
    c: Horizontal(g0)
    c: Horizontal(g2)
    c: Vertical(g1)
    c: Vertical(g3)
    c: Symmetric(g2,g0,g4)
    c: Distance(g1,g3) = 2.4
    c: Distance(g0,g2) = 1.2
    c: Coincident(g5,g6)
    c: Coincident(g6,g7)
    c: Coincident(g7,g8)
    c: Coincident(g8,g5)
    c: Horizontal(g5)
    c: Horizontal(g7)
    c: Vertical(g6)
    c: Vertical(g8)
    c: Symmetric(g7,g5,g9)
    c: Distance(g6,g8) = 2.4
    c: Distance(g5,g7) = 1.2
    c: Coincident(g10,g11)
    c: Coincident(g11,g12)
    c: Coincident(g12,g13)
    c: Coincident(g13,g10)
    c: Horizontal(g10)
    c: Horizontal(g12)
    c: Vertical(g11)
    c: Vertical(g13)
    c: Symmetric(g12,g10,g14)
    c: Distance(g11,g13) = 2.4
    c: Distance(g10,g12) = 1.2
    c: Coincident(g15,g16)
    c: Coincident(g16,g17)
    c: Coincident(g17,g18)
    c: Coincident(g18,g15)
    c: Horizontal(g15)
    c: Horizontal(g17)
    c: Vertical(g16)
    c: Vertical(g18)
    c: Symmetric(g17,g15,g19)
    c: Distance(g16,g18) = 2.4
    c: Distance(g15,g17) = 1.2
    c: Vertical(g4,g-3)
    c: Vertical(g9,g-3)
    c: Vertical(g14,g-3)
    c: Vertical(g19,g-3)
    c: DistanceY(g-3,g4) = 5
    c: DistanceY(g4,g9) = 2.8
    c: DistanceY(g9,g14) = 2.8
    c: DistanceY(g14,g19) = 2.8
    c: Coincident(g20,g21)
    c: Coincident(g21,g22)
    c: Coincident(g22,g23)
    c: Coincident(g23,g20)
    c: Horizontal(g20)
    c: Horizontal(g22)
    c: Vertical(g21)
    c: Vertical(g23)
    c: Symmetric(g22,g20,g24)
    c: Distance(g21,g23) = 2.4
    c: Distance(g20,g22) = 1.2
    c: DistanceY(g19,g24) = 2.8
    c: Vertical(g-3,g24)
FEATURE [PartDesign::Pocket] Pocket020
  BaseFeature = -> Pocket012
  Direction = (0,1,-2e-16)
  Length = 3.6
  Length2 = 5
  Profile = -> Sketch154
  ReferenceAxis = -> Sketch154 [N_Axis]
  Refine = true
  Suppressed = false
  Type = 0
FEATURE [PartDesign::Body] Body007  label="lato DX"
  AllowCompound = false
  Group = -> [Binder001,Sketch114,Pad011,Chamfer014,Sketch115,Pocket006,Sketch116,Pad012,Sketch117,Pocket007,Sketch118,Pad013,Sketch119,Pocket008,Pad017,Chamfer009,Pocket009,Sketch123,Sketch120,Pad014,Pad018,Chamfer008,Pocket010,Sketch121,Pad015,Sketch122,Pad016,SubtractivePipe004,SubtractivePipe005,Sketch149,Sketch148,Sketch124,Sketch125,Sketch126,Sketch129,Sketch130,Clone2D001,Sketch131,SubtractiveLoft002,+13 more]
  Origin = -> Origin007
  Tip = -> Pocket020
FEATURE [Sketcher::SketchObject] Sketch155  label="fermo per protezione batteria"
  ArcFitTolerance = 1e-06
  AttachmentSupport = -> [XZ_Plane]
  ExternalGeometry = -> [Sketch016,Sketch]
  FullyConstrained = true
  MakeInternals = false
  MapMode = 5
  Placement = pos=(0,0,0) rot=(1,0,0;1.5708rad)
  sketch-geometry (5):
    g0: LineSegment StartX=-183.305 StartY=-76.0316 StartZ=0 EndX=-179.305 EndY=-76.0316 EndZ=0
    g1: LineSegment StartX=-179.305 StartY=-76.0316 StartZ=0 EndX=-179.305 EndY=-74.4316 EndZ=0
    g2: LineSegment StartX=-179.305 StartY=-74.4316 StartZ=0 EndX=-183.305 EndY=-74.4316 EndZ=0
    g3: LineSegment [constr] StartX=-183.305 StartY=-76.0316 StartZ=0 EndX=-183.305 EndY=-78.4316 EndZ=0
    g4: LineSegment StartX=-183.305 StartY=-74.4316 StartZ=0 EndX=-183.305 EndY=-76.0316 EndZ=0
  constraints (16):
    c: Horizontal(g0)
    c: Distance(g1) = 1.6
    c: Coincident(g1,g0)
    c: Vertical(g1)
    c: Coincident(g2,g1)
    c: Horizontal(g2)
    c: Vertical(g3)
    c: PointOnObject(g3,g-4)
    c: Horizontal(g3,g0)
    c: Tangent(g3,g-3)
    c: Vertical(g0,g-3)
    c: Coincident(g4,g2)
    c: Coincident(g4,g0)
    c: Vertical(g4)
    c: Vertical(g0,g3)
    c: DistanceY(g3,g3) = 2.4
FEATURE [Part::Extrusion] Extrude089  label="Extrude089 - fermo per protezione batteria"
  Base = -> Sketch155
  Dir = (0,-1,2e-16)
  DirMode = 2
  FaceMakerClass = Part::FaceMakerBullseye
  FaceMakerMode = 3
  LengthFwd = 8
  LengthRev = 0
  Solid = true
  Symmetric = true
FEATURE [Sketcher::SketchObject] Sketch156  label="buco per protezione batteria"
  ArcFitTolerance = 1e-06
  AttachmentSupport = -> [XZ_Plane]
  ExternalGeometry = -> [Sketch,Sketch016]
  FullyConstrained = true
  MakeInternals = false
  MapMode = 5
  Placement = pos=(0,0,0) rot=(1,0,0;1.5708rad)
  sketch-geometry (5):
    g0: LineSegment [constr] StartX=-183.305 StartY=-76.8316 StartZ=0 EndX=-183.305 EndY=-78.4316 EndZ=0
    g1: LineSegment StartX=-200.305 StartY=-78.4316 StartZ=0 EndX=-200.305 EndY=-80.4316 EndZ=0
    g2: LineSegment StartX=-200.305 StartY=-80.4316 StartZ=0 EndX=-198.505 EndY=-80.4316 EndZ=0
    g3: LineSegment StartX=-198.505 StartY=-80.4316 StartZ=0 EndX=-198.505 EndY=-78.4316 EndZ=0
    g4: LineSegment StartX=-198.505 StartY=-78.4316 StartZ=0 EndX=-200.305 EndY=-78.4316 EndZ=0
  constraints (15):
    c: Vertical(g0)
    c: Tangent(g0,g-4)
    c: PointOnObject(g0,g-3)
    c: Horizontal(g0,g-4)
    c: Coincident(g1,g2)
    c: Coincident(g2,g3)
    c: Coincident(g3,g4)
    c: Coincident(g4,g1)
    c: Vertical(g1)
    c: Vertical(g3)
    c: Horizontal(g2)
    c: Distance(g1,g3) = 1.8
    c: Distance(g2,g4) = 2
    c: Tangent(g4,g-3)
    c: Distance(g3,g0) = 15.2
FEATURE [Part::Extrusion] Extrude090  label="Extrude090 - buco per protezione batteria"
  Base = -> Sketch156
  Dir = (0,-1,2e-16)
  DirMode = 2
  FaceMakerClass = Part::FaceMakerBullseye
  FaceMakerMode = 3
  LengthFwd = 4.8
  LengthRev = 0
  Solid = true
  Symmetric = true
FEATURE [Sketcher::SketchObject] Sketch157
  ArcFitTolerance = 1e-06
  AttachmentSupport = -> [XY_Plane010]
  FullyConstrained = true
  MakeInternals = false
  MapMode = 5
  sketch-geometry (9):
    g0: LineSegment [constr] StartX=1.8 StartY=8 StartZ=0 EndX=1.8 EndY=-8 EndZ=0
    g1: LineSegment StartX=1.8 StartY=8 StartZ=0 EndX=17 EndY=8 EndZ=0
    g2: LineSegment StartX=1.8 StartY=-8 StartZ=0 EndX=17 EndY=-8 EndZ=0
    g3: LineSegment StartX=0 StartY=8 StartZ=0 EndX=0 EndY=-8 EndZ=0
    g4: LineSegment StartX=1.8 StartY=8 StartZ=0 EndX=0 EndY=8 EndZ=0
    g5: LineSegment StartX=1.8 StartY=-8 StartZ=0 EndX=0 EndY=-8 EndZ=0
    g6: LineSegment StartX=17 StartY=8 StartZ=0 EndX=17 EndY=-8 EndZ=0
    g7: Circle CenterX=8.5 CenterY=0 CenterZ=0 NormalX=0 NormalY=0 NormalZ=1 AngleXU=0 Radius=5
    g8: LineSegment [constr] StartX=17 StartY=8 StartZ=0 EndX=17 EndY=0 EndZ=0
  constraints (23):
    c: DistanceY(g0,g0) = 16
    c: Distance(g1) = 15.2
    c: Coincident(g1,g0)
    c: Horizontal(g1)
    c: Coincident(g2,g0)
    c: Horizontal(g2)
    c: Equal(g1,g2)
    c: Symmetric(g0,g0,g-1)
    c: Equal(g3,g0)
    c: Coincident(g4,g0)
    c: Horizontal(g4)
    c: DistanceX(g4,g4) = 1.8
    c: Coincident(g5,g0)
    c: Horizontal(g5)
    c: Equal(g4,g5)
    c: Coincident(g3,g4)
    c: Tangent(g3,g-2)
    c: Coincident(g6,g1)
    c: Coincident(g6,g2)
    c: Coincident(g8,g1)
    c: Symmetric(g6,g6,g8)
    c: Symmetric(g8,g-1,g7)
    c: Diameter(g7) = 10
FEATURE [PartDesign::Pad] Pad031
  Direction = (0,0,1)
  Length = 1.4
  Length2 = 10
  Profile = -> Sketch157
  ReferenceAxis = -> Sketch157 [N_Axis]
  Refine = true
  Suppressed = false
  Type = 0
FEATURE [Sketcher::SketchObject] Sketch158
  ArcFitTolerance = 1e-06
  AttachmentSupport = -> [Pad031]
  ExternalGeometry = -> [Pad031]
  FullyConstrained = true
  MakeInternals = false
  MapMode = 5
  Placement = pos=(0,0,1.4) rot=(0,0,1;0rad)
  sketch-geometry (4):
    g0: LineSegment StartX=0 StartY=8 StartZ=0 EndX=0 EndY=-8 EndZ=0
    g1: LineSegment StartX=0 StartY=8 StartZ=0 EndX=1.8 EndY=8 EndZ=0
    g2: LineSegment StartX=1.8 StartY=8 StartZ=0 EndX=1.8 EndY=-8 EndZ=0
    g3: LineSegment StartX=0 StartY=-8 StartZ=0 EndX=1.8 EndY=-8 EndZ=0
  constraints (10):
    c: Coincident(g0,g-3)
    c: Coincident(g0,g-4)
    c: Distance(g1) = 1.8
    c: Coincident(g1,g0)
    c: PointOnObject(g1,g-3)
    c: Coincident(g2,g1)
    c: Vertical(g2)
    c: Coincident(g3,g0)
    c: PointOnObject(g3,g-4)
    c: Coincident(g3,g2)
FEATURE [PartDesign::Pad] Pad032
  BaseFeature = -> Pad031
  Direction = (0,0,1)
  Length = 6.4
  Length2 = 10
  Profile = -> Sketch158
  ReferenceAxis = -> Sketch158 [N_Axis]
  Refine = true
  Suppressed = false
  Type = 0
FEATURE [Sketcher::SketchObject] Sketch159
  ArcFitTolerance = 1e-06
  AttachmentSupport = -> [Pad032]
  ExternalGeometry = -> [Pad032,Pad031]
  FullyConstrained = true
  MakeInternals = false
  MapMode = 5
  Placement = pos=(0,0,7.8) rot=(0,0,1;0rad)
  sketch-geometry (7):
    g0: LineSegment StartX=0.1 StartY=2.2 StartZ=0 EndX=0.1 EndY=-2.2 EndZ=0
    g1: LineSegment StartX=0.1 StartY=-2.2 StartZ=0 EndX=1.7 EndY=-2.2 EndZ=0
    g2: LineSegment StartX=1.7 StartY=-2.2 StartZ=0 EndX=1.7 EndY=2.2 EndZ=0
    g3: LineSegment StartX=1.7 StartY=2.2 StartZ=0 EndX=0.1 EndY=2.2 EndZ=0
    g4: GeomPoint [constr] X=0.9 Y=8 Z=0
    g5: GeomPoint [constr] X=0.9 Y=-8 Z=0
    g6: LineSegment [constr] StartX=0.9 StartY=8 StartZ=0 EndX=0.9 EndY=-8 EndZ=0
  constraints (14):
    c: Coincident(g0,g1)
    c: Coincident(g1,g2)
    c: Coincident(g2,g3)
    c: Coincident(g3,g0)
    c: Vertical(g2)
    c: Horizontal(g1)
    c: Distance(g0,g2) = 1.6
    c: Distance(g1,g3) = 4.4
    c: Symmetric(g0,g0,g-1)
    c: Symmetric(g-4,g-4,g4)
    c: Symmetric(g-3,g-5,g5)
    c: Coincident(g6,g4)
    c: Coincident(g6,g5)
    c: Symmetric(g0,g2,g6)
FEATURE [PartDesign::Pad] Pad033
  BaseFeature = -> Pad032
  Direction = (0,0,1)
  Length = 1.4
  Length2 = 10
  Profile = -> Sketch159
  ReferenceAxis = -> Sketch159 [N_Axis]
  Refine = true
  Suppressed = false
  Type = 0
FEATURE [Part::Cut] Cut053
  Base = -> Cut052
  Refine = true
  Tool = -> Extrude089
FEATURE [Part::Cut] Cut054
  Base = -> Cut053
  Refine = true
  Tool = -> Extrude090
FEATURE [Sketcher::SketchObject] Sketch160
  ArcFitTolerance = 1e-06
  AttachmentSupport = -> [Pad033]
  ExternalGeometry = -> [Pad033]
  FullyConstrained = true
  MakeInternals = false
  MapMode = 5
  Placement = pos=(0,0,1.4) rot=(0,0,1;0rad)
  sketch-geometry (4):
    g0: LineSegment StartX=15.6 StartY=3.7 StartZ=0 EndX=15.6 EndY=-3.7 EndZ=0
    g1: LineSegment StartX=15.6 StartY=-3.7 StartZ=0 EndX=17 EndY=-3.7 EndZ=0
    g2: LineSegment StartX=17 StartY=-3.7 StartZ=0 EndX=17 EndY=3.7 EndZ=0
    g3: LineSegment StartX=17 StartY=3.7 StartZ=0 EndX=15.6 EndY=3.7 EndZ=0
  constraints (10):
    c: Coincident(g0,g1)
    c: Coincident(g1,g2)
    c: Coincident(g2,g3)
    c: Coincident(g3,g0)
    c: Horizontal(g1)
    c: Horizontal(g3)
    c: Distance(g0,g2) = 1.4
    c: Distance(g1,g3) = 7.4
    c: Symmetric(g0,g0,g-1)
    c: Tangent(g2,g-3)
FEATURE [PartDesign::Pad] Pad034
  BaseFeature = -> Pad033
  Direction = (0,0,1)
  Length = 2.4
  Length2 = 10
  Profile = -> Sketch160
  ReferenceAxis = -> Sketch160 [N_Axis]
  Refine = true
  Suppressed = false
  Type = 0
FEATURE [Sketcher::SketchObject] Sketch161
  ArcFitTolerance = 1e-06
  AttachmentSupport = -> [Pad034]
  ExternalGeometry = -> [Pad034]
  FullyConstrained = true
  MakeInternals = false
  MapMode = 5
  Placement = pos=(0,0,3.8) rot=(0,0,1;0rad)
  sketch-geometry (6):
    g0: LineSegment StartX=17 StartY=3.7 StartZ=0 EndX=21 EndY=3.7 EndZ=0
    g1: LineSegment StartX=17 StartY=3.7 StartZ=0 EndX=15.6 EndY=3.7 EndZ=0
    g2: LineSegment StartX=15.6 StartY=3.7 StartZ=0 EndX=15.6 EndY=-3.7 EndZ=0
    g3: LineSegment StartX=15.6 StartY=-3.7 StartZ=0 EndX=17 EndY=-3.7 EndZ=0
    g4: LineSegment StartX=17 StartY=-3.7 StartZ=0 EndX=21 EndY=-3.7 EndZ=0
    g5: LineSegment StartX=21 StartY=3.7 StartZ=0 EndX=21 EndY=-3.7 EndZ=0
  constraints (14):
    c: Distance(g0) = 4
    c: Coincident(g0,g-4)
    c: Horizontal(g0)
    c: Coincident(g1,g0)
    c: Coincident(g1,g-3)
    c: Coincident(g2,g1)
    c: Coincident(g2,g-5)
    c: Coincident(g3,g2)
    c: Coincident(g3,g-5)
    c: Coincident(g4,g3)
    c: Horizontal(g4)
    c: Equal(g4,g0)
    c: Coincident(g5,g0)
    c: Coincident(g5,g4)
FEATURE [PartDesign::Pad] Pad035
  BaseFeature = -> Pad034
  Direction = (0,0,1)
  Length = 1.4
  Length2 = 10
  Profile = -> Sketch161
  ReferenceAxis = -> Sketch161 [N_Axis]
  Refine = true
  Suppressed = false
  Type = 0
FEATURE [PartDesign::Body] Body010  label="Protezione_inferiore_batteria"
  AllowCompound = false
  Group = -> [Sketch157,Pad031,Sketch158,Pad032,Sketch159,Pad033,Sketch160,Pad034,Sketch161,Pad035]
  Origin = -> Origin010
  Tip = -> Pad035
FEATURE [Sketcher::SketchObject] Sketch162  label="scavo_saldature_nuovo_driver_alto"
  ArcFitTolerance = 1e-06
  AttachmentSupport = -> [XZ_Plane]
  ExternalGeometry = -> [Sketch138]
  FullyConstrained = true
  MakeInternals = false
  MapMode = 5
  Placement = pos=(0,0,0) rot=(1,0,0;1.5708rad)
  sketch-geometry (4):
    g0: LineSegment StartX=-192.503 StartY=17.8001 StartZ=0 EndX=-191.336 EndY=4.65187 EndZ=0
    g1: LineSegment StartX=-192.503 StartY=17.8001 StartZ=0 EndX=-190.909 EndY=17.9416 EndZ=0
    g2: LineSegment StartX=-190.909 StartY=17.9416 StartZ=0 EndX=-189.742 EndY=4.79337 EndZ=0
    g3: LineSegment StartX=-189.742 StartY=4.79337 StartZ=0 EndX=-191.336 EndY=4.65187 EndZ=0
  constraints (10):
    c: Parallel(g0,g-3)
    c: Equal(g0,g-3)
    c: Coincident(g1,g0)
    c: Perpendicular(g0,g1)
    c: Coincident(g1,g-3)
    c: Coincident(g2,g1)
    c: Coincident(g2,g-3)
    c: Coincident(g3,g2)
    c: Coincident(g3,g0)
    c: Distance(g1) = 1.6
FEATURE [PartDesign::Body] Body  label="Struttura pistola"
  AllowCompound = false
  Group = -> [Sketch,Sketch002,Sketch004,DatumPlane,Sketch005,DatumPlane001,CopyCut,Sketch008,Sketch009,Sketch010,Sketch011,Sketch012,Sketch013,Sketch014,Sketch015,Sketch016,Sketch017,Sketch018,Sketch019,Sketch020,Sketch022,Sketch023,Sketch024,Sketch025,Sketch026,Sketch027,Sketch029,Sketch030,Sketch031,Sketch032,Sketch033,Sketch034,Sketch035,Sketch036,Sketch037,Sketch038,Sketch039,Sketch040,Sketch041,Sketch042,+31 more]
  Origin = -> Origin
FEATURE [Part::Extrusion] Extrude091  label="Extrude091 - scavo_saldature_nuovo_driver_alto"
  Base = -> Sketch162
  Dir = (0,-1,2e-16)
  DirMode = 2
  FaceMakerClass = Part::FaceMakerBullseye
  FaceMakerMode = 3
  LengthFwd = 4
  LengthRev = 0
  Placement = pos=(0,-3.8,0) rot=(0,0,1;0rad)
  Solid = true
  Symmetric = false
FEATURE [Part::Cut] Cut055
  Base = -> Cut054
  Refine = true
  Tool = -> Extrude091
note: 2 file-system paths scrubbed to <path> (originals preserved in the JSON sidecar)
